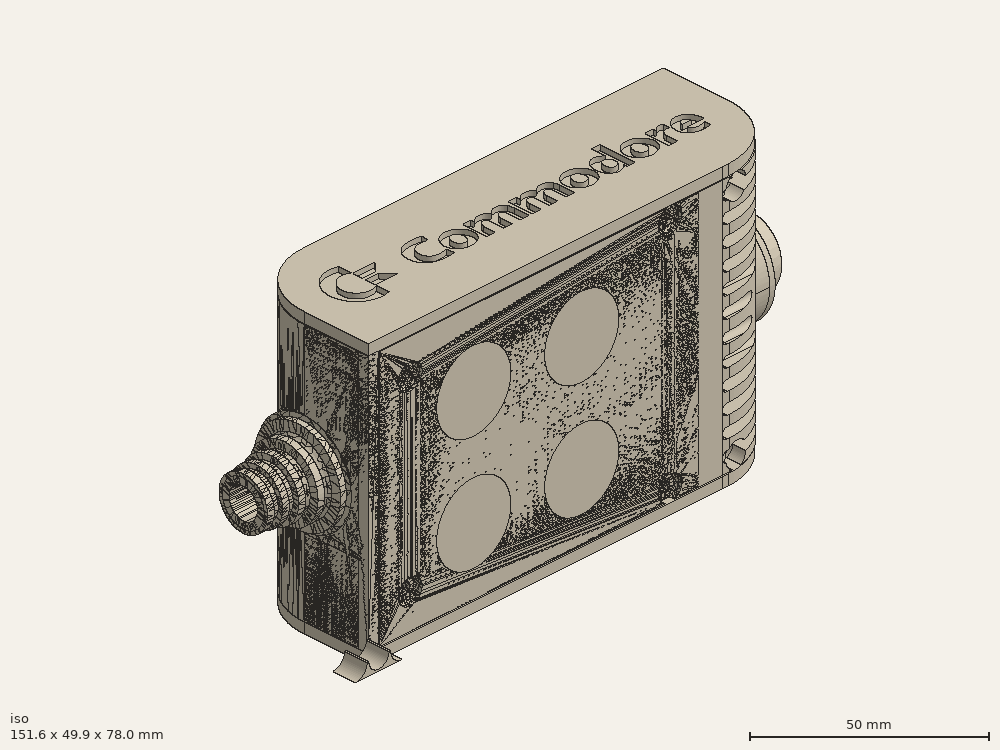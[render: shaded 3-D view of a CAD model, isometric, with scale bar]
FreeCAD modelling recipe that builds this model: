
FCSTD DOCUMENT  (FreeCAD 0.19R0.19.2)
Label: enclosure_213FCStd
License: All rights reserved
LicenseURL: http://en.wikipedia.org/wiki/All_rights_reserved
objects: Part::Revolution×152, Part::MultiFuse×146, Part::Feature×146, Sketcher::SketchObject×87, Part::Extrusion×72, Part::Cut×72, Part::Cylinder×70, Part::Fillet×58, Part::Box×36, App::MeasureDistance×4, Part::FeaturePython×2, Image::ImagePlane×1, PartDesign::Body×1, Part::Mirroring×1
note: 843 computed .brp shape members not serialized (recipe doc carries the construction recipe); baked Part::Feature solids carry a one-line shape summary decoded from their .brp

FEATURE [Sketcher::SketchObject] Sketch  label="topSketch"
  FullyConstrained = true
  sketch-geometry (20):
    g0: LineSegment StartX=5.21097e-06 StartY=3 StartZ=0 EndX=5.21097e-06 EndY=19 EndZ=0
    g1: ArcOfCircle CenterX=19 CenterY=19 CenterZ=0 NormalX=0 NormalY=0 NormalZ=1 AngleXU=0 Radius=19 StartAngle=1.5708 EndAngle=3.14159
    g2: ArcOfCircle CenterX=19 CenterY=19 CenterZ=0 NormalX=0 NormalY=0 NormalZ=1 AngleXU=0 Radius=16 StartAngle=1.5708 EndAngle=3.14159
    g3: LineSegment StartX=114 StartY=35 StartZ=0 EndX=19 EndY=35 EndZ=0
    g4: LineSegment StartX=5.21097e-06 StartY=3 StartZ=0 EndX=5.21097e-06 EndY=0 EndZ=0
    g5: LineSegment StartX=3 StartY=0 StartZ=0 EndX=5.21097e-06 EndY=0 EndZ=0
    g6: LineSegment StartX=3 StartY=19 StartZ=0 EndX=3 EndY=0 EndZ=0
    g7: LineSegment StartX=19 StartY=38 StartZ=0 EndX=124 EndY=38 EndZ=0
    g8: Circle CenterX=119 CenterY=35 CenterZ=0 NormalX=0 NormalY=0 NormalZ=1 AngleXU=0 Radius=1
    g9: Circle CenterX=121 CenterY=35 CenterZ=0 NormalX=0 NormalY=0 NormalZ=1 AngleXU=0 Radius=1
    g10: Circle CenterX=121 CenterY=33 CenterZ=0 NormalX=0 NormalY=0 NormalZ=1 AngleXU=0 Radius=1
    g11: BSplineCurve PolesCount=3 KnotsCount=2 Degree=2 IsPeriodic=0
    g12: GeomPoint X=119 Y=35 Z=0
    g13: GeomPoint X=121 Y=33 Z=0
    g14: LineSegment StartX=119 StartY=35 StartZ=0 EndX=114 EndY=35 EndZ=0
    g15: ArcOfCircle CenterX=105 CenterY=19 CenterZ=0 NormalX=0 NormalY=0 NormalZ=1 AngleXU=0 Radius=19 StartAngle=5.7297 EndAngle=6.28319
    g16: ArcOfCircle CenterX=105 CenterY=19 CenterZ=0 NormalX=0 NormalY=0 NormalZ=1 AngleXU=0 Radius=16 StartAngle=5.60905 EndAngle=6.28319
    g17: LineSegment StartX=121 StartY=33 StartZ=0 EndX=121 EndY=19 EndZ=0
    g18: LineSegment StartX=124 StartY=38 StartZ=0 EndX=124 EndY=19 EndZ=0
    g19: LineSegment StartX=117.5 StartY=9.01251 StartZ=0 EndX=121.163 EndY=9.0125 EndZ=0
  constraints (46):
    c: Vertical(g0)
    c: Block(g0)
    c: Coincident(g1,g0)
    c: Block(g1)
    c: Coincident(g2,g1)
    c: Block(g2)
    c: Coincident(g3,g2)
    c: Horizontal(g3)
    c: Tangent(g3,g2)
    c: Coincident(g4,g0)
    c: Distance(g4) = 3
    c: Vertical(g4)
    c: Coincident(g5,g4)
    c: Horizontal(g5)
    c: Coincident(g6,g2)
    c: Coincident(g6,g5)
    c: Vertical(g6)
    c: Horizontal(g7)
    c: Distance(g7) = 105
    c: Coincident(g7,g1)
    c: Block(g3)
    c: Weight(g8) = 1
    c: Equal(g8,g9)
    c: Equal(g8,g10)
    c: InternalAlignment(g8,g11)
    c: InternalAlignment(g9,g11)
    c: InternalAlignment(g10,g11)
    c: InternalAlignment(g12,g11)
    c: InternalAlignment(g13,g11)
    c: Block(g11)
    c: Coincident(g14,g11)
    c: Coincident(g14,g3)
    c: Horizontal(g14)
    c: Block(g15)
    c: Coincident(g16,g15)
    c: Block(g16)
    c: Coincident(g17,g11)
    c: Coincident(g17,g16)
    c: Vertical(g17)
    c: Distance(g17) = 14
    c: Coincident(g18,g7)
    c: Coincident(g18,g15)
    c: Vertical(g18)
    c: Distance(g18) = 19
    c: Coincident(g19,g16)
    c: Coincident(g19,g15)
FEATURE [Sketcher::SketchObject] Sketch001  label="bottomSketch"
  FullyConstrained = true
  sketch-geometry (32):
    g0: LineSegment StartX=3.3 StartY=-6.03275e-07 StartZ=0 EndX=98 EndY=-6.03275e-07 EndZ=0
    g1: ArcOfCircle CenterX=98 CenterY=19 CenterZ=0 NormalX=0 NormalY=0 NormalZ=1 AngleXU=0 Radius=19 StartAngle=4.71239 EndAngle=5.71103
    g2: LineSegment StartX=6.3 StartY=8 StartZ=0 EndX=3.3 EndY=8 EndZ=0
    g3: LineSegment StartX=3.3 StartY=8 StartZ=0 EndX=3.3 EndY=-6.03275e-07 EndZ=0
    g4: ArcOfCircle CenterX=8.3 CenterY=5 CenterZ=0 NormalX=0 NormalY=0 NormalZ=1 AngleXU=0 Radius=2 StartAngle=3.14159 EndAngle=4.71239
    g5: LineSegment StartX=6.3 StartY=8 StartZ=0 EndX=6.3 EndY=5 EndZ=0
    g6: ArcOfCircle CenterX=98 CenterY=19 CenterZ=0 NormalX=0 NormalY=0 NormalZ=1 AngleXU=0 Radius=12.7 StartAngle=4.71239 EndAngle=6.28319
    g7: LineSegment StartX=94.7 StartY=3 StartZ=0 EndX=8.3 EndY=3 EndZ=0
    g8-g12: Circle x5 (B-spline internal-alignment scaffolding for g13; pole/knot coordinates omitted)
    g13: BSplineCurve PolesCount=5 KnotsCount=3 Degree=3 IsPeriodic=0
    g14: GeomPoint X=98 Y=6.3 Z=0
    g15: GeomPoint X=96.3938 Y=4.71946 Z=0
    g16: GeomPoint X=94.7 Y=3 Z=0
    g17-g23: Circle x7 (B-spline internal-alignment scaffolding for g24; pole/knot coordinates omitted)
    g24: BSplineCurve PolesCount=7 KnotsCount=5 Degree=3 IsPeriodic=0
    g25-g29: GeomPoint x5 (B-spline internal-alignment scaffolding for g24; pole/knot coordinates omitted)
    g30: ArcOfCircle CenterX=98 CenterY=19 CenterZ=0 NormalX=0 NormalY=0 NormalZ=1 AngleXU=0 Radius=15.7 StartAngle=5.81226 EndAngle=6.28319
    g31: LineSegment StartX=110.7 StartY=19 StartZ=0 EndX=113.7 EndY=19 EndZ=0
  constraints (41):
    c: Horizontal(g0)
    c: Coincident(g1,g0)
    c: Block(g1)
    c: Horizontal(g2)
    c: Distance(g2) = 3
    c: Coincident(g3,g2)
    c: Vertical(g3)
    c: Coincident(g3,g0)
    c: Block(g4)
    c: Block(g2)
    c: Coincident(g5,g2)
    c: Coincident(g5,g4)
    c: Vertical(g5)
    c: Coincident(g6,g1)
    c: Block(g6)
    c: Coincident(g7,g4)
    c: Horizontal(g7)
    c: Block(g0)
    c: Block(g7)
    c: Block(g3)
    c: Coincident(g13,g6)
    c: Weight(g8) = 1
    c: Equal(g8, g9-g12) x4
    c: Coincident(g13,g7)
    c: InternalAlignment(g8-g12 -> g13) x5
    c: InternalAlignment(g14,g13)
    c: InternalAlignment(g15,g13)
    c: InternalAlignment(g16,g13)
    c: Block(g13)
    c: Weight(g17) = 1
    c: Equal(g17, g18-g23) x6
    c: Coincident(g24,g1)
    c: InternalAlignment(g17-g23 -> g24) x7
    c: InternalAlignment(g25-g29 -> g24) x5
    c: Block(g24)
    c: Coincident(g30,g24)
    c: Coincident(g31,g6)
    c: Coincident(g31,g30)
    c: Horizontal(g31)
    c: Block(g31)
    c: Block(g30)
FEATURE [Part::Extrusion] Extrude  label="top"
  Base = -> Sketch
  Dir = (0,0,1)
  DirMode = 2
  FaceMakerClass = Part::FaceMakerBullseye
  LengthFwd = 72
  LengthRev = 0
  Solid = true
  Symmetric = false
FEATURE [Part::Extrusion] Extrude001  label="bottom"
  Base = -> Sketch001
  Dir = (0,0,1)
  DirMode = 2
  FaceMakerClass = Part::FaceMakerBullseye
  LengthFwd = 71.4
  LengthRev = 0
  Placement = pos=(0,0,0.3) rot=(0,0,1;0rad)
  Solid = true
  Symmetric = false
FEATURE [Sketcher::SketchObject] Sketch002  label="topSketch001"
  FullyConstrained = true
  sketch-geometry (8):
    g0: ArcOfCircle CenterX=19 CenterY=19.0975 CenterZ=0 NormalX=0 NormalY=0 NormalZ=1 AngleXU=0 Radius=18.9025 StartAngle=1.5708 EndAngle=3.14674
    g1: LineSegment StartX=0.0977805 StartY=19.0003 StartZ=0 EndX=0.0977805 EndY=0.000251602 EndZ=0
    g2: LineSegment StartX=19 StartY=38 StartZ=0 EndX=124 EndY=38 EndZ=0
    g3: LineSegment StartX=0.0977805 StartY=0.000251602 StartZ=0 EndX=105.098 EndY=0.000251602 EndZ=0
    g4: LineSegment StartX=124 StartY=38 StartZ=0 EndX=125.616 EndY=38 EndZ=0
    g5: LineSegment StartX=105.098 StartY=0.000251602 StartZ=0 EndX=106.713 EndY=0.000251602 EndZ=0
    g6: ArcOfCircle CenterX=106.616 CenterY=19 CenterZ=0 NormalX=0 NormalY=0 NormalZ=1 AngleXU=0 Radius=19 StartAngle=4.71754 EndAngle=6.28319
    g7: LineSegment StartX=125.616 StartY=38 StartZ=0 EndX=125.616 EndY=19 EndZ=0
  constraints (21):
    c: Block(g0)
    c: Coincident(g1,g0)
    c: Vertical(g1)
    c: Horizontal(g2)
    c: Distance(g2) = 105
    c: Coincident(g2,g0)
    c: Distance(g1) = 19
    c: Coincident(g3,g1)
    c: Horizontal(g3)
    c: Distance(g3) = 105
    c: Coincident(g4,g2)
    c: Horizontal(g4)
    c: Distance(g4) = 1.61553
    c: Horizontal(g5)
    c: Equal(g4,g5) = 1.61553
    c: Coincident(g5,g3)
    c: Block(g6)
    c: Coincident(g6,g5)
    c: Coincident(g7,g4)
    c: Coincident(g7,g6)
    c: Vertical(g7)
FEATURE [Part::Extrusion] Extrude002  label="sideA"
  Base = -> Sketch002
  Dir = (0,0,1)
  DirMode = 2
  FaceMakerClass = Part::FaceMakerBullseye
  LengthFwd = 3
  LengthRev = 0
  Placement = pos=(0,0,-3) rot=(0,0,1;0rad)
  Solid = true
  Symmetric = false
FEATURE [Sketcher::SketchObject] Sketch003  label="topSketch002"
  FullyConstrained = true
  sketch-geometry (6):
    g0: LineSegment StartX=19 StartY=38 StartZ=0 EndX=117 EndY=38 EndZ=0
    g1: ArcOfCircle CenterX=19 CenterY=19 CenterZ=0 NormalX=0 NormalY=0 NormalZ=1 AngleXU=0 Radius=19 StartAngle=1.5708 EndAngle=3.14159
    g2: LineSegment StartX=117 StartY=38 StartZ=0 EndX=117 EndY=19 EndZ=0
    g3: LineSegment StartX=98 StartY=1.0161e-12 StartZ=0 EndX=5.22862e-06 EndY=1.0161e-12 EndZ=0
    g4: LineSegment StartX=5.22862e-06 StartY=19 StartZ=0 EndX=5.22862e-06 EndY=1.0161e-12 EndZ=0
    g5: ArcOfCircle CenterX=98 CenterY=19 CenterZ=0 NormalX=0 NormalY=0 NormalZ=1 AngleXU=0 Radius=19 StartAngle=4.71239 EndAngle=6.28319
  constraints (16):
    c: Horizontal(g0)
    c: Distance(g0) = 98
    c: Coincident(g1,g0)
    c: Block(g1)
    c: Coincident(g2,g0)
    c: Vertical(g2)
    c: Distance(g2) = 19
    c: Horizontal(g3)
    c: Coincident(g4,g1)
    c: Vertical(g4)
    c: Coincident(g3,g4)
    c: Block(g3)
    c: Coincident(g5,g2)
    c: Coincident(g5,g3)
    c: Block(g0)
    c: Block(g5)
FEATURE [Sketcher::SketchObject] Sketch004
  FullyConstrained = true
  MapMode = 3
  Placement = pos=(0,0,0) rot=(1,0,0;1.5708rad)
  Support = -> [Extrude]
  sketch-geometry (8):
    g0: Circle CenterX=80.351 CenterY=-67.6202 CenterZ=0 NormalX=0 NormalY=0 NormalZ=1 AngleXU=0 Radius=2
    g1: Circle CenterX=80.351 CenterY=-67.6202 CenterZ=0 NormalX=0 NormalY=0 NormalZ=1 AngleXU=0 Radius=3
    g2: Circle CenterX=80.351 CenterY=-4.92017 CenterZ=0 NormalX=0 NormalY=0 NormalZ=1 AngleXU=0 Radius=2
    g3: Circle CenterX=80.351 CenterY=-4.92017 CenterZ=0 NormalX=0 NormalY=0 NormalZ=1 AngleXU=0 Radius=3
    g4: Circle CenterX=23.851 CenterY=-4.92017 CenterZ=0 NormalX=0 NormalY=0 NormalZ=1 AngleXU=0 Radius=2
    g5: Circle CenterX=23.851 CenterY=-4.92017 CenterZ=0 NormalX=0 NormalY=0 NormalZ=1 AngleXU=0 Radius=3
    g6: Circle CenterX=23.851 CenterY=-67.6202 CenterZ=0 NormalX=0 NormalY=0 NormalZ=1 AngleXU=0 Radius=2
    g7: Circle CenterX=23.851 CenterY=-67.6202 CenterZ=0 NormalX=0 NormalY=0 NormalZ=1 AngleXU=0 Radius=3
  constraints (8):
    c: Block(g3)
    c: Block(g2)
    c: Block(g1)
    c: Block(g0)
    c: Block(g6)
    c: Block(g7)
    c: Block(g4)
    c: Block(g5)
FEATURE [Part::Extrusion] Extrude004
  Base = -> Sketch004
  Dir = (0,-1,2e-16)
  DirMode = 2
  FaceMakerClass = Part::FaceMakerBullseye
  LengthFwd = 6
  LengthRev = 0
  Placement = pos=(0,9,0) rot=(0,0,1;0rad)
  Solid = true
  Symmetric = false
FEATURE [Sketcher::SketchObject] Sketch005
  FullyConstrained = true
  MapMode = 3
  Placement = pos=(0,0,0) rot=(1,0,0;1.5708rad)
  Support = -> [Extrude]
  sketch-geometry (8):
    g0: Circle CenterX=80.351 CenterY=-67.6202 CenterZ=0 NormalX=0 NormalY=0 NormalZ=1 AngleXU=0 Radius=3
    g1: Circle CenterX=80.351 CenterY=-4.92017 CenterZ=0 NormalX=0 NormalY=0 NormalZ=1 AngleXU=0 Radius=3
    g2: Circle CenterX=23.851 CenterY=-4.92017 CenterZ=0 NormalX=0 NormalY=0 NormalZ=1 AngleXU=0 Radius=3
    g3: Circle CenterX=23.851 CenterY=-67.6202 CenterZ=0 NormalX=0 NormalY=0 NormalZ=1 AngleXU=0 Radius=3
    g4: Circle CenterX=23.851 CenterY=-67.6202 CenterZ=0 NormalX=0 NormalY=0 NormalZ=1 AngleXU=0 Radius=5
    g5: Circle CenterX=80.351 CenterY=-67.6202 CenterZ=0 NormalX=0 NormalY=0 NormalZ=1 AngleXU=0 Radius=5
    g6: Circle CenterX=23.851 CenterY=-4.92017 CenterZ=0 NormalX=0 NormalY=0 NormalZ=1 AngleXU=0 Radius=5
    g7: Circle CenterX=80.351 CenterY=-4.92017 CenterZ=0 NormalX=0 NormalY=0 NormalZ=1 AngleXU=0 Radius=5
  constraints (8):
    c: Block(g1)
    c: Block(g0)
    c: Block(g3)
    c: Block(g2)
    c: Block(g5)
    c: Block(g4)
    c: Block(g6)
    c: Block(g7)
FEATURE [Part::Extrusion] Extrude005
  Base = -> Sketch005
  Dir = (0,-1,2e-16)
  DirMode = 2
  FaceMakerClass = Part::FaceMakerBullseye
  LengthFwd = 2
  LengthRev = 0
  Solid = true
  Symmetric = false
FEATURE [Sketcher::SketchObject] Sketch006
  FullyConstrained = true
  MapMode = 3
  Placement = pos=(0,0,0) rot=(1,0,0;1.5708rad)
  sketch-geometry (8):
    g0: Circle CenterX=80.351 CenterY=-67.6202 CenterZ=0 NormalX=0 NormalY=0 NormalZ=1 AngleXU=0 Radius=3
    g1: Circle CenterX=80.351 CenterY=-4.92017 CenterZ=0 NormalX=0 NormalY=0 NormalZ=1 AngleXU=0 Radius=3
    g2: Circle CenterX=23.851 CenterY=-4.92017 CenterZ=0 NormalX=0 NormalY=0 NormalZ=1 AngleXU=0 Radius=3
    g3: Circle CenterX=23.851 CenterY=-67.6202 CenterZ=0 NormalX=0 NormalY=0 NormalZ=1 AngleXU=0 Radius=3
    g4: Circle CenterX=23.851 CenterY=-67.6202 CenterZ=0 NormalX=0 NormalY=0 NormalZ=1 AngleXU=0 Radius=5
    g5: Circle CenterX=80.351 CenterY=-67.6202 CenterZ=0 NormalX=0 NormalY=0 NormalZ=1 AngleXU=0 Radius=5
    g6: Circle CenterX=23.851 CenterY=-4.92017 CenterZ=0 NormalX=0 NormalY=0 NormalZ=1 AngleXU=0 Radius=5
    g7: Circle CenterX=80.351 CenterY=-4.92017 CenterZ=0 NormalX=0 NormalY=0 NormalZ=1 AngleXU=0 Radius=5
  constraints (8):
    c: Block(g1)
    c: Block(g0)
    c: Block(g3)
    c: Block(g2)
    c: Block(g5)
    c: Block(g4)
    c: Block(g6)
    c: Block(g7)
FEATURE [Part::Extrusion] Extrude007
  Base = -> Sketch006
  Dir = (0,-1,2e-16)
  DirMode = 2
  FaceMakerClass = Part::FaceMakerBullseye
  LengthFwd = 2
  LengthRev = 0
  Solid = true
  Symmetric = false
FEATURE [Part::Fillet] Fillet
  Base = -> Extrude007
  Edges = 4 edges r=1.99: [Edge6,Edge12,Edge18,Edge24]
FEATURE [Part::Cut] Cut
  Base = -> Extrude005
  Placement = pos=(0,5,0) rot=(0,0,1;0rad)
  Tool = -> Fillet
FEATURE [Part::MultiFuse] Fusion  label="pCBScrews"
  Placement = pos=(-2.5,0,72.3) rot=(0,0,1;0rad)
  Shapes = -> [Extrude004,Cut]
FEATURE [App::MeasureDistance] Distance  label="Distance: 0.69 mm"
  Distance = 0.685967
  P1 = (24.0138,2.9647,0.3)
  P2 = (23.8901,3,-0.373787)
FEATURE [App::MeasureDistance] Distance001  label="Distance: 0.53 mm"
  Distance = 0.533607
  P1 = (80.2939,3,72.2334)
  P2 = (80.281,2.99661,71.7)
FEATURE [Part::Fillet] Fillet001
  Base = -> Extrude001
  Edges = 1 edges r=2.4: [Edge17]
FEATURE [Part::Fillet] Fillet002  label="bottom001"
  Base = -> Fillet001
  Edges = 1 edges r=2.4: [Edge36]
FEATURE [Part::Fillet] Fillet003  label="top001"
  Base = -> Extrude
  Edges = 1 edges r=2: [Edge1]
FEATURE [Sketcher::SketchObject] Sketch007
  FullyConstrained = true
  sketch-geometry (16):
    g0: LineSegment StartX=4 StartY=0 StartZ=0 EndX=4 EndY=2.4 EndZ=0
    g1: LineSegment StartX=4 StartY=2.4 StartZ=0 EndX=7 EndY=2.4 EndZ=0
    g2: LineSegment StartX=4 StartY=0 StartZ=0 EndX=5.7 EndY=0 EndZ=0
    g3: LineSegment StartX=5.7 StartY=0 StartZ=0 EndX=5.7 EndY=-5.6 EndZ=0
    g4-g8: Circle x5 (B-spline internal-alignment scaffolding for g9; pole/knot coordinates omitted)
    g9: BSplineCurve PolesCount=5 KnotsCount=3 Degree=3 IsPeriodic=0
    g10: GeomPoint X=7 Y=2.4 Z=0
    g11: GeomPoint X=10.4582 Y=-1.55472 Z=0
    g12: GeomPoint X=14 Y=-5.6 Z=0
    g13: LineSegment StartX=14 StartY=-5.6 StartZ=0 EndX=14 EndY=-14.1 EndZ=0
    g14: LineSegment StartX=14 StartY=-14.1 StartZ=0 EndX=6.5 EndY=-14.1 EndZ=0
    g15: LineSegment StartX=5.7 StartY=-5.6 StartZ=0 EndX=6.5 EndY=-14.1 EndZ=0
  constraints (28):
    c: Distance(g0) = 2.4
    c: Vertical(g0)
    c: Block(g0)
    c: Coincident(g1,g0)
    c: Horizontal(g1)
    c: Distance(g1) = 3
    c: Coincident(g2,g0)
    c: Horizontal(g2)
    c: Distance(g2) = 1.7
    c: Coincident(g3,g2)
    c: Vertical(g3)
    c: Distance(g3) = 5.6
    c: Coincident(g9,g1)
    c: Weight(g4) = 1
    c: Equal(g4, g5-g8) x4
    c: InternalAlignment(g4-g8 -> g9) x5
    c: InternalAlignment(g10,g9)
    c: InternalAlignment(g11,g9)
    c: InternalAlignment(g12,g9)
    c: Block(g9)
    c: Coincident(g13,g9)
    c: Vertical(g13)
    c: Distance(g13) = 8.5
    c: Coincident(g14,g13)
    c: Horizontal(g14)
    c: Distance(g14) = 7.5
    c: Coincident(g15,g3)
    c: Coincident(g15,g14)
FEATURE [Part::Feature] Face
  shape: bbox 10 x 16.5 x 2e-07 mm, 1 faces, 0 solids (baked)
FEATURE [Part::Revolution] Revolve  label="plugHousing"
  Angle = 360
  Axis = (0,1,0)
  Base = (0,0,0)
  FaceMakerClass = Part::FaceMakerBullseye
  Placement = pos=(0,0,36.15) rot=(0,0,1;0rad)
  Solid = false
  Source = -> Face
  Symmetric = false
FEATURE [Part::Feature] Face001
  shape: bbox 10 x 16.5 x 2e-07 mm, 1 faces, 0 solids (baked)
FEATURE [Part::Revolution] Revolve001  label="plugHousing001"
  Angle = 360
  Axis = (0,1,0)
  Base = (0,0,0)
  FaceMakerClass = Part::FaceMakerBullseye
  Placement = pos=(0,0,36.15) rot=(0,0,1;0rad)
  Solid = false
  Source = -> Face001
  Symmetric = false
FEATURE [Part::MultiFuse] Fusion001  label="plugHousing002"
  Placement = pos=(0,0,0) rot=(0,0,1;1.5708rad)
  Shapes = -> [Revolve001,Revolve]
FEATURE [Part::Feature] Face002
  shape: bbox 10 x 16.5 x 2e-07 mm, 1 faces, 0 solids (baked)
FEATURE [Part::Revolution] Revolve003  label="plugHousing005"
  Angle = 360
  Axis = (0,1,0)
  Base = (0,0,0)
  FaceMakerClass = Part::FaceMakerBullseye
  Placement = pos=(0,0,36.15) rot=(0,0,1;0rad)
  Solid = false
  Source = -> Face002
  Symmetric = false
FEATURE [Part::Feature] Face003
  shape: bbox 10 x 16.5 x 2e-07 mm, 1 faces, 0 solids (baked)
FEATURE [Part::Revolution] Revolve002  label="plugHousing003"
  Angle = 360
  Axis = (0,1,0)
  Base = (0,0,0)
  FaceMakerClass = Part::FaceMakerBullseye
  Placement = pos=(0,0,36.15) rot=(0,0,1;0rad)
  Solid = false
  Source = -> Face003
  Symmetric = false
FEATURE [Part::MultiFuse] Fusion002  label="plugHousing004"
  Placement = pos=(0,0,0) rot=(0,0,1;1.5708rad)
  Shapes = -> [Revolve002,Revolve003]
FEATURE [Part::MultiFuse] Fusion003  label="plugHousing006"
  Placement = pos=(0,19,0) rot=(0,0,1;3.14159rad)
  Shapes = -> [Fusion002,Fusion001]
FEATURE [Part::Feature] Face004
  shape: bbox 10 x 16.5 x 2e-07 mm, 1 faces, 0 solids (baked)
FEATURE [Part::Revolution] Revolve006  label="plugHousing010"
  Angle = 360
  Axis = (0,1,0)
  Base = (0,0,0)
  FaceMakerClass = Part::FaceMakerBullseye
  Placement = pos=(0,0,36.15) rot=(0,0,1;0rad)
  Solid = false
  Source = -> Face004
  Symmetric = false
FEATURE [Part::Feature] Face005
  shape: bbox 10 x 16.5 x 2e-07 mm, 1 faces, 0 solids (baked)
FEATURE [Part::Revolution] Revolve007  label="plugHousing011"
  Angle = 360
  Axis = (0,1,0)
  Base = (0,0,0)
  FaceMakerClass = Part::FaceMakerBullseye
  Placement = pos=(0,0,36.15) rot=(0,0,1;0rad)
  Solid = false
  Source = -> Face005
  Symmetric = false
FEATURE [Part::Feature] Face006
  shape: bbox 10 x 16.5 x 2e-07 mm, 1 faces, 0 solids (baked)
FEATURE [Part::Revolution] Revolve004  label="plugHousing007"
  Angle = 360
  Axis = (0,1,0)
  Base = (0,0,0)
  FaceMakerClass = Part::FaceMakerBullseye
  Placement = pos=(0,0,36.15) rot=(0,0,1;0rad)
  Solid = false
  Source = -> Face006
  Symmetric = false
FEATURE [Part::MultiFuse] Fusion004  label="plugHousing009"
  Placement = pos=(0,0,0) rot=(0,0,1;1.5708rad)
  Shapes = -> [Revolve004,Revolve007]
FEATURE [Part::Feature] Face007
  shape: bbox 10 x 16.5 x 2e-07 mm, 1 faces, 0 solids (baked)
FEATURE [Part::Revolution] Revolve005  label="plugHousing008"
  Angle = 360
  Axis = (0,1,0)
  Base = (0,0,0)
  FaceMakerClass = Part::FaceMakerBullseye
  Placement = pos=(0,0,36.15) rot=(0,0,1;0rad)
  Solid = false
  Source = -> Face007
  Symmetric = false
FEATURE [Part::MultiFuse] Fusion005  label="plugHousing012"
  Placement = pos=(0,0,0) rot=(0,0,1;1.5708rad)
  Shapes = -> [Revolve006,Revolve005]
FEATURE [Part::MultiFuse] Fusion006  label="plugHousing013"
  Placement = pos=(0,19,0) rot=(0,0,1;3.14159rad)
  Shapes = -> [Fusion005,Fusion004]
FEATURE [Part::MultiFuse] Fusion007  label="plugHousing014"
  Placement = pos=(122.621,0,-0.15) rot=(0,0,1;0rad)
  Shapes = -> [Fusion003,Fusion006]
FEATURE [Part::Cylinder] Cylinder002
  Angle = 360
  AttacherType = Attacher::AttachEngine3D
  Height = 20
  Placement = pos=(0,0,36.15) rot=(0,0,1;0rad)
  Radius = 4
FEATURE [Part::Cylinder] Cylinder003
  Angle = 360
  AttacherType = Attacher::AttachEngine3D
  Height = 10
  Placement = pos=(0,0,36.15) rot=(0,0,1;0rad)
  Radius = 4
FEATURE [Part::MultiFuse] Fusion009  label="removeToCreateHoleForPlugHousing"
  Placement = pos=(70,19,36.15) rot=(0,1,0;1.5708rad)
  Shapes = -> [Cylinder002,Cylinder003]
FEATURE [Part::Cylinder] Cylinder004
  Angle = 360
  AttacherType = Attacher::AttachEngine3D
  Height = 20
  Placement = pos=(0,0,36.15) rot=(0,0,1;0rad)
  Radius = 4
FEATURE [Part::Cylinder] Cylinder005
  Angle = 360
  AttacherType = Attacher::AttachEngine3D
  Height = 10
  Placement = pos=(0,0,36.15) rot=(0,0,1;0rad)
  Radius = 4
FEATURE [Part::MultiFuse] Fusion010  label="removeToCreateHoleForPlugHousing001"
  Placement = pos=(70,19,36.15) rot=(0,1,0;1.5708rad)
  Shapes = -> [Cylinder004,Cylinder005]
FEATURE [Part::Cut] Cut001
  Base = -> Fillet003
  Tool = -> Fusion010
FEATURE [Part::Cut] Cut002  label="Bottom"
  Base = -> Fillet002
  Tool = -> Fusion009
FEATURE [Part::Feature] Face008
  shape: bbox 10 x 16.5 x 2e-07 mm, 1 faces, 0 solids (baked)
FEATURE [Part::Revolution] Revolve011  label="plugHousing021"
  Angle = 360
  Axis = (0,1,0)
  Base = (0,0,0)
  FaceMakerClass = Part::FaceMakerBullseye
  Placement = pos=(0,0,36.15) rot=(0,0,1;0rad)
  Solid = false
  Source = -> Face008
  Symmetric = false
FEATURE [Part::Feature] Face009
  shape: bbox 10 x 16.5 x 2e-07 mm, 1 faces, 0 solids (baked)
FEATURE [Part::Revolution] Revolve012  label="plugHousing022"
  Angle = 360
  Axis = (0,1,0)
  Base = (0,0,0)
  FaceMakerClass = Part::FaceMakerBullseye
  Placement = pos=(0,0,36.15) rot=(0,0,1;0rad)
  Solid = false
  Source = -> Face009
  Symmetric = false
FEATURE [Part::Feature] Face010 .. Face013  x4 (patterned run collapsed; names and placements below)
  shape: bbox 10 x 16.5 x 2e-07 mm, 1 faces, 0 solids (baked)
FEATURE [Part::Revolution] Revolve015  label="plugHousing027"
  Angle = 360
  Axis = (0,1,0)
  Base = (0,0,0)
  FaceMakerClass = Part::FaceMakerBullseye
  Placement = pos=(0,0,36.15) rot=(0,0,1;0rad)
  Solid = false
  Source = -> Face013
  Symmetric = false
FEATURE [Part::Feature] Face014
  shape: bbox 10 x 16.5 x 2e-07 mm, 1 faces, 0 solids (baked)
FEATURE [Part::Feature] Face015
  shape: bbox 10 x 16.5 x 2e-07 mm, 1 faces, 0 solids (baked)
FEATURE [Part::Feature] Face016
  shape: bbox 10 x 16.5 x 2e-07 mm, 1 faces, 0 solids (baked)
FEATURE [Part::Revolution] Revolve019  label="plugHousing033"
  Angle = 360
  Axis = (0,1,0)
  Base = (0,0,0)
  FaceMakerClass = Part::FaceMakerBullseye
  Placement = pos=(0,0,36.15) rot=(0,0,1;0rad)
  Solid = false
  Source = -> Face016
  Symmetric = false
FEATURE [Part::Feature] Face017
  shape: bbox 10 x 16.5 x 2e-07 mm, 1 faces, 0 solids (baked)
FEATURE [Part::Revolution] Revolve020  label="plugHousing034"
  Angle = 360
  Axis = (0,1,0)
  Base = (0,0,0)
  FaceMakerClass = Part::FaceMakerBullseye
  Placement = pos=(0,0,36.15) rot=(0,0,1;0rad)
  Solid = false
  Source = -> Face017
  Symmetric = false
FEATURE [Part::Feature] Face018
  shape: bbox 10 x 16.5 x 2e-07 mm, 1 faces, 0 solids (baked)
FEATURE [Part::Revolution] Revolve016  label="plugHousing030"
  Angle = 360
  Axis = (0,1,0)
  Base = (0,0,0)
  FaceMakerClass = Part::FaceMakerBullseye
  Placement = pos=(0,0,36.15) rot=(0,0,1;0rad)
  Solid = false
  Source = -> Face018
  Symmetric = false
FEATURE [Part::MultiFuse] Fusion020  label="plugHousing038"
  Placement = pos=(0,0,0) rot=(0,0,1;1.5708rad)
  Shapes = -> [Revolve016,Revolve020]
FEATURE [Part::Feature] Face019
  shape: bbox 10 x 16.5 x 2e-07 mm, 1 faces, 0 solids (baked)
FEATURE [Part::Feature] Face020
  shape: bbox 10 x 16.5 x 2e-07 mm, 1 faces, 0 solids (baked)
FEATURE [Part::Revolution] Revolve017  label="plugHousing031"
  Angle = 360
  Axis = (0,1,0)
  Base = (0,0,0)
  FaceMakerClass = Part::FaceMakerBullseye
  Placement = pos=(0,0,36.15) rot=(0,0,1;0rad)
  Solid = false
  Source = -> Face020
  Symmetric = false
FEATURE [Part::MultiFuse] Fusion021  label="plugHousing039"
  Placement = pos=(0,0,0) rot=(0,0,1;1.5708rad)
  Shapes = -> [Revolve019,Revolve017]
FEATURE [Part::MultiFuse] Fusion023  label="plugHousing041"
  Placement = pos=(0,19,0) rot=(0,0,1;3.14159rad)
  Shapes = -> [Fusion021,Fusion020]
FEATURE [Part::Revolution] Revolve022  label="plugHousing043"
  Angle = 360
  Axis = (0,1,0)
  Base = (0,0,0)
  FaceMakerClass = Part::FaceMakerBullseye
  Placement = pos=(0,0,36.15) rot=(0,0,1;0rad)
  Solid = false
  Source = -> Face019
  Symmetric = false
FEATURE [Part::Feature] Face021
  shape: bbox 10 x 16.5 x 2e-07 mm, 1 faces, 0 solids (baked)
FEATURE [Part::Revolution] Revolve023  label="plugHousing044"
  Angle = 360
  Axis = (0,1,0)
  Base = (0,0,0)
  FaceMakerClass = Part::FaceMakerBullseye
  Placement = pos=(0,0,36.15) rot=(0,0,1;0rad)
  Solid = false
  Source = -> Face021
  Symmetric = false
FEATURE [Part::Feature] Face022
  shape: bbox 10 x 16.5 x 2e-07 mm, 1 faces, 0 solids (baked)
FEATURE [Part::Revolution] Revolve018  label="plugHousing032"
  Angle = 360
  Axis = (0,1,0)
  Base = (0,0,0)
  FaceMakerClass = Part::FaceMakerBullseye
  Placement = pos=(0,0,36.15) rot=(0,0,1;0rad)
  Solid = false
  Source = -> Face022
  Symmetric = false
FEATURE [Part::MultiFuse] Fusion022  label="plugHousing040"
  Placement = pos=(0,0,0) rot=(0,0,1;1.5708rad)
  Shapes = -> [Revolve018,Revolve023]
FEATURE [Part::Feature] Face023
  shape: bbox 10 x 16.5 x 2e-07 mm, 1 faces, 0 solids (baked)
FEATURE [Part::Revolution] Revolve021  label="plugHousing035"
  Angle = 360
  Axis = (0,1,0)
  Base = (0,0,0)
  FaceMakerClass = Part::FaceMakerBullseye
  Placement = pos=(0,0,36.15) rot=(0,0,1;0rad)
  Solid = false
  Source = -> Face023
  Symmetric = false
FEATURE [Part::MultiFuse] Fusion018  label="plugHousing036"
  Placement = pos=(0,0,0) rot=(0,0,1;1.5708rad)
  Shapes = -> [Revolve022,Revolve021]
FEATURE [Part::MultiFuse] Fusion019  label="plugHousing037"
  Placement = pos=(0,19,0) rot=(0,0,1;3.14159rad)
  Shapes = -> [Fusion018,Fusion022]
FEATURE [Part::MultiFuse] Fusion024  label="plugHousing042"
  Placement = pos=(122.621,0,-0.15) rot=(0,0,1;0rad)
  Shapes = -> [Fusion023,Fusion019]
FEATURE [Part::Cylinder] Cylinder006
  Angle = 360
  AttacherType = Attacher::AttachEngine3D
  Height = 20
  Placement = pos=(0,0,36.15) rot=(0,0,1;0rad)
  Radius = 14.3
FEATURE [Part::Cylinder] Cylinder007
  Angle = 360
  AttacherType = Attacher::AttachEngine3D
  Height = 10
  Placement = pos=(0,0,36.15) rot=(0,0,1;0rad)
  Radius = 4
FEATURE [Part::MultiFuse] Fusion026  label="removeToCreteHoleForPlugHousing"
  Placement = pos=(70,19,36) rot=(0,1,0;1.5708rad)
  Shapes = -> [Cylinder006,Cylinder007]
FEATURE [Part::Box] Box001  label="Cube001"
  AttacherType = Attacher::AttachEngine3D
  Height = 28
  Length = 3
  Placement = pos=(110.7,19,22) rot=(0,0,1;0rad)
  Width = 15.7
FEATURE [Part::Cut] Cut003  label="top002"
  Base = -> Cut001
  Tool = -> Fusion007
FEATURE [Part::Revolution] Revolve008  label="plugHousing015"
  Angle = 360
  Axis = (0,1,0)
  Base = (0,0,0)
  FaceMakerClass = Part::FaceMakerBullseye
  Placement = pos=(0,0,36.15) rot=(0,0,1;0rad)
  Solid = false
  Source = -> Face010
  Symmetric = false
FEATURE [Part::MultiFuse] Fusion013  label="plugHousing020"
  Placement = pos=(0,0,0) rot=(0,0,1;1.5708rad)
  Shapes = -> [Revolve008,Revolve012]
FEATURE [Part::Cut] Cut004  label="top003"
  Base = -> Cut003
  Placement = pos=(1,0,0) rot=(0,0,1;0rad)
  Tool = -> Fusion026
FEATURE [Part::Cylinder] Cylinder008
  Angle = 360
  AttacherType = Attacher::AttachEngine3D
  Height = 20
  Placement = pos=(0,0,36.15) rot=(0,0,1;0rad)
  Radius = 10.3
FEATURE [Part::Cylinder] Cylinder009
  Angle = 360
  AttacherType = Attacher::AttachEngine3D
  Height = 10
  Placement = pos=(0,0,36.15) rot=(0,0,1;0rad)
  Radius = 4
FEATURE [Part::MultiFuse] Fusion027  label="removeToCreteHoleForPlugHousing001"
  Placement = pos=(70,19,36) rot=(0,1,0;1.5708rad)
  Shapes = -> [Cylinder008,Cylinder009]
FEATURE [Part::Cut] Cut005  label="plugHousingTab"
  Base = -> Box001
  Tool = -> Fusion027
FEATURE [Part::MultiFuse] Fusion028  label="plugHousing045"
  Shapes = -> [Fusion024,Cut005]
FEATURE [Part::Box] Box002  label="Cube002"
  AttacherType = Attacher::AttachEngine3D
  Height = 28.8
  Length = 3
  Placement = pos=(107.3,28,21.6) rot=(0,0,1;0rad)
  Width = 7
FEATURE [Part::Box] Box003  label="Cube003"
  AttacherType = Attacher::AttachEngine3D
  Height = 3
  Length = 6.4
  Placement = pos=(107.3,28,18.6) rot=(0,0,1;0rad)
  Width = 7
FEATURE [Part::Box] Box004  label="Cube004"
  AttacherType = Attacher::AttachEngine3D
  Height = 3
  Length = 6.4
  Placement = pos=(107.3,28,50.4) rot=(0,0,1;0rad)
  Width = 7
FEATURE [Part::MultiFuse] Fusion029  label="plugHousingBracketHolder"
  Shapes = -> [Box004,Box002,Box003]
FEATURE [Part::Cylinder] Cylinder010
  Angle = 360
  AttacherType = Attacher::AttachEngine3D
  Height = 20
  Placement = pos=(0,0,36.15) rot=(0,0,1;0rad)
  Radius = 14.3
FEATURE [Part::Cylinder] Cylinder011
  Angle = 360
  AttacherType = Attacher::AttachEngine3D
  Height = 10
  Placement = pos=(0,0,36.15) rot=(0,0,1;0rad)
  Radius = 4
FEATURE [Part::MultiFuse] Fusion030  label="removeToCreteHoleForPlugHousing002"
  Placement = pos=(70,19,36) rot=(0,1,0;1.5708rad)
  Shapes = -> [Cylinder010,Cylinder011]
FEATURE [Part::Cut] Cut006  label="plugHousingBracketHolder001"
  Base = -> Fusion029
  Tool = -> Fusion030
FEATURE [Part::Cylinder] Cylinder012
  Angle = 360
  AttacherType = Attacher::AttachEngine3D
  Height = 20
  Placement = pos=(0,0,36.15) rot=(0,0,1;0rad)
  Radius = 7
FEATURE [Part::Cylinder] Cylinder013
  Angle = 360
  AttacherType = Attacher::AttachEngine3D
  Height = 10
  Placement = pos=(0,0,36.15) rot=(0,0,1;0rad)
  Radius = 4
FEATURE [Part::MultiFuse] Fusion032  label="removeToCreteHoleForPlugHousing003"
  Placement = pos=(70,19,36) rot=(0,1,0;1.5708rad)
  Shapes = -> [Cylinder012,Cylinder013]
FEATURE [Part::Cut] Cut007  label="bottom002"
  Base = -> Cut002
  Tool = -> Fusion032
FEATURE [Sketcher::SketchObject] Sketch008
  FullyConstrained = true
  sketch-geometry (54):
    g0: LineSegment StartX=-4.2 StartY=0 StartZ=0 EndX=-6.2 EndY=0 EndZ=0
    g1: LineSegment StartX=-14 StartY=-18 StartZ=0 EndX=-14 EndY=-26.5 EndZ=0
    g2: LineSegment StartX=-4.2 StartY=0 StartZ=0 EndX=-4.2 EndY=-13.4877 EndZ=0
    g3: Circle CenterX=-4.2 CenterY=-13.4877 CenterZ=0 NormalX=0 NormalY=0 NormalZ=1 AngleXU=0 Radius=1
    g4: Circle CenterX=-4.2 CenterY=-26.5 CenterZ=0 NormalX=0 NormalY=0 NormalZ=1 AngleXU=0 Radius=1
    g5: Circle CenterX=-8.2 CenterY=-26.5 CenterZ=0 NormalX=0 NormalY=0 NormalZ=1 AngleXU=0 Radius=1
    g6: BSplineCurve PolesCount=3 KnotsCount=2 Degree=2 IsPeriodic=0
    g7: GeomPoint X=-4.2 Y=-13.4877 Z=0
    g8: GeomPoint X=-8.2 Y=-26.5 Z=0
    g9: LineSegment StartX=-14 StartY=-26.5 StartZ=0 EndX=-8.2 EndY=-26.5 EndZ=0
    g10: LineSegment StartX=-10.15 StartY=-12 StartZ=0 EndX=-10.15 EndY=-14 EndZ=0
    g11: LineSegment StartX=-12.8401 StartY=-16 StartZ=0 EndX=-10.1571 EndY=-16 EndZ=0
    g12: LineSegment StartX=-10.15 StartY=-14 StartZ=0 EndX=-8.70761 EndY=-14 EndZ=0
    g13: LineSegment StartX=-12.8401 StartY=-16 StartZ=0 EndX=-12.8401 EndY=-17.6958 EndZ=0
    g14: LineSegment StartX=-10.15 StartY=-12 StartZ=0 EndX=-7.79258 EndY=-12 EndZ=0
    g15: Circle CenterX=-6.2215 CenterY=-2 CenterZ=0 NormalX=0 NormalY=0 NormalZ=1 AngleXU=0 Radius=1
    g16: Circle CenterX=-6.22762 CenterY=-2.58724 CenterZ=0 NormalX=0 NormalY=0 NormalZ=1 AngleXU=0 Radius=1
    g17: Circle CenterX=-6.32538 CenterY=-4 CenterZ=0 NormalX=0 NormalY=0 NormalZ=1 AngleXU=0 Radius=1
    g18: BSplineCurve PolesCount=3 KnotsCount=2 Degree=2 IsPeriodic=0
    g19: GeomPoint X=-6.2215 Y=-2 Z=0
    g20: GeomPoint X=-6.32538 Y=-4 Z=0
    g21: Circle CenterX=-6.48644 CenterY=-5.99526 CenterZ=0 NormalX=0 NormalY=0 NormalZ=1 AngleXU=0 Radius=1
    g22: Circle CenterX=-6.58486 CenterY=-6.99526 CenterZ=0 NormalX=0 NormalY=0 NormalZ=1 AngleXU=0 Radius=1
    g23: Circle CenterX=-6.77343 CenterY=-8 CenterZ=0 NormalX=0 NormalY=0 NormalZ=1 AngleXU=0 Radius=1
    g24: BSplineCurve PolesCount=3 KnotsCount=2 Degree=2 IsPeriodic=0
    g25: GeomPoint X=-6.48644 Y=-5.99526 Z=0
    g26: GeomPoint X=-6.77343 Y=-8 Z=0
    g27: Circle CenterX=-7.19003 CenterY=-10 CenterZ=0 NormalX=0 NormalY=0 NormalZ=1 AngleXU=0 Radius=1
    g28: Circle CenterX=-7.44407 CenterY=-11.0915 CenterZ=0 NormalX=0 NormalY=0 NormalZ=1 AngleXU=0 Radius=1
    g29: Circle CenterX=-7.79258 CenterY=-12 CenterZ=0 NormalX=0 NormalY=0 NormalZ=1 AngleXU=0 Radius=1
    g30: BSplineCurve PolesCount=3 KnotsCount=2 Degree=2 IsPeriodic=0
    g31: GeomPoint X=-7.19003 Y=-10 Z=0
    g32: GeomPoint X=-7.79258 Y=-12 Z=0
    g33: Circle CenterX=-8.70761 CenterY=-14 CenterZ=0 NormalX=0 NormalY=0 NormalZ=1 AngleXU=0 Radius=1
    g34: Circle CenterX=-9.33087 CenterY=-15.1837 CenterZ=0 NormalX=0 NormalY=0 NormalZ=1 AngleXU=0 Radius=1
    g35: Circle CenterX=-10.1571 CenterY=-16 CenterZ=0 NormalX=0 NormalY=0 NormalZ=1 AngleXU=0 Radius=1
    g36: BSplineCurve PolesCount=3 KnotsCount=2 Degree=2 IsPeriodic=0
    g37: GeomPoint X=-8.70761 Y=-14 Z=0
    g38: GeomPoint X=-10.1571 Y=-16 Z=0
    g39: Circle CenterX=-12.8401 CenterY=-17.6958 CenterZ=0 NormalX=0 NormalY=0 NormalZ=1 AngleXU=0 Radius=1
    g40: Circle CenterX=-13.3521 CenterY=-17.9027 CenterZ=0 NormalX=0 NormalY=0 NormalZ=1 AngleXU=0 Radius=1
    g41: Circle CenterX=-14 CenterY=-18 CenterZ=0 NormalX=0 NormalY=0 NormalZ=1 AngleXU=0 Radius=1
    g42: BSplineCurve PolesCount=3 KnotsCount=2 Degree=2 IsPeriodic=0
    g43: GeomPoint X=-12.8401 Y=-17.6958 Z=0
    g44: GeomPoint X=-14 Y=-18 Z=0
    g45: LineSegment StartX=-6.2 StartY=0 StartZ=0 EndX=-7.2 EndY=0 EndZ=0
    g46: LineSegment StartX=-7.2 StartY=0 StartZ=0 EndX=-7.2 EndY=-2 EndZ=0
    g47: LineSegment StartX=-7.2 StartY=-2 StartZ=0 EndX=-6.2215 EndY=-2 EndZ=0
    g48: LineSegment StartX=-6.32538 StartY=-4 StartZ=0 EndX=-7.65538 EndY=-4 EndZ=0
    g49: LineSegment StartX=-7.65538 StartY=-4 StartZ=0 EndX=-7.65538 EndY=-5.99526 EndZ=0
    g50: LineSegment StartX=-7.65538 StartY=-5.99526 StartZ=0 EndX=-6.48644 EndY=-5.99526 EndZ=0
    g51: LineSegment StartX=-6.77343 StartY=-8 StartZ=0 EndX=-8.43343 EndY=-8 EndZ=0
    g52: LineSegment StartX=-8.43343 StartY=-8 StartZ=0 EndX=-8.43343 EndY=-10 EndZ=0
    g53: LineSegment StartX=-8.43343 StartY=-10 StartZ=0 EndX=-7.19003 EndY=-10 EndZ=0
  constraints (112):
    c: Horizontal(g0)
    c: Distance(g0) = 2
    c: Block(g0)
    c: Vertical(g1)
    c: Coincident(g2,g0)
    c: Vertical(g2)
    c: Block(g2)
    c: Coincident(g6,g2)
    c: Weight(g3) = 1
    c: Equal(g3,g4)
    c: Equal(g3,g5)
    c: InternalAlignment(g3,g6)
    c: InternalAlignment(g4,g6)
    c: InternalAlignment(g5,g6)
    c: InternalAlignment(g7,g6)
    c: InternalAlignment(g8,g6)
    c: Block(g6)
    c: Coincident(g9,g1)
    c: Coincident(g9,g6)
    c: Horizontal(g9)
    c: Vertical(g10)
    c: Block(g10)
    c: Horizontal(g11)
    c: Block(g11)
    c: Coincident(g12,g10)
    c: Horizontal(g12)
    c: Block(g12)
    c: Coincident(g13,g11)
    c: Vertical(g13)
    c: Block(g13)
    c: Coincident(g14,g10)
    c: Horizontal(g14)
    c: Block(g14)
    c: Block(g9)
    c: Block(g1)
    c: Weight(g15) = 1
    c: Equal(g15,g16)
    c: Equal(g15,g17)
    c: InternalAlignment(g15,g18)
    c: InternalAlignment(g16,g18)
    c: InternalAlignment(g17,g18)
    c: InternalAlignment(g19,g18)
    c: InternalAlignment(g20,g18)
    c: Weight(g21) = 1
    c: Equal(g21,g22)
    c: Equal(g21,g23)
    c: InternalAlignment(g21,g24)
    c: InternalAlignment(g22,g24)
    c: InternalAlignment(g23,g24)
    c: InternalAlignment(g25,g24)
    c: InternalAlignment(g26,g24)
    c: Weight(g27) = 1
    c: Equal(g27,g28)
    c: Equal(g27,g29)
    c: Coincident(g30,g14)
    c: InternalAlignment(g27,g30)
    c: InternalAlignment(g28,g30)
    c: InternalAlignment(g29,g30)
    c: InternalAlignment(g31,g30)
    c: InternalAlignment(g32,g30)
    c: Coincident(g36,g12)
    c: Weight(g33) = 1
    c: Equal(g33,g34)
    c: Equal(g33,g35)
    c: Coincident(g36,g11)
    c: InternalAlignment(g33,g36)
    c: InternalAlignment(g34,g36)
    c: InternalAlignment(g35,g36)
    c: InternalAlignment(g37,g36)
    c: InternalAlignment(g38,g36)
    c: Coincident(g42,g13)
    c: Weight(g39) = 1
    c: Equal(g39,g40)
    c: Equal(g39,g41)
    c: Coincident(g42,g1)
    c: InternalAlignment(g39,g42)
    c: InternalAlignment(g40,g42)
    c: InternalAlignment(g41,g42)
    c: InternalAlignment(g43,g42)
    c: InternalAlignment(g44,g42)
    c: Block(g18)
    c: Block(g24)
    c: Block(g30)
    c: Block(g36)
    c: Block(g42)
    c: Horizontal(g45)
    c: Coincident(g45,g0)
    c: Vertical(g46)
    c: Coincident(g46,g45)
    c: Coincident(g47,g46)
    c: Coincident(g47,g18)
    c: Horizontal(g47)
    c: Block(g46)
    c: Coincident(g48,g18)
    c: Horizontal(g48)
    c: Distance(g48) = 1.33
    c: Vertical(g49)
    c: Coincident(g49,g48)
    c: Coincident(g50,g49)
    c: Coincident(g50,g24)
    c: Horizontal(g50)
    c: Tangent(g50,g22)
    c: Horizontal(g51)
    c: Coincident(g51,g24)
    c: Block(g51)
    c: Vertical(g52)
    c: Block(g52)
    c: Coincident(g52,g51)
    c: Coincident(g53,g52)
    c: Coincident(g53,g30)
    c: Horizontal(g53)
    c: Distance(g1) = 8.5
FEATURE [Part::Feature] Face024
  shape: bbox 9.8 x 26.5 x 2e-07 mm, 1 faces, 0 solids (baked)
FEATURE [Part::Revolution] Revolve024
  Angle = 360
  Axis = (0,1,0)
  Base = (0,0,0)
  FaceMakerClass = Part::FaceMakerBullseye
  Placement = pos=(0,0,0) rot=(0,0,1;1.5708rad)
  Solid = false
  Source = -> Face024
  Symmetric = false
FEATURE [Part::Feature] Face025
  shape: bbox 9.8 x 26.5 x 2e-07 mm, 1 faces, 0 solids (baked)
FEATURE [Part::Revolution] Revolve025
  Angle = 360
  Axis = (0,1,0)
  Base = (0,0,0)
  FaceMakerClass = Part::FaceMakerBullseye
  Placement = pos=(0,0,0) rot=(0,0,1;1.5708rad)
  Solid = false
  Source = -> Face025
  Symmetric = false
FEATURE [Part::MultiFuse] Fusion033
  Placement = pos=(-18,19,36) rot=(0,0,1;0rad)
  Shapes = -> [Revolve025,Revolve024]
FEATURE [Part::Cylinder] Cylinder014
  Angle = 360
  AttacherType = Attacher::AttachEngine3D
  Height = 20
  Placement = pos=(0,0,36.15) rot=(0,0,1;0rad)
  Radius = 14.3
FEATURE [Part::Cylinder] Cylinder015
  Angle = 360
  AttacherType = Attacher::AttachEngine3D
  Height = 10
  Placement = pos=(0,0,36.15) rot=(0,0,1;0rad)
  Radius = 4
FEATURE [Part::MultiFuse] Fusion034  label="removeToCreteHoleForPlugHousing004"
  Placement = pos=(-42,19,36) rot=(0,1,0;1.5708rad)
  Shapes = -> [Cylinder014,Cylinder015]
FEATURE [Part::Cut] Cut008  label="top004"
  Base = -> Cut004
  Placement = pos=(-1,0,0) rot=(0,0,1;0rad)
  Tool = -> Fusion034
FEATURE [Part::Box] Box005  label="Cube005"
  AttacherType = Attacher::AttachEngine3D
  Height = 28
  Length = 3
  Placement = pos=(110.7,19,22) rot=(0,0,1;0rad)
  Width = 15.7
FEATURE [Part::Cylinder] Cylinder016
  Angle = 360
  AttacherType = Attacher::AttachEngine3D
  Height = 10
  Placement = pos=(0,0,36.15) rot=(0,0,1;0rad)
  Radius = 4
FEATURE [Part::Cylinder] Cylinder017
  Angle = 360
  AttacherType = Attacher::AttachEngine3D
  Height = 20
  Placement = pos=(0,0,36.15) rot=(0,0,1;0rad)
  Radius = 10.3
FEATURE [Part::MultiFuse] Fusion035  label="removeToCreteHoleForPlugHousing005"
  Placement = pos=(70,19,36) rot=(0,1,0;1.5708rad)
  Shapes = -> [Cylinder017,Cylinder016]
FEATURE [Part::Cut] Cut009  label="plugHousingTab001"
  Base = -> Box005
  Placement = pos=(-107.4,-14,0) rot=(0,0,1;0rad)
  Tool = -> Fusion035
FEATURE [Part::Box] Box006  label="Cube006"
  AttacherType = Attacher::AttachEngine3D
  Height = 28
  Length = 3
  Placement = pos=(110.7,19,22) rot=(0,0,1;0rad)
  Width = 15.7
FEATURE [Part::Cylinder] Cylinder018
  Angle = 360
  AttacherType = Attacher::AttachEngine3D
  Height = 10
  Placement = pos=(0,0,36.15) rot=(0,0,1;0rad)
  Radius = 4
FEATURE [Part::Cylinder] Cylinder019
  Angle = 360
  AttacherType = Attacher::AttachEngine3D
  Height = 20
  Placement = pos=(0,0,36.15) rot=(0,0,1;0rad)
  Radius = 10.3
FEATURE [Part::MultiFuse] Fusion036  label="removeToCreteHoleForPlugHousing006"
  Placement = pos=(70,19,36) rot=(0,1,0;1.5708rad)
  Shapes = -> [Cylinder019,Cylinder018]
FEATURE [Part::Cut] Cut010  label="plugHousingTab002"
  Base = -> Box006
  Placement = pos=(-107.4,-14,0) rot=(0,0,1;0rad)
  Tool = -> Fusion036
FEATURE [Part::MultiFuse] Fusion037
  Placement = pos=(9.6,23,0) rot=(0,0,1;3.14159rad)
  Shapes = -> [Cut009,Cut010]
FEATURE [Part::Box] Box  label="Cube"
  AttacherType = Attacher::AttachEngine3D
  Height = 10
  Length = 3
  Placement = pos=(3.3,4,12) rot=(0,0,1;0rad)
  Width = 10
FEATURE [Part::Fillet] Fillet004
  Base = -> Fusion028
  Edges = 1 edges r=2: [Edge25]
FEATURE [Part::Fillet] Fillet005  label="plugHousing046"
  Base = -> Fillet004
  Edges = 1 edges r=2: [Edge8]
FEATURE [Part::Fillet] Fillet006
  Base = -> Box
  Edges = 1 edges r=2: [Edge11]
FEATURE [Part::Box] Box007  label="Cube007"
  AttacherType = Attacher::AttachEngine3D
  Height = 10
  Length = 3
  Placement = pos=(3.3,4,50) rot=(0,0,1;0rad)
  Width = 10
FEATURE [Part::Fillet] Fillet007
  Base = -> Box007
  Edges = 1 edges r=2: [Edge12]
FEATURE [Part::Box] Box008  label="Cube008"
  AttacherType = Attacher::AttachEngine3D
  Height = 28
  Length = 4
  Placement = pos=(5,0,22) rot=(0,0,1;0rad)
  Width = 10
FEATURE [Part::Fillet] Fillet008
  Base = -> Box008
  Edges = 1 edges r=1: [Edge7]
FEATURE [Part::Fillet] Fillet009
  Base = -> Fillet008
  Edges = 1 edges r=2: [Edge5]
FEATURE [Part::Fillet] Fillet010
  Base = -> Fillet009
  Edges = 1 edges r=2: [Edge2]
FEATURE [Sketcher::SketchObject] Sketch009  label="topSketch003"
  FullyConstrained = true
  sketch-geometry (4):
    g0: LineSegment StartX=16.8446 StartY=31.512 StartZ=0 EndX=16.3251 EndY=34.4666 EndZ=0
    g1: ArcOfCircle CenterX=19 CenterY=19.2524 CenterZ=0 NormalX=0 NormalY=0 NormalZ=1 AngleXU=0 Radius=15.4476 StartAngle=1.74483 EndAngle=2.72717
    g2: ArcOfCircle CenterX=19 CenterY=19.2524 CenterZ=0 NormalX=0 NormalY=0 NormalZ=1 AngleXU=0 Radius=12.4476 StartAngle=1.74483 EndAngle=2.73189
    g3: LineSegment StartX=4.86004 StartY=25.4725 StartZ=0 EndX=7.58253 EndY=24.2107 EndZ=0
  constraints (7):
    c: Block(g0)
    c: Coincident(g1,g0)
    c: Coincident(g2,g0)
    c: Coincident(g3,g1)
    c: Coincident(g3,g2)
    c: Block(g1)
    c: Block(g2)
FEATURE [Part::Extrusion] Extrude008
  Base = -> Sketch009
  Dir = (0,0,1)
  DirMode = 2
  FaceMakerClass = Part::FaceMakerBullseye
  LengthFwd = 10
  LengthRev = 0
  Placement = pos=(0,0,31) rot=(0,0,1;0rad)
  Solid = true
  Symmetric = false
FEATURE [Part::Cylinder] Cylinder020
  Angle = 360
  AttacherType = Attacher::AttachEngine3D
  Height = 20
  Placement = pos=(0,0,36.15) rot=(0,0,1;0rad)
  Radius = 8.2
FEATURE [Part::Cylinder] Cylinder021
  Angle = 360
  AttacherType = Attacher::AttachEngine3D
  Height = 10
  Placement = pos=(0,0,36.15) rot=(0,0,1;0rad)
  Radius = 4
FEATURE [Part::MultiFuse] Fusion038  label="removeToCreteHoleForPlugHousing007"
  Placement = pos=(-42,19,36) rot=(0,1,0;1.5708rad)
  Shapes = -> [Cylinder020,Cylinder021]
FEATURE [Part::Cut] Cut011
  Base = -> Extrude008
  Tool = -> Fusion038
FEATURE [Part::Fillet] Fillet011
  Base = -> Cut011
  Edges = 1 edges r=2: [Edge1]
FEATURE [Part::Fillet] Fillet012
  Base = -> Fillet011
  Edges = 1 edges r=2.5: [Edge1]
FEATURE [Part::Fillet] Fillet013
  Base = -> Fillet012
  Edges = 1 edges r=2.5: [Edge2]
FEATURE [Part::Box] Box010  label="Cube010"
  AttacherType = Attacher::AttachEngine3D
  Height = 16
  Length = 8
  Placement = pos=(12.7,31.52,28) rot=(0,0,1;0rad)
  Width = 4
FEATURE [Sketcher::SketchObject] Sketch010  label="topSketch004"
  FullyConstrained = true
  sketch-geometry (4):
    g0: LineSegment StartX=16.8446 StartY=31.512 StartZ=0 EndX=16.3251 EndY=34.4666 EndZ=0
    g1: ArcOfCircle CenterX=19 CenterY=19.2524 CenterZ=0 NormalX=0 NormalY=0 NormalZ=1 AngleXU=0 Radius=15.4476 StartAngle=1.74483 EndAngle=2.72717
    g2: ArcOfCircle CenterX=19 CenterY=19.2524 CenterZ=0 NormalX=0 NormalY=0 NormalZ=1 AngleXU=0 Radius=12.4476 StartAngle=1.74483 EndAngle=2.73189
    g3: LineSegment StartX=4.86004 StartY=25.4725 StartZ=0 EndX=7.58253 EndY=24.2107 EndZ=0
  constraints (7):
    c: Block(g0)
    c: Coincident(g1,g0)
    c: Coincident(g2,g0)
    c: Coincident(g3,g1)
    c: Coincident(g3,g2)
    c: Block(g1)
    c: Block(g2)
FEATURE [Part::Cylinder] Cylinder022
  Angle = 360
  AttacherType = Attacher::AttachEngine3D
  Height = 10
  Placement = pos=(0,0,36.15) rot=(0,0,1;0rad)
  Radius = 4
FEATURE [Sketcher::SketchObject] Sketch011  label="topSketch005"
  FullyConstrained = true
  sketch-geometry (4):
    g0: LineSegment StartX=16.8446 StartY=31.512 StartZ=0 EndX=16.3251 EndY=34.4666 EndZ=0
    g1: ArcOfCircle CenterX=19 CenterY=19.2524 CenterZ=0 NormalX=0 NormalY=0 NormalZ=1 AngleXU=0 Radius=15.4476 StartAngle=1.74483 EndAngle=2.72717
    g2: ArcOfCircle CenterX=19 CenterY=19.2524 CenterZ=0 NormalX=0 NormalY=0 NormalZ=1 AngleXU=0 Radius=12.4476 StartAngle=1.74483 EndAngle=2.73189
    g3: LineSegment StartX=4.86004 StartY=25.4725 StartZ=0 EndX=7.58253 EndY=24.2107 EndZ=0
  constraints (7):
    c: Block(g0)
    c: Coincident(g1,g0)
    c: Coincident(g2,g0)
    c: Coincident(g3,g1)
    c: Coincident(g3,g2)
    c: Block(g1)
    c: Block(g2)
FEATURE [Part::Extrusion] Extrude010
  Base = -> Sketch011
  Dir = (0,0,1)
  DirMode = 2
  FaceMakerClass = Part::FaceMakerBullseye
  LengthFwd = 10.6
  LengthRev = 0
  Placement = pos=(0,0,31) rot=(0,0,1;0rad)
  Solid = true
  Symmetric = false
FEATURE [Part::Cylinder] Cylinder023
  Angle = 360
  AttacherType = Attacher::AttachEngine3D
  Height = 20
  Placement = pos=(0,0,36.15) rot=(0,0,1;0rad)
  Radius = 8.2
FEATURE [Part::MultiFuse] Fusion039  label="removeToCreteHoleForPlugHousing008"
  Placement = pos=(-42,19,36) rot=(0,1,0;1.5708rad)
  Shapes = -> [Cylinder023,Cylinder022]
FEATURE [Part::Cut] Cut012
  Base = -> Extrude010
  Placement = pos=(0,0,-0.3) rot=(0,0,1;0rad)
  Tool = -> Fusion039
FEATURE [Part::Cut] Cut013
  Base = -> Box010
  Tool = -> Cut012
FEATURE [Part::Fillet] Fillet014
  Base = -> Cut013
  Edges = 1 edges r=0.7: [Edge13]
FEATURE [Part::Fillet] Fillet015
  Base = -> Fillet014
  Edges = 1 edges r=0.7: [Edge13]
FEATURE [Part::Fillet] Fillet016
  Base = -> Fillet015
  Edges = 1 edges r=0.7: [Edge16]
FEATURE [Part::Fillet] Fillet017
  Base = -> Fillet016
  Edges = 1 edges r=0.7: [Edge11]
FEATURE [Part::Fillet] Fillet018
  Base = -> Fillet017
  Edges = 1 edges r=0.7: [Edge10]
FEATURE [Part::Fillet] Fillet019
  Base = -> Fillet018
  Edges = 1 edges r=1.2: [Edge5]
FEATURE [Part::Fillet] Fillet020
  Base = -> Fillet019
  Edges = 1 edges r=1.2: [Edge12]
FEATURE [Part::Fillet] Fillet021
  Base = -> Fillet020
  Edges = 1 edges r=2: [Edge1]
  Placement = pos=(0.3,0,0) rot=(0,0,1;0rad)
FEATURE [Part::MultiFuse] Fusion040  label="top005"
  Shapes = -> [Cut008,Fillet021]
FEATURE [Part::MultiFuse] Fusion041  label="wireHolder"
  Shapes = -> [Fusion033,Fillet013]
FEATURE [Part::MultiFuse] Fusion042
  Shapes = -> [Fillet007,Fusion041]
FEATURE [Part::MultiFuse] Fusion043  label="wireHolder001"
  Shapes = -> [Fusion042,Fillet010]
FEATURE [Part::MultiFuse] Fusion044  label="wireHolder002"
  Shapes = -> [Fillet006,Fusion037,Fusion043]
FEATURE [Part::Feature] Face026
  shape: bbox 11 x 6 x 2e-07 mm, 1 faces, 0 solids (baked)
FEATURE [Part::Revolution] Revolve026
  Angle = 360
  Axis = (0,1,0)
  Base = (0,0,0)
  FaceMakerClass = Part::FaceMakerBullseye
  Placement = pos=(30.3,-1,19.7) rot=(0,0,1;0rad)
  Solid = false
  Source = -> Face026
  Symmetric = false
FEATURE [Sketcher::SketchObject] Sketch013  label="topSketch006"
  FullyConstrained = true
  sketch-geometry (13):
    g0: LineSegment StartX=117 StartY=19 StartZ=0 EndX=117 EndY=38 EndZ=0
    g1: ArcOfCircle CenterX=98 CenterY=19 CenterZ=0 NormalX=0 NormalY=0 NormalZ=1 AngleXU=0 Radius=19 StartAngle=5.7297 EndAngle=6.28319
    g2: LineSegment StartX=0 StartY=3 StartZ=0 EndX=0 EndY=19 EndZ=0
    g3: LineSegment StartX=19 StartY=38 StartZ=0 EndX=117 EndY=38 EndZ=0
    g4: ArcOfCircle CenterX=19 CenterY=19 CenterZ=0 NormalX=0 NormalY=0 NormalZ=1 AngleXU=0 Radius=19 StartAngle=1.5708 EndAngle=3.14159
    g5: ArcOfCircle CenterX=19 CenterY=19 CenterZ=0 NormalX=0 NormalY=0 NormalZ=1 AngleXU=0 Radius=16 StartAngle=1.5708 EndAngle=3.14159
    g6: ArcOfCircle CenterX=98 CenterY=19 CenterZ=0 NormalX=0 NormalY=0 NormalZ=1 AngleXU=0 Radius=16 StartAngle=5.60905 EndAngle=6.28319
    g7: LineSegment StartX=114 StartY=19 StartZ=0 EndX=114 EndY=35 EndZ=0
    g8: LineSegment StartX=110.5 StartY=9.01251 StartZ=0 EndX=114.163 EndY=9.01251 EndZ=0
    g9: LineSegment StartX=114 StartY=35 StartZ=0 EndX=19 EndY=35 EndZ=0
    g10: LineSegment StartX=0 StartY=3 StartZ=0 EndX=0 EndY=0 EndZ=0
    g11: LineSegment StartX=3 StartY=0 StartZ=0 EndX=0 EndY=0 EndZ=0
    g12: LineSegment StartX=3 StartY=19 StartZ=0 EndX=3 EndY=0 EndZ=0
  constraints (33):
    c: Vertical(g0)
    c: Distance(g0) = 19
    c: Block(g0)
    c: Coincident(g1,g0)
    c: Block(g1)
    c: Vertical(g2)
    c: Block(g2)
    c: Coincident(g3,g0)
    c: Horizontal(g3)
    c: Distance(g3) = 98
    c: Coincident(g4,g3)
    c: Coincident(g4,g2)
    c: Block(g4)
    c: Coincident(g5,g4)
    c: Coincident(g6,g1)
    c: Block(g6)
    c: Block(g5)
    c: Coincident(g7,g6)
    c: Vertical(g7)
    c: Coincident(g8,g6)
    c: Coincident(g8,g1)
    c: Coincident(g9,g7)
    c: Coincident(g9,g5)
    c: Horizontal(g9)
    c: Tangent(g9,g5)
    c: Coincident(g10,g2)
    c: Distance(g10) = 3
    c: Vertical(g10)
    c: Coincident(g11,g10)
    c: Horizontal(g11)
    c: Coincident(g12,g5)
    c: Coincident(g12,g11)
    c: Vertical(g12)
FEATURE [Part::Extrusion] Extrude011  label="top006"
  Base = -> Sketch013
  Dir = (0,0,1)
  DirMode = 2
  FaceMakerClass = Part::FaceMakerBullseye
  LengthFwd = 72
  LengthRev = 0
  Solid = true
  Symmetric = false
FEATURE [Sketcher::SketchObject] Sketch014
  FullyConstrained = true
  MapMode = 3
  Placement = pos=(0,0,0) rot=(1,0,0;1.5708rad)
  Support = -> [Extrude011]
  sketch-geometry (8):
    g0: Circle CenterX=80.351 CenterY=-67.6202 CenterZ=0 NormalX=0 NormalY=0 NormalZ=1 AngleXU=0 Radius=2
    g1: Circle CenterX=80.351 CenterY=-67.6202 CenterZ=0 NormalX=0 NormalY=0 NormalZ=1 AngleXU=0 Radius=3
    g2: Circle CenterX=80.351 CenterY=-4.92017 CenterZ=0 NormalX=0 NormalY=0 NormalZ=1 AngleXU=0 Radius=2
    g3: Circle CenterX=80.351 CenterY=-4.92017 CenterZ=0 NormalX=0 NormalY=0 NormalZ=1 AngleXU=0 Radius=3
    g4: Circle CenterX=23.851 CenterY=-4.92017 CenterZ=0 NormalX=0 NormalY=0 NormalZ=1 AngleXU=0 Radius=2
    g5: Circle CenterX=23.851 CenterY=-4.92017 CenterZ=0 NormalX=0 NormalY=0 NormalZ=1 AngleXU=0 Radius=3
    g6: Circle CenterX=23.851 CenterY=-67.6202 CenterZ=0 NormalX=0 NormalY=0 NormalZ=1 AngleXU=0 Radius=2
    g7: Circle CenterX=23.851 CenterY=-67.6202 CenterZ=0 NormalX=0 NormalY=0 NormalZ=1 AngleXU=0 Radius=3
  constraints (8):
    c: Block(g3)
    c: Block(g2)
    c: Block(g1)
    c: Block(g0)
    c: Block(g6)
    c: Block(g7)
    c: Block(g4)
    c: Block(g5)
FEATURE [Part::Feature] Face027
  shape: bbox 11 x 6 x 2e-07 mm, 1 faces, 0 solids (baked)
FEATURE [Part::Revolution] Revolve027
  Angle = 360
  Axis = (0,1,0)
  Base = (0,0,0)
  FaceMakerClass = Part::FaceMakerBullseye
  Placement = pos=(30.3,-1,51.7) rot=(0,0,1;0rad)
  Solid = false
  Source = -> Face027
  Symmetric = false
FEATURE [Part::Feature] Face028
  shape: bbox 11 x 6 x 2e-07 mm, 1 faces, 0 solids (baked)
FEATURE [Part::Revolution] Revolve028
  Angle = 360
  Axis = (0,1,0)
  Base = (0,0,0)
  FaceMakerClass = Part::FaceMakerBullseye
  Placement = pos=(62.3,-1,19.7) rot=(0,0,1;0rad)
  Solid = false
  Source = -> Face028
  Symmetric = false
FEATURE [Part::Feature] Face029
  shape: bbox 11 x 6 x 2e-07 mm, 1 faces, 0 solids (baked)
FEATURE [Part::Revolution] Revolve029
  Angle = 360
  Axis = (0,1,0)
  Base = (0,0,0)
  FaceMakerClass = Part::FaceMakerBullseye
  Placement = pos=(62.3,-1,51.7) rot=(0,0,1;0rad)
  Solid = false
  Source = -> Face029
  Symmetric = false
FEATURE [Part::Feature] Wire
  shape: bbox 11 x 5.2 x 2e-07 mm, 0 faces, 0 solids (baked)
FEATURE [Part::Revolution] Revolve030
  Angle = 360
  Axis = (0,1,0)
  Base = (0,0,0)
  FaceMakerClass = Part::FaceMakerBullseye
  Placement = pos=(30.3,38,19.7) rot=(0,0,1;0rad)
  Solid = true
  Source = -> Wire
  Symmetric = false
FEATURE [Part::Feature] Wire001
  shape: bbox 11 x 5.2 x 2e-07 mm, 0 faces, 0 solids (baked)
FEATURE [Part::Revolution] Revolve031
  Angle = 360
  Axis = (0,1,0)
  Base = (0,0,0)
  FaceMakerClass = Part::FaceMakerBullseye
  Placement = pos=(30.3,38,51.7) rot=(0,0,1;0rad)
  Solid = true
  Source = -> Wire001
  Symmetric = false
FEATURE [Part::Feature] Wire002
  shape: bbox 11 x 5.2 x 2e-07 mm, 0 faces, 0 solids (baked)
FEATURE [Part::Revolution] Revolve032
  Angle = 360
  Axis = (0,1,0)
  Base = (0,0,0)
  FaceMakerClass = Part::FaceMakerBullseye
  Placement = pos=(62.3,38,51.7) rot=(0,0,1;0rad)
  Solid = true
  Source = -> Wire002
  Symmetric = false
FEATURE [Part::Feature] Wire003
  shape: bbox 11 x 5.2 x 2e-07 mm, 0 faces, 0 solids (baked)
FEATURE [Part::Revolution] Revolve033
  Angle = 360
  Axis = (0,1,0)
  Base = (0,0,0)
  FaceMakerClass = Part::FaceMakerBullseye
  Placement = pos=(62.3,38,19.7) rot=(0,0,1;0rad)
  Solid = true
  Source = -> Wire003
  Symmetric = false
FEATURE [Part::MultiFuse] Fusion045  label="altRandScrewHousing"
  Shapes = -> [Revolve029,Revolve027,Revolve028,Revolve026]
FEATURE [Part::MultiFuse] Fusion046  label="fanScrewHousing"
  Shapes = -> [Revolve033,Revolve032,Revolve031,Revolve030]
FEATURE [Sketcher::SketchObject] Sketch015
  FullyConstrained = true
  sketch-geometry (17):
    g0: Circle CenterX=-3.5 CenterY=23.5 CenterZ=0 NormalX=0 NormalY=0 NormalZ=1 AngleXU=0 Radius=1
    g1: Circle CenterX=-1 CenterY=15.25 CenterZ=0 NormalX=0 NormalY=0 NormalZ=1 AngleXU=0 Radius=1
    g2: Circle CenterX=-3.5 CenterY=7 CenterZ=0 NormalX=0 NormalY=0 NormalZ=1 AngleXU=0 Radius=1
    g3: BSplineCurve PolesCount=3 KnotsCount=2 Degree=2 IsPeriodic=0
    g4: GeomPoint X=-3.5 Y=23.5 Z=0
    g5: GeomPoint X=-3.5 Y=7 Z=0
    g6: Circle CenterX=-4.8 CenterY=30.5 CenterZ=0 NormalX=0 NormalY=0 NormalZ=1 AngleXU=0 Radius=1
    g7: Circle CenterX=-3.5 CenterY=30.5 CenterZ=0 NormalX=0 NormalY=0 NormalZ=1 AngleXU=0 Radius=1
    g8: Circle CenterX=-3.5 CenterY=29.2 CenterZ=0 NormalX=0 NormalY=0 NormalZ=1 AngleXU=0 Radius=1
    g9: BSplineCurve PolesCount=3 KnotsCount=2 Degree=2 IsPeriodic=0
    g10: GeomPoint X=-4.8 Y=30.5 Z=0
    g11: GeomPoint X=-3.5 Y=29.2 Z=0
    g12: LineSegment StartX=-3.5 StartY=29.2 StartZ=0 EndX=-3.5 EndY=23.5 EndZ=0
    g13: LineSegment StartX=-4.8 StartY=30.5 StartZ=0 EndX=0 EndY=30.5 EndZ=0
    g14: LineSegment StartX=-3.5 StartY=0.3 StartZ=0 EndX=0 EndY=0.3 EndZ=0
    g15: LineSegment StartX=-3.5 StartY=0.3 StartZ=0 EndX=-3.5 EndY=7 EndZ=0
    g16: LineSegment StartX=0 StartY=0.3 StartZ=0 EndX=0 EndY=30.5 EndZ=0
  constraints (34):
    c: Weight(g0) = 1
    c: Equal(g0,g1)
    c: Equal(g0,g2)
    c: InternalAlignment(g0,g3)
    c: InternalAlignment(g1,g3)
    c: InternalAlignment(g2,g3)
    c: InternalAlignment(g4,g3)
    c: InternalAlignment(g5,g3)
    c: Block(g3)
    c: Weight(g6) = 1
    c: Equal(g6,g7)
    c: Equal(g6,g8)
    c: InternalAlignment(g6,g9)
    c: InternalAlignment(g7,g9)
    c: InternalAlignment(g8,g9)
    c: InternalAlignment(g10,g9)
    c: InternalAlignment(g11,g9)
    c: Block(g9)
    c: Coincident(g12,g9)
    c: Coincident(g12,g3)
    c: Vertical(g12)
    c: Coincident(g13,g9)
    c: Horizontal(g13)
    c: Distance(g13) = 4.8
    c: Horizontal(g14)
    c: Block(g14)
    c: Coincident(g15,g14)
    c: Coincident(g15,g3)
    c: Vertical(g15)
    c: Coincident(g16,g14)
    c: Coincident(g16,g13)
    c: Vertical(g16)
    c: Tangent(g16,g1)
    c: Distance(g14) = 3.5
FEATURE [Sketcher::SketchObject] Sketch016
  FullyConstrained = true
  sketch-geometry (16):
    g0: Circle CenterX=-3.5 CenterY=23.5 CenterZ=0 NormalX=0 NormalY=0 NormalZ=1 AngleXU=0 Radius=1
    g1: Circle CenterX=-1 CenterY=15.25 CenterZ=0 NormalX=0 NormalY=0 NormalZ=1 AngleXU=0 Radius=1
    g2: Circle CenterX=-3.5 CenterY=7 CenterZ=0 NormalX=0 NormalY=0 NormalZ=1 AngleXU=0 Radius=1
    g3: BSplineCurve PolesCount=3 KnotsCount=2 Degree=2 IsPeriodic=0
    g4: GeomPoint X=-3.5 Y=23.5 Z=0
    g5: GeomPoint X=-3.5 Y=7 Z=0
    g6: LineSegment StartX=-3.5 StartY=28.2 StartZ=0 EndX=-3.5 EndY=23.5 EndZ=0
    g7: LineSegment StartX=0 StartY=29.5 StartZ=0 EndX=0 EndY=30 EndZ=0
    g8: LineSegment StartX=-3.5 StartY=28.2 StartZ=0 EndX=-3.5 EndY=30 EndZ=0
    g9: LineSegment StartX=0 StartY=30 StartZ=0 EndX=0 EndY=30.5 EndZ=0
    g10: LineSegment StartX=0 StartY=30.5 StartZ=0 EndX=-3.5 EndY=30.5 EndZ=0
    g11: LineSegment StartX=-3.5 StartY=30.5 StartZ=0 EndX=-3.5 EndY=30 EndZ=0
    g12: LineSegment StartX=0 StartY=29.5 StartZ=0 EndX=0 EndY=5 EndZ=0
    g13: LineSegment StartX=-3.5 StartY=0.3 StartZ=0 EndX=-3.5 EndY=7 EndZ=0
    g14: LineSegment StartX=-3.5 StartY=0.3 StartZ=0 EndX=0 EndY=0.3 EndZ=0
    g15: LineSegment StartX=0 StartY=5 StartZ=0 EndX=0 EndY=0.3 EndZ=0
  constraints (39):
    c: Weight(g0) = 1
    c: Equal(g0,g1)
    c: Equal(g0,g2)
    c: InternalAlignment(g0,g3)
    c: InternalAlignment(g1,g3)
    c: InternalAlignment(g2,g3)
    c: InternalAlignment(g4,g3)
    c: InternalAlignment(g5,g3)
    c: Block(g3)
    c: Coincident(g6,g3)
    c: Vertical(g6)
    c: Vertical(g7)
    c: Distance(g7) = 0.5
    c: Coincident(g8,g6)
    c: Vertical(g8)
    c: Block(g6)
    c: Block(g7)
    c: Vertical(g9)
    c: Equal(g7,g9) = 0.5
    c: Block(g9)
    c: Coincident(g9,g7)
    c: Horizontal(g10)
    c: Coincident(g10,g9)
    c: Coincident(g11,g10)
    c: Coincident(g11,g8)
    c: Vertical(g11)
    c: Block(g11)
    c: Coincident(g12,g7)
    c: Vertical(g12)
    c: Coincident(g13,g3)
    c: Vertical(g13)
    c: Distance(g13) = 6.7
    c: Coincident(g14,g13)
    c: Horizontal(g14)
    c: Block(g14)
    c: Coincident(g15,g12)
    c: Coincident(g15,g14)
    c: Vertical(g15)
    c: Block(g15)
FEATURE [Sketcher::SketchObject] Sketch017
  FullyConstrained = true
  sketch-geometry (11):
    g0: LineSegment StartX=-3.5 StartY=1e-16 StartZ=0 EndX=-1.6 EndY=1e-16 EndZ=0
    g1: LineSegment StartX=-1.6 StartY=1e-16 StartZ=0 EndX=-1.6 EndY=1.5 EndZ=0
    g2: LineSegment StartX=-3.5 StartY=1.5 StartZ=0 EndX=-1.6 EndY=1.5 EndZ=0
    g3: LineSegment StartX=-3.5 StartY=1e-16 StartZ=0 EndX=-4.8 EndY=1e-16 EndZ=0
    g4: Circle CenterX=-3.5 CenterY=1.3 CenterZ=0 NormalX=0 NormalY=0 NormalZ=1 AngleXU=0 Radius=1
    g5: Circle CenterX=-3.5 CenterY=1e-16 CenterZ=0 NormalX=0 NormalY=0 NormalZ=1 AngleXU=0 Radius=1
    g6: Circle CenterX=-4.8 CenterY=1e-16 CenterZ=0 NormalX=0 NormalY=0 NormalZ=1 AngleXU=0 Radius=1
    g7: BSplineCurve PolesCount=3 KnotsCount=2 Degree=2 IsPeriodic=0
    g8: GeomPoint X=-3.5 Y=1.3 Z=0
    g9: GeomPoint X=-4.8 Y=1e-16 Z=0
    g10: LineSegment StartX=-3.5 StartY=1.3 StartZ=0 EndX=-3.5 EndY=1.5 EndZ=0
  constraints (24):
    c: Horizontal(g0)
    c: Distance(g0) = 1.9
    c: Block(g0)
    c: Coincident(g1,g0)
    c: Vertical(g1)
    c: Coincident(g2,g1)
    c: Horizontal(g2)
    c: Coincident(g3,g0)
    c: Horizontal(g3)
    c: Distance(g3) = 1.3
    c: Weight(g4) = 1
    c: Equal(g4,g5)
    c: Coincident(g5,g0)
    c: Equal(g4,g6)
    c: Coincident(g7,g3)
    c: InternalAlignment(g4,g7)
    c: InternalAlignment(g5,g7)
    c: InternalAlignment(g6,g7)
    c: InternalAlignment(g8,g7)
    c: InternalAlignment(g9,g7)
    c: Coincident(g10,g7)
    c: Coincident(g10,g2)
    c: Vertical(g10)
    c: Block(g10)
FEATURE [Part::Feature] Face035
  shape: bbox 3.2 x 1.5 x 2e-07 mm, 1 faces, 0 solids (baked)
FEATURE [Part::Revolution] Revolve039  label="backCaseScrewRetainer"
  Angle = 360
  Axis = (0,1,0)
  Base = (0,0,0)
  FaceMakerClass = Part::FaceMakerBullseye
  Placement = pos=(12.5,3,62) rot=(0,0,1;0rad)
  Solid = false
  Source = -> Face035
  Symmetric = false
FEATURE [Part::Feature] Face036
  shape: bbox 3.2 x 1.5 x 2e-07 mm, 1 faces, 0 solids (baked)
FEATURE [Part::Feature] Face039
  shape: bbox 4.8 x 30.2 x 2e-07 mm, 1 faces, 0 solids (baked)
FEATURE [Part::Revolution] Revolve043  label="frontCaseScrewPost002"
  Angle = 360
  Axis = (0,1,0)
  Base = (0,0,0)
  FaceMakerClass = Part::FaceMakerBullseye
  Placement = pos=(89.5,4.5,3.5) rot=(0,0,1;0rad)
  Solid = false
  Source = -> Face039
  Symmetric = false
FEATURE [Part::Feature] Face042
  shape: bbox 4.8 x 30.2 x 2e-07 mm, 1 faces, 0 solids (baked)
FEATURE [Part::Revolution] Revolve046  label="frontCaseScrewPost003"
  Angle = 360
  Axis = (0,1,0)
  Base = (0,0,0)
  FaceMakerClass = Part::FaceMakerBullseye
  Placement = pos=(89.5,4.5,68.5) rot=(0,0,1;0rad)
  Solid = false
  Source = -> Face042
  Symmetric = false
FEATURE [Part::Feature] Face043
  shape: bbox 3.2 x 1.5 x 2e-07 mm, 1 faces, 0 solids (baked)
FEATURE [Part::Revolution] Revolve047  label="frontCaseScrewRetainer002"
  Angle = 360
  Axis = (0,1,0)
  Base = (0,0,0)
  FaceMakerClass = Part::FaceMakerBullseye
  Placement = pos=(89.5,3,68.5) rot=(0,0,1;0rad)
  Solid = false
  Source = -> Face043
  Symmetric = false
FEATURE [Part::Feature] Face044
  shape: bbox 3.2 x 1.5 x 2e-07 mm, 1 faces, 0 solids (baked)
FEATURE [Part::Revolution] Revolve048  label="frontCaseScrewRetainer003"
  Angle = 360
  Axis = (0,1,0)
  Base = (0,0,0)
  FaceMakerClass = Part::FaceMakerBullseye
  Placement = pos=(89.5,3,3.5) rot=(0,0,1;0rad)
  Solid = false
  Source = -> Face044
  Symmetric = false
FEATURE [App::MeasureDistance] Distance002  label="Distance: 1.67 mm"
  Distance = 1.66921
  P1 = (99.2361,4.7524,71.7)
  P2 = (99.2347,6.42161,71.7)
FEATURE [Sketcher::SketchObject] Sketch018
  FullyConstrained = true
  sketch-geometry (7):
    g0: LineSegment StartX=0 StartY=0 StartZ=0 EndX=0 EndY=6 EndZ=0
    g1: Circle CenterX=0 CenterY=0 CenterZ=0 NormalX=0 NormalY=0 NormalZ=1 AngleXU=0 Radius=1
    g2: Circle CenterX=8 CenterY=6 CenterZ=0 NormalX=0 NormalY=0 NormalZ=1 AngleXU=0 Radius=1
    g3: BSplineCurve PolesCount=3 KnotsCount=2 Degree=2 IsPeriodic=0
    g4: GeomPoint X=0 Y=0 Z=0
    g5: GeomPoint X=8 Y=6 Z=0
    g6: LineSegment StartX=0 StartY=6 StartZ=0 EndX=8 EndY=6 EndZ=0
  constraints (14):
    c: Coincident(g0,g-1)
    c: Distance(g0) = 6
    c: Vertical(g0)
    c: Coincident(g3,g0)
    c: Weight(g1) = 1
    c: Equal(g1,g2)
    c: InternalAlignment(g1,g3)
    c: InternalAlignment(g2,g3)
    c: InternalAlignment(g4,g3)
    c: InternalAlignment(g5,g3)
    c: Block(g3)
    c: Coincident(g6,g0)
    c: Coincident(g6,g3)
    c: Horizontal(g6)
FEATURE [Part::Extrusion] Extrude012  label="caseScrewPillarBracket"
  Base = -> Sketch018
  Dir = (0,0,1)
  DirMode = 2
  FaceMakerClass = Part::FaceMakerBullseye
  LengthFwd = 2.4
  LengthRev = 0
  Placement = pos=(15.76,29,8.8) rot=(0,1,0;0rad)
  Solid = true
  Symmetric = false
FEATURE [Sketcher::SketchObject] Sketch019
  FullyConstrained = true
  sketch-geometry (7):
    g0: LineSegment StartX=0 StartY=0 StartZ=0 EndX=0 EndY=6 EndZ=0
    g1: Circle CenterX=0 CenterY=0 CenterZ=0 NormalX=0 NormalY=0 NormalZ=1 AngleXU=0 Radius=1
    g2: Circle CenterX=8 CenterY=6 CenterZ=0 NormalX=0 NormalY=0 NormalZ=1 AngleXU=0 Radius=1
    g3: BSplineCurve PolesCount=3 KnotsCount=2 Degree=2 IsPeriodic=0
    g4: GeomPoint X=0 Y=0 Z=0
    g5: GeomPoint X=8 Y=6 Z=0
    g6: LineSegment StartX=0 StartY=6 StartZ=0 EndX=8 EndY=6 EndZ=0
  constraints (14):
    c: Coincident(g0,g-1)
    c: Distance(g0) = 6
    c: Vertical(g0)
    c: Coincident(g3,g0)
    c: Weight(g1) = 1
    c: Equal(g1,g2)
    c: InternalAlignment(g1,g3)
    c: InternalAlignment(g2,g3)
    c: InternalAlignment(g4,g3)
    c: InternalAlignment(g5,g3)
    c: Block(g3)
    c: Coincident(g6,g0)
    c: Coincident(g6,g3)
    c: Horizontal(g6)
FEATURE [Part::Extrusion] Extrude013  label="caseScrewPillarBracket001"
  Base = -> Sketch019
  Dir = (0,0,1)
  DirMode = 2
  FaceMakerClass = Part::FaceMakerBullseye
  LengthFwd = 2.4
  LengthRev = 0
  Placement = pos=(15.76,29,60.8) rot=(0,0,1;0rad)
  Solid = true
  Symmetric = false
FEATURE [Sketcher::SketchObject] Sketch020
  FullyConstrained = true
  sketch-geometry (7):
    g0: LineSegment StartX=0 StartY=0 StartZ=0 EndX=0 EndY=6 EndZ=0
    g1: Circle CenterX=0 CenterY=0 CenterZ=0 NormalX=0 NormalY=0 NormalZ=1 AngleXU=0 Radius=1
    g2: Circle CenterX=8 CenterY=6 CenterZ=0 NormalX=0 NormalY=0 NormalZ=1 AngleXU=0 Radius=1
    g3: BSplineCurve PolesCount=3 KnotsCount=2 Degree=2 IsPeriodic=0
    g4: GeomPoint X=0 Y=0 Z=0
    g5: GeomPoint X=8 Y=6 Z=0
    g6: LineSegment StartX=0 StartY=6 StartZ=0 EndX=8 EndY=6 EndZ=0
  constraints (14):
    c: Coincident(g0,g-1)
    c: Distance(g0) = 6
    c: Vertical(g0)
    c: Coincident(g3,g0)
    c: Weight(g1) = 1
    c: Equal(g1,g2)
    c: InternalAlignment(g1,g3)
    c: InternalAlignment(g2,g3)
    c: InternalAlignment(g4,g3)
    c: InternalAlignment(g5,g3)
    c: Block(g3)
    c: Coincident(g6,g0)
    c: Coincident(g6,g3)
    c: Horizontal(g6)
FEATURE [Part::Extrusion] Extrude014  label="caseScrewPillarBracket002"
  Base = -> Sketch020
  Dir = (0,0,1)
  DirMode = 2
  FaceMakerClass = Part::FaceMakerBullseye
  LengthFwd = 2.4
  LengthRev = 0
  Placement = pos=(13.7,29,13.26) rot=(0,-1,0;1.5708rad)
  Solid = true
  Symmetric = false
FEATURE [Sketcher::SketchObject] Sketch021
  FullyConstrained = true
  sketch-geometry (7):
    g0: LineSegment StartX=0 StartY=0 StartZ=0 EndX=0 EndY=6 EndZ=0
    g1: Circle CenterX=0 CenterY=0 CenterZ=0 NormalX=0 NormalY=0 NormalZ=1 AngleXU=0 Radius=1
    g2: Circle CenterX=8 CenterY=6 CenterZ=0 NormalX=0 NormalY=0 NormalZ=1 AngleXU=0 Radius=1
    g3: BSplineCurve PolesCount=3 KnotsCount=2 Degree=2 IsPeriodic=0
    g4: GeomPoint X=0 Y=0 Z=0
    g5: GeomPoint X=8 Y=6 Z=0
    g6: LineSegment StartX=0 StartY=6 StartZ=0 EndX=8 EndY=6 EndZ=0
  constraints (14):
    c: Coincident(g0,g-1)
    c: Distance(g0) = 6
    c: Vertical(g0)
    c: Coincident(g3,g0)
    c: Weight(g1) = 1
    c: Equal(g1,g2)
    c: InternalAlignment(g1,g3)
    c: InternalAlignment(g2,g3)
    c: InternalAlignment(g4,g3)
    c: InternalAlignment(g5,g3)
    c: Block(g3)
    c: Coincident(g6,g0)
    c: Coincident(g6,g3)
    c: Horizontal(g6)
FEATURE [Part::Extrusion] Extrude015  label="caseScrewPillarBracket003"
  Base = -> Sketch021
  Dir = (0,0,1)
  DirMode = 2
  FaceMakerClass = Part::FaceMakerBullseye
  LengthFwd = 2.4
  LengthRev = 0
  Placement = pos=(11.3,29,58.74) rot=(0,1,0;1.5708rad)
  Solid = true
  Symmetric = false
FEATURE [Sketcher::SketchObject] Sketch022
  FullyConstrained = true
  sketch-geometry (7):
    g0: LineSegment StartX=0 StartY=0 StartZ=0 EndX=0 EndY=6 EndZ=0
    g1: Circle CenterX=0 CenterY=0 CenterZ=0 NormalX=0 NormalY=0 NormalZ=1 AngleXU=0 Radius=1
    g2: Circle CenterX=8 CenterY=6 CenterZ=0 NormalX=0 NormalY=0 NormalZ=1 AngleXU=0 Radius=1
    g3: BSplineCurve PolesCount=3 KnotsCount=2 Degree=2 IsPeriodic=0
    g4: GeomPoint X=0 Y=0 Z=0
    g5: GeomPoint X=8 Y=6 Z=0
    g6: LineSegment StartX=0 StartY=6 StartZ=0 EndX=8 EndY=6 EndZ=0
  constraints (14):
    c: Coincident(g0,g-1)
    c: Distance(g0) = 6
    c: Vertical(g0)
    c: Coincident(g3,g0)
    c: Weight(g1) = 1
    c: Equal(g1,g2)
    c: InternalAlignment(g1,g3)
    c: InternalAlignment(g2,g3)
    c: InternalAlignment(g4,g3)
    c: InternalAlignment(g5,g3)
    c: Block(g3)
    c: Coincident(g6,g0)
    c: Coincident(g6,g3)
    c: Horizontal(g6)
FEATURE [Part::Extrusion] Extrude016  label="caseScrewPillarBracket004"
  Base = -> Sketch022
  Dir = (0,0,1)
  DirMode = 2
  FaceMakerClass = Part::FaceMakerBullseye
  LengthFwd = 2.4
  LengthRev = 0
  Placement = pos=(88.3,29,65.23) rot=(0,1,0;1.5708rad)
  Solid = true
  Symmetric = false
FEATURE [Sketcher::SketchObject] Sketch023
  FullyConstrained = true
  sketch-geometry (7):
    g0: LineSegment StartX=0 StartY=0 StartZ=0 EndX=0 EndY=6 EndZ=0
    g1: Circle CenterX=0 CenterY=0 CenterZ=0 NormalX=0 NormalY=0 NormalZ=1 AngleXU=0 Radius=1
    g2: Circle CenterX=8 CenterY=6 CenterZ=0 NormalX=0 NormalY=0 NormalZ=1 AngleXU=0 Radius=1
    g3: BSplineCurve PolesCount=3 KnotsCount=2 Degree=2 IsPeriodic=0
    g4: GeomPoint X=0 Y=0 Z=0
    g5: GeomPoint X=8 Y=6 Z=0
    g6: LineSegment StartX=0 StartY=6 StartZ=0 EndX=8 EndY=6 EndZ=0
  constraints (14):
    c: Coincident(g0,g-1)
    c: Distance(g0) = 6
    c: Vertical(g0)
    c: Coincident(g3,g0)
    c: Weight(g1) = 1
    c: Equal(g1,g2)
    c: InternalAlignment(g1,g3)
    c: InternalAlignment(g2,g3)
    c: InternalAlignment(g4,g3)
    c: InternalAlignment(g5,g3)
    c: Block(g3)
    c: Coincident(g6,g0)
    c: Coincident(g6,g3)
    c: Horizontal(g6)
FEATURE [Part::Extrusion] Extrude017  label="caseScrewPillarBracket005"
  Base = -> Sketch023
  Dir = (0,0,1)
  DirMode = 2
  FaceMakerClass = Part::FaceMakerBullseye
  LengthFwd = 2.4
  LengthRev = 0
  Placement = pos=(90.7,29,6.77) rot=(0,-1,0;1.5708rad)
  Solid = true
  Symmetric = false
FEATURE [Sketcher::SketchObject] Sketch024
  FullyConstrained = true
  sketch-geometry (7):
    g0: LineSegment StartX=0 StartY=0 StartZ=0 EndX=0 EndY=6 EndZ=0
    g1: Circle CenterX=0 CenterY=0 CenterZ=0 NormalX=0 NormalY=0 NormalZ=1 AngleXU=0 Radius=1
    g2: Circle CenterX=8 CenterY=6 CenterZ=0 NormalX=0 NormalY=0 NormalZ=1 AngleXU=0 Radius=1
    g3: BSplineCurve PolesCount=3 KnotsCount=2 Degree=2 IsPeriodic=0
    g4: GeomPoint X=0 Y=0 Z=0
    g5: GeomPoint X=8 Y=6 Z=0
    g6: LineSegment StartX=0 StartY=6 StartZ=0 EndX=8 EndY=6 EndZ=0
  constraints (14):
    c: Coincident(g0,g-1)
    c: Distance(g0) = 6
    c: Vertical(g0)
    c: Coincident(g3,g0)
    c: Weight(g1) = 1
    c: Equal(g1,g2)
    c: InternalAlignment(g1,g3)
    c: InternalAlignment(g2,g3)
    c: InternalAlignment(g4,g3)
    c: InternalAlignment(g5,g3)
    c: Block(g3)
    c: Coincident(g6,g0)
    c: Coincident(g6,g3)
    c: Horizontal(g6)
FEATURE [Part::Extrusion] Extrude018  label="caseScrewPillarBracket006"
  Base = -> Sketch024
  Dir = (0,0,1)
  DirMode = 2
  FaceMakerClass = Part::FaceMakerBullseye
  LengthFwd = 2.4
  LengthRev = 0
  Placement = pos=(103.7,29,6.77) rot=(0,-1,0;1.5708rad)
  Solid = true
  Symmetric = false
FEATURE [Sketcher::SketchObject] Sketch025
  FullyConstrained = true
  sketch-geometry (7):
    g0: LineSegment StartX=0 StartY=0 StartZ=0 EndX=0 EndY=6 EndZ=0
    g1: Circle CenterX=0 CenterY=0 CenterZ=0 NormalX=0 NormalY=0 NormalZ=1 AngleXU=0 Radius=1
    g2: Circle CenterX=8 CenterY=6 CenterZ=0 NormalX=0 NormalY=0 NormalZ=1 AngleXU=0 Radius=1
    g3: BSplineCurve PolesCount=3 KnotsCount=2 Degree=2 IsPeriodic=0
    g4: GeomPoint X=0 Y=0 Z=0
    g5: GeomPoint X=8 Y=6 Z=0
    g6: LineSegment StartX=0 StartY=6 StartZ=0 EndX=8 EndY=6 EndZ=0
  constraints (14):
    c: Coincident(g0,g-1)
    c: Distance(g0) = 6
    c: Vertical(g0)
    c: Coincident(g3,g0)
    c: Weight(g1) = 1
    c: Equal(g1,g2)
    c: InternalAlignment(g1,g3)
    c: InternalAlignment(g2,g3)
    c: InternalAlignment(g4,g3)
    c: InternalAlignment(g5,g3)
    c: Block(g3)
    c: Coincident(g6,g0)
    c: Coincident(g6,g3)
    c: Horizontal(g6)
FEATURE [Part::Extrusion] Extrude019  label="caseScrewPillarBracket007"
  Base = -> Sketch025
  Dir = (0,0,1)
  DirMode = 2
  FaceMakerClass = Part::FaceMakerBullseye
  LengthFwd = 2.4
  LengthRev = 0
  Placement = pos=(101.3,29,65.23) rot=(0,1,0;1.5708rad)
  Solid = true
  Symmetric = false
FEATURE [Part::Box] Box011  label="frontCaseScrewPillarBracket"
  AttacherType = Attacher::AttachEngine3D
  Height = 2.4
  Length = 16
  Placement = pos=(87,28,2.3) rot=(0,0,1;0rad)
  Width = 7
FEATURE [Part::Box] Box012  label="frontCaseScrewPillarBracket001"
  AttacherType = Attacher::AttachEngine3D
  Height = 2.4
  Length = 16
  Placement = pos=(87,28,67.3) rot=(0,0,1;0rad)
  Width = 7
FEATURE [Sketcher::SketchObject] Sketch026
  FullyConstrained = true
  sketch-geometry (17):
    g0: Circle CenterX=-3.5 CenterY=23.5 CenterZ=0 NormalX=0 NormalY=0 NormalZ=1 AngleXU=0 Radius=1
    g1: Circle CenterX=-1 CenterY=15.25 CenterZ=0 NormalX=0 NormalY=0 NormalZ=1 AngleXU=0 Radius=1
    g2: Circle CenterX=-3.5 CenterY=7 CenterZ=0 NormalX=0 NormalY=0 NormalZ=1 AngleXU=0 Radius=1
    g3: BSplineCurve PolesCount=3 KnotsCount=2 Degree=2 IsPeriodic=0
    g4: GeomPoint X=-3.5 Y=23.5 Z=0
    g5: GeomPoint X=-3.5 Y=7 Z=0
    g6: Circle CenterX=-4.8 CenterY=30.5 CenterZ=0 NormalX=0 NormalY=0 NormalZ=1 AngleXU=0 Radius=1
    g7: Circle CenterX=-3.5 CenterY=30.5 CenterZ=0 NormalX=0 NormalY=0 NormalZ=1 AngleXU=0 Radius=1
    g8: Circle CenterX=-3.5 CenterY=29.2 CenterZ=0 NormalX=0 NormalY=0 NormalZ=1 AngleXU=0 Radius=1
    g9: BSplineCurve PolesCount=3 KnotsCount=2 Degree=2 IsPeriodic=0
    g10: GeomPoint X=-4.8 Y=30.5 Z=0
    g11: GeomPoint X=-3.5 Y=29.2 Z=0
    g12: LineSegment StartX=-3.5 StartY=29.2 StartZ=0 EndX=-3.5 EndY=23.5 EndZ=0
    g13: LineSegment StartX=-4.8 StartY=30.5 StartZ=0 EndX=0 EndY=30.5 EndZ=0
    g14: LineSegment StartX=-3.5 StartY=5 StartZ=0 EndX=-3.5 EndY=7 EndZ=0
    g15: LineSegment StartX=0 StartY=5 StartZ=0 EndX=0 EndY=30.5 EndZ=0
    g16: LineSegment StartX=-3.5 StartY=5 StartZ=0 EndX=0 EndY=5 EndZ=0
  constraints (33):
    c: Weight(g0) = 1
    c: Equal(g0,g1)
    c: Equal(g0,g2)
    c: InternalAlignment(g0,g3)
    c: InternalAlignment(g1,g3)
    c: InternalAlignment(g2,g3)
    c: InternalAlignment(g4,g3)
    c: InternalAlignment(g5,g3)
    c: Block(g3)
    c: Weight(g6) = 1
    c: Equal(g6,g7)
    c: Equal(g6,g8)
    c: InternalAlignment(g6,g9)
    c: InternalAlignment(g7,g9)
    c: InternalAlignment(g8,g9)
    c: InternalAlignment(g10,g9)
    c: InternalAlignment(g11,g9)
    c: Block(g9)
    c: Coincident(g12,g9)
    c: Coincident(g12,g3)
    c: Vertical(g12)
    c: Coincident(g13,g9)
    c: Horizontal(g13)
    c: Distance(g13) = 4.8
    c: Coincident(g14,g3)
    c: Vertical(g14)
    c: Coincident(g15,g13)
    c: Vertical(g15)
    c: Tangent(g15,g1)
    c: Distance(g14) = 2
    c: Coincident(g16,g14)
    c: Horizontal(g16)
    c: Coincident(g15,g16)
FEATURE [Part::Feature] Face050
  shape: bbox 4.8 x 25.5 x 2e-07 mm, 1 faces, 0 solids (baked)
FEATURE [Part::Revolution] Revolve054  label="moreFrontCaseScrewPost001"
  Angle = 360
  Axis = (0,1,0)
  Base = (0,0,0)
  FaceMakerClass = Part::FaceMakerBullseye
  Placement = pos=(102.5,4.5,3.5) rot=(0,0,1;0rad)
  Solid = false
  Source = -> Face050
  Symmetric = false
FEATURE [Part::Feature] Face051
  shape: bbox 4.8 x 25.5 x 2e-07 mm, 1 faces, 0 solids (baked)
FEATURE [Part::Revolution] Revolve055  label="moreFrontCaseScrewPost002"
  Angle = 360
  Axis = (0,1,0)
  Base = (0,0,0)
  FaceMakerClass = Part::FaceMakerBullseye
  Placement = pos=(102.5,4.5,68.5) rot=(0,0,1;0rad)
  Solid = false
  Source = -> Face051
  Symmetric = false
FEATURE [Sketcher::SketchObject] Sketch027
  FullyConstrained = true
  sketch-geometry (10):
    g0: LineSegment StartX=-1.6 StartY=4.7 StartZ=0 EndX=-1.6 EndY=1.7 EndZ=0
    g1: LineSegment StartX=-3.5 StartY=4.7 StartZ=0 EndX=-1.6 EndY=4.7 EndZ=0
    g2: LineSegment StartX=-1.6 StartY=1.7 StartZ=0 EndX=-1.6 EndY=1.5 EndZ=0
    g3: LineSegment StartX=-1.6 StartY=1.5 StartZ=0 EndX=-5.2 EndY=1.5 EndZ=0
    g4: Circle CenterX=-3.5 CenterY=4.7 CenterZ=0 NormalX=0 NormalY=0 NormalZ=1 AngleXU=0 Radius=1
    g5: Circle CenterX=-3.59627 CenterY=2.99743 CenterZ=0 NormalX=0 NormalY=0 NormalZ=1 AngleXU=0 Radius=1
    g6: Circle CenterX=-5.2 CenterY=1.5 CenterZ=0 NormalX=0 NormalY=0 NormalZ=1 AngleXU=0 Radius=1
    g7: BSplineCurve PolesCount=3 KnotsCount=2 Degree=2 IsPeriodic=0
    g8: GeomPoint X=-3.5 Y=4.7 Z=0
    g9: GeomPoint X=-5.2 Y=1.5 Z=0
  constraints (23):
    c: Vertical(g0)
    c: Distance(g0) = 3
    c: Coincident(g1,g0)
    c: Horizontal(g1)
    c: Block(g0)
    c: Block(g1)
    c: Coincident(g2,g0)
    c: Vertical(g2)
    c: Distance(g2) = 0.2
    c: Coincident(g3,g2)
    c: Horizontal(g3)
    c: Block(g3)
    c: Coincident(g7,g1)
    c: Weight(g4) = 1
    c: Equal(g4,g5)
    c: Equal(g4,g6)
    c: Coincident(g7,g3)
    c: InternalAlignment(g4,g7)
    c: InternalAlignment(g5,g7)
    c: InternalAlignment(g6,g7)
    c: InternalAlignment(g8,g7)
    c: InternalAlignment(g9,g7)
    c: Block(g7)
FEATURE [Sketcher::SketchObject] Sketch028
  FullyConstrained = true
  sketch-geometry (18):
    g0: LineSegment StartX=0 StartY=3e-16 StartZ=0 EndX=0 EndY=1.7 EndZ=0
    g1: LineSegment StartX=-3.5 StartY=0 StartZ=0 EndX=-3.5 EndY=0.9 EndZ=0
    g2: Circle CenterX=-2.7 CenterY=1.7 CenterZ=0 NormalX=0 NormalY=0 NormalZ=1 AngleXU=0 Radius=1
    g3: Circle CenterX=-3.5 CenterY=1.7 CenterZ=0 NormalX=0 NormalY=0 NormalZ=1 AngleXU=0 Radius=1
    g4: Circle CenterX=-3.5 CenterY=0.9 CenterZ=0 NormalX=0 NormalY=0 NormalZ=1 AngleXU=0 Radius=1
    g5: BSplineCurve PolesCount=3 KnotsCount=2 Degree=2 IsPeriodic=0
    g6: GeomPoint X=-2.7 Y=1.7 Z=0
    g7: GeomPoint X=-3.5 Y=0.9 Z=0
    g8: LineSegment StartX=-3.5 StartY=0 StartZ=0 EndX=-3.5 EndY=-7 EndZ=0
    g9: LineSegment StartX=0 StartY=3e-16 StartZ=0 EndX=0 EndY=-7 EndZ=0
    g10: LineSegment StartX=-3.5 StartY=-7 StartZ=0 EndX=0 EndY=-7 EndZ=0
    g11: LineSegment StartX=-2.7 StartY=1.7 StartZ=0 EndX=-1.6 EndY=1.7 EndZ=0
    g12: LineSegment StartX=0 StartY=1.7 StartZ=0 EndX=0 EndY=4.5 EndZ=0
    g13: LineSegment StartX=0 StartY=4.5 StartZ=0 EndX=0 EndY=10.8 EndZ=0
    g14: LineSegment StartX=0 StartY=10.8 StartZ=0 EndX=-2 EndY=10.8 EndZ=0
    g15: LineSegment StartX=-1.6 StartY=4.7 StartZ=0 EndX=-1.6 EndY=1.7 EndZ=0
    g16: LineSegment StartX=-1.6 StartY=4.7 StartZ=0 EndX=-2 EndY=4.7 EndZ=0
    g17: LineSegment StartX=-2 StartY=4.7 StartZ=0 EndX=-2 EndY=10.8 EndZ=0
  constraints (44):
    c: Vertical(g0)
    c: Vertical(g1)
    c: Distance(g1) = 0.9
    c: Block(g0)
    c: Distance(g0) = 1.7
    c: Weight(g2) = 1
    c: Equal(g2,g3)
    c: Equal(g2,g4)
    c: Coincident(g5,g1)
    c: InternalAlignment(g2,g5)
    c: InternalAlignment(g3,g5)
    c: InternalAlignment(g4,g5)
    c: InternalAlignment(g6,g5)
    c: InternalAlignment(g7,g5)
    c: Block(g5)
    c: Coincident(g8,g1)
    c: Vertical(g8)
    c: Distance(g8) = 7
    c: Vertical(g9)
    c: Equal(g8,g9) = 7
    c: Coincident(g9,g0)
    c: Coincident(g10,g8)
    c: Coincident(g10,g9)
    c: Horizontal(g10)
    c: Coincident(g11,g5)
    c: Horizontal(g11)
    c: Coincident(g12,g0)
    c: Vertical(g12)
    c: Distance(g12) = 2.8
    c: Coincident(g13,g12)
    c: Vertical(g13)
    c: Distance(g13) = 6.3
    c: Coincident(g14,g13)
    c: Horizontal(g14)
    c: Distance(g14) = 2
    c: Vertical(g15)
    c: Distance(g15) = 3
    c: Block(g11)
    c: Coincident(g15,g11)
    c: Coincident(g16,g15)
    c: Horizontal(g16)
    c: Coincident(g17,g16)
    c: Coincident(g17,g14)
    c: Vertical(g17)
FEATURE [Part::Revolution] Revolve040  label="backCaseScrewRetainer001"
  Angle = 360
  Axis = (0,1,0)
  Base = (0,0,0)
  FaceMakerClass = Part::FaceMakerBullseye
  Placement = pos=(12.5,3,10) rot=(0,0,1;0rad)
  Solid = false
  Source = -> Face036
  Symmetric = false
FEATURE [Part::Feature] Face055
  shape: bbox 3.5 x 30.2 x 2e-07 mm, 1 faces, 0 solids (baked)
FEATURE [Part::Revolution] Revolve059  label="backCaseScrewPost"
  Angle = 360
  Axis = (0,1,0)
  Base = (0,0,0)
  FaceMakerClass = Part::FaceMakerBullseye
  Placement = pos=(12.5,4.5,10) rot=(0,0,1;0rad)
  Solid = false
  Source = -> Face055
  Symmetric = false
FEATURE [Part::Feature] Face056
  shape: bbox 3.5 x 30.2 x 2e-07 mm, 1 faces, 0 solids (baked)
FEATURE [Part::Revolution] Revolve060  label="backCaseScrewPost001"
  Angle = 360
  Axis = (0,1,0)
  Base = (0,0,0)
  FaceMakerClass = Part::FaceMakerBullseye
  Placement = pos=(12.5,4.5,62) rot=(0,0,1;0rad)
  Solid = false
  Source = -> Face056
  Symmetric = false
FEATURE [Part::Feature] Face057
  shape: bbox 3.5 x 17.8 x 2e-07 mm, 1 faces, 0 solids (baked)
FEATURE [Part::Revolution] Revolve061  label="removeToCreateScrewAndThreadedInsertHole"
  Angle = 360
  Axis = (0,1,0)
  Base = (0,0,0)
  FaceMakerClass = Part::FaceMakerBullseye
  Placement = pos=(12.5,0,10) rot=(0,0,1;0rad)
  Solid = false
  Source = -> Face057
  Symmetric = false
FEATURE [Part::Feature] Face058
  shape: bbox 3.5 x 17.8 x 2e-07 mm, 1 faces, 0 solids (baked)
FEATURE [Part::Revolution] Revolve062  label="removeToCreateScrewAndThreadedInsertHole001"
  Angle = 360
  Axis = (0,1,0)
  Base = (0,0,0)
  FaceMakerClass = Part::FaceMakerBullseye
  Placement = pos=(12.5,0,62) rot=(0,0,1;0rad)
  Solid = false
  Source = -> Face058
  Symmetric = false
FEATURE [Part::Feature] Face059
  shape: bbox 3.5 x 17.8 x 2e-07 mm, 1 faces, 0 solids (baked)
FEATURE [Part::Revolution] Revolve063  label="removeToCreateScrewAndThreadedInsertHole002"
  Angle = 360
  Axis = (0,1,0)
  Base = (0,0,0)
  FaceMakerClass = Part::FaceMakerBullseye
  Placement = pos=(89.5,0,68.5) rot=(0,0,1;0rad)
  Solid = false
  Source = -> Face059
  Symmetric = false
FEATURE [Part::Feature] Face060
  shape: bbox 3.5 x 17.8 x 2e-07 mm, 1 faces, 0 solids (baked)
FEATURE [Part::Revolution] Revolve064  label="removeToCreateScrewAndThreadedInsertHole003"
  Angle = 360
  Axis = (0,1,0)
  Base = (0,0,0)
  FaceMakerClass = Part::FaceMakerBullseye
  Placement = pos=(89.5,0,3.5) rot=(0,0,1;0rad)
  Solid = false
  Source = -> Face060
  Symmetric = false
FEATURE [Part::Feature] Face061
  shape: bbox 3.5 x 17.8 x 2e-07 mm, 1 faces, 0 solids (baked)
FEATURE [Part::Revolution] Revolve065  label="removeToCreateScrewAndThreadedInsertHole004"
  Angle = 360
  Axis = (0,1,0)
  Base = (0,0,0)
  FaceMakerClass = Part::FaceMakerBullseye
  Placement = pos=(102.5,4.7,3.5) rot=(0,0,1;0rad)
  Solid = false
  Source = -> Face061
  Symmetric = false
FEATURE [Part::Feature] Face062
  shape: bbox 3.5 x 17.8 x 2e-07 mm, 1 faces, 0 solids (baked)
FEATURE [Part::Revolution] Revolve066  label="removeToCreateScrewAndThreadedInsertHole005"
  Angle = 360
  Axis = (0,1,0)
  Base = (0,0,0)
  FaceMakerClass = Part::FaceMakerBullseye
  Placement = pos=(102.5,4.7,68.5) rot=(0,0,1;0rad)
  Solid = false
  Source = -> Face062
  Symmetric = false
FEATURE [Part::MultiFuse] Fusion047  label="makeHoles"
  Shapes = -> [Revolve066,Revolve065,Revolve064,Revolve063,Revolve062,Revolve061]
FEATURE [Part::Feature] Face063
  shape: bbox 3.6 x 3.2 x 2e-07 mm, 1 faces, 0 solids (baked)
FEATURE [Part::Revolution] Revolve067  label="moreFrontCaseScrewRetainer002"
  Angle = 360
  Axis = (0,1,0)
  Base = (0,0,0)
  FaceMakerClass = Part::FaceMakerBullseye
  Placement = pos=(102.5,4.5,68.5) rot=(0,0,1;0rad)
  Solid = false
  Source = -> Face063
  Symmetric = false
FEATURE [Part::Feature] Face064
  shape: bbox 3.6 x 3.2 x 2e-07 mm, 1 faces, 0 solids (baked)
FEATURE [Part::Revolution] Revolve068  label="moreFrontCaseScrewRetainer003"
  Angle = 360
  Axis = (0,1,0)
  Base = (0,0,0)
  FaceMakerClass = Part::FaceMakerBullseye
  Placement = pos=(102.5,4.5,3.5) rot=(0,0,1;0rad)
  Solid = false
  Source = -> Face064
  Symmetric = false
FEATURE [Part::Feature] Face065
  shape: bbox 3.5 x 17.8 x 2e-07 mm, 1 faces, 0 solids (baked)
FEATURE [Part::Revolution] Revolve069  label="removeToCreateScrewAndThreadedInsertHole006"
  Angle = 360
  Axis = (0,1,0)
  Base = (0,0,0)
  FaceMakerClass = Part::FaceMakerBullseye
  Placement = pos=(12.5,0,10) rot=(0,0,1;0rad)
  Solid = false
  Source = -> Face065
  Symmetric = false
FEATURE [Part::Feature] Face066
  shape: bbox 3.5 x 17.8 x 2e-07 mm, 1 faces, 0 solids (baked)
FEATURE [Part::Revolution] Revolve070  label="removeToCreateScrewAndThreadedInsertHole007"
  Angle = 360
  Axis = (0,1,0)
  Base = (0,0,0)
  FaceMakerClass = Part::FaceMakerBullseye
  Placement = pos=(12.5,0,62) rot=(0,0,1;0rad)
  Solid = false
  Source = -> Face066
  Symmetric = false
FEATURE [Part::Feature] Face067
  shape: bbox 3.5 x 17.8 x 2e-07 mm, 1 faces, 0 solids (baked)
FEATURE [Part::Revolution] Revolve071  label="removeToCreateScrewAndThreadedInsertHole008"
  Angle = 360
  Axis = (0,1,0)
  Base = (0,0,0)
  FaceMakerClass = Part::FaceMakerBullseye
  Placement = pos=(89.5,0,68.5) rot=(0,0,1;0rad)
  Solid = false
  Source = -> Face067
  Symmetric = false
FEATURE [Part::Feature] Face068
  shape: bbox 3.5 x 17.8 x 2e-07 mm, 1 faces, 0 solids (baked)
FEATURE [Part::Revolution] Revolve072  label="removeToCreateScrewAndThreadedInsertHole009"
  Angle = 360
  Axis = (0,1,0)
  Base = (0,0,0)
  FaceMakerClass = Part::FaceMakerBullseye
  Placement = pos=(89.5,0,3.5) rot=(0,0,1;0rad)
  Solid = false
  Source = -> Face068
  Symmetric = false
FEATURE [Part::Feature] Face069
  shape: bbox 3.5 x 17.8 x 2e-07 mm, 1 faces, 0 solids (baked)
FEATURE [Part::Feature] Face070
  shape: bbox 3.5 x 17.8 x 2e-07 mm, 1 faces, 0 solids (baked)
FEATURE [Part::Revolution] Revolve073  label="removeToCreateScrewAndThreadedInsertHole010"
  Angle = 360
  Axis = (0,1,0)
  Base = (0,0,0)
  FaceMakerClass = Part::FaceMakerBullseye
  Placement = pos=(102.5,4.7,3.5) rot=(0,0,1;0rad)
  Solid = false
  Source = -> Face069
  Symmetric = false
FEATURE [Part::Revolution] Revolve074  label="removeToCreateScrewAndThreadedInsertHole011"
  Angle = 360
  Axis = (0,1,0)
  Base = (0,0,0)
  FaceMakerClass = Part::FaceMakerBullseye
  Placement = pos=(102.5,4.7,68.5) rot=(0,0,1;0rad)
  Solid = false
  Source = -> Face070
  Symmetric = false
FEATURE [Part::MultiFuse] Fusion048  label="makeHoles001"
  Shapes = -> [Revolve074,Revolve073,Revolve072,Revolve071,Revolve070,Revolve069]
FEATURE [Part::MultiFuse] Fusion049  label="caseScrewRetainers"
  Shapes = -> [Revolve067,Revolve068,Revolve048,Revolve047,Revolve039,Revolve040]
FEATURE [Part::Cut] Cut015  label="caseScrewRetainers001"
  Base = -> Fusion049
  Tool = -> Fusion048
FEATURE [Part::MultiFuse] Fusion050  label="casePillars"
  Shapes = -> [Revolve055,Revolve054,Revolve043,Revolve046,Revolve059,Revolve060]
FEATURE [Part::Feature] Face071 .. Face076  x6 (patterned run collapsed; names and placements below)
  shape: bbox 3.5 x 17.8 x 2e-07 mm, 1 faces, 0 solids (baked)
FEATURE [Part::Revolution] Revolve075  label="removeToCreateScrewAndThreadedInsertHole012"
  Angle = 360
  Axis = (0,1,0)
  Base = (0,0,0)
  FaceMakerClass = Part::FaceMakerBullseye
  Placement = pos=(12.5,0,10) rot=(0,0,1;0rad)
  Solid = false
  Source = -> Face071
  Symmetric = false
FEATURE [Part::Revolution] Revolve076  label="removeToCreateScrewAndThreadedInsertHole013"
  Angle = 360
  Axis = (0,1,0)
  Base = (0,0,0)
  FaceMakerClass = Part::FaceMakerBullseye
  Placement = pos=(12.5,0,62) rot=(0,0,1;0rad)
  Solid = false
  Source = -> Face072
  Symmetric = false
FEATURE [Part::Revolution] Revolve077  label="removeToCreateScrewAndThreadedInsertHole014"
  Angle = 360
  Axis = (0,1,0)
  Base = (0,0,0)
  FaceMakerClass = Part::FaceMakerBullseye
  Placement = pos=(89.5,0,68.5) rot=(0,0,1;0rad)
  Solid = false
  Source = -> Face073
  Symmetric = false
FEATURE [Part::Revolution] Revolve078  label="removeToCreateScrewAndThreadedInsertHole015"
  Angle = 360
  Axis = (0,1,0)
  Base = (0,0,0)
  FaceMakerClass = Part::FaceMakerBullseye
  Placement = pos=(89.5,0,3.5) rot=(0,0,1;0rad)
  Solid = false
  Source = -> Face074
  Symmetric = false
FEATURE [Part::Revolution] Revolve079  label="removeToCreateScrewAndThreadedInsertHole016"
  Angle = 360
  Axis = (0,1,0)
  Base = (0,0,0)
  FaceMakerClass = Part::FaceMakerBullseye
  Placement = pos=(102.5,4.7,3.5) rot=(0,0,1;0rad)
  Solid = false
  Source = -> Face075
  Symmetric = false
FEATURE [Part::Revolution] Revolve080  label="removeToCreateScrewAndThreadedInsertHole017"
  Angle = 360
  Axis = (0,1,0)
  Base = (0,0,0)
  FaceMakerClass = Part::FaceMakerBullseye
  Placement = pos=(102.5,4.7,68.5) rot=(0,0,1;0rad)
  Solid = false
  Source = -> Face076
  Symmetric = false
FEATURE [Part::MultiFuse] Fusion051  label="makeHoles002"
  Shapes = -> [Revolve080,Revolve079,Revolve078,Revolve077,Revolve076,Revolve075]
FEATURE [Part::Cut] Cut016  label="caesPillars"
  Base = -> Fusion050
  Tool = -> Fusion051
FEATURE [Part::Revolution] Revolve009  label="plugHousing016"
  Angle = 360
  Axis = (0,1,0)
  Base = (0,0,0)
  FaceMakerClass = Part::FaceMakerBullseye
  Placement = pos=(0,0,36.15) rot=(0,0,1;0rad)
  Solid = false
  Source = -> Face012
  Symmetric = false
FEATURE [Part::MultiFuse] Fusion014  label="plugHousing023"
  Placement = pos=(0,0,0) rot=(0,0,1;1.5708rad)
  Shapes = -> [Revolve011,Revolve009]
FEATURE [Part::Revolution] Revolve010  label="plugHousing017"
  Angle = 360
  Axis = (0,1,0)
  Base = (0,0,0)
  FaceMakerClass = Part::FaceMakerBullseye
  Placement = pos=(0,0,36.15) rot=(0,0,1;0rad)
  Solid = false
  Source = -> Face014
  Symmetric = false
FEATURE [Part::MultiFuse] Fusion015  label="plugHousing024"
  Placement = pos=(0,0,0) rot=(0,0,1;1.5708rad)
  Shapes = -> [Revolve010,Revolve015]
FEATURE [Part::Revolution] Revolve014  label="plugHousing026"
  Angle = 360
  Axis = (0,1,0)
  Base = (0,0,0)
  FaceMakerClass = Part::FaceMakerBullseye
  Placement = pos=(0,0,36.15) rot=(0,0,1;0rad)
  Solid = false
  Source = -> Face011
  Symmetric = false
FEATURE [Part::Revolution] Revolve013  label="plugHousing025"
  Angle = 360
  Axis = (0,1,0)
  Base = (0,0,0)
  FaceMakerClass = Part::FaceMakerBullseye
  Placement = pos=(0,0,36.15) rot=(0,0,1;0rad)
  Solid = false
  Source = -> Face015
  Symmetric = false
FEATURE [Part::MultiFuse] Fusion016  label="plugHousing028"
  Placement = pos=(0,19,0) rot=(0,0,1;3.14159rad)
  Shapes = -> [Fusion014,Fusion013]
FEATURE [Part::MultiFuse] Fusion011  label="plugHousing018"
  Placement = pos=(0,0,0) rot=(0,0,1;1.5708rad)
  Shapes = -> [Revolve014,Revolve013]
FEATURE [Part::MultiFuse] Fusion012  label="plugHousing019"
  Placement = pos=(0,19,0) rot=(0,0,1;3.14159rad)
  Shapes = -> [Fusion011,Fusion015]
FEATURE [Part::MultiFuse] Fusion017  label="plugHousing029"
  Placement = pos=(122.621,0,-0.15) rot=(0,0,1;0rad)
  Shapes = -> [Fusion016,Fusion012]
FEATURE [Part::MultiFuse] Fusion052  label="casePillarRetainers"
  Shapes = -> [Extrude012,Extrude013,Extrude014,Extrude015,Extrude016,Extrude017,Extrude018,Extrude019,Box011,Box012]
FEATURE [Part::Feature] Face077
  shape: bbox 3.5 x 17.8 x 2e-07 mm, 1 faces, 0 solids (baked)
FEATURE [Part::Revolution] Revolve081  label="removeToCreateScrewAndThreadedInsertHole018"
  Angle = 360
  Axis = (0,1,0)
  Base = (0,0,0)
  FaceMakerClass = Part::FaceMakerBullseye
  Placement = pos=(62.3,30.3,19.7) rot=(0,0,1;0rad)
  Solid = false
  Source = -> Face077
  Symmetric = false
FEATURE [Part::Feature] Face078
  shape: bbox 3.5 x 17.8 x 2e-07 mm, 1 faces, 0 solids (baked)
FEATURE [Part::Revolution] Revolve082  label="removeToCreateScrewAndThreadedInsertHole019"
  Angle = 360
  Axis = (0,1,0)
  Base = (0,0,0)
  FaceMakerClass = Part::FaceMakerBullseye
  Placement = pos=(62.3,30.3,51.7) rot=(0,0,1;0rad)
  Solid = false
  Source = -> Face078
  Symmetric = false
FEATURE [Part::Feature] Face079
  shape: bbox 3.5 x 17.8 x 2e-07 mm, 1 faces, 0 solids (baked)
FEATURE [Part::Revolution] Revolve083  label="removeToCreateScrewAndThreadedInsertHole020"
  Angle = 360
  Axis = (0,1,0)
  Base = (0,0,0)
  FaceMakerClass = Part::FaceMakerBullseye
  Placement = pos=(30.3,30.3,19.7) rot=(0,0,1;0rad)
  Solid = false
  Source = -> Face079
  Symmetric = false
FEATURE [Part::Feature] Face080
  shape: bbox 3.5 x 17.8 x 2e-07 mm, 1 faces, 0 solids (baked)
FEATURE [Part::Revolution] Revolve084  label="removeToCreateScrewAndThreadedInsertHole021"
  Angle = 360
  Axis = (0,1,0)
  Base = (0,0,0)
  FaceMakerClass = Part::FaceMakerBullseye
  Placement = pos=(30.3,30.3,51.7) rot=(0,0,1;0rad)
  Solid = false
  Source = -> Face080
  Symmetric = false
FEATURE [Part::MultiFuse] Fusion053  label="createThreadedInsertHolesForFan"
  Shapes = -> [Revolve081,Revolve082,Revolve083,Revolve084]
FEATURE [Part::Cut] Cut017  label="fanScrewHousing001"
  Base = -> Fusion046
  Tool = -> Fusion053
FEATURE [Part::Feature] Face081
  shape: bbox 3.5 x 17.8 x 2e-07 mm, 1 faces, 0 solids (baked)
FEATURE [Part::Revolution] Revolve085  label="removeToCreateScrewAndThreadedInsertHole022"
  Angle = 360
  Axis = (0,1,0)
  Base = (0,0,0)
  FaceMakerClass = Part::FaceMakerBullseye
  Placement = pos=(62.3,30.3,19.7) rot=(0,0,1;0rad)
  Solid = false
  Source = -> Face081
  Symmetric = false
FEATURE [Part::Feature] Face082
  shape: bbox 3.5 x 17.8 x 2e-07 mm, 1 faces, 0 solids (baked)
FEATURE [Part::Revolution] Revolve086  label="removeToCreateScrewAndThreadedInsertHole023"
  Angle = 360
  Axis = (0,1,0)
  Base = (0,0,0)
  FaceMakerClass = Part::FaceMakerBullseye
  Placement = pos=(62.3,30.3,51.7) rot=(0,0,1;0rad)
  Solid = false
  Source = -> Face082
  Symmetric = false
FEATURE [Part::Feature] Face083
  shape: bbox 3.5 x 17.8 x 2e-07 mm, 1 faces, 0 solids (baked)
FEATURE [Part::Revolution] Revolve087  label="removeToCreateScrewAndThreadedInsertHole024"
  Angle = 360
  Axis = (0,1,0)
  Base = (0,0,0)
  FaceMakerClass = Part::FaceMakerBullseye
  Placement = pos=(30.3,30.3,19.7) rot=(0,0,1;0rad)
  Solid = false
  Source = -> Face083
  Symmetric = false
FEATURE [Part::Feature] Face084
  shape: bbox 3.5 x 17.8 x 2e-07 mm, 1 faces, 0 solids (baked)
FEATURE [Part::Revolution] Revolve088  label="removeToCreateScrewAndThreadedInsertHole025"
  Angle = 360
  Axis = (0,1,0)
  Base = (0,0,0)
  FaceMakerClass = Part::FaceMakerBullseye
  Placement = pos=(30.3,30.3,51.7) rot=(0,0,1;0rad)
  Solid = false
  Source = -> Face084
  Symmetric = false
FEATURE [Part::MultiFuse] Fusion054  label="createThreadedInsertHolesForFan001"
  Shapes = -> [Revolve085,Revolve086,Revolve087,Revolve088]
FEATURE [Part::Cut] Cut018  label="top007"
  Base = -> Fusion040
  Tool = -> Fusion054
FEATURE [Sketcher::SketchObject] Sketch029
  FullyConstrained = false
  Placement = pos=(0,0,0) rot=(1,0,0;1.5708rad)
  sketch-geometry (24):
    g0: ArcOfCircle CenterX=-4 CenterY=-10.5 CenterZ=0 NormalX=0 NormalY=0 NormalZ=1 AngleXU=0 Radius=1.5 StartAngle=6e-16 EndAngle=3.14159
    g1: ArcOfCircle CenterX=-34.2 CenterY=-10.5 CenterZ=0 NormalX=0 NormalY=0 NormalZ=1 AngleXU=0 Radius=1.5 StartAngle=0 EndAngle=3.14159
    g2: ArcOfCircle CenterX=-34.2 CenterY=-27.7 CenterZ=0 NormalX=0 NormalY=0 NormalZ=1 AngleXU=0 Radius=1.5 StartAngle=3.14159 EndAngle=6.28319
    g3: ArcOfCircle CenterX=-4 CenterY=-27.7 CenterZ=0 NormalX=0 NormalY=0 NormalZ=1 AngleXU=0 Radius=1.5 StartAngle=3.1416 EndAngle=6.28319
    g4: ArcOfCircle CenterX=-10 CenterY=-4.3 CenterZ=0 NormalX=0 NormalY=0 NormalZ=1 AngleXU=0 Radius=1.5 StartAngle=2e-16 EndAngle=3.14159
    g5: ArcOfCircle CenterX=-16.1 CenterY=-1.8 CenterZ=0 NormalX=0 NormalY=0 NormalZ=1 AngleXU=0 Radius=1.5 StartAngle=5e-16 EndAngle=3.14159
    g6: ArcOfCircle CenterX=-22.1 CenterY=-1.8 CenterZ=0 NormalX=0 NormalY=0 NormalZ=1 AngleXU=0 Radius=1.5 StartAngle=5e-16 EndAngle=3.14159
    g7: ArcOfCircle CenterX=-28.2 CenterY=-4.3 CenterZ=0 NormalX=0 NormalY=0 NormalZ=1 AngleXU=0 Radius=1.5 StartAngle=2e-16 EndAngle=3.14159
    g8: ArcOfCircle CenterX=-10 CenterY=-33.9 CenterZ=0 NormalX=0 NormalY=0 NormalZ=1 AngleXU=0 Radius=1.5 StartAngle=3.14159 EndAngle=6.28319
    g9: ArcOfCircle CenterX=-16.1 CenterY=-36.4 CenterZ=0 NormalX=0 NormalY=0 NormalZ=1 AngleXU=0 Radius=1.5 StartAngle=3.14159 EndAngle=6.28319
    g10: ArcOfCircle CenterX=-22.1 CenterY=-36.4 CenterZ=0 NormalX=0 NormalY=0 NormalZ=1 AngleXU=0 Radius=1.5 StartAngle=3.14159 EndAngle=6.28319
    g11: ArcOfCircle CenterX=-28.2 CenterY=-33.9 CenterZ=0 NormalX=0 NormalY=0 NormalZ=1 AngleXU=0 Radius=1.5 StartAngle=3.14159 EndAngle=6.28319
    g12: LineSegment StartX=-35.7 StartY=-10.5 StartZ=0 EndX=-35.7 EndY=-27.7 EndZ=0
    g13: LineSegment StartX=-32.7 StartY=-10.5 StartZ=0 EndX=-32.7 EndY=-27.7 EndZ=0
    g14: LineSegment StartX=-29.7 StartY=-33.9 StartZ=0 EndX=-29.7 EndY=-4.3 EndZ=0
    g15: LineSegment StartX=-26.7 StartY=-33.9 StartZ=0 EndX=-26.7 EndY=-4.3 EndZ=0
    g16: LineSegment StartX=-2.5 StartY=-10.5 StartZ=0 EndX=-2.5 EndY=-27.7 EndZ=0
    g17: LineSegment StartX=-8.5 StartY=-4.3 StartZ=0 EndX=-8.5 EndY=-33.9 EndZ=0
    g18: LineSegment StartX=-5.5 StartY=-10.5 StartZ=0 EndX=-5.5 EndY=-27.7 EndZ=0
    g19: LineSegment StartX=-11.5 StartY=-4.3 StartZ=0 EndX=-11.5 EndY=-33.9 EndZ=0
    g20: LineSegment StartX=-14.6 StartY=-1.8 StartZ=0 EndX=-14.6 EndY=-36.4 EndZ=0
    g21: LineSegment StartX=-17.6 StartY=-1.8 StartZ=0 EndX=-17.6 EndY=-36.4 EndZ=0
    g22: LineSegment StartX=-20.6 StartY=-36.4 StartZ=0 EndX=-20.6 EndY=-1.8 EndZ=0
    g23: LineSegment StartX=-23.6 StartY=-1.8 StartZ=0 EndX=-23.6 EndY=-36.4 EndZ=0
  constraints (48):
    c: Block(g0)
    c: Block(g1)
    c: Block(g2)
    c: Block(g3)
    c: Block(g4)
    c: Block(g5)
    c: Block(g6)
    c: Block(g7)
    c: Block(g8)
    c: Block(g9)
    c: Block(g10)
    c: Block(g11)
    c: Coincident(g12,g1)
    c: Coincident(g12,g2)
    c: Vertical(g12)
    c: Coincident(g13,g1)
    c: Coincident(g13,g2)
    c: Vertical(g13)
    c: Coincident(g14,g11)
    c: Coincident(g14,g7)
    c: Vertical(g14)
    c: Coincident(g15,g11)
    c: Coincident(g15,g7)
    c: Vertical(g15)
    c: Coincident(g16,g0)
    c: Coincident(g16,g3)
    c: Vertical(g16)
    c: Coincident(g17,g4)
    c: Coincident(g17,g8)
    c: Vertical(g17)
    c: Coincident(g18,g0)
    c: Coincident(g18,g3)
    c: Vertical(g18)
    c: Coincident(g19,g4)
    c: Coincident(g19,g8)
    c: Vertical(g19)
    c: Coincident(g20,g5)
    c: Coincident(g20,g9)
    c: Vertical(g20)
    c: Coincident(g21,g5)
    c: Coincident(g21,g9)
    c: Vertical(g21)
    c: Coincident(g22,g10)
    c: Coincident(g22,g6)
    c: Vertical(g22)
    c: Coincident(g23,g6)
    c: Coincident(g23,g10)
    c: Vertical(g23)
FEATURE [Part::Extrusion] Extrude020  label="removeToCreateFanGrillHoles"
  Base = -> Sketch029
  Dir = (0,-1,6e-16)
  DirMode = 2
  FaceMakerClass = Part::FaceMakerBullseye
  LengthFwd = 10
  LengthRev = 0
  Placement = pos=(65.4,44,54.82) rot=(0,0,1;0rad)
  Solid = true
  Symmetric = false
FEATURE [Part::MultiFuse] Fusion055  label="top008"
  Shapes = -> [Cut017,Cut018]
FEATURE [Part::Cut] Cut019  label="top009"
  Base = -> Fusion055
  Tool = -> Extrude020
FEATURE [App::MeasureDistance] Distance003  label="Distance: 71.95 mm"
  Distance = 71.9513
  P1 = (117,38,72)
  P2 = (117,38,0.0487319)
FEATURE [Sketcher::SketchObject] Sketch030
  FullyConstrained = true
  Placement = pos=(117,19,0) rot=(0.57735,0.57735,0.57735;2.0944rad)
  sketch-geometry (48):
    g0: LineSegment StartX=-49.19 StartY=69.25 StartZ=0 EndX=-49.19 EndY=66.25 EndZ=0
    g1: LineSegment StartX=-49.19 StartY=63.5 StartZ=0 EndX=-49.19 EndY=60.5 EndZ=0
    g2: LineSegment StartX=-49.19 StartY=57.75 StartZ=0 EndX=-49.19 EndY=54.75 EndZ=0
    g3: LineSegment StartX=-49.19 StartY=52 StartZ=0 EndX=-49.19 EndY=49 EndZ=0
    g4: LineSegment StartX=-49.19 StartY=46.25 StartZ=0 EndX=-49.19 EndY=43.25 EndZ=0
    g5: LineSegment StartX=-49.19 StartY=40.5 StartZ=0 EndX=-49.19 EndY=37.5 EndZ=0
    g6: LineSegment StartX=-49.19 StartY=34.5 StartZ=0 EndX=-49.19 EndY=31.5 EndZ=0
    g7: LineSegment StartX=-49.19 StartY=28.75 StartZ=0 EndX=-49.19 EndY=25.75 EndZ=0
    g8: LineSegment StartX=-49.19 StartY=23 StartZ=0 EndX=-49.19 EndY=20 EndZ=0
    g9: LineSegment StartX=-49.19 StartY=17.25 StartZ=0 EndX=-49.19 EndY=14.25 EndZ=0
    g10: LineSegment StartX=-49.19 StartY=11.5 StartZ=0 EndX=-49.19 EndY=8.5 EndZ=0
    g11: LineSegment StartX=-49.19 StartY=5.75 StartZ=0 EndX=-49.19 EndY=2.75 EndZ=0
    g12: ArcOfCircle CenterX=-1.5 CenterY=67.75 CenterZ=0 NormalX=0 NormalY=0 NormalZ=1 AngleXU=0 Radius=1.5 StartAngle=4.71239 EndAngle=7.85398
    g13: ArcOfCircle CenterX=-1.5 CenterY=62 CenterZ=0 NormalX=0 NormalY=0 NormalZ=1 AngleXU=0 Radius=1.5 StartAngle=4.71239 EndAngle=7.85398
    g14: ArcOfCircle CenterX=-1.5 CenterY=56.25 CenterZ=0 NormalX=0 NormalY=0 NormalZ=1 AngleXU=0 Radius=1.5 StartAngle=4.71239 EndAngle=7.85398
    g15: ArcOfCircle CenterX=-11.49 CenterY=50.5 CenterZ=0 NormalX=0 NormalY=0 NormalZ=1 AngleXU=0 Radius=1.5 StartAngle=4.71239 EndAngle=7.85398
    g16: ArcOfCircle CenterX=-16.28 CenterY=44.75 CenterZ=0 NormalX=0 NormalY=0 NormalZ=1 AngleXU=0 Radius=1.5 StartAngle=4.71239 EndAngle=7.85398
    g17: ArcOfCircle CenterX=-18.2337 CenterY=39 CenterZ=0 NormalX=0 NormalY=0 NormalZ=1 AngleXU=0 Radius=1.5 StartAngle=4.71485 EndAngle=7.85398
    g18: ArcOfCircle CenterX=-16.2837 CenterY=27.25 CenterZ=0 NormalX=0 NormalY=0 NormalZ=1 AngleXU=0 Radius=1.5 StartAngle=4.71485 EndAngle=7.85398
    g19: ArcOfCircle CenterX=-18.2337 CenterY=33 CenterZ=0 NormalX=0 NormalY=0 NormalZ=1 AngleXU=0 Radius=1.5 StartAngle=4.71485 EndAngle=7.85398
    g20: ArcOfCircle CenterX=-11.49 CenterY=21.5 CenterZ=0 NormalX=0 NormalY=0 NormalZ=1 AngleXU=0 Radius=1.5 StartAngle=4.71239 EndAngle=7.85398
    g21: ArcOfCircle CenterX=-1.5 CenterY=4.25 CenterZ=0 NormalX=0 NormalY=0 NormalZ=1 AngleXU=0 Radius=1.5 StartAngle=4.71239 EndAngle=7.85398
    g22: ArcOfCircle CenterX=-1.5 CenterY=10 CenterZ=0 NormalX=0 NormalY=0 NormalZ=1 AngleXU=0 Radius=1.5 StartAngle=4.71239 EndAngle=7.85398
    g23: ArcOfCircle CenterX=-1.5 CenterY=15.75 CenterZ=0 NormalX=0 NormalY=0 NormalZ=1 AngleXU=0 Radius=1.5 StartAngle=4.71239 EndAngle=7.85398
    g24: LineSegment StartX=-49.19 StartY=69.25 StartZ=0 EndX=-1.5 EndY=69.25 EndZ=0
    g25: LineSegment StartX=-49.19 StartY=66.25 StartZ=0 EndX=-1.5 EndY=66.25 EndZ=0
    g26: LineSegment StartX=-49.19 StartY=63.5 StartZ=0 EndX=-1.5 EndY=63.5 EndZ=0
    g27: LineSegment StartX=-49.19 StartY=60.5 StartZ=0 EndX=-1.5 EndY=60.5 EndZ=0
    g28: LineSegment StartX=-49.19 StartY=57.75 StartZ=0 EndX=-1.5 EndY=57.75 EndZ=0
    g29: LineSegment StartX=-49.19 StartY=54.75 StartZ=0 EndX=-1.5 EndY=54.75 EndZ=0
    g30: LineSegment StartX=-49.19 StartY=52 StartZ=0 EndX=-11.49 EndY=52 EndZ=0
    g31: LineSegment StartX=-49.19 StartY=49 StartZ=0 EndX=-11.49 EndY=49 EndZ=0
    g32: LineSegment StartX=-49.19 StartY=46.25 StartZ=0 EndX=-16.28 EndY=46.25 EndZ=0
    g33: LineSegment StartX=-49.19 StartY=43.25 StartZ=0 EndX=-16.28 EndY=43.25 EndZ=0
    g34: LineSegment StartX=-49.19 StartY=40.5 StartZ=0 EndX=-18.2337 EndY=40.5 EndZ=0
    g35: LineSegment StartX=-49.19 StartY=37.5 StartZ=0 EndX=-18.23 EndY=37.5 EndZ=0
    g36: LineSegment StartX=-49.19 StartY=34.5 StartZ=0 EndX=-18.2337 EndY=34.5 EndZ=0
    g37: LineSegment StartX=-49.19 StartY=31.5 StartZ=0 EndX=-18.23 EndY=31.5 EndZ=0
    g38: LineSegment StartX=-49.19 StartY=28.75 StartZ=0 EndX=-16.2837 EndY=28.75 EndZ=0
    g39: LineSegment StartX=-49.19 StartY=25.75 StartZ=0 EndX=-16.28 EndY=25.75 EndZ=0
    g40: LineSegment StartX=-49.19 StartY=23 StartZ=0 EndX=-11.49 EndY=23 EndZ=0
    g41: LineSegment StartX=-49.19 StartY=20 StartZ=0 EndX=-11.49 EndY=20 EndZ=0
    g42: LineSegment StartX=-49.19 StartY=17.25 StartZ=0 EndX=-1.5 EndY=17.25 EndZ=0
    g43: LineSegment StartX=-49.19 StartY=14.25 StartZ=0 EndX=-1.5 EndY=14.25 EndZ=0
    g44: LineSegment StartX=-49.19 StartY=11.5 StartZ=0 EndX=-1.5 EndY=11.5 EndZ=0
    g45: LineSegment StartX=-49.19 StartY=8.5 StartZ=0 EndX=-1.5 EndY=8.5 EndZ=0
    g46: LineSegment StartX=-49.19 StartY=5.75 StartZ=0 EndX=-1.5 EndY=5.75 EndZ=0
    g47: LineSegment StartX=-49.19 StartY=2.75 StartZ=0 EndX=-1.5 EndY=2.75 EndZ=0
  constraints (120):
    c: Vertical(g0)
    c: Distance(g0) = 3
    c: Block(g0)
    c: Vertical(g1)
    c: Distance(g1) = 3
    c: Vertical(g2)
    c: Equal(g0,g2) = 3
    c: Block(g2)
    c: Vertical(g3)
    c: Equal(g1,g3) = 3
    c: Vertical(g4)
    c: Equal(g0,g4) = 3
    c: Block(g4)
    c: Vertical(g5)
    c: Equal(g1,g5) = 3
    c: Vertical(g6)
    c: Equal(g0,g6) = 3
    c: Block(g6)
    c: Vertical(g7)
    c: Equal(g1,g7) = 3
    c: Vertical(g8)
    c: Equal(g0,g8) = 3
    c: Block(g8)
    c: Vertical(g9)
    c: Equal(g1,g9) = 3
    c: Vertical(g10)
    c: Equal(g0,g10) = 3
    c: Block(g10)
    c: Vertical(g11)
    c: Equal(g1,g11) = 3
    c: Block(g12)
    c: Block(g13)
    c: Block(g14)
    c: Block(g15)
    c: Block(g16)
    c: Block(g17)
    c: Block(g18)
    c: Block(g19)
    c: Block(g20)
    c: Block(g21)
    c: Block(g22)
    c: Block(g23)
    c: Block(g11)
    c: Block(g9)
    c: Block(g7)
    c: Block(g5)
    c: Block(g3)
    c: Block(g1)
    c: Coincident(g24,g0)
    c: Coincident(g24,g12)
    c: Horizontal(g24)
    c: Coincident(g25,g0)
    c: Coincident(g25,g12)
    c: Horizontal(g25)
    c: Coincident(g26,g1)
    c: Coincident(g26,g13)
    c: Horizontal(g26)
    c: Coincident(g27,g1)
    c: Coincident(g27,g13)
    c: Horizontal(g27)
    c: Coincident(g28,g2)
    c: Coincident(g28,g14)
    c: Horizontal(g28)
    c: Coincident(g29,g2)
    c: Coincident(g29,g14)
    c: Horizontal(g29)
    c: Coincident(g30,g3)
    c: Coincident(g30,g15)
    c: Horizontal(g30)
    c: Coincident(g31,g3)
    c: Coincident(g31,g15)
    c: Horizontal(g31)
    c: Coincident(g32,g4)
    c: Coincident(g32,g16)
    c: Horizontal(g32)
    c: Coincident(g33,g4)
    c: Coincident(g33,g16)
    c: Horizontal(g33)
    c: Coincident(g34,g5)
    c: Coincident(g34,g17)
    c: Horizontal(g34)
    c: Coincident(g35,g5)
    c: Coincident(g35,g17)
    c: Horizontal(g35)
    c: Coincident(g36,g6)
    c: Coincident(g36,g19)
    c: Horizontal(g36)
    c: Coincident(g37,g6)
    c: Coincident(g37,g19)
    c: Horizontal(g37)
    c: Coincident(g38,g7)
    c: Coincident(g38,g18)
    c: Horizontal(g38)
    c: Coincident(g39,g7)
    c: Coincident(g39,g18)
    c: Horizontal(g39)
    c: Coincident(g40,g8)
    c: Coincident(g40,g20)
    c: Horizontal(g40)
    c: Coincident(g41,g8)
    c: Coincident(g41,g20)
    c: Horizontal(g41)
    c: Coincident(g42,g9)
    c: Coincident(g42,g23)
    c: Horizontal(g42)
    c: Coincident(g43,g9)
    c: Coincident(g43,g23)
    c: Horizontal(g43)
    c: Coincident(g44,g10)
    c: Coincident(g44,g22)
    c: Horizontal(g44)
    c: Coincident(g45,g10)
    c: Coincident(g45,g22)
    c: Horizontal(g45)
    c: Coincident(g46,g11)
    c: Coincident(g46,g21)
    c: Horizontal(g46)
    c: Coincident(g47,g11)
    c: Coincident(g47,g21)
    c: Horizontal(g47)
FEATURE [Sketcher::SketchObject] Sketch031
  FullyConstrained = true
  Placement = pos=(117,19,0) rot=(0.57735,0.57735,0.57735;2.0944rad)
  sketch-geometry (24):
    g0: ArcOfCircle CenterX=-49.19 CenterY=67.75 CenterZ=0 NormalX=0 NormalY=0 NormalZ=1 AngleXU=0 Radius=1.5 StartAngle=1.5708 EndAngle=4.71239
    g1: ArcOfCircle CenterX=-49.19 CenterY=62 CenterZ=0 NormalX=0 NormalY=0 NormalZ=1 AngleXU=0 Radius=1.5 StartAngle=1.5708 EndAngle=4.71239
    g2: ArcOfCircle CenterX=-49.19 CenterY=56.25 CenterZ=0 NormalX=0 NormalY=0 NormalZ=1 AngleXU=0 Radius=1.5 StartAngle=1.5708 EndAngle=4.71239
    g3: ArcOfCircle CenterX=-49.19 CenterY=50.5 CenterZ=0 NormalX=0 NormalY=0 NormalZ=1 AngleXU=0 Radius=1.5 StartAngle=1.5708 EndAngle=4.71239
    g4: ArcOfCircle CenterX=-49.19 CenterY=44.75 CenterZ=0 NormalX=0 NormalY=0 NormalZ=1 AngleXU=0 Radius=1.5 StartAngle=1.5708 EndAngle=4.71239
    g5: ArcOfCircle CenterX=-49.19 CenterY=39 CenterZ=0 NormalX=0 NormalY=0 NormalZ=1 AngleXU=0 Radius=1.5 StartAngle=1.5708 EndAngle=4.71239
    g6: ArcOfCircle CenterX=-49.19 CenterY=33 CenterZ=0 NormalX=0 NormalY=0 NormalZ=1 AngleXU=0 Radius=1.5 StartAngle=1.5708 EndAngle=4.71239
    g7: ArcOfCircle CenterX=-49.19 CenterY=27.25 CenterZ=0 NormalX=0 NormalY=0 NormalZ=1 AngleXU=0 Radius=1.5 StartAngle=1.5708 EndAngle=4.71239
    g8: ArcOfCircle CenterX=-49.19 CenterY=21.5 CenterZ=0 NormalX=0 NormalY=0 NormalZ=1 AngleXU=0 Radius=1.5 StartAngle=1.5708 EndAngle=4.71239
    g9: ArcOfCircle CenterX=-49.19 CenterY=15.75 CenterZ=0 NormalX=0 NormalY=0 NormalZ=1 AngleXU=0 Radius=1.5 StartAngle=1.5708 EndAngle=4.71239
    g10: ArcOfCircle CenterX=-49.19 CenterY=10 CenterZ=0 NormalX=0 NormalY=0 NormalZ=1 AngleXU=0 Radius=1.5 StartAngle=1.5708 EndAngle=4.71239
    g11: ArcOfCircle CenterX=-49.19 CenterY=4.25 CenterZ=0 NormalX=0 NormalY=0 NormalZ=1 AngleXU=0 Radius=1.5 StartAngle=1.5708 EndAngle=4.71239
    g12: LineSegment StartX=-49.19 StartY=69.25 StartZ=0 EndX=-49.19 EndY=66.25 EndZ=0
    g13: LineSegment StartX=-49.19 StartY=63.5 StartZ=0 EndX=-49.19 EndY=60.5 EndZ=0
    g14: LineSegment StartX=-49.19 StartY=57.75 StartZ=0 EndX=-49.19 EndY=54.75 EndZ=0
    g15: LineSegment StartX=-49.19 StartY=52 StartZ=0 EndX=-49.19 EndY=49 EndZ=0
    g16: LineSegment StartX=-49.19 StartY=46.25 StartZ=0 EndX=-49.19 EndY=43.25 EndZ=0
    g17: LineSegment StartX=-49.19 StartY=40.5 StartZ=0 EndX=-49.19 EndY=37.5 EndZ=0
    g18: LineSegment StartX=-49.19 StartY=34.5 StartZ=0 EndX=-49.19 EndY=31.5 EndZ=0
    g19: LineSegment StartX=-49.19 StartY=28.75 StartZ=0 EndX=-49.19 EndY=25.75 EndZ=0
    g20: LineSegment StartX=-49.19 StartY=23 StartZ=0 EndX=-49.19 EndY=20 EndZ=0
    g21: LineSegment StartX=-49.19 StartY=17.25 StartZ=0 EndX=-49.19 EndY=14.25 EndZ=0
    g22: LineSegment StartX=-49.19 StartY=11.5 StartZ=0 EndX=-49.19 EndY=8.5 EndZ=0
    g23: LineSegment StartX=-49.19 StartY=5.75 StartZ=0 EndX=-49.19 EndY=2.75 EndZ=0
  constraints (48):
    c: Block(g0)
    c: Block(g1)
    c: Block(g2)
    c: Block(g3)
    c: Block(g4)
    c: Block(g5)
    c: Block(g6)
    c: Block(g7)
    c: Block(g8)
    c: Block(g9)
    c: Block(g10)
    c: Block(g11)
    c: Coincident(g12,g0)
    c: Coincident(g12,g0)
    c: Vertical(g12)
    c: Vertical(g13)
    c: Coincident(g13,g1)
    c: Vertical(g14)
    c: Coincident(g14,g2)
    c: Vertical(g15)
    c: Coincident(g15,g3)
    c: Vertical(g16)
    c: Coincident(g16,g4)
    c: Vertical(g17)
    c: Coincident(g17,g5)
    c: Vertical(g18)
    c: Coincident(g18,g6)
    c: Vertical(g19)
    c: Coincident(g19,g7)
    c: Vertical(g20)
    c: Coincident(g20,g8)
    c: Vertical(g21)
    c: Coincident(g21,g9)
    c: Vertical(g22)
    c: Coincident(g22,g10)
    c: Vertical(g23)
    c: Coincident(g23,g11)
    c: Block(g23)
    c: Block(g22)
    c: Block(g21)
    c: Block(g20)
    c: Block(g13)
    c: Block(g14)
    c: Block(g15)
    c: Block(g16)
    c: Block(g17)
    c: Block(g18)
    c: Block(g19)
FEATURE [Part::Extrusion] Extrude022
  Base = -> Sketch030
  Dir = (1,-2e-16,2e-16)
  DirMode = 2
  FaceMakerClass = Part::FaceMakerBullseye
  LengthFwd = 19
  LengthRev = 0
  Placement = pos=(-19,0,0) rot=(0,0,1;0rad)
  Solid = true
  Symmetric = false
FEATURE [Part::Fillet] Fillet022
  Base = -> Extrude022
  Edges = 24 edges r=1.49: [Edge6,Edge11,Edge18,Edge23,Edge30,Edge35,Edge42,Edge47,Edge54,Edge59,Edge66,Edge71,Edge78,Edge83,Edge90,Edge95,Edge102,Edge107,Edge114,Edge119,Edge126,Edge131,Edge138,Edge143]
FEATURE [Part::Cut] Cut020  label="top010"
  Base = -> Cut019
  Tool = -> Fillet022
FEATURE [Sketcher::SketchObject] Sketch032
  FullyConstrained = true
  Placement = pos=(117,19,0) rot=(0.57735,0.57735,0.57735;2.0944rad)
  sketch-geometry (48):
    g0: LineSegment StartX=-49.19 StartY=69.25 StartZ=0 EndX=-49.19 EndY=66.25 EndZ=0
    g1: LineSegment StartX=-49.19 StartY=63.5 StartZ=0 EndX=-49.19 EndY=60.5 EndZ=0
    g2: LineSegment StartX=-49.19 StartY=57.75 StartZ=0 EndX=-49.19 EndY=54.75 EndZ=0
    g3: LineSegment StartX=-49.19 StartY=52 StartZ=0 EndX=-49.19 EndY=49 EndZ=0
    g4: LineSegment StartX=-49.19 StartY=46.25 StartZ=0 EndX=-49.19 EndY=43.25 EndZ=0
    g5: LineSegment StartX=-49.19 StartY=40.5 StartZ=0 EndX=-49.19 EndY=37.5 EndZ=0
    g6: LineSegment StartX=-49.19 StartY=34.5 StartZ=0 EndX=-49.19 EndY=31.5 EndZ=0
    g7: LineSegment StartX=-49.19 StartY=28.75 StartZ=0 EndX=-49.19 EndY=25.75 EndZ=0
    g8: LineSegment StartX=-49.19 StartY=23 StartZ=0 EndX=-49.19 EndY=20 EndZ=0
    g9: LineSegment StartX=-49.19 StartY=17.25 StartZ=0 EndX=-49.19 EndY=14.25 EndZ=0
    g10: LineSegment StartX=-49.19 StartY=11.5 StartZ=0 EndX=-49.19 EndY=8.5 EndZ=0
    g11: LineSegment StartX=-49.19 StartY=5.75 StartZ=0 EndX=-49.19 EndY=2.75 EndZ=0
    g12: ArcOfCircle CenterX=-1.5 CenterY=67.75 CenterZ=0 NormalX=0 NormalY=0 NormalZ=1 AngleXU=0 Radius=1.5 StartAngle=4.71239 EndAngle=7.85398
    g13: ArcOfCircle CenterX=-1.5 CenterY=62 CenterZ=0 NormalX=0 NormalY=0 NormalZ=1 AngleXU=0 Radius=1.5 StartAngle=4.71239 EndAngle=7.85398
    g14: ArcOfCircle CenterX=-1.5 CenterY=56.25 CenterZ=0 NormalX=0 NormalY=0 NormalZ=1 AngleXU=0 Radius=1.5 StartAngle=4.71239 EndAngle=7.85398
    g15: ArcOfCircle CenterX=-11.49 CenterY=50.5 CenterZ=0 NormalX=0 NormalY=0 NormalZ=1 AngleXU=0 Radius=1.5 StartAngle=4.71239 EndAngle=7.85398
    g16: ArcOfCircle CenterX=-16.28 CenterY=44.75 CenterZ=0 NormalX=0 NormalY=0 NormalZ=1 AngleXU=0 Radius=1.5 StartAngle=4.71239 EndAngle=7.85398
    g17: ArcOfCircle CenterX=-18.2337 CenterY=39 CenterZ=0 NormalX=0 NormalY=0 NormalZ=1 AngleXU=0 Radius=1.5 StartAngle=4.71485 EndAngle=7.85398
    g18: ArcOfCircle CenterX=-16.2837 CenterY=27.25 CenterZ=0 NormalX=0 NormalY=0 NormalZ=1 AngleXU=0 Radius=1.5 StartAngle=4.71485 EndAngle=7.85398
    g19: ArcOfCircle CenterX=-18.2337 CenterY=33 CenterZ=0 NormalX=0 NormalY=0 NormalZ=1 AngleXU=0 Radius=1.5 StartAngle=4.71485 EndAngle=7.85398
    g20: ArcOfCircle CenterX=-11.49 CenterY=21.5 CenterZ=0 NormalX=0 NormalY=0 NormalZ=1 AngleXU=0 Radius=1.5 StartAngle=4.71239 EndAngle=7.85398
    g21: ArcOfCircle CenterX=-1.5 CenterY=4.25 CenterZ=0 NormalX=0 NormalY=0 NormalZ=1 AngleXU=0 Radius=1.5 StartAngle=4.71239 EndAngle=7.85398
    g22: ArcOfCircle CenterX=-1.5 CenterY=10 CenterZ=0 NormalX=0 NormalY=0 NormalZ=1 AngleXU=0 Radius=1.5 StartAngle=4.71239 EndAngle=7.85398
    g23: ArcOfCircle CenterX=-1.5 CenterY=15.75 CenterZ=0 NormalX=0 NormalY=0 NormalZ=1 AngleXU=0 Radius=1.5 StartAngle=4.71239 EndAngle=7.85398
    g24: LineSegment StartX=-49.19 StartY=69.25 StartZ=0 EndX=-1.5 EndY=69.25 EndZ=0
    g25: LineSegment StartX=-49.19 StartY=66.25 StartZ=0 EndX=-1.5 EndY=66.25 EndZ=0
    g26: LineSegment StartX=-49.19 StartY=63.5 StartZ=0 EndX=-1.5 EndY=63.5 EndZ=0
    g27: LineSegment StartX=-49.19 StartY=60.5 StartZ=0 EndX=-1.5 EndY=60.5 EndZ=0
    g28: LineSegment StartX=-49.19 StartY=57.75 StartZ=0 EndX=-1.5 EndY=57.75 EndZ=0
    g29: LineSegment StartX=-49.19 StartY=54.75 StartZ=0 EndX=-1.5 EndY=54.75 EndZ=0
    g30: LineSegment StartX=-49.19 StartY=52 StartZ=0 EndX=-11.49 EndY=52 EndZ=0
    g31: LineSegment StartX=-49.19 StartY=49 StartZ=0 EndX=-11.49 EndY=49 EndZ=0
    g32: LineSegment StartX=-49.19 StartY=46.25 StartZ=0 EndX=-16.28 EndY=46.25 EndZ=0
    g33: LineSegment StartX=-49.19 StartY=43.25 StartZ=0 EndX=-16.28 EndY=43.25 EndZ=0
    g34: LineSegment StartX=-49.19 StartY=40.5 StartZ=0 EndX=-18.2337 EndY=40.5 EndZ=0
    g35: LineSegment StartX=-49.19 StartY=37.5 StartZ=0 EndX=-18.23 EndY=37.5 EndZ=0
    g36: LineSegment StartX=-49.19 StartY=34.5 StartZ=0 EndX=-18.2337 EndY=34.5 EndZ=0
    g37: LineSegment StartX=-49.19 StartY=31.5 StartZ=0 EndX=-18.23 EndY=31.5 EndZ=0
    g38: LineSegment StartX=-49.19 StartY=28.75 StartZ=0 EndX=-16.2837 EndY=28.75 EndZ=0
    g39: LineSegment StartX=-49.19 StartY=25.75 StartZ=0 EndX=-16.28 EndY=25.75 EndZ=0
    g40: LineSegment StartX=-49.19 StartY=23 StartZ=0 EndX=-11.49 EndY=23 EndZ=0
    g41: LineSegment StartX=-49.19 StartY=20 StartZ=0 EndX=-11.49 EndY=20 EndZ=0
    g42: LineSegment StartX=-49.19 StartY=17.25 StartZ=0 EndX=-1.5 EndY=17.25 EndZ=0
    g43: LineSegment StartX=-49.19 StartY=14.25 StartZ=0 EndX=-1.5 EndY=14.25 EndZ=0
    g44: LineSegment StartX=-49.19 StartY=11.5 StartZ=0 EndX=-1.5 EndY=11.5 EndZ=0
    g45: LineSegment StartX=-49.19 StartY=8.5 StartZ=0 EndX=-1.5 EndY=8.5 EndZ=0
    g46: LineSegment StartX=-49.19 StartY=5.75 StartZ=0 EndX=-1.5 EndY=5.75 EndZ=0
    g47: LineSegment StartX=-49.19 StartY=2.75 StartZ=0 EndX=-1.5 EndY=2.75 EndZ=0
  constraints (120):
    c: Vertical(g0)
    c: Distance(g0) = 3
    c: Block(g0)
    c: Vertical(g1)
    c: Distance(g1) = 3
    c: Vertical(g2)
    c: Equal(g0,g2) = 3
    c: Block(g2)
    c: Vertical(g3)
    c: Equal(g1,g3) = 3
    c: Vertical(g4)
    c: Equal(g0,g4) = 3
    c: Block(g4)
    c: Vertical(g5)
    c: Equal(g1,g5) = 3
    c: Vertical(g6)
    c: Equal(g0,g6) = 3
    c: Block(g6)
    c: Vertical(g7)
    c: Equal(g1,g7) = 3
    c: Vertical(g8)
    c: Equal(g0,g8) = 3
    c: Block(g8)
    c: Vertical(g9)
    c: Equal(g1,g9) = 3
    c: Vertical(g10)
    c: Equal(g0,g10) = 3
    c: Block(g10)
    c: Vertical(g11)
    c: Equal(g1,g11) = 3
    c: Block(g12)
    c: Block(g13)
    c: Block(g14)
    c: Block(g15)
    c: Block(g16)
    c: Block(g17)
    c: Block(g18)
    c: Block(g19)
    c: Block(g20)
    c: Block(g21)
    c: Block(g22)
    c: Block(g23)
    c: Block(g11)
    c: Block(g9)
    c: Block(g7)
    c: Block(g5)
    c: Block(g3)
    c: Block(g1)
    c: Coincident(g24,g0)
    c: Coincident(g24,g12)
    c: Horizontal(g24)
    c: Coincident(g25,g0)
    c: Coincident(g25,g12)
    c: Horizontal(g25)
    c: Coincident(g26,g1)
    c: Coincident(g26,g13)
    c: Horizontal(g26)
    c: Coincident(g27,g1)
    c: Coincident(g27,g13)
    c: Horizontal(g27)
    c: Coincident(g28,g2)
    c: Coincident(g28,g14)
    c: Horizontal(g28)
    c: Coincident(g29,g2)
    c: Coincident(g29,g14)
    c: Horizontal(g29)
    c: Coincident(g30,g3)
    c: Coincident(g30,g15)
    c: Horizontal(g30)
    c: Coincident(g31,g3)
    c: Coincident(g31,g15)
    c: Horizontal(g31)
    c: Coincident(g32,g4)
    c: Coincident(g32,g16)
    c: Horizontal(g32)
    c: Coincident(g33,g4)
    c: Coincident(g33,g16)
    c: Horizontal(g33)
    c: Coincident(g34,g5)
    c: Coincident(g34,g17)
    c: Horizontal(g34)
    c: Coincident(g35,g5)
    c: Coincident(g35,g17)
    c: Horizontal(g35)
    c: Coincident(g36,g6)
    c: Coincident(g36,g19)
    c: Horizontal(g36)
    c: Coincident(g37,g6)
    c: Coincident(g37,g19)
    c: Horizontal(g37)
    c: Coincident(g38,g7)
    c: Coincident(g38,g18)
    c: Horizontal(g38)
    c: Coincident(g39,g7)
    c: Coincident(g39,g18)
    c: Horizontal(g39)
    c: Coincident(g40,g8)
    c: Coincident(g40,g20)
    c: Horizontal(g40)
    c: Coincident(g41,g8)
    c: Coincident(g41,g20)
    c: Horizontal(g41)
    c: Coincident(g42,g9)
    c: Coincident(g42,g23)
    c: Horizontal(g42)
    c: Coincident(g43,g9)
    c: Coincident(g43,g23)
    c: Horizontal(g43)
    c: Coincident(g44,g10)
    c: Coincident(g44,g22)
    c: Horizontal(g44)
    c: Coincident(g45,g10)
    c: Coincident(g45,g22)
    c: Horizontal(g45)
    c: Coincident(g46,g11)
    c: Coincident(g46,g21)
    c: Horizontal(g46)
    c: Coincident(g47,g11)
    c: Coincident(g47,g21)
    c: Horizontal(g47)
FEATURE [Part::Extrusion] Extrude023
  Base = -> Sketch032
  Dir = (1,-2e-16,2e-16)
  DirMode = 2
  FaceMakerClass = Part::FaceMakerBullseye
  LengthFwd = 19
  LengthRev = 0
  Placement = pos=(-19,0,0) rot=(0,0,1;0rad)
  Solid = true
  Symmetric = false
FEATURE [Part::Fillet] Fillet023
  Base = -> Extrude023
  Edges = <same value as first occurrence — deduplicated (x6 in doc)>
  Placement = pos=(0,0.05,0) rot=(0,0,1;0rad)
FEATURE [Part::Cut] Cut014  label="bottom003"
  Base = -> Cut007
  Tool = -> Fusion047
FEATURE [Part::Cut] Cut021  label="bottom004"
  Base = -> Cut014
  Tool = -> Fillet023
FEATURE [Sketcher::SketchObject] Sketch033
  FullyConstrained = true
  Placement = pos=(117,19,0) rot=(0.57735,0.57735,0.57735;2.0944rad)
  sketch-geometry (8):
    g0: LineSegment StartX=-49.19 StartY=69.25 StartZ=0 EndX=-49.19 EndY=66.25 EndZ=0
    g1: LineSegment StartX=-49.19 StartY=5.75 StartZ=0 EndX=-49.19 EndY=2.75 EndZ=0
    g2: ArcOfCircle CenterX=-1.5 CenterY=67.75 CenterZ=0 NormalX=0 NormalY=0 NormalZ=1 AngleXU=0 Radius=1.5 StartAngle=4.71239 EndAngle=7.85398
    g3: ArcOfCircle CenterX=-1.5 CenterY=4.25 CenterZ=0 NormalX=0 NormalY=0 NormalZ=1 AngleXU=0 Radius=1.5 StartAngle=4.71239 EndAngle=7.85398
    g4: LineSegment StartX=-49.19 StartY=69.25 StartZ=0 EndX=-1.5 EndY=69.25 EndZ=0
    g5: LineSegment StartX=-49.19 StartY=66.25 StartZ=0 EndX=-1.5 EndY=66.25 EndZ=0
    g6: LineSegment StartX=-49.19 StartY=5.75 StartZ=0 EndX=-1.5 EndY=5.75 EndZ=0
    g7: LineSegment StartX=-49.19 StartY=2.75 StartZ=0 EndX=-1.5 EndY=2.75 EndZ=0
  constraints (19):
    c: Vertical(g0)
    c: Distance(g0) = 3
    c: Block(g0)
    c: Vertical(g1)
    c: Block(g2)
    c: Block(g3)
    c: Block(g1)
    c: Coincident(g4,g0)
    c: Coincident(g4,g2)
    c: Horizontal(g4)
    c: Coincident(g5,g0)
    c: Coincident(g5,g2)
    c: Horizontal(g5)
    c: Coincident(g6,g1)
    c: Coincident(g6,g3)
    c: Horizontal(g6)
    c: Coincident(g7,g1)
    c: Coincident(g7,g3)
    c: Horizontal(g7)
FEATURE [Sketcher::SketchObject] Sketch034
  FullyConstrained = true
  Placement = pos=(117,19,0) rot=(0.57735,0.57735,0.57735;2.0944rad)
  sketch-geometry (8):
    g0: LineSegment StartX=-49.19 StartY=63.5 StartZ=0 EndX=-49.19 EndY=60.5 EndZ=0
    g1: LineSegment StartX=-49.19 StartY=11.5 StartZ=0 EndX=-49.19 EndY=8.5 EndZ=0
    g2: ArcOfCircle CenterX=-1.5 CenterY=62 CenterZ=0 NormalX=0 NormalY=0 NormalZ=1 AngleXU=0 Radius=1.5 StartAngle=4.71239 EndAngle=7.85398
    g3: ArcOfCircle CenterX=-1.5 CenterY=10 CenterZ=0 NormalX=0 NormalY=0 NormalZ=1 AngleXU=0 Radius=1.5 StartAngle=4.71239 EndAngle=7.85398
    g4: LineSegment StartX=-49.19 StartY=63.5 StartZ=0 EndX=-1.5 EndY=63.5 EndZ=0
    g5: LineSegment StartX=-49.19 StartY=60.5 StartZ=0 EndX=-1.5 EndY=60.5 EndZ=0
    g6: LineSegment StartX=-49.19 StartY=11.5 StartZ=0 EndX=-1.5 EndY=11.5 EndZ=0
    g7: LineSegment StartX=-49.19 StartY=8.5 StartZ=0 EndX=-1.5 EndY=8.5 EndZ=0
  constraints (19):
    c: Vertical(g0)
    c: Distance(g0) = 3
    c: Vertical(g1)
    c: Block(g1)
    c: Block(g2)
    c: Block(g3)
    c: Block(g0)
    c: Coincident(g4,g0)
    c: Coincident(g4,g2)
    c: Horizontal(g4)
    c: Coincident(g5,g0)
    c: Coincident(g5,g2)
    c: Horizontal(g5)
    c: Coincident(g6,g1)
    c: Coincident(g6,g3)
    c: Horizontal(g6)
    c: Coincident(g7,g1)
    c: Coincident(g7,g3)
    c: Horizontal(g7)
FEATURE [Part::Extrusion] Extrude024
  Base = -> Sketch033
  Dir = (1,0,0)
  DirMode = 2
  FaceMakerClass = Part::FaceMakerBullseye
  LengthFwd = 10
  LengthRev = 0
  Solid = true
  Symmetric = false
FEATURE [Part::Extrusion] Extrude025
  Base = -> Sketch034
  Dir = (1,0,0)
  DirMode = 2
  FaceMakerClass = Part::FaceMakerBullseye
  LengthFwd = 10
  LengthRev = 0
  Solid = true
  Symmetric = false
FEATURE [Part::Fillet] Fillet024  label="removeFromtMoreFrontCaseScrewRetainers"
  Base = -> Extrude024
  Edges = 4 edges r=1.49: [Edge6,Edge11,Edge18,Edge23]
  Placement = pos=(-11,0,0) rot=(0,0,1;0rad)
FEATURE [Part::Fillet] Fillet025  label="removeFromtMoreFrontCaseScrewRetainers001"
  Base = -> Extrude025
  Edges = 4 edges r=1.49: [Edge6,Edge11,Edge18,Edge23]
  Placement = pos=(-19,0,0) rot=(0,0,1;0rad)
FEATURE [Part::Cut] Cut022
  Base = -> Cut015
  Tool = -> Fillet025
FEATURE [Part::Cut] Cut023  label="screwRetainers"
  Base = -> Cut022
  Tool = -> Fillet024
FEATURE [Part::MultiFuse] Fusion056  label="bottom005"
  Shapes = -> [Fusion044,Cut021]
FEATURE [Part::MultiFuse] Fusion057  label="casePillars001"
  Shapes = -> [Cut016,Fusion052]
FEATURE [Part::MultiFuse] Fusion058  label="bottom006"
  Shapes = -> [Fusion056,Cut023]
FEATURE [Part::MultiFuse] Fusion059  label="bottom007"
  Shapes = -> [Fusion058,Fillet005]
FEATURE [Part::MultiFuse] Fusion060  label="bottom008"
  Shapes = -> [Fusion059,Fusion]
FEATURE [Part::MultiFuse] Fusion061  label="top011"
  Shapes = -> [Cut006,Cut020]
FEATURE [Part::MultiFuse] Fusion062  label="top012"
  Shapes = -> [Fusion057,Fusion061]
FEATURE [Sketcher::SketchObject] Sketch035  label="topSketch007"
  FullyConstrained = true
  sketch-geometry (6):
    g0: LineSegment StartX=19 StartY=38 StartZ=0 EndX=117 EndY=38 EndZ=0
    g1: ArcOfCircle CenterX=19 CenterY=19 CenterZ=0 NormalX=0 NormalY=0 NormalZ=1 AngleXU=0 Radius=19 StartAngle=1.5708 EndAngle=3.14159
    g2: LineSegment StartX=117 StartY=38 StartZ=0 EndX=117 EndY=19 EndZ=0
    g3: LineSegment StartX=98 StartY=1.0161e-12 StartZ=0 EndX=5.22862e-06 EndY=1.0161e-12 EndZ=0
    g4: LineSegment StartX=5.22862e-06 StartY=19 StartZ=0 EndX=5.22862e-06 EndY=1.0161e-12 EndZ=0
    g5: ArcOfCircle CenterX=98 CenterY=19 CenterZ=0 NormalX=0 NormalY=0 NormalZ=1 AngleXU=0 Radius=19 StartAngle=4.71239 EndAngle=6.28319
  constraints (16):
    c: Horizontal(g0)
    c: Distance(g0) = 98
    c: Coincident(g1,g0)
    c: Block(g1)
    c: Coincident(g2,g0)
    c: Vertical(g2)
    c: Distance(g2) = 19
    c: Horizontal(g3)
    c: Coincident(g4,g1)
    c: Vertical(g4)
    c: Coincident(g3,g4)
    c: Block(g3)
    c: Coincident(g5,g2)
    c: Coincident(g5,g3)
    c: Block(g0)
    c: Block(g5)
FEATURE [Part::Extrusion] Extrude026  label="sideA001"
  Base = -> Sketch035
  Dir = (0,0,1)
  DirMode = 2
  FaceMakerClass = Part::FaceMakerBullseye
  LengthFwd = 3
  LengthRev = 0
  Placement = pos=(0,0,-2.7) rot=(0,0,1;0rad)
  Solid = true
  Symmetric = false
FEATURE [Sketcher::SketchObject] Sketch036  label="topSketch008"
  FullyConstrained = true
  sketch-geometry (6):
    g0: LineSegment StartX=19 StartY=38 StartZ=0 EndX=117 EndY=38 EndZ=0
    g1: ArcOfCircle CenterX=19 CenterY=19 CenterZ=0 NormalX=0 NormalY=0 NormalZ=1 AngleXU=0 Radius=19 StartAngle=1.5708 EndAngle=3.14159
    g2: LineSegment StartX=117 StartY=38 StartZ=0 EndX=117 EndY=19 EndZ=0
    g3: LineSegment StartX=98 StartY=1.0161e-12 StartZ=0 EndX=5.22862e-06 EndY=1.0161e-12 EndZ=0
    g4: LineSegment StartX=5.22862e-06 StartY=19 StartZ=0 EndX=5.22862e-06 EndY=1.0161e-12 EndZ=0
    g5: ArcOfCircle CenterX=98 CenterY=19 CenterZ=0 NormalX=0 NormalY=0 NormalZ=1 AngleXU=0 Radius=19 StartAngle=4.71239 EndAngle=6.28319
  constraints (16):
    c: Horizontal(g0)
    c: Distance(g0) = 98
    c: Coincident(g1,g0)
    c: Block(g1)
    c: Coincident(g2,g0)
    c: Vertical(g2)
    c: Distance(g2) = 19
    c: Horizontal(g3)
    c: Coincident(g4,g1)
    c: Vertical(g4)
    c: Coincident(g3,g4)
    c: Block(g3)
    c: Coincident(g5,g2)
    c: Coincident(g5,g3)
    c: Block(g0)
    c: Block(g5)
FEATURE [Part::Extrusion] Extrude027  label="sideB001"
  Base = -> Sketch036
  Dir = (0,0,1)
  DirMode = 2
  FaceMakerClass = Part::FaceMakerBullseye
  LengthFwd = 3
  LengthRev = 0
  Placement = pos=(0,0,71.7) rot=(0,0,1;0rad)
  Solid = true
  Symmetric = false
FEATURE [Part::MultiFuse] Fusion064  label="removeFromBottom"
  Shapes = -> [Extrude026,Extrude027]
FEATURE [Part::Cut] Cut024  label="bottom009"
  Base = -> Fusion060
  Tool = -> Fusion064
FEATURE [Sketcher::SketchObject] Sketch037  label="topSketch009"
  FullyConstrained = true
  sketch-geometry (8):
    g0: ArcOfCircle CenterX=19 CenterY=19.1201 CenterZ=0 NormalX=0 NormalY=0 NormalZ=1 AngleXU=0 Radius=18.8799 StartAngle=1.5708 EndAngle=3.14793
    g1: LineSegment StartX=0.120501 StartY=19.0004 StartZ=0 EndX=0.120501 EndY=0.000382114 EndZ=0
    g2: LineSegment StartX=19 StartY=38 StartZ=0 EndX=124 EndY=38 EndZ=0
    g3: LineSegment StartX=0.120501 StartY=0.000382114 StartZ=0 EndX=105.121 EndY=0.000382114 EndZ=0
    g4: LineSegment StartX=124 StartY=38 StartZ=0 EndX=125.616 EndY=38 EndZ=0
    g5: LineSegment StartX=105.121 StartY=0.000382114 StartZ=0 EndX=106.736 EndY=0.000382114 EndZ=0
    g6: ArcOfCircle CenterX=106.616 CenterY=19 CenterZ=0 NormalX=0 NormalY=0 NormalZ=1 AngleXU=0 Radius=19 StartAngle=4.71873 EndAngle=6.28319
    g7: LineSegment StartX=125.616 StartY=38 StartZ=0 EndX=125.616 EndY=19 EndZ=0
  constraints (21):
    c: Block(g0)
    c: Coincident(g1,g0)
    c: Vertical(g1)
    c: Horizontal(g2)
    c: Distance(g2) = 105
    c: Coincident(g2,g0)
    c: Distance(g1) = 19
    c: Coincident(g3,g1)
    c: Horizontal(g3)
    c: Distance(g3) = 105
    c: Coincident(g4,g2)
    c: Horizontal(g4)
    c: Distance(g4) = 1.61553
    c: Horizontal(g5)
    c: Equal(g4,g5) = 1.61553
    c: Coincident(g5,g3)
    c: Block(g6)
    c: Coincident(g6,g5)
    c: Coincident(g7,g4)
    c: Coincident(g7,g6)
    c: Vertical(g7)
FEATURE [Part::Extrusion] Extrude028  label="sideB"
  Base = -> Sketch037
  Dir = (0,0,1)
  DirMode = 2
  FaceMakerClass = Part::FaceMakerBullseye
  LengthFwd = 3
  LengthRev = 0
  Placement = pos=(0,0,72) rot=(0,0,1;0rad)
  Solid = true
  Symmetric = false
FEATURE [Sketcher::SketchObject] Sketch038  label="topSketch010"
  FullyConstrained = true
  sketch-geometry (22):
    g0: LineSegment StartX=5.21097e-06 StartY=3 StartZ=0 EndX=5.21097e-06 EndY=19 EndZ=0
    g1: ArcOfCircle CenterX=19 CenterY=19 CenterZ=0 NormalX=0 NormalY=0 NormalZ=1 AngleXU=0 Radius=19 StartAngle=1.5708 EndAngle=3.14159
    g2: ArcOfCircle CenterX=19 CenterY=19 CenterZ=0 NormalX=0 NormalY=0 NormalZ=1 AngleXU=0 Radius=16 StartAngle=1.5708 EndAngle=3.14159
    g3: LineSegment StartX=114 StartY=35 StartZ=0 EndX=19 EndY=35 EndZ=0
    g4: LineSegment StartX=5.21097e-06 StartY=3 StartZ=0 EndX=5.21097e-06 EndY=0 EndZ=0
    g5: LineSegment StartX=3 StartY=0 StartZ=0 EndX=5.21097e-06 EndY=0 EndZ=0
    g6: LineSegment StartX=3 StartY=19 StartZ=0 EndX=3 EndY=0 EndZ=0
    g7: LineSegment StartX=19 StartY=38 StartZ=0 EndX=124 EndY=38 EndZ=0
    g8: Circle CenterX=119 CenterY=35 CenterZ=0 NormalX=0 NormalY=0 NormalZ=1 AngleXU=0 Radius=1
    g9: Circle CenterX=121 CenterY=35 CenterZ=0 NormalX=0 NormalY=0 NormalZ=1 AngleXU=0 Radius=1
    g10: Circle CenterX=121 CenterY=33 CenterZ=0 NormalX=0 NormalY=0 NormalZ=1 AngleXU=0 Radius=1
    g11: BSplineCurve PolesCount=3 KnotsCount=2 Degree=2 IsPeriodic=0
    g12: GeomPoint X=119 Y=35 Z=0
    g13: GeomPoint X=121 Y=33 Z=0
    g14: LineSegment StartX=119 StartY=35 StartZ=0 EndX=114 EndY=35 EndZ=0
    g15: ArcOfCircle CenterX=105 CenterY=19 CenterZ=0 NormalX=0 NormalY=0 NormalZ=1 AngleXU=0 Radius=16 StartAngle=5.60905 EndAngle=6.28319
    g16: LineSegment StartX=121 StartY=33 StartZ=0 EndX=121 EndY=19 EndZ=0
    g17: LineSegment StartX=117.5 StartY=9.01251 StartZ=0 EndX=121.163 EndY=9.0125 EndZ=0
    g18: ArcOfCircle CenterX=105 CenterY=19 CenterZ=0 NormalX=0 NormalY=0 NormalZ=1 AngleXU=0 Radius=20.6155 StartAngle=5.7297 EndAngle=6.28319
    g19: LineSegment StartX=121.163 StartY=9.0125 StartZ=0 EndX=122.538 EndY=8.16329 EndZ=0
    g20: LineSegment StartX=124 StartY=38 StartZ=0 EndX=125.616 EndY=38 EndZ=0
    g21: LineSegment StartX=125.616 StartY=19 StartZ=0 EndX=125.616 EndY=38 EndZ=0
  constraints (49):
    c: Vertical(g0)
    c: Block(g0)
    c: Coincident(g1,g0)
    c: Block(g1)
    c: Coincident(g2,g1)
    c: Block(g2)
    c: Coincident(g3,g2)
    c: Horizontal(g3)
    c: Tangent(g3,g2)
    c: Coincident(g4,g0)
    c: Distance(g4) = 3
    c: Vertical(g4)
    c: Coincident(g5,g4)
    c: Horizontal(g5)
    c: Coincident(g6,g2)
    c: Coincident(g6,g5)
    c: Vertical(g6)
    c: Horizontal(g7)
    c: Distance(g7) = 105
    c: Coincident(g7,g1)
    c: Block(g3)
    c: Weight(g8) = 1
    c: Equal(g8,g9)
    c: Equal(g8,g10)
    c: InternalAlignment(g8,g11)
    c: InternalAlignment(g9,g11)
    c: InternalAlignment(g10,g11)
    c: InternalAlignment(g12,g11)
    c: InternalAlignment(g13,g11)
    c: Block(g11)
    c: Coincident(g14,g11)
    c: Coincident(g14,g3)
    c: Horizontal(g14)
    c: Block(g15)
    c: Coincident(g16,g11)
    c: Coincident(g16,g15)
    c: Vertical(g16)
    c: Distance(g16) = 14
    c: Coincident(g17,g15)
    c: Block(g18)
    c: Coincident(g19,g18)
    c: Coincident(g20,g7)
    c: Horizontal(g20)
    c: Vertical(g21)
    c: Coincident(g20,g21)
    c: Block(g20)
    c: Block(g21)
    c: Block(g19)
    c: Block(g17)
FEATURE [Part::Extrusion] Extrude029
  Base = -> Sketch038
  Dir = (0,0,1)
  DirMode = 2
  FaceMakerClass = Part::FaceMakerBullseye
  LengthFwd = 72
  LengthRev = 0
  Solid = true
  Symmetric = false
FEATURE [Part::Feature] Face085
  shape: bbox 4.8 x 25.5 x 2e-07 mm, 1 faces, 0 solids (baked)
FEATURE [Part::Revolution] Revolve089  label="moreFrontCaseScrewPost003"
  Angle = 360
  Axis = (0,1,0)
  Base = (0,0,0)
  FaceMakerClass = Part::FaceMakerBullseye
  Placement = pos=(109.5,4.5,3.5) rot=(0,0,1;0rad)
  Solid = false
  Source = -> Face085
  Symmetric = false
FEATURE [Part::Feature] Face086
  shape: bbox 4.8 x 25.5 x 2e-07 mm, 1 faces, 0 solids (baked)
FEATURE [Part::Revolution] Revolve090  label="moreFrontCaseScrewPost004"
  Angle = 360
  Axis = (0,1,0)
  Base = (0,0,0)
  FaceMakerClass = Part::FaceMakerBullseye
  Placement = pos=(109.5,4.5,68.5) rot=(0,0,1;0rad)
  Solid = false
  Source = -> Face086
  Symmetric = false
FEATURE [Part::Fillet] Fillet026  label="top013"
  Base = -> Extrude029
  Edges = 1 edges r=2: [Edge35]
FEATURE [Sketcher::SketchObject] Sketch039
  FullyConstrained = true
  sketch-geometry (7):
    g0: LineSegment StartX=0 StartY=0 StartZ=0 EndX=0 EndY=6 EndZ=0
    g1: Circle CenterX=0 CenterY=0 CenterZ=0 NormalX=0 NormalY=0 NormalZ=1 AngleXU=0 Radius=1
    g2: Circle CenterX=8 CenterY=6 CenterZ=0 NormalX=0 NormalY=0 NormalZ=1 AngleXU=0 Radius=1
    g3: BSplineCurve PolesCount=3 KnotsCount=2 Degree=2 IsPeriodic=0
    g4: GeomPoint X=0 Y=0 Z=0
    g5: GeomPoint X=8 Y=6 Z=0
    g6: LineSegment StartX=0 StartY=6 StartZ=0 EndX=8 EndY=6 EndZ=0
  constraints (14):
    c: Coincident(g0,g-1)
    c: Distance(g0) = 6
    c: Vertical(g0)
    c: Coincident(g3,g0)
    c: Weight(g1) = 1
    c: Equal(g1,g2)
    c: InternalAlignment(g1,g3)
    c: InternalAlignment(g2,g3)
    c: InternalAlignment(g4,g3)
    c: InternalAlignment(g5,g3)
    c: Block(g3)
    c: Coincident(g6,g0)
    c: Coincident(g6,g3)
    c: Horizontal(g6)
FEATURE [Sketcher::SketchObject] Sketch040
  FullyConstrained = true
  sketch-geometry (7):
    g0: LineSegment StartX=0 StartY=0 StartZ=0 EndX=0 EndY=6 EndZ=0
    g1: Circle CenterX=0 CenterY=0 CenterZ=0 NormalX=0 NormalY=0 NormalZ=1 AngleXU=0 Radius=1
    g2: Circle CenterX=8 CenterY=6 CenterZ=0 NormalX=0 NormalY=0 NormalZ=1 AngleXU=0 Radius=1
    g3: BSplineCurve PolesCount=3 KnotsCount=2 Degree=2 IsPeriodic=0
    g4: GeomPoint X=0 Y=0 Z=0
    g5: GeomPoint X=8 Y=6 Z=0
    g6: LineSegment StartX=0 StartY=6 StartZ=0 EndX=8 EndY=6 EndZ=0
  constraints (14):
    c: Coincident(g0,g-1)
    c: Distance(g0) = 6
    c: Vertical(g0)
    c: Coincident(g3,g0)
    c: Weight(g1) = 1
    c: Equal(g1,g2)
    c: InternalAlignment(g1,g3)
    c: InternalAlignment(g2,g3)
    c: InternalAlignment(g4,g3)
    c: InternalAlignment(g5,g3)
    c: Block(g3)
    c: Coincident(g6,g0)
    c: Coincident(g6,g3)
    c: Horizontal(g6)
FEATURE [Sketcher::SketchObject] Sketch041
  FullyConstrained = true
  sketch-geometry (7):
    g0: LineSegment StartX=0 StartY=0 StartZ=0 EndX=0 EndY=6 EndZ=0
    g1: Circle CenterX=0 CenterY=0 CenterZ=0 NormalX=0 NormalY=0 NormalZ=1 AngleXU=0 Radius=1
    g2: Circle CenterX=8 CenterY=6 CenterZ=0 NormalX=0 NormalY=0 NormalZ=1 AngleXU=0 Radius=1
    g3: BSplineCurve PolesCount=3 KnotsCount=2 Degree=2 IsPeriodic=0
    g4: GeomPoint X=0 Y=0 Z=0
    g5: GeomPoint X=8 Y=6 Z=0
    g6: LineSegment StartX=0 StartY=6 StartZ=0 EndX=8 EndY=6 EndZ=0
  constraints (14):
    c: Coincident(g0,g-1)
    c: Distance(g0) = 6
    c: Vertical(g0)
    c: Coincident(g3,g0)
    c: Weight(g1) = 1
    c: Equal(g1,g2)
    c: InternalAlignment(g1,g3)
    c: InternalAlignment(g2,g3)
    c: InternalAlignment(g4,g3)
    c: InternalAlignment(g5,g3)
    c: Block(g3)
    c: Coincident(g6,g0)
    c: Coincident(g6,g3)
    c: Horizontal(g6)
FEATURE [Sketcher::SketchObject] Sketch042
  FullyConstrained = true
  sketch-geometry (7):
    g0: LineSegment StartX=0 StartY=0 StartZ=0 EndX=0 EndY=6 EndZ=0
    g1: Circle CenterX=0 CenterY=0 CenterZ=0 NormalX=0 NormalY=0 NormalZ=1 AngleXU=0 Radius=1
    g2: Circle CenterX=8 CenterY=6 CenterZ=0 NormalX=0 NormalY=0 NormalZ=1 AngleXU=0 Radius=1
    g3: BSplineCurve PolesCount=3 KnotsCount=2 Degree=2 IsPeriodic=0
    g4: GeomPoint X=0 Y=0 Z=0
    g5: GeomPoint X=8 Y=6 Z=0
    g6: LineSegment StartX=0 StartY=6 StartZ=0 EndX=8 EndY=6 EndZ=0
  constraints (14):
    c: Coincident(g0,g-1)
    c: Distance(g0) = 6
    c: Vertical(g0)
    c: Coincident(g3,g0)
    c: Weight(g1) = 1
    c: Equal(g1,g2)
    c: InternalAlignment(g1,g3)
    c: InternalAlignment(g2,g3)
    c: InternalAlignment(g4,g3)
    c: InternalAlignment(g5,g3)
    c: Block(g3)
    c: Coincident(g6,g0)
    c: Coincident(g6,g3)
    c: Horizontal(g6)
FEATURE [Part::Extrusion] Extrude030  label="caseScrewPillarBracket008"
  Base = -> Sketch039
  Dir = (0,0,1)
  DirMode = 2
  FaceMakerClass = Part::FaceMakerBullseye
  LengthFwd = 2.4
  LengthRev = 0
  Placement = pos=(15.76,29,8.8) rot=(0,1,0;0rad)
  Solid = true
  Symmetric = false
FEATURE [Part::Extrusion] Extrude031  label="caseScrewPillarBracket009"
  Base = -> Sketch040
  Dir = (0,0,1)
  DirMode = 2
  FaceMakerClass = Part::FaceMakerBullseye
  LengthFwd = 2.4
  LengthRev = 0
  Placement = pos=(15.76,29,60.8) rot=(0,0,1;0rad)
  Solid = true
  Symmetric = false
FEATURE [Part::Extrusion] Extrude032  label="caseScrewPillarBracket010"
  Base = -> Sketch041
  Dir = (0,0,1)
  DirMode = 2
  FaceMakerClass = Part::FaceMakerBullseye
  LengthFwd = 2.4
  LengthRev = 0
  Placement = pos=(13.7,29,13.26) rot=(0,-1,0;1.5708rad)
  Solid = true
  Symmetric = false
FEATURE [Part::Extrusion] Extrude033  label="caseScrewPillarBracket011"
  Base = -> Sketch042
  Dir = (0,0,1)
  DirMode = 2
  FaceMakerClass = Part::FaceMakerBullseye
  LengthFwd = 2.4
  LengthRev = 0
  Placement = pos=(11.3,29,58.74) rot=(0,1,0;1.5708rad)
  Solid = true
  Symmetric = false
FEATURE [Sketcher::SketchObject] Sketch043
  FullyConstrained = true
  sketch-geometry (7):
    g0: LineSegment StartX=0 StartY=0 StartZ=0 EndX=0 EndY=6 EndZ=0
    g1: Circle CenterX=0 CenterY=0 CenterZ=0 NormalX=0 NormalY=0 NormalZ=1 AngleXU=0 Radius=1
    g2: Circle CenterX=8 CenterY=6 CenterZ=0 NormalX=0 NormalY=0 NormalZ=1 AngleXU=0 Radius=1
    g3: BSplineCurve PolesCount=3 KnotsCount=2 Degree=2 IsPeriodic=0
    g4: GeomPoint X=0 Y=0 Z=0
    g5: GeomPoint X=8 Y=6 Z=0
    g6: LineSegment StartX=0 StartY=6 StartZ=0 EndX=8 EndY=6 EndZ=0
  constraints (14):
    c: Coincident(g0,g-1)
    c: Distance(g0) = 6
    c: Vertical(g0)
    c: Coincident(g3,g0)
    c: Weight(g1) = 1
    c: Equal(g1,g2)
    c: InternalAlignment(g1,g3)
    c: InternalAlignment(g2,g3)
    c: InternalAlignment(g4,g3)
    c: InternalAlignment(g5,g3)
    c: Block(g3)
    c: Coincident(g6,g0)
    c: Coincident(g6,g3)
    c: Horizontal(g6)
FEATURE [Part::Extrusion] Extrude034  label="caseScrewPillarBracket012"
  Base = -> Sketch043
  Dir = (0,0,1)
  DirMode = 2
  FaceMakerClass = Part::FaceMakerBullseye
  LengthFwd = 2.4
  LengthRev = 0
  Placement = pos=(88.3,29,65.23) rot=(0,1,0;1.5708rad)
  Solid = true
  Symmetric = false
FEATURE [Sketcher::SketchObject] Sketch044
  FullyConstrained = true
  sketch-geometry (7):
    g0: LineSegment StartX=0 StartY=0 StartZ=0 EndX=0 EndY=6 EndZ=0
    g1: Circle CenterX=0 CenterY=0 CenterZ=0 NormalX=0 NormalY=0 NormalZ=1 AngleXU=0 Radius=1
    g2: Circle CenterX=8 CenterY=6 CenterZ=0 NormalX=0 NormalY=0 NormalZ=1 AngleXU=0 Radius=1
    g3: BSplineCurve PolesCount=3 KnotsCount=2 Degree=2 IsPeriodic=0
    g4: GeomPoint X=0 Y=0 Z=0
    g5: GeomPoint X=8 Y=6 Z=0
    g6: LineSegment StartX=0 StartY=6 StartZ=0 EndX=8 EndY=6 EndZ=0
  constraints (14):
    c: Coincident(g0,g-1)
    c: Distance(g0) = 6
    c: Vertical(g0)
    c: Coincident(g3,g0)
    c: Weight(g1) = 1
    c: Equal(g1,g2)
    c: InternalAlignment(g1,g3)
    c: InternalAlignment(g2,g3)
    c: InternalAlignment(g4,g3)
    c: InternalAlignment(g5,g3)
    c: Block(g3)
    c: Coincident(g6,g0)
    c: Coincident(g6,g3)
    c: Horizontal(g6)
FEATURE [Part::Extrusion] Extrude035  label="caseScrewPillarBracket013"
  Base = -> Sketch044
  Dir = (0,0,1)
  DirMode = 2
  FaceMakerClass = Part::FaceMakerBullseye
  LengthFwd = 2.4
  LengthRev = 0
  Placement = pos=(90.7,29,6.77) rot=(0,-1,0;1.5708rad)
  Solid = true
  Symmetric = false
FEATURE [Sketcher::SketchObject] Sketch045
  FullyConstrained = true
  sketch-geometry (7):
    g0: LineSegment StartX=0 StartY=0 StartZ=0 EndX=0 EndY=6 EndZ=0
    g1: Circle CenterX=0 CenterY=0 CenterZ=0 NormalX=0 NormalY=0 NormalZ=1 AngleXU=0 Radius=1
    g2: Circle CenterX=8 CenterY=6 CenterZ=0 NormalX=0 NormalY=0 NormalZ=1 AngleXU=0 Radius=1
    g3: BSplineCurve PolesCount=3 KnotsCount=2 Degree=2 IsPeriodic=0
    g4: GeomPoint X=0 Y=0 Z=0
    g5: GeomPoint X=8 Y=6 Z=0
    g6: LineSegment StartX=0 StartY=6 StartZ=0 EndX=8 EndY=6 EndZ=0
  constraints (14):
    c: Coincident(g0,g-1)
    c: Distance(g0) = 6
    c: Vertical(g0)
    c: Coincident(g3,g0)
    c: Weight(g1) = 1
    c: Equal(g1,g2)
    c: InternalAlignment(g1,g3)
    c: InternalAlignment(g2,g3)
    c: InternalAlignment(g4,g3)
    c: InternalAlignment(g5,g3)
    c: Block(g3)
    c: Coincident(g6,g0)
    c: Coincident(g6,g3)
    c: Horizontal(g6)
FEATURE [Sketcher::SketchObject] Sketch046
  FullyConstrained = true
  sketch-geometry (7):
    g0: LineSegment StartX=0 StartY=0 StartZ=0 EndX=0 EndY=6 EndZ=0
    g1: Circle CenterX=0 CenterY=0 CenterZ=0 NormalX=0 NormalY=0 NormalZ=1 AngleXU=0 Radius=1
    g2: Circle CenterX=8 CenterY=6 CenterZ=0 NormalX=0 NormalY=0 NormalZ=1 AngleXU=0 Radius=1
    g3: BSplineCurve PolesCount=3 KnotsCount=2 Degree=2 IsPeriodic=0
    g4: GeomPoint X=0 Y=0 Z=0
    g5: GeomPoint X=8 Y=6 Z=0
    g6: LineSegment StartX=0 StartY=6 StartZ=0 EndX=8 EndY=6 EndZ=0
  constraints (14):
    c: Coincident(g0,g-1)
    c: Distance(g0) = 6
    c: Vertical(g0)
    c: Coincident(g3,g0)
    c: Weight(g1) = 1
    c: Equal(g1,g2)
    c: InternalAlignment(g1,g3)
    c: InternalAlignment(g2,g3)
    c: InternalAlignment(g4,g3)
    c: InternalAlignment(g5,g3)
    c: Block(g3)
    c: Coincident(g6,g0)
    c: Coincident(g6,g3)
    c: Horizontal(g6)
FEATURE [Part::Extrusion] Extrude036  label="caseScrewPillarBracket014"
  Base = -> Sketch045
  Dir = (0,0,1)
  DirMode = 2
  FaceMakerClass = Part::FaceMakerBullseye
  LengthFwd = 2.4
  LengthRev = 0
  Placement = pos=(110.7,29,6.77) rot=(0,-1,0;1.5708rad)
  Solid = true
  Symmetric = false
FEATURE [Part::Extrusion] Extrude037  label="caseScrewPillarBracket015"
  Base = -> Sketch046
  Dir = (0,0,1)
  DirMode = 2
  FaceMakerClass = Part::FaceMakerBullseye
  LengthFwd = 2.4
  LengthRev = 0
  Placement = pos=(108.3,29,65.23) rot=(0,1,0;1.5708rad)
  Solid = true
  Symmetric = false
FEATURE [Part::Box] Box013  label="frontCaseScrewPillarBracket002"
  AttacherType = Attacher::AttachEngine3D
  Height = 2.4
  Length = 22
  Placement = pos=(87,28,2.3) rot=(0,0,1;0rad)
  Width = 7
FEATURE [Part::Box] Box014  label="frontCaseScrewPillarBracket003"
  AttacherType = Attacher::AttachEngine3D
  Height = 2.4
  Length = 22
  Placement = pos=(87,28,67.3) rot=(0,0,1;0rad)
  Width = 7
FEATURE [Part::Feature] Face087
  shape: bbox 4.8 x 30.2 x 2e-07 mm, 1 faces, 0 solids (baked)
FEATURE [Part::Revolution] Revolve091  label="frontCaseScrewPost004"
  Angle = 360
  Axis = (0,1,0)
  Base = (0,0,0)
  FaceMakerClass = Part::FaceMakerBullseye
  Placement = pos=(89.5,4.5,3.5) rot=(0,0,1;0rad)
  Solid = false
  Source = -> Face087
  Symmetric = false
FEATURE [Part::Feature] Face088
  shape: bbox 4.8 x 30.2 x 2e-07 mm, 1 faces, 0 solids (baked)
FEATURE [Part::Revolution] Revolve092  label="frontCaseScrewPost005"
  Angle = 360
  Axis = (0,1,0)
  Base = (0,0,0)
  FaceMakerClass = Part::FaceMakerBullseye
  Placement = pos=(89.5,4.5,68.5) rot=(0,0,1;0rad)
  Solid = false
  Source = -> Face088
  Symmetric = false
FEATURE [Part::Feature] Face089
  shape: bbox 3.5 x 30.2 x 2e-07 mm, 1 faces, 0 solids (baked)
FEATURE [Part::Revolution] Revolve093  label="backCaseScrewPost002"
  Angle = 360
  Axis = (0,1,0)
  Base = (0,0,0)
  FaceMakerClass = Part::FaceMakerBullseye
  Placement = pos=(12.5,4.5,10) rot=(0,0,1;0rad)
  Solid = false
  Source = -> Face089
  Symmetric = false
FEATURE [Part::Feature] Face090
  shape: bbox 3.5 x 30.2 x 2e-07 mm, 1 faces, 0 solids (baked)
FEATURE [Part::Revolution] Revolve094  label="backCaseScrewPost003"
  Angle = 360
  Axis = (0,1,0)
  Base = (0,0,0)
  FaceMakerClass = Part::FaceMakerBullseye
  Placement = pos=(12.5,4.5,62) rot=(0,0,1;0rad)
  Solid = false
  Source = -> Face090
  Symmetric = false
FEATURE [Part::Box] Box015  label="Cube011"
  AttacherType = Attacher::AttachEngine3D
  Height = 28.8
  Length = 3
  Placement = pos=(107.3,28,21.6) rot=(0,0,1;0rad)
  Width = 7
FEATURE [Part::Box] Box016  label="Cube012"
  AttacherType = Attacher::AttachEngine3D
  Height = 3
  Length = 7.4
  Placement = pos=(107.3,28,18.6) rot=(0,0,1;0rad)
  Width = 7
FEATURE [Part::Box] Box017  label="Cube013"
  AttacherType = Attacher::AttachEngine3D
  Height = 3
  Length = 7.4
  Placement = pos=(107.3,28,50.4) rot=(0,0,1;0rad)
  Width = 7
FEATURE [Part::Cylinder] Cylinder024
  Angle = 360
  AttacherType = Attacher::AttachEngine3D
  Height = 20
  Placement = pos=(0,0,36.15) rot=(0,0,1;0rad)
  Radius = 14.3
FEATURE [Part::Cylinder] Cylinder025
  Angle = 360
  AttacherType = Attacher::AttachEngine3D
  Height = 10
  Placement = pos=(0,0,36.15) rot=(0,0,1;0rad)
  Radius = 4
FEATURE [Part::MultiFuse] Fusion066  label="removeToCreteHoleForPlugHousing009"
  Placement = pos=(70,19,36) rot=(0,1,0;1.5708rad)
  Shapes = -> [Cylinder024,Cylinder025]
FEATURE [Part::MultiFuse] Fusion065  label="plugHousingBracketHolder002"
  Shapes = -> [Box017,Box015,Box016]
FEATURE [Part::Cut] Cut025  label="plugHousingBracketHolder003"
  Base = -> Fusion065
  Placement = pos=(7,0,0) rot=(0,0,1;0rad)
  Tool = -> Fusion066
FEATURE [Sketcher::SketchObject] Sketch047
  FullyConstrained = false
  Placement = pos=(0,0,0) rot=(1,0,0;1.5708rad)
  sketch-geometry (24):
    g0: ArcOfCircle CenterX=-4 CenterY=-10.5 CenterZ=0 NormalX=0 NormalY=0 NormalZ=1 AngleXU=0 Radius=1.5 StartAngle=6e-16 EndAngle=3.14159
    g1: ArcOfCircle CenterX=-34.2 CenterY=-10.5 CenterZ=0 NormalX=0 NormalY=0 NormalZ=1 AngleXU=0 Radius=1.5 StartAngle=0 EndAngle=3.14159
    g2: ArcOfCircle CenterX=-34.2 CenterY=-27.7 CenterZ=0 NormalX=0 NormalY=0 NormalZ=1 AngleXU=0 Radius=1.5 StartAngle=3.14159 EndAngle=6.28319
    g3: ArcOfCircle CenterX=-4 CenterY=-27.7 CenterZ=0 NormalX=0 NormalY=0 NormalZ=1 AngleXU=0 Radius=1.5 StartAngle=3.1416 EndAngle=6.28319
    g4: ArcOfCircle CenterX=-10 CenterY=-4.3 CenterZ=0 NormalX=0 NormalY=0 NormalZ=1 AngleXU=0 Radius=1.5 StartAngle=2e-16 EndAngle=3.14159
    g5: ArcOfCircle CenterX=-16.1 CenterY=-1.8 CenterZ=0 NormalX=0 NormalY=0 NormalZ=1 AngleXU=0 Radius=1.5 StartAngle=5e-16 EndAngle=3.14159
    g6: ArcOfCircle CenterX=-22.1 CenterY=-1.8 CenterZ=0 NormalX=0 NormalY=0 NormalZ=1 AngleXU=0 Radius=1.5 StartAngle=5e-16 EndAngle=3.14159
    g7: ArcOfCircle CenterX=-28.2 CenterY=-4.3 CenterZ=0 NormalX=0 NormalY=0 NormalZ=1 AngleXU=0 Radius=1.5 StartAngle=2e-16 EndAngle=3.14159
    g8: ArcOfCircle CenterX=-10 CenterY=-33.9 CenterZ=0 NormalX=0 NormalY=0 NormalZ=1 AngleXU=0 Radius=1.5 StartAngle=3.14159 EndAngle=6.28319
    g9: ArcOfCircle CenterX=-16.1 CenterY=-36.4 CenterZ=0 NormalX=0 NormalY=0 NormalZ=1 AngleXU=0 Radius=1.5 StartAngle=3.14159 EndAngle=6.28319
    g10: ArcOfCircle CenterX=-22.1 CenterY=-36.4 CenterZ=0 NormalX=0 NormalY=0 NormalZ=1 AngleXU=0 Radius=1.5 StartAngle=3.14159 EndAngle=6.28319
    g11: ArcOfCircle CenterX=-28.2 CenterY=-33.9 CenterZ=0 NormalX=0 NormalY=0 NormalZ=1 AngleXU=0 Radius=1.5 StartAngle=3.14159 EndAngle=6.28319
    g12: LineSegment StartX=-35.7 StartY=-10.5 StartZ=0 EndX=-35.7 EndY=-27.7 EndZ=0
    g13: LineSegment StartX=-32.7 StartY=-10.5 StartZ=0 EndX=-32.7 EndY=-27.7 EndZ=0
    g14: LineSegment StartX=-29.7 StartY=-33.9 StartZ=0 EndX=-29.7 EndY=-4.3 EndZ=0
    g15: LineSegment StartX=-26.7 StartY=-33.9 StartZ=0 EndX=-26.7 EndY=-4.3 EndZ=0
    g16: LineSegment StartX=-2.5 StartY=-10.5 StartZ=0 EndX=-2.5 EndY=-27.7 EndZ=0
    g17: LineSegment StartX=-8.5 StartY=-4.3 StartZ=0 EndX=-8.5 EndY=-33.9 EndZ=0
    g18: LineSegment StartX=-5.5 StartY=-10.5 StartZ=0 EndX=-5.5 EndY=-27.7 EndZ=0
    g19: LineSegment StartX=-11.5 StartY=-4.3 StartZ=0 EndX=-11.5 EndY=-33.9 EndZ=0
    g20: LineSegment StartX=-14.6 StartY=-1.8 StartZ=0 EndX=-14.6 EndY=-36.4 EndZ=0
    g21: LineSegment StartX=-17.6 StartY=-1.8 StartZ=0 EndX=-17.6 EndY=-36.4 EndZ=0
    g22: LineSegment StartX=-20.6 StartY=-36.4 StartZ=0 EndX=-20.6 EndY=-1.8 EndZ=0
    g23: LineSegment StartX=-23.6 StartY=-1.8 StartZ=0 EndX=-23.6 EndY=-36.4 EndZ=0
  constraints (48):
    c: Block(g0)
    c: Block(g1)
    c: Block(g2)
    c: Block(g3)
    c: Block(g4)
    c: Block(g5)
    c: Block(g6)
    c: Block(g7)
    c: Block(g8)
    c: Block(g9)
    c: Block(g10)
    c: Block(g11)
    c: Coincident(g12,g1)
    c: Coincident(g12,g2)
    c: Vertical(g12)
    c: Coincident(g13,g1)
    c: Coincident(g13,g2)
    c: Vertical(g13)
    c: Coincident(g14,g11)
    c: Coincident(g14,g7)
    c: Vertical(g14)
    c: Coincident(g15,g11)
    c: Coincident(g15,g7)
    c: Vertical(g15)
    c: Coincident(g16,g0)
    c: Coincident(g16,g3)
    c: Vertical(g16)
    c: Coincident(g17,g4)
    c: Coincident(g17,g8)
    c: Vertical(g17)
    c: Coincident(g18,g0)
    c: Coincident(g18,g3)
    c: Vertical(g18)
    c: Coincident(g19,g4)
    c: Coincident(g19,g8)
    c: Vertical(g19)
    c: Coincident(g20,g5)
    c: Coincident(g20,g9)
    c: Vertical(g20)
    c: Coincident(g21,g5)
    c: Coincident(g21,g9)
    c: Vertical(g21)
    c: Coincident(g22,g10)
    c: Coincident(g22,g6)
    c: Vertical(g22)
    c: Coincident(g23,g6)
    c: Coincident(g23,g10)
    c: Vertical(g23)
FEATURE [Part::Extrusion] Extrude038  label="removeToCreateFanGrillHoles001"
  Base = -> Sketch047
  Dir = (0,-1,6e-16)
  DirMode = 2
  FaceMakerClass = Part::FaceMakerBullseye
  LengthFwd = 10
  LengthRev = 0
  Placement = pos=(65.4,44,54.82) rot=(0,0,1;0rad)
  Solid = true
  Symmetric = false
FEATURE [Part::Feature] Wire004
  shape: bbox 11 x 5.2 x 2e-07 mm, 0 faces, 0 solids (baked)
FEATURE [Part::Revolution] Revolve095
  Angle = 360
  Axis = (0,1,0)
  Base = (0,0,0)
  FaceMakerClass = Part::FaceMakerBullseye
  Placement = pos=(30.3,38,19.7) rot=(0,0,1;0rad)
  Solid = true
  Source = -> Wire004
  Symmetric = false
FEATURE [Part::Feature] Wire005
  shape: bbox 11 x 5.2 x 2e-07 mm, 0 faces, 0 solids (baked)
FEATURE [Part::Revolution] Revolve096
  Angle = 360
  Axis = (0,1,0)
  Base = (0,0,0)
  FaceMakerClass = Part::FaceMakerBullseye
  Placement = pos=(30.3,38,51.7) rot=(0,0,1;0rad)
  Solid = true
  Source = -> Wire005
  Symmetric = false
FEATURE [Part::Feature] Wire006
  shape: bbox 11 x 5.2 x 2e-07 mm, 0 faces, 0 solids (baked)
FEATURE [Part::Revolution] Revolve097
  Angle = 360
  Axis = (0,1,0)
  Base = (0,0,0)
  FaceMakerClass = Part::FaceMakerBullseye
  Placement = pos=(62.3,38,51.7) rot=(0,0,1;0rad)
  Solid = true
  Source = -> Wire006
  Symmetric = false
FEATURE [Part::Feature] Wire007
  shape: bbox 11 x 5.2 x 2e-07 mm, 0 faces, 0 solids (baked)
FEATURE [Part::Revolution] Revolve098
  Angle = 360
  Axis = (0,1,0)
  Base = (0,0,0)
  FaceMakerClass = Part::FaceMakerBullseye
  Placement = pos=(62.3,38,19.7) rot=(0,0,1;0rad)
  Solid = true
  Source = -> Wire007
  Symmetric = false
FEATURE [Part::MultiFuse] Fusion067  label="fanScrewHousing002"
  Shapes = -> [Revolve098,Revolve097,Revolve096,Revolve095]
FEATURE [Part::Feature] Face091 .. Face094  x4 (patterned run collapsed; names and placements below)
  shape: bbox 3.5 x 17.8 x 2e-07 mm, 1 faces, 0 solids (baked)
FEATURE [Part::Revolution] Revolve099  label="removeToCreateScrewAndThreadedInsertHole026"
  Angle = 360
  Axis = (0,1,0)
  Base = (0,0,0)
  FaceMakerClass = Part::FaceMakerBullseye
  Placement = pos=(62.3,30.3,19.7) rot=(0,0,1;0rad)
  Solid = false
  Source = -> Face091
  Symmetric = false
FEATURE [Part::Revolution] Revolve100  label="removeToCreateScrewAndThreadedInsertHole027"
  Angle = 360
  Axis = (0,1,0)
  Base = (0,0,0)
  FaceMakerClass = Part::FaceMakerBullseye
  Placement = pos=(62.3,30.3,51.7) rot=(0,0,1;0rad)
  Solid = false
  Source = -> Face092
  Symmetric = false
FEATURE [Part::Revolution] Revolve101  label="removeToCreateScrewAndThreadedInsertHole028"
  Angle = 360
  Axis = (0,1,0)
  Base = (0,0,0)
  FaceMakerClass = Part::FaceMakerBullseye
  Placement = pos=(30.3,30.3,19.7) rot=(0,0,1;0rad)
  Solid = false
  Source = -> Face093
  Symmetric = false
FEATURE [Part::Revolution] Revolve102  label="removeToCreateScrewAndThreadedInsertHole029"
  Angle = 360
  Axis = (0,1,0)
  Base = (0,0,0)
  FaceMakerClass = Part::FaceMakerBullseye
  Placement = pos=(30.3,30.3,51.7) rot=(0,0,1;0rad)
  Solid = false
  Source = -> Face094
  Symmetric = false
FEATURE [Part::MultiFuse] Fusion068  label="createThreadedInsertHolesForFan002"
  Shapes = -> [Revolve099,Revolve100,Revolve101,Revolve102]
FEATURE [Part::Cut] Cut026  label="fanScrewHousing003"
  Base = -> Fusion067
  Tool = -> Fusion068
FEATURE [Sketcher::SketchObject] Sketch048
  FullyConstrained = false
  Placement = pos=(0,0,0) rot=(1,0,0;1.5708rad)
  sketch-geometry (24):
    g0: ArcOfCircle CenterX=-4 CenterY=-10.5 CenterZ=0 NormalX=0 NormalY=0 NormalZ=1 AngleXU=0 Radius=1.5 StartAngle=6e-16 EndAngle=3.14159
    g1: ArcOfCircle CenterX=-34.2 CenterY=-10.5 CenterZ=0 NormalX=0 NormalY=0 NormalZ=1 AngleXU=0 Radius=1.5 StartAngle=0 EndAngle=3.14159
    g2: ArcOfCircle CenterX=-34.2 CenterY=-27.7 CenterZ=0 NormalX=0 NormalY=0 NormalZ=1 AngleXU=0 Radius=1.5 StartAngle=3.14159 EndAngle=6.28319
    g3: ArcOfCircle CenterX=-4 CenterY=-27.7 CenterZ=0 NormalX=0 NormalY=0 NormalZ=1 AngleXU=0 Radius=1.5 StartAngle=3.1416 EndAngle=6.28319
    g4: ArcOfCircle CenterX=-10 CenterY=-4.3 CenterZ=0 NormalX=0 NormalY=0 NormalZ=1 AngleXU=0 Radius=1.5 StartAngle=2e-16 EndAngle=3.14159
    g5: ArcOfCircle CenterX=-16.1 CenterY=-1.8 CenterZ=0 NormalX=0 NormalY=0 NormalZ=1 AngleXU=0 Radius=1.5 StartAngle=5e-16 EndAngle=3.14159
    g6: ArcOfCircle CenterX=-22.1 CenterY=-1.8 CenterZ=0 NormalX=0 NormalY=0 NormalZ=1 AngleXU=0 Radius=1.5 StartAngle=5e-16 EndAngle=3.14159
    g7: ArcOfCircle CenterX=-28.2 CenterY=-4.3 CenterZ=0 NormalX=0 NormalY=0 NormalZ=1 AngleXU=0 Radius=1.5 StartAngle=2e-16 EndAngle=3.14159
    g8: ArcOfCircle CenterX=-10 CenterY=-33.9 CenterZ=0 NormalX=0 NormalY=0 NormalZ=1 AngleXU=0 Radius=1.5 StartAngle=3.14159 EndAngle=6.28319
    g9: ArcOfCircle CenterX=-16.1 CenterY=-36.4 CenterZ=0 NormalX=0 NormalY=0 NormalZ=1 AngleXU=0 Radius=1.5 StartAngle=3.14159 EndAngle=6.28319
    g10: ArcOfCircle CenterX=-22.1 CenterY=-36.4 CenterZ=0 NormalX=0 NormalY=0 NormalZ=1 AngleXU=0 Radius=1.5 StartAngle=3.14159 EndAngle=6.28319
    g11: ArcOfCircle CenterX=-28.2 CenterY=-33.9 CenterZ=0 NormalX=0 NormalY=0 NormalZ=1 AngleXU=0 Radius=1.5 StartAngle=3.14159 EndAngle=6.28319
    g12: LineSegment StartX=-35.7 StartY=-10.5 StartZ=0 EndX=-35.7 EndY=-27.7 EndZ=0
    g13: LineSegment StartX=-32.7 StartY=-10.5 StartZ=0 EndX=-32.7 EndY=-27.7 EndZ=0
    g14: LineSegment StartX=-29.7 StartY=-33.9 StartZ=0 EndX=-29.7 EndY=-4.3 EndZ=0
    g15: LineSegment StartX=-26.7 StartY=-33.9 StartZ=0 EndX=-26.7 EndY=-4.3 EndZ=0
    g16: LineSegment StartX=-2.5 StartY=-10.5 StartZ=0 EndX=-2.5 EndY=-27.7 EndZ=0
    g17: LineSegment StartX=-8.5 StartY=-4.3 StartZ=0 EndX=-8.5 EndY=-33.9 EndZ=0
    g18: LineSegment StartX=-5.5 StartY=-10.5 StartZ=0 EndX=-5.5 EndY=-27.7 EndZ=0
    g19: LineSegment StartX=-11.5 StartY=-4.3 StartZ=0 EndX=-11.5 EndY=-33.9 EndZ=0
    g20: LineSegment StartX=-14.6 StartY=-1.8 StartZ=0 EndX=-14.6 EndY=-36.4 EndZ=0
    g21: LineSegment StartX=-17.6 StartY=-1.8 StartZ=0 EndX=-17.6 EndY=-36.4 EndZ=0
    g22: LineSegment StartX=-20.6 StartY=-36.4 StartZ=0 EndX=-20.6 EndY=-1.8 EndZ=0
    g23: LineSegment StartX=-23.6 StartY=-1.8 StartZ=0 EndX=-23.6 EndY=-36.4 EndZ=0
  constraints (48):
    c: Block(g0)
    c: Block(g1)
    c: Block(g2)
    c: Block(g3)
    c: Block(g4)
    c: Block(g5)
    c: Block(g6)
    c: Block(g7)
    c: Block(g8)
    c: Block(g9)
    c: Block(g10)
    c: Block(g11)
    c: Coincident(g12,g1)
    c: Coincident(g12,g2)
    c: Vertical(g12)
    c: Coincident(g13,g1)
    c: Coincident(g13,g2)
    c: Vertical(g13)
    c: Coincident(g14,g11)
    c: Coincident(g14,g7)
    c: Vertical(g14)
    c: Coincident(g15,g11)
    c: Coincident(g15,g7)
    c: Vertical(g15)
    c: Coincident(g16,g0)
    c: Coincident(g16,g3)
    c: Vertical(g16)
    c: Coincident(g17,g4)
    c: Coincident(g17,g8)
    c: Vertical(g17)
    c: Coincident(g18,g0)
    c: Coincident(g18,g3)
    c: Vertical(g18)
    c: Coincident(g19,g4)
    c: Coincident(g19,g8)
    c: Vertical(g19)
    c: Coincident(g20,g5)
    c: Coincident(g20,g9)
    c: Vertical(g20)
    c: Coincident(g21,g5)
    c: Coincident(g21,g9)
    c: Vertical(g21)
    c: Coincident(g22,g10)
    c: Coincident(g22,g6)
    c: Vertical(g22)
    c: Coincident(g23,g6)
    c: Coincident(g23,g10)
    c: Vertical(g23)
FEATURE [Part::Extrusion] Extrude039  label="removeToCreateFanGrillHoles002"
  Base = -> Sketch048
  Dir = (0,-1,6e-16)
  DirMode = 2
  FaceMakerClass = Part::FaceMakerBullseye
  LengthFwd = 10
  LengthRev = 0
  Placement = pos=(65.4,44,54.82) rot=(0,0,1;0rad)
  Solid = true
  Symmetric = false
FEATURE [Part::Cut] Cut027  label="fanScrewHousing004"
  Base = -> Cut026
  Tool = -> Extrude038
FEATURE [Part::Cut] Cut028  label="top014"
  Base = -> Fillet026
  Tool = -> Extrude039
FEATURE [Part::Feature] Face095 .. Face098  x4 (patterned run collapsed; names and placements below)
  shape: bbox 3.5 x 17.8 x 2e-07 mm, 1 faces, 0 solids (baked)
FEATURE [Part::Revolution] Revolve103  label="removeToCreateScrewAndThreadedInsertHole030"
  Angle = 360
  Axis = (0,1,0)
  Base = (0,0,0)
  FaceMakerClass = Part::FaceMakerBullseye
  Placement = pos=(62.3,30.3,19.7) rot=(0,0,1;0rad)
  Solid = false
  Source = -> Face095
  Symmetric = false
FEATURE [Part::Revolution] Revolve104  label="removeToCreateScrewAndThreadedInsertHole031"
  Angle = 360
  Axis = (0,1,0)
  Base = (0,0,0)
  FaceMakerClass = Part::FaceMakerBullseye
  Placement = pos=(62.3,30.3,51.7) rot=(0,0,1;0rad)
  Solid = false
  Source = -> Face096
  Symmetric = false
FEATURE [Part::Revolution] Revolve105  label="removeToCreateScrewAndThreadedInsertHole032"
  Angle = 360
  Axis = (0,1,0)
  Base = (0,0,0)
  FaceMakerClass = Part::FaceMakerBullseye
  Placement = pos=(30.3,30.3,19.7) rot=(0,0,1;0rad)
  Solid = false
  Source = -> Face097
  Symmetric = false
FEATURE [Part::Revolution] Revolve106  label="removeToCreateScrewAndThreadedInsertHole033"
  Angle = 360
  Axis = (0,1,0)
  Base = (0,0,0)
  FaceMakerClass = Part::FaceMakerBullseye
  Placement = pos=(30.3,30.3,51.7) rot=(0,0,1;0rad)
  Solid = false
  Source = -> Face098
  Symmetric = false
FEATURE [Part::MultiFuse] Fusion069  label="createThreadedInsertHolesForFan003"
  Shapes = -> [Revolve103,Revolve104,Revolve105,Revolve106]
FEATURE [Part::Cut] Cut029  label="top015"
  Base = -> Cut028
  Tool = -> Fusion054
FEATURE [Part::Cut] Cut030  label="fanScrewHousing005"
  Base = -> Cut027
  Tool = -> Fusion069
FEATURE [Part::Cylinder] Cylinder026  label="removeToCreteHoleForPlugHousing010"
  Angle = 360
  AttacherType = Attacher::AttachEngine3D
  Height = 20
  Placement = pos=(-2,19,36) rot=(0,1,0;1.5708rad)
  Radius = 14.3
FEATURE [Part::Box] Box018  label="removeToCreteHoleForPlugHousing011"
  AttacherType = Attacher::AttachEngine3D
  Height = 28.6
  Length = 10
  Placement = pos=(-2,0,21.7) rot=(0,0,1;0rad)
  Width = 19
FEATURE [Part::Box] Box019  label="wireHolderBottomCaseBit"
  AttacherType = Attacher::AttachEngine3D
  Height = 28
  Length = 3
  Placement = pos=(0,0,22) rot=(0,0,1;0rad)
  Width = 21
FEATURE [Part::Cylinder] Cylinder027  label="removeToCreteHoleForPlugHousing012"
  Angle = 360
  AttacherType = Attacher::AttachEngine3D
  Height = 20
  Placement = pos=(-2,19,36) rot=(0,1,0;1.5708rad)
  Radius = 14.3
FEATURE [Part::Cut] Cut031  label="wireHolderBottomCaseBit001"
  Base = -> Box019
  Tool = -> Cylinder027
FEATURE [Part::MultiFuse] Fusion070  label="removeToCreteHoleForPlugHousing013"
  Shapes = -> [Box018,Cylinder026]
FEATURE [Part::Cut] Cut032  label="top016"
  Base = -> Cut029
  Tool = -> Fusion070
FEATURE [Part::Cylinder] Cylinder028
  Angle = 360
  AttacherType = Attacher::AttachEngine3D
  Height = 20
  Placement = pos=(0,0,36.15) rot=(0,0,1;0rad)
  Radius = 14.3
FEATURE [Part::Cylinder] Cylinder029
  Angle = 360
  AttacherType = Attacher::AttachEngine3D
  Height = 10
  Placement = pos=(0,0,36.15) rot=(0,0,1;0rad)
  Radius = 4
FEATURE [Part::MultiFuse] Fusion071  label="removeToCreteHoleForPlugHousing014"
  Placement = pos=(70,19,36) rot=(0,1,0;1.5708rad)
  Shapes = -> [Cylinder028,Cylinder029]
FEATURE [Sketcher::SketchObject] Sketch049  label="topSketch011"
  FullyConstrained = true
  sketch-geometry (4):
    g0: ArcOfCircle CenterX=105 CenterY=19 CenterZ=0 NormalX=0 NormalY=0 NormalZ=1 AngleXU=0 Radius=20.6155 StartAngle=5.54125 EndAngle=6.28319
    g1: ArcOfCircle CenterX=105 CenterY=19 CenterZ=0 NormalX=0 NormalY=0 NormalZ=1 AngleXU=0 Radius=13 StartAngle=5.54125 EndAngle=6.28319
    g2: LineSegment StartX=118 StartY=19 StartZ=0 EndX=125.616 EndY=19 EndZ=0
    g3: LineSegment StartX=114.583 StartY=10.2157 StartZ=0 EndX=120.197 EndY=5.06982 EndZ=0
  constraints (7):
    c: Block(g0)
    c: Block(g1)
    c: Coincident(g2,g1)
    c: Coincident(g2,g0)
    c: Horizontal(g2)
    c: Coincident(g3,g1)
    c: Coincident(g3,g0)
FEATURE [Part::Box] Box020  label="removeToCreteHoleForPlugHousing015"
  AttacherType = Attacher::AttachEngine3D
  Height = 28.6
  Length = 20
  Placement = pos=(106.15,0,21.7) rot=(0,0,1;0rad)
  Width = 19
FEATURE [Part::MultiFuse] Fusion072  label="removeToCreteHoleForPlugHousing016"
  Shapes = -> [Box020,Fusion071]
FEATURE [Part::Cut] Cut033  label="removeToCreteHoleForPlugHousing017"
  Base = -> Cut032
  Tool = -> Fusion072
FEATURE [Part::Cylinder] Cylinder030
  Angle = 360
  AttacherType = Attacher::AttachEngine3D
  Height = 20
  Placement = pos=(0,0,36.15) rot=(0,0,1;0rad)
  Radius = 14.3
FEATURE [Part::Cylinder] Cylinder031
  Angle = 360
  AttacherType = Attacher::AttachEngine3D
  Height = 10
  Placement = pos=(0,0,36.15) rot=(0,0,1;0rad)
  Radius = 4
FEATURE [Part::Box] Box021  label="removeToCreteHoleForPlugHousing019"
  AttacherType = Attacher::AttachEngine3D
  Height = 28.6
  Length = 20
  Placement = pos=(106.15,0,21.7) rot=(0,0,1;0rad)
  Width = 19
FEATURE [Part::MultiFuse] Fusion074  label="removeToCreteHoleForPlugHousing020"
  Placement = pos=(70,19,36) rot=(0,1,0;1.5708rad)
  Shapes = -> [Cylinder030,Cylinder031]
FEATURE [Part::MultiFuse] Fusion073  label="removeToCreteHoleForPlugHousing018"
  Placement = pos=(0,0,28.3) rot=(0,0,1;0rad)
  Shapes = -> [Box021,Fusion074]
FEATURE [Part::Cylinder] Cylinder032
  Angle = 360
  AttacherType = Attacher::AttachEngine3D
  Height = 20
  Placement = pos=(0,0,36.15) rot=(0,0,1;0rad)
  Radius = 14.3
FEATURE [Part::Cylinder] Cylinder033
  Angle = 360
  AttacherType = Attacher::AttachEngine3D
  Height = 10
  Placement = pos=(0,0,36.15) rot=(0,0,1;0rad)
  Radius = 4
FEATURE [Part::Box] Box022  label="removeToCreteHoleForPlugHousing021"
  AttacherType = Attacher::AttachEngine3D
  Height = 28.6
  Length = 20
  Placement = pos=(106.15,0,21.7) rot=(0,0,1;0rad)
  Width = 19
FEATURE [Part::MultiFuse] Fusion076  label="removeToCreteHoleForPlugHousing023"
  Placement = pos=(70,19,36) rot=(0,1,0;1.5708rad)
  Shapes = -> [Cylinder032,Cylinder033]
FEATURE [Part::MultiFuse] Fusion075  label="removeToCreteHoleForPlugHousing022"
  Placement = pos=(0,0,-28.3) rot=(0,0,1;0rad)
  Shapes = -> [Box022,Fusion076]
FEATURE [Part::MultiFuse] Fusion077  label="removeToCreatePlugHousingBottomBit"
  Shapes = -> [Fusion075,Fusion073]
FEATURE [Part::Cylinder] Cylinder034
  Angle = 360
  AttacherType = Attacher::AttachEngine3D
  Height = 20
  Placement = pos=(0,0,36.15) rot=(0,0,1;0rad)
  Radius = 14
FEATURE [Part::Cylinder] Cylinder035
  Angle = 360
  AttacherType = Attacher::AttachEngine3D
  Height = 10
  Placement = pos=(0,0,36.15) rot=(0,0,1;0rad)
  Radius = 4
FEATURE [Part::MultiFuse] Fusion078  label="removeToCreteHoleForPlugHousing024"
  Placement = pos=(70,19,36) rot=(0,1,0;1.5708rad)
  Shapes = -> [Cylinder034,Cylinder035]
FEATURE [Part::MultiFuse] Fusion079  label="removeToCreatePlugHousingBottomBit001"
  Shapes = -> [Fusion078,Fusion077]
FEATURE [Part::Extrusion] Extrude040  label="bottomPlugHousingBit"
  Base = -> Sketch049
  Dir = (0,0,1)
  DirMode = 2
  FaceMakerClass = Part::FaceMakerBullseye
  LengthFwd = 72
  LengthRev = 0
  Solid = true
  Symmetric = false
FEATURE [Part::Cut] Cut034  label="bottomPlugHousingBit001"
  Base = -> Extrude040
  Placement = pos=(-0.09,0,0) rot=(0,0,1;0rad)
  Tool = -> Fusion079
FEATURE [Part::Box] Box023  label="Cube014"
  AttacherType = Attacher::AttachEngine3D
  Height = 16
  Length = 8
  Placement = pos=(12.7,31.52,28) rot=(0,0,1;0rad)
  Width = 4
FEATURE [Part::Cylinder] Cylinder036
  Angle = 360
  AttacherType = Attacher::AttachEngine3D
  Height = 10
  Placement = pos=(0,0,36.15) rot=(0,0,1;0rad)
  Radius = 4
FEATURE [Part::Cylinder] Cylinder037
  Angle = 360
  AttacherType = Attacher::AttachEngine3D
  Height = 20
  Placement = pos=(0,0,36.15) rot=(0,0,1;0rad)
  Radius = 8.2
FEATURE [Part::MultiFuse] Fusion080  label="removeToCreteHoleForPlugHousing025"
  Placement = pos=(-42,19,36) rot=(0,1,0;1.5708rad)
  Shapes = -> [Cylinder037,Cylinder036]
FEATURE [Sketcher::SketchObject] Sketch050  label="topSketch012"
  FullyConstrained = true
  sketch-geometry (4):
    g0: LineSegment StartX=16.8446 StartY=31.512 StartZ=0 EndX=16.3251 EndY=34.4666 EndZ=0
    g1: ArcOfCircle CenterX=19 CenterY=19.2524 CenterZ=0 NormalX=0 NormalY=0 NormalZ=1 AngleXU=0 Radius=15.4476 StartAngle=1.74483 EndAngle=2.72717
    g2: ArcOfCircle CenterX=19 CenterY=19.2524 CenterZ=0 NormalX=0 NormalY=0 NormalZ=1 AngleXU=0 Radius=12.4476 StartAngle=1.74483 EndAngle=2.73189
    g3: LineSegment StartX=4.86004 StartY=25.4725 StartZ=0 EndX=7.58253 EndY=24.2107 EndZ=0
  constraints (7):
    c: Block(g0)
    c: Coincident(g1,g0)
    c: Coincident(g2,g0)
    c: Coincident(g3,g1)
    c: Coincident(g3,g2)
    c: Block(g1)
    c: Block(g2)
FEATURE [Part::Extrusion] Extrude041
  Base = -> Sketch050
  Dir = (0,0,1)
  DirMode = 2
  FaceMakerClass = Part::FaceMakerBullseye
  LengthFwd = 10.6
  LengthRev = 0
  Placement = pos=(0,0,31) rot=(0,0,1;0rad)
  Solid = true
  Symmetric = false
FEATURE [Part::Cut] Cut035
  Base = -> Extrude041
  Placement = pos=(0,0,-0.3) rot=(0,0,1;0rad)
  Tool = -> Fusion080
FEATURE [Part::Cut] Cut036
  Base = -> Box023
  Tool = -> Cut035
FEATURE [Part::Fillet] Fillet027
  Base = -> Cut036
  Edges = 1 edges r=0.7: [Edge13]
FEATURE [Part::Fillet] Fillet028
  Base = -> Fillet027
  Edges = 1 edges r=0.7: [Edge13]
FEATURE [Part::Fillet] Fillet029
  Base = -> Fillet028
  Edges = 1 edges r=0.7: [Edge16]
FEATURE [Part::Fillet] Fillet030
  Base = -> Fillet029
  Edges = 1 edges r=0.7: [Edge11]
FEATURE [Part::Fillet] Fillet031
  Base = -> Fillet030
  Edges = 1 edges r=0.7: [Edge10]
FEATURE [Part::Fillet] Fillet032
  Base = -> Fillet031
  Edges = 1 edges r=1.2: [Edge5]
FEATURE [Part::Fillet] Fillet033
  Base = -> Fillet032
  Edges = 1 edges r=1.2: [Edge12]
FEATURE [Part::Fillet] Fillet034  label="wireHousingRetainer"
  Base = -> Fillet033
  Edges = 1 edges r=2: [Edge1]
  Placement = pos=(0.3,0,0) rot=(0,0,1;0rad)
FEATURE [Part::Feature] Face099
  shape: bbox 3.5 x 17.8 x 2e-07 mm, 1 faces, 0 solids (baked)
FEATURE [Part::Revolution] Revolve107  label="removeToCreateScrewAndThreadedInsertHole034"
  Angle = 360
  Axis = (0,1,0)
  Base = (0,0,0)
  FaceMakerClass = Part::FaceMakerBullseye
  Placement = pos=(12.5,0,10) rot=(0,0,1;0rad)
  Solid = false
  Source = -> Face099
  Symmetric = false
FEATURE [Part::Feature] Face100
  shape: bbox 3.5 x 17.8 x 2e-07 mm, 1 faces, 0 solids (baked)
FEATURE [Part::Revolution] Revolve108  label="removeToCreateScrewAndThreadedInsertHole035"
  Angle = 360
  Axis = (0,1,0)
  Base = (0,0,0)
  FaceMakerClass = Part::FaceMakerBullseye
  Placement = pos=(12.5,0,62) rot=(0,0,1;0rad)
  Solid = false
  Source = -> Face100
  Symmetric = false
FEATURE [Part::Feature] Face101
  shape: bbox 3.5 x 17.8 x 2e-07 mm, 1 faces, 0 solids (baked)
FEATURE [Part::Revolution] Revolve109  label="removeToCreateScrewAndThreadedInsertHole036"
  Angle = 360
  Axis = (0,1,0)
  Base = (0,0,0)
  FaceMakerClass = Part::FaceMakerBullseye
  Placement = pos=(89.5,0,68.5) rot=(0,0,1;0rad)
  Solid = false
  Source = -> Face101
  Symmetric = false
FEATURE [Part::Feature] Face102
  shape: bbox 3.5 x 17.8 x 2e-07 mm, 1 faces, 0 solids (baked)
FEATURE [Part::Revolution] Revolve110  label="removeToCreateScrewAndThreadedInsertHole037"
  Angle = 360
  Axis = (0,1,0)
  Base = (0,0,0)
  FaceMakerClass = Part::FaceMakerBullseye
  Placement = pos=(89.5,0,3.5) rot=(0,0,1;0rad)
  Solid = false
  Source = -> Face102
  Symmetric = false
FEATURE [Part::Feature] Face103
  shape: bbox 3.5 x 17.8 x 2e-07 mm, 1 faces, 0 solids (baked)
FEATURE [Part::Revolution] Revolve111  label="removeToCreateScrewAndThreadedInsertHole038"
  Angle = 360
  Axis = (0,1,0)
  Base = (0,0,0)
  FaceMakerClass = Part::FaceMakerBullseye
  Placement = pos=(109.5,4.7,3.5) rot=(0,0,1;0rad)
  Solid = false
  Source = -> Face103
  Symmetric = false
FEATURE [Part::Feature] Face104
  shape: bbox 3.5 x 17.8 x 2e-07 mm, 1 faces, 0 solids (baked)
FEATURE [Part::Revolution] Revolve112  label="removeToCreateScrewAndThreadedInsertHole039"
  Angle = 360
  Axis = (0,1,0)
  Base = (0,0,0)
  FaceMakerClass = Part::FaceMakerBullseye
  Placement = pos=(109.5,4.7,68.5) rot=(0,0,1;0rad)
  Solid = false
  Source = -> Face104
  Symmetric = false
FEATURE [Part::MultiFuse] Fusion081  label="removeToCreateScrewAndThreadedInsertHole040"
  Shapes = -> [Revolve107,Revolve108,Revolve109,Revolve110,Revolve111,Revolve112]
FEATURE [Part::MultiFuse] Fusion082  label="casePillars002"
  Shapes = -> [Revolve094,Revolve092,Revolve090,Revolve089,Revolve091,Revolve093]
FEATURE [Part::Cut] Cut037  label="casePillars003"
  Base = -> Fusion082
  Tool = -> Fusion081
FEATURE [Sketcher::SketchObject] Sketch051
  FullyConstrained = true
  Placement = pos=(117,19,0) rot=(0.57735,0.57735,0.57735;2.0944rad)
  sketch-geometry (48):
    g0: LineSegment StartX=-49.19 StartY=69.25 StartZ=0 EndX=-49.19 EndY=66.25 EndZ=0
    g1: LineSegment StartX=-49.19 StartY=63.5 StartZ=0 EndX=-49.19 EndY=60.5 EndZ=0
    g2: LineSegment StartX=-49.19 StartY=57.75 StartZ=0 EndX=-49.19 EndY=54.75 EndZ=0
    g3: LineSegment StartX=-49.19 StartY=52 StartZ=0 EndX=-49.19 EndY=49 EndZ=0
    g4: LineSegment StartX=-49.19 StartY=46.25 StartZ=0 EndX=-49.19 EndY=43.25 EndZ=0
    g5: LineSegment StartX=-49.19 StartY=40.5 StartZ=0 EndX=-49.19 EndY=37.5 EndZ=0
    g6: LineSegment StartX=-49.19 StartY=34.5 StartZ=0 EndX=-49.19 EndY=31.5 EndZ=0
    g7: LineSegment StartX=-49.19 StartY=28.75 StartZ=0 EndX=-49.19 EndY=25.75 EndZ=0
    g8: LineSegment StartX=-49.19 StartY=23 StartZ=0 EndX=-49.19 EndY=20 EndZ=0
    g9: LineSegment StartX=-49.19 StartY=17.25 StartZ=0 EndX=-49.19 EndY=14.25 EndZ=0
    g10: LineSegment StartX=-49.19 StartY=11.5 StartZ=0 EndX=-49.19 EndY=8.5 EndZ=0
    g11: LineSegment StartX=-49.19 StartY=5.75 StartZ=0 EndX=-49.19 EndY=2.75 EndZ=0
    g12: ArcOfCircle CenterX=-1.5 CenterY=67.75 CenterZ=0 NormalX=0 NormalY=0 NormalZ=1 AngleXU=0 Radius=1.5 StartAngle=4.71239 EndAngle=7.85398
    g13: ArcOfCircle CenterX=-1.5 CenterY=62 CenterZ=0 NormalX=0 NormalY=0 NormalZ=1 AngleXU=0 Radius=1.5 StartAngle=4.71239 EndAngle=7.85398
    g14: ArcOfCircle CenterX=-1.5 CenterY=56.25 CenterZ=0 NormalX=0 NormalY=0 NormalZ=1 AngleXU=0 Radius=1.5 StartAngle=4.71239 EndAngle=7.85398
    g15: ArcOfCircle CenterX=-11.49 CenterY=50.5 CenterZ=0 NormalX=0 NormalY=0 NormalZ=1 AngleXU=0 Radius=1.5 StartAngle=4.71239 EndAngle=7.85398
    g16: ArcOfCircle CenterX=-16.28 CenterY=44.75 CenterZ=0 NormalX=0 NormalY=0 NormalZ=1 AngleXU=0 Radius=1.5 StartAngle=4.71239 EndAngle=7.85398
    g17: ArcOfCircle CenterX=-18.2337 CenterY=39 CenterZ=0 NormalX=0 NormalY=0 NormalZ=1 AngleXU=0 Radius=1.5 StartAngle=4.71485 EndAngle=7.85398
    g18: ArcOfCircle CenterX=-16.2837 CenterY=27.25 CenterZ=0 NormalX=0 NormalY=0 NormalZ=1 AngleXU=0 Radius=1.5 StartAngle=4.71485 EndAngle=7.85398
    g19: ArcOfCircle CenterX=-18.2337 CenterY=33 CenterZ=0 NormalX=0 NormalY=0 NormalZ=1 AngleXU=0 Radius=1.5 StartAngle=4.71485 EndAngle=7.85398
    g20: ArcOfCircle CenterX=-11.49 CenterY=21.5 CenterZ=0 NormalX=0 NormalY=0 NormalZ=1 AngleXU=0 Radius=1.5 StartAngle=4.71239 EndAngle=7.85398
    g21: ArcOfCircle CenterX=-1.5 CenterY=4.25 CenterZ=0 NormalX=0 NormalY=0 NormalZ=1 AngleXU=0 Radius=1.5 StartAngle=4.71239 EndAngle=7.85398
    g22: ArcOfCircle CenterX=-1.5 CenterY=10 CenterZ=0 NormalX=0 NormalY=0 NormalZ=1 AngleXU=0 Radius=1.5 StartAngle=4.71239 EndAngle=7.85398
    g23: ArcOfCircle CenterX=-1.5 CenterY=15.75 CenterZ=0 NormalX=0 NormalY=0 NormalZ=1 AngleXU=0 Radius=1.5 StartAngle=4.71239 EndAngle=7.85398
    g24: LineSegment StartX=-49.19 StartY=69.25 StartZ=0 EndX=-1.5 EndY=69.25 EndZ=0
    g25: LineSegment StartX=-49.19 StartY=66.25 StartZ=0 EndX=-1.5 EndY=66.25 EndZ=0
    g26: LineSegment StartX=-49.19 StartY=63.5 StartZ=0 EndX=-1.5 EndY=63.5 EndZ=0
    g27: LineSegment StartX=-49.19 StartY=60.5 StartZ=0 EndX=-1.5 EndY=60.5 EndZ=0
    g28: LineSegment StartX=-49.19 StartY=57.75 StartZ=0 EndX=-1.5 EndY=57.75 EndZ=0
    g29: LineSegment StartX=-49.19 StartY=54.75 StartZ=0 EndX=-1.5 EndY=54.75 EndZ=0
    g30: LineSegment StartX=-49.19 StartY=52 StartZ=0 EndX=-11.49 EndY=52 EndZ=0
    g31: LineSegment StartX=-49.19 StartY=49 StartZ=0 EndX=-11.49 EndY=49 EndZ=0
    g32: LineSegment StartX=-49.19 StartY=46.25 StartZ=0 EndX=-16.28 EndY=46.25 EndZ=0
    g33: LineSegment StartX=-49.19 StartY=43.25 StartZ=0 EndX=-16.28 EndY=43.25 EndZ=0
    g34: LineSegment StartX=-49.19 StartY=40.5 StartZ=0 EndX=-18.2337 EndY=40.5 EndZ=0
    g35: LineSegment StartX=-49.19 StartY=37.5 StartZ=0 EndX=-18.23 EndY=37.5 EndZ=0
    g36: LineSegment StartX=-49.19 StartY=34.5 StartZ=0 EndX=-18.2337 EndY=34.5 EndZ=0
    g37: LineSegment StartX=-49.19 StartY=31.5 StartZ=0 EndX=-18.23 EndY=31.5 EndZ=0
    g38: LineSegment StartX=-49.19 StartY=28.75 StartZ=0 EndX=-16.2837 EndY=28.75 EndZ=0
    g39: LineSegment StartX=-49.19 StartY=25.75 StartZ=0 EndX=-16.28 EndY=25.75 EndZ=0
    g40: LineSegment StartX=-49.19 StartY=23 StartZ=0 EndX=-11.49 EndY=23 EndZ=0
    g41: LineSegment StartX=-49.19 StartY=20 StartZ=0 EndX=-11.49 EndY=20 EndZ=0
    g42: LineSegment StartX=-49.19 StartY=17.25 StartZ=0 EndX=-1.5 EndY=17.25 EndZ=0
    g43: LineSegment StartX=-49.19 StartY=14.25 StartZ=0 EndX=-1.5 EndY=14.25 EndZ=0
    g44: LineSegment StartX=-49.19 StartY=11.5 StartZ=0 EndX=-1.5 EndY=11.5 EndZ=0
    g45: LineSegment StartX=-49.19 StartY=8.5 StartZ=0 EndX=-1.5 EndY=8.5 EndZ=0
    g46: LineSegment StartX=-49.19 StartY=5.75 StartZ=0 EndX=-1.5 EndY=5.75 EndZ=0
    g47: LineSegment StartX=-49.19 StartY=2.75 StartZ=0 EndX=-1.5 EndY=2.75 EndZ=0
  constraints (120):
    c: Vertical(g0)
    c: Distance(g0) = 3
    c: Block(g0)
    c: Vertical(g1)
    c: Distance(g1) = 3
    c: Vertical(g2)
    c: Equal(g0,g2) = 3
    c: Block(g2)
    c: Vertical(g3)
    c: Equal(g1,g3) = 3
    c: Vertical(g4)
    c: Equal(g0,g4) = 3
    c: Block(g4)
    c: Vertical(g5)
    c: Equal(g1,g5) = 3
    c: Vertical(g6)
    c: Equal(g0,g6) = 3
    c: Block(g6)
    c: Vertical(g7)
    c: Equal(g1,g7) = 3
    c: Vertical(g8)
    c: Equal(g0,g8) = 3
    c: Block(g8)
    c: Vertical(g9)
    c: Equal(g1,g9) = 3
    c: Vertical(g10)
    c: Equal(g0,g10) = 3
    c: Block(g10)
    c: Vertical(g11)
    c: Equal(g1,g11) = 3
    c: Block(g12)
    c: Block(g13)
    c: Block(g14)
    c: Block(g15)
    c: Block(g16)
    c: Block(g17)
    c: Block(g18)
    c: Block(g19)
    c: Block(g20)
    c: Block(g21)
    c: Block(g22)
    c: Block(g23)
    c: Block(g11)
    c: Block(g9)
    c: Block(g7)
    c: Block(g5)
    c: Block(g3)
    c: Block(g1)
    c: Coincident(g24,g0)
    c: Coincident(g24,g12)
    c: Horizontal(g24)
    c: Coincident(g25,g0)
    c: Coincident(g25,g12)
    c: Horizontal(g25)
    c: Coincident(g26,g1)
    c: Coincident(g26,g13)
    c: Horizontal(g26)
    c: Coincident(g27,g1)
    c: Coincident(g27,g13)
    c: Horizontal(g27)
    c: Coincident(g28,g2)
    c: Coincident(g28,g14)
    c: Horizontal(g28)
    c: Coincident(g29,g2)
    c: Coincident(g29,g14)
    c: Horizontal(g29)
    c: Coincident(g30,g3)
    c: Coincident(g30,g15)
    c: Horizontal(g30)
    c: Coincident(g31,g3)
    c: Coincident(g31,g15)
    c: Horizontal(g31)
    c: Coincident(g32,g4)
    c: Coincident(g32,g16)
    c: Horizontal(g32)
    c: Coincident(g33,g4)
    c: Coincident(g33,g16)
    c: Horizontal(g33)
    c: Coincident(g34,g5)
    c: Coincident(g34,g17)
    c: Horizontal(g34)
    c: Coincident(g35,g5)
    c: Coincident(g35,g17)
    c: Horizontal(g35)
    c: Coincident(g36,g6)
    c: Coincident(g36,g19)
    c: Horizontal(g36)
    c: Coincident(g37,g6)
    c: Coincident(g37,g19)
    c: Horizontal(g37)
    c: Coincident(g38,g7)
    c: Coincident(g38,g18)
    c: Horizontal(g38)
    c: Coincident(g39,g7)
    c: Coincident(g39,g18)
    c: Horizontal(g39)
    c: Coincident(g40,g8)
    c: Coincident(g40,g20)
    c: Horizontal(g40)
    c: Coincident(g41,g8)
    c: Coincident(g41,g20)
    c: Horizontal(g41)
    c: Coincident(g42,g9)
    c: Coincident(g42,g23)
    c: Horizontal(g42)
    c: Coincident(g43,g9)
    c: Coincident(g43,g23)
    c: Horizontal(g43)
    c: Coincident(g44,g10)
    c: Coincident(g44,g22)
    c: Horizontal(g44)
    c: Coincident(g45,g10)
    c: Coincident(g45,g22)
    c: Horizontal(g45)
    c: Coincident(g46,g11)
    c: Coincident(g46,g21)
    c: Horizontal(g46)
    c: Coincident(g47,g11)
    c: Coincident(g47,g21)
    c: Horizontal(g47)
FEATURE [Part::Extrusion] Extrude042
  Base = -> Sketch051
  Dir = (1,-2e-16,2e-16)
  DirMode = 2
  FaceMakerClass = Part::FaceMakerBullseye
  LengthFwd = 19
  LengthRev = 0
  Placement = pos=(-19,0,0) rot=(0,0,1;0rad)
  Solid = true
  Symmetric = false
FEATURE [Part::Fillet] Fillet035  label="removeToCreateVentalationHoles"
  Base = -> Extrude042
  Edges = <same value as first occurrence — deduplicated (x6 in doc)>
  Placement = pos=(7,0,0) rot=(0,0,1;0rad)
FEATURE [Part::Cut] Cut038  label="top017"
  Base = -> Cut033
  Tool = -> Fillet035
FEATURE [Sketcher::SketchObject] Sketch052  label="bottomSketch001"
  FullyConstrained = true
  sketch-geometry (45):
    g0: LineSegment StartX=6.29999 StartY=8 StartZ=0 EndX=3.29999 EndY=8 EndZ=0
    g1: LineSegment StartX=3.29999 StartY=8 StartZ=0 EndX=3.29999 EndY=-6.03275e-07 EndZ=0
    g2: ArcOfCircle CenterX=8.29999 CenterY=5 CenterZ=0 NormalX=0 NormalY=0 NormalZ=1 AngleXU=0 Radius=2 StartAngle=3.14159 EndAngle=4.71239
    g3: LineSegment StartX=6.29999 StartY=8 StartZ=0 EndX=6.29999 EndY=5 EndZ=0
    g4: ArcOfCircle CenterX=105 CenterY=19 CenterZ=0 NormalX=0 NormalY=0 NormalZ=1 AngleXU=0 Radius=12.7 StartAngle=4.71239 EndAngle=5.94289
    g5-g11: Circle x7 (B-spline internal-alignment scaffolding for g12; pole/knot coordinates omitted)
    g12: BSplineCurve PolesCount=7 KnotsCount=5 Degree=3 IsPeriodic=0
    g13-g17: GeomPoint x5 (B-spline internal-alignment scaffolding for g12; pole/knot coordinates omitted)
    g18: ArcOfCircle CenterX=105 CenterY=19 CenterZ=0 NormalX=0 NormalY=0 NormalZ=1 AngleXU=0 Radius=15.7 StartAngle=5.81226 EndAngle=6.28319
    g19: BSplineCurve PolesCount=5 KnotsCount=3 Degree=3 IsPeriodic=0
    g20: LineSegment StartX=8.29999 StartY=3 StartZ=0 EndX=101.7 EndY=3 EndZ=0
    g21: LineSegment StartX=3.29999 StartY=-6.03275e-07 StartZ=0 EndX=105 EndY=-6.03275e-07 EndZ=0
    g22: LineSegment StartX=120.974 StartY=8.71251 StartZ=0 EndX=122.332 EndY=7.83778 EndZ=0
    g23: LineSegment StartX=105 StartY=-6.03274e-07 StartZ=0 EndX=113 EndY=-6.03274e-07 EndZ=0
    g24: ArcOfCircle CenterX=105 CenterY=19 CenterZ=0 NormalX=0 NormalY=0 NormalZ=1 AngleXU=0 Radius=20.6155 StartAngle=5.11091 EndAngle=5.71103
    g25: ArcOfCircle CenterX=117.7 CenterY=19 CenterZ=0 NormalX=0 NormalY=0 NormalZ=1 AngleXU=0 Radius=3 StartAngle=1.2e-15 EndAngle=2.10468
    g26: Circle CenterX=116.345 CenterY=16.3232 CenterZ=0 NormalX=0 NormalY=0 NormalZ=1 AngleXU=0 Radius=1
    g27: Circle CenterX=117.24 CenterY=15.7584 CenterZ=0 NormalX=0 NormalY=0 NormalZ=1 AngleXU=0 Radius=1
    g28: Circle CenterX=116.972 CenterY=14.7612 CenterZ=0 NormalX=0 NormalY=0 NormalZ=1 AngleXU=0 Radius=1
    g29: BSplineCurve PolesCount=3 KnotsCount=2 Degree=2 IsPeriodic=0
    g30: GeomPoint X=116.345 Y=16.3232 Z=0
    g31: GeomPoint X=116.972 Y=14.7612 Z=0
    g32: Circle CenterX=115.828 CenterY=17.157 CenterZ=0 NormalX=0 NormalY=0 NormalZ=1 AngleXU=0 Radius=1
    g33: Circle CenterX=115.841 CenterY=16.639 CenterZ=0 NormalX=0 NormalY=0 NormalZ=1 AngleXU=0 Radius=1
    g34: Circle CenterX=116.345 CenterY=16.3232 CenterZ=0 NormalX=0 NormalY=0 NormalZ=1 AngleXU=0 Radius=1
    g35: BSplineCurve PolesCount=3 KnotsCount=2 Degree=2 IsPeriodic=0
    g36: GeomPoint X=115.828 Y=17.157 Z=0
    g37: GeomPoint X=116.345 Y=16.3232 Z=0
    g38: LineSegment StartX=115.828 StartY=17.157 StartZ=0 EndX=115.828 EndY=20.8307 EndZ=0
    g39: Circle CenterX=115.828 CenterY=20.8307 CenterZ=0 NormalX=0 NormalY=0 NormalZ=1 AngleXU=0 Radius=1
    g40: Circle CenterX=115.831 CenterY=21.3396 CenterZ=0 NormalX=0 NormalY=0 NormalZ=1 AngleXU=0 Radius=1
    g41: Circle CenterX=116.173 CenterY=21.5825 CenterZ=0 NormalX=0 NormalY=0 NormalZ=1 AngleXU=0 Radius=1
    g42: BSplineCurve PolesCount=3 KnotsCount=2 Degree=2 IsPeriodic=0
    g43: GeomPoint X=115.828 Y=20.8307 Z=0
    g44: GeomPoint X=116.173 Y=21.5825 Z=0
  constraints (70):
    c: Horizontal(g0)
    c: Distance(g0) = 3
    c: Coincident(g1,g0)
    c: Vertical(g1)
    c: Block(g2)
    c: Block(g0)
    c: Coincident(g3,g0)
    c: Coincident(g3,g2)
    c: Vertical(g3)
    c: Block(g1)
    c: Block(g4)
    c: Coincident(g19,g4)
    c: Block(g19)
    c: Equal(g5, g6-g11) x6
    c: InternalAlignment(g5-g11 -> g12) x7
    c: InternalAlignment(g13-g17 -> g12) x5
    c: Block(g12)
    c: Coincident(g18,g12)
    c: Block(g18)
    c: Coincident(g20,g2)
    c: Coincident(g20,g19)
    c: Horizontal(g20)
    c: Distance(g20) = 93.4
    c: Coincident(g21,g1)
    c: Horizontal(g21)
    c: Distance(g21) = 101.7
    c: Horizontal(g23)
    c: Distance(g23) = 8
    c: Coincident(g24,g23)
    c: Block(g23)
    c: Coincident(g22,g24)
    c: Block(g24)
    c: Block(g22)
    c: Distance(g22) = 1.61553
    c: Coincident(g25,g18)
    c: Block(g25)
    c: Weight(g26) = 1
    c: Equal(g26,g27)
    c: Equal(g26,g28)
    c: Coincident(g29,g4)
    c: InternalAlignment(g26,g29)
    c: InternalAlignment(g27,g29)
    c: InternalAlignment(g28,g29)
    c: InternalAlignment(g30,g29)
    c: InternalAlignment(g31,g29)
    c: Block(g29)
    c: Weight(g32) = 1
    c: Equal(g32,g33)
    c: Equal(g32,g34)
    c: Coincident(g35,g29)
    c: InternalAlignment(g32,g35)
    c: InternalAlignment(g33,g35)
    c: InternalAlignment(g34,g35)
    c: InternalAlignment(g36,g35)
    c: InternalAlignment(g37,g35)
    c: Block(g35)
    c: Coincident(g38,g35)
    c: Vertical(g38)
    c: Block(g38)
    c: Coincident(g42,g38)
    c: Weight(g39) = 1
    c: Equal(g39,g40)
    c: Equal(g39,g41)
    c: Coincident(g42,g25)
    c: InternalAlignment(g39,g42)
    c: InternalAlignment(g40,g42)
    c: InternalAlignment(g41,g42)
    c: InternalAlignment(g43,g42)
    c: InternalAlignment(g44,g42)
    c: Block(g42)
FEATURE [Part::Extrusion] Extrude043  label="bottom010"
  Base = -> Sketch052
  Dir = (0,0,1)
  DirMode = 2
  FaceMakerClass = Part::FaceMakerBullseye
  LengthFwd = 71.4
  LengthRev = 0
  Placement = pos=(0,0,0.3) rot=(0,0,1;0rad)
  Solid = true
  Symmetric = false
FEATURE [Sketcher::SketchObject] Sketch053  label="topSketch013"
  FullyConstrained = true
  sketch-geometry (22):
    g0: LineSegment StartX=5.21097e-06 StartY=3 StartZ=0 EndX=5.21097e-06 EndY=19 EndZ=0
    g1: ArcOfCircle CenterX=19 CenterY=19 CenterZ=0 NormalX=0 NormalY=0 NormalZ=1 AngleXU=0 Radius=19 StartAngle=1.5708 EndAngle=3.14159
    g2: ArcOfCircle CenterX=19 CenterY=19 CenterZ=0 NormalX=0 NormalY=0 NormalZ=1 AngleXU=0 Radius=16 StartAngle=1.5708 EndAngle=3.14159
    g3: LineSegment StartX=114 StartY=35 StartZ=0 EndX=19 EndY=35 EndZ=0
    g4: LineSegment StartX=5.21097e-06 StartY=3 StartZ=0 EndX=5.21097e-06 EndY=0 EndZ=0
    g5: LineSegment StartX=3 StartY=0 StartZ=0 EndX=5.21097e-06 EndY=0 EndZ=0
    g6: LineSegment StartX=3 StartY=19 StartZ=0 EndX=3 EndY=0 EndZ=0
    g7: LineSegment StartX=19 StartY=38 StartZ=0 EndX=124 EndY=38 EndZ=0
    g8: Circle CenterX=119 CenterY=35 CenterZ=0 NormalX=0 NormalY=0 NormalZ=1 AngleXU=0 Radius=1
    g9: Circle CenterX=121 CenterY=35 CenterZ=0 NormalX=0 NormalY=0 NormalZ=1 AngleXU=0 Radius=1
    g10: Circle CenterX=121 CenterY=33 CenterZ=0 NormalX=0 NormalY=0 NormalZ=1 AngleXU=0 Radius=1
    g11: BSplineCurve PolesCount=3 KnotsCount=2 Degree=2 IsPeriodic=0
    g12: GeomPoint X=119 Y=35 Z=0
    g13: GeomPoint X=121 Y=33 Z=0
    g14: LineSegment StartX=119 StartY=35 StartZ=0 EndX=114 EndY=35 EndZ=0
    g15: ArcOfCircle CenterX=105 CenterY=19 CenterZ=0 NormalX=0 NormalY=0 NormalZ=1 AngleXU=0 Radius=16 StartAngle=5.60905 EndAngle=6.28319
    g16: LineSegment StartX=121 StartY=33 StartZ=0 EndX=121 EndY=19 EndZ=0
    g17: LineSegment StartX=117.5 StartY=9.01251 StartZ=0 EndX=121.163 EndY=9.0125 EndZ=0
    g18: ArcOfCircle CenterX=105 CenterY=19 CenterZ=0 NormalX=0 NormalY=0 NormalZ=1 AngleXU=0 Radius=20.6155 StartAngle=5.7297 EndAngle=6.28319
    g19: LineSegment StartX=121.163 StartY=9.0125 StartZ=0 EndX=122.538 EndY=8.16329 EndZ=0
    g20: LineSegment StartX=124 StartY=38 StartZ=0 EndX=125.616 EndY=38 EndZ=0
    g21: LineSegment StartX=125.616 StartY=19 StartZ=0 EndX=125.616 EndY=38 EndZ=0
  constraints (50):
    c: Vertical(g0)
    c: Block(g0)
    c: Coincident(g1,g0)
    c: Block(g1)
    c: Coincident(g2,g1)
    c: Block(g2)
    c: Coincident(g3,g2)
    c: Horizontal(g3)
    c: Tangent(g3,g2)
    c: Coincident(g4,g0)
    c: Distance(g4) = 3
    c: Vertical(g4)
    c: Coincident(g5,g4)
    c: Horizontal(g5)
    c: Coincident(g6,g2)
    c: Coincident(g6,g5)
    c: Vertical(g6)
    c: Horizontal(g7)
    c: Distance(g7) = 105
    c: Coincident(g7,g1)
    c: Block(g3)
    c: Weight(g8) = 1
    c: Equal(g8,g9)
    c: Equal(g8,g10)
    c: InternalAlignment(g8,g11)
    c: InternalAlignment(g9,g11)
    c: InternalAlignment(g10,g11)
    c: InternalAlignment(g12,g11)
    c: InternalAlignment(g13,g11)
    c: Block(g11)
    c: Coincident(g14,g11)
    c: Coincident(g14,g3)
    c: Horizontal(g14)
    c: Block(g15)
    c: Coincident(g16,g11)
    c: Coincident(g16,g15)
    c: Vertical(g16)
    c: Distance(g16) = 14
    c: Coincident(g17,g15)
    c: Block(g18)
    c: Coincident(g19,g18)
    c: Coincident(g20,g7)
    c: Horizontal(g20)
    c: Vertical(g21)
    c: Coincident(g20,g21)
    c: Block(g20)
    c: Block(g21)
    c: Block(g19)
    c: Block(g17)
    c: Distance(g20) = 1.61553
FEATURE [Part::Extrusion] Extrude044
  Base = -> Sketch053
  Dir = (0,0,1)
  DirMode = 2
  FaceMakerClass = Part::FaceMakerBullseye
  LengthFwd = 72
  LengthRev = 0
  Solid = true
  Symmetric = false
FEATURE [Part::Fillet] Fillet036  label="top018"
  Base = -> Extrude044
  Edges = 1 edges r=2: [Edge41]
FEATURE [Sketcher::SketchObject] Sketch054
  FullyConstrained = false
  Placement = pos=(0,0,0) rot=(1,0,0;1.5708rad)
  sketch-geometry (24):
    g0: ArcOfCircle CenterX=-4 CenterY=-10.5 CenterZ=0 NormalX=0 NormalY=0 NormalZ=1 AngleXU=0 Radius=1.5 StartAngle=6e-16 EndAngle=3.14159
    g1: ArcOfCircle CenterX=-34.2 CenterY=-10.5 CenterZ=0 NormalX=0 NormalY=0 NormalZ=1 AngleXU=0 Radius=1.5 StartAngle=0 EndAngle=3.14159
    g2: ArcOfCircle CenterX=-34.2 CenterY=-27.7 CenterZ=0 NormalX=0 NormalY=0 NormalZ=1 AngleXU=0 Radius=1.5 StartAngle=3.14159 EndAngle=6.28319
    g3: ArcOfCircle CenterX=-4 CenterY=-27.7 CenterZ=0 NormalX=0 NormalY=0 NormalZ=1 AngleXU=0 Radius=1.5 StartAngle=3.1416 EndAngle=6.28319
    g4: ArcOfCircle CenterX=-10 CenterY=-4.3 CenterZ=0 NormalX=0 NormalY=0 NormalZ=1 AngleXU=0 Radius=1.5 StartAngle=2e-16 EndAngle=3.14159
    g5: ArcOfCircle CenterX=-16.1 CenterY=-1.8 CenterZ=0 NormalX=0 NormalY=0 NormalZ=1 AngleXU=0 Radius=1.5 StartAngle=5e-16 EndAngle=3.14159
    g6: ArcOfCircle CenterX=-22.1 CenterY=-1.8 CenterZ=0 NormalX=0 NormalY=0 NormalZ=1 AngleXU=0 Radius=1.5 StartAngle=5e-16 EndAngle=3.14159
    g7: ArcOfCircle CenterX=-28.2 CenterY=-4.3 CenterZ=0 NormalX=0 NormalY=0 NormalZ=1 AngleXU=0 Radius=1.5 StartAngle=2e-16 EndAngle=3.14159
    g8: ArcOfCircle CenterX=-10 CenterY=-33.9 CenterZ=0 NormalX=0 NormalY=0 NormalZ=1 AngleXU=0 Radius=1.5 StartAngle=3.14159 EndAngle=6.28319
    g9: ArcOfCircle CenterX=-16.1 CenterY=-36.4 CenterZ=0 NormalX=0 NormalY=0 NormalZ=1 AngleXU=0 Radius=1.5 StartAngle=3.14159 EndAngle=6.28319
    g10: ArcOfCircle CenterX=-22.1 CenterY=-36.4 CenterZ=0 NormalX=0 NormalY=0 NormalZ=1 AngleXU=0 Radius=1.5 StartAngle=3.14159 EndAngle=6.28319
    g11: ArcOfCircle CenterX=-28.2 CenterY=-33.9 CenterZ=0 NormalX=0 NormalY=0 NormalZ=1 AngleXU=0 Radius=1.5 StartAngle=3.14159 EndAngle=6.28319
    g12: LineSegment StartX=-35.7 StartY=-10.5 StartZ=0 EndX=-35.7 EndY=-27.7 EndZ=0
    g13: LineSegment StartX=-32.7 StartY=-10.5 StartZ=0 EndX=-32.7 EndY=-27.7 EndZ=0
    g14: LineSegment StartX=-29.7 StartY=-33.9 StartZ=0 EndX=-29.7 EndY=-4.3 EndZ=0
    g15: LineSegment StartX=-26.7 StartY=-33.9 StartZ=0 EndX=-26.7 EndY=-4.3 EndZ=0
    g16: LineSegment StartX=-2.5 StartY=-10.5 StartZ=0 EndX=-2.5 EndY=-27.7 EndZ=0
    g17: LineSegment StartX=-8.5 StartY=-4.3 StartZ=0 EndX=-8.5 EndY=-33.9 EndZ=0
    g18: LineSegment StartX=-5.5 StartY=-10.5 StartZ=0 EndX=-5.5 EndY=-27.7 EndZ=0
    g19: LineSegment StartX=-11.5 StartY=-4.3 StartZ=0 EndX=-11.5 EndY=-33.9 EndZ=0
    g20: LineSegment StartX=-14.6 StartY=-1.8 StartZ=0 EndX=-14.6 EndY=-36.4 EndZ=0
    g21: LineSegment StartX=-17.6 StartY=-1.8 StartZ=0 EndX=-17.6 EndY=-36.4 EndZ=0
    g22: LineSegment StartX=-20.6 StartY=-36.4 StartZ=0 EndX=-20.6 EndY=-1.8 EndZ=0
    g23: LineSegment StartX=-23.6 StartY=-1.8 StartZ=0 EndX=-23.6 EndY=-36.4 EndZ=0
  constraints (48):
    c: Block(g0)
    c: Block(g1)
    c: Block(g2)
    c: Block(g3)
    c: Block(g4)
    c: Block(g5)
    c: Block(g6)
    c: Block(g7)
    c: Block(g8)
    c: Block(g9)
    c: Block(g10)
    c: Block(g11)
    c: Coincident(g12,g1)
    c: Coincident(g12,g2)
    c: Vertical(g12)
    c: Coincident(g13,g1)
    c: Coincident(g13,g2)
    c: Vertical(g13)
    c: Coincident(g14,g11)
    c: Coincident(g14,g7)
    c: Vertical(g14)
    c: Coincident(g15,g11)
    c: Coincident(g15,g7)
    c: Vertical(g15)
    c: Coincident(g16,g0)
    c: Coincident(g16,g3)
    c: Vertical(g16)
    c: Coincident(g17,g4)
    c: Coincident(g17,g8)
    c: Vertical(g17)
    c: Coincident(g18,g0)
    c: Coincident(g18,g3)
    c: Vertical(g18)
    c: Coincident(g19,g4)
    c: Coincident(g19,g8)
    c: Vertical(g19)
    c: Coincident(g20,g5)
    c: Coincident(g20,g9)
    c: Vertical(g20)
    c: Coincident(g21,g5)
    c: Coincident(g21,g9)
    c: Vertical(g21)
    c: Coincident(g22,g10)
    c: Coincident(g22,g6)
    c: Vertical(g22)
    c: Coincident(g23,g6)
    c: Coincident(g23,g10)
    c: Vertical(g23)
FEATURE [Part::Extrusion] Extrude045  label="removeToCreateFanGrillHoles003"
  Base = -> Sketch054
  Dir = (0,-1,6e-16)
  DirMode = 2
  FaceMakerClass = Part::FaceMakerBullseye
  LengthFwd = 10
  LengthRev = 0
  Placement = pos=(65.4,44,54.82) rot=(0,0,1;0rad)
  Solid = true
  Symmetric = false
FEATURE [Part::Feature] Face105 .. Face108  x4 (patterned run collapsed; names and placements below)
  shape: bbox 3.5 x 17.8 x 2e-07 mm, 1 faces, 0 solids (baked)
FEATURE [Part::Revolution] Revolve113  label="removeToCreateScrewAndThreadedInsertHole041"
  Angle = 360
  Axis = (0,1,0)
  Base = (0,0,0)
  FaceMakerClass = Part::FaceMakerBullseye
  Placement = pos=(62.3,30.3,19.7) rot=(0,0,1;0rad)
  Solid = false
  Source = -> Face105
  Symmetric = false
FEATURE [Part::Revolution] Revolve114  label="removeToCreateScrewAndThreadedInsertHole042"
  Angle = 360
  Axis = (0,1,0)
  Base = (0,0,0)
  FaceMakerClass = Part::FaceMakerBullseye
  Placement = pos=(62.3,30.3,51.7) rot=(0,0,1;0rad)
  Solid = false
  Source = -> Face106
  Symmetric = false
FEATURE [Part::Revolution] Revolve115  label="removeToCreateScrewAndThreadedInsertHole043"
  Angle = 360
  Axis = (0,1,0)
  Base = (0,0,0)
  FaceMakerClass = Part::FaceMakerBullseye
  Placement = pos=(30.3,30.3,19.7) rot=(0,0,1;0rad)
  Solid = false
  Source = -> Face107
  Symmetric = false
FEATURE [Part::Revolution] Revolve116  label="removeToCreateScrewAndThreadedInsertHole044"
  Angle = 360
  Axis = (0,1,0)
  Base = (0,0,0)
  FaceMakerClass = Part::FaceMakerBullseye
  Placement = pos=(30.3,30.3,51.7) rot=(0,0,1;0rad)
  Solid = false
  Source = -> Face108
  Symmetric = false
FEATURE [Part::MultiFuse] Fusion083  label="createThreadedInsertHolesForFan004"
  Shapes = -> [Revolve113,Revolve114,Revolve115,Revolve116]
FEATURE [Part::Box] Box024  label="removeToCreteHoleForPlugHousing026"
  AttacherType = Attacher::AttachEngine3D
  Height = 28.6
  Length = 10
  Placement = pos=(-2,0,21.7) rot=(0,0,1;0rad)
  Width = 19
FEATURE [Part::Cylinder] Cylinder038  label="removeToCreteHoleForPlugHousing027"
  Angle = 360
  AttacherType = Attacher::AttachEngine3D
  Height = 20
  Placement = pos=(-2,19,36) rot=(0,1,0;1.5708rad)
  Radius = 14.3
FEATURE [Part::MultiFuse] Fusion084  label="removeToCreteHoleForPlugHousing028"
  Shapes = -> [Box024,Cylinder038]
FEATURE [Part::Cylinder] Cylinder039
  Angle = 360
  AttacherType = Attacher::AttachEngine3D
  Height = 20
  Placement = pos=(0,0,36.15) rot=(0,0,1;0rad)
  Radius = 14.3
FEATURE [Part::Cylinder] Cylinder040
  Angle = 360
  AttacherType = Attacher::AttachEngine3D
  Height = 10
  Placement = pos=(0,0,36.15) rot=(0,0,1;0rad)
  Radius = 4
FEATURE [Part::Box] Box025  label="removeToCreteHoleForPlugHousing030"
  AttacherType = Attacher::AttachEngine3D
  Height = 28.6
  Length = 20
  Placement = pos=(106.15,0,21.7) rot=(0,0,1;0rad)
  Width = 19
FEATURE [Part::MultiFuse] Fusion086  label="removeToCreteHoleForPlugHousing031"
  Placement = pos=(70,19,36) rot=(0,1,0;1.5708rad)
  Shapes = -> [Cylinder039,Cylinder040]
FEATURE [Part::MultiFuse] Fusion085  label="removeToCreteHoleForPlugHousing029"
  Shapes = -> [Box025,Fusion086]
FEATURE [Sketcher::SketchObject] Sketch055
  FullyConstrained = true
  Placement = pos=(117,19,0) rot=(0.57735,0.57735,0.57735;2.0944rad)
  sketch-geometry (48):
    g0: LineSegment StartX=-49.19 StartY=69.25 StartZ=0 EndX=-49.19 EndY=66.25 EndZ=0
    g1: LineSegment StartX=-49.19 StartY=63.5 StartZ=0 EndX=-49.19 EndY=60.5 EndZ=0
    g2: LineSegment StartX=-49.19 StartY=57.75 StartZ=0 EndX=-49.19 EndY=54.75 EndZ=0
    g3: LineSegment StartX=-49.19 StartY=52 StartZ=0 EndX=-49.19 EndY=49 EndZ=0
    g4: LineSegment StartX=-49.19 StartY=46.25 StartZ=0 EndX=-49.19 EndY=43.25 EndZ=0
    g5: LineSegment StartX=-49.19 StartY=40.5 StartZ=0 EndX=-49.19 EndY=37.5 EndZ=0
    g6: LineSegment StartX=-49.19 StartY=34.5 StartZ=0 EndX=-49.19 EndY=31.5 EndZ=0
    g7: LineSegment StartX=-49.19 StartY=28.75 StartZ=0 EndX=-49.19 EndY=25.75 EndZ=0
    g8: LineSegment StartX=-49.19 StartY=23 StartZ=0 EndX=-49.19 EndY=20 EndZ=0
    g9: LineSegment StartX=-49.19 StartY=17.25 StartZ=0 EndX=-49.19 EndY=14.25 EndZ=0
    g10: LineSegment StartX=-49.19 StartY=11.5 StartZ=0 EndX=-49.19 EndY=8.5 EndZ=0
    g11: LineSegment StartX=-49.19 StartY=5.75 StartZ=0 EndX=-49.19 EndY=2.75 EndZ=0
    g12: ArcOfCircle CenterX=-1.5 CenterY=67.75 CenterZ=0 NormalX=0 NormalY=0 NormalZ=1 AngleXU=0 Radius=1.5 StartAngle=4.71239 EndAngle=7.85398
    g13: ArcOfCircle CenterX=-1.5 CenterY=62 CenterZ=0 NormalX=0 NormalY=0 NormalZ=1 AngleXU=0 Radius=1.5 StartAngle=4.71239 EndAngle=7.85398
    g14: ArcOfCircle CenterX=-1.5 CenterY=56.25 CenterZ=0 NormalX=0 NormalY=0 NormalZ=1 AngleXU=0 Radius=1.5 StartAngle=4.71239 EndAngle=7.85398
    g15: ArcOfCircle CenterX=-11.49 CenterY=50.5 CenterZ=0 NormalX=0 NormalY=0 NormalZ=1 AngleXU=0 Radius=1.5 StartAngle=4.71239 EndAngle=7.85398
    g16: ArcOfCircle CenterX=-16.28 CenterY=44.75 CenterZ=0 NormalX=0 NormalY=0 NormalZ=1 AngleXU=0 Radius=1.5 StartAngle=4.71239 EndAngle=7.85398
    g17: ArcOfCircle CenterX=-18.2337 CenterY=39 CenterZ=0 NormalX=0 NormalY=0 NormalZ=1 AngleXU=0 Radius=1.5 StartAngle=4.71485 EndAngle=7.85398
    g18: ArcOfCircle CenterX=-16.2837 CenterY=27.25 CenterZ=0 NormalX=0 NormalY=0 NormalZ=1 AngleXU=0 Radius=1.5 StartAngle=4.71485 EndAngle=7.85398
    g19: ArcOfCircle CenterX=-18.2337 CenterY=33 CenterZ=0 NormalX=0 NormalY=0 NormalZ=1 AngleXU=0 Radius=1.5 StartAngle=4.71485 EndAngle=7.85398
    g20: ArcOfCircle CenterX=-11.49 CenterY=21.5 CenterZ=0 NormalX=0 NormalY=0 NormalZ=1 AngleXU=0 Radius=1.5 StartAngle=4.71239 EndAngle=7.85398
    g21: ArcOfCircle CenterX=-1.5 CenterY=4.25 CenterZ=0 NormalX=0 NormalY=0 NormalZ=1 AngleXU=0 Radius=1.5 StartAngle=4.71239 EndAngle=7.85398
    g22: ArcOfCircle CenterX=-1.5 CenterY=10 CenterZ=0 NormalX=0 NormalY=0 NormalZ=1 AngleXU=0 Radius=1.5 StartAngle=4.71239 EndAngle=7.85398
    g23: ArcOfCircle CenterX=-1.5 CenterY=15.75 CenterZ=0 NormalX=0 NormalY=0 NormalZ=1 AngleXU=0 Radius=1.5 StartAngle=4.71239 EndAngle=7.85398
    g24: LineSegment StartX=-49.19 StartY=69.25 StartZ=0 EndX=-1.5 EndY=69.25 EndZ=0
    g25: LineSegment StartX=-49.19 StartY=66.25 StartZ=0 EndX=-1.5 EndY=66.25 EndZ=0
    g26: LineSegment StartX=-49.19 StartY=63.5 StartZ=0 EndX=-1.5 EndY=63.5 EndZ=0
    g27: LineSegment StartX=-49.19 StartY=60.5 StartZ=0 EndX=-1.5 EndY=60.5 EndZ=0
    g28: LineSegment StartX=-49.19 StartY=57.75 StartZ=0 EndX=-1.5 EndY=57.75 EndZ=0
    g29: LineSegment StartX=-49.19 StartY=54.75 StartZ=0 EndX=-1.5 EndY=54.75 EndZ=0
    g30: LineSegment StartX=-49.19 StartY=52 StartZ=0 EndX=-11.49 EndY=52 EndZ=0
    g31: LineSegment StartX=-49.19 StartY=49 StartZ=0 EndX=-11.49 EndY=49 EndZ=0
    g32: LineSegment StartX=-49.19 StartY=46.25 StartZ=0 EndX=-16.28 EndY=46.25 EndZ=0
    g33: LineSegment StartX=-49.19 StartY=43.25 StartZ=0 EndX=-16.28 EndY=43.25 EndZ=0
    g34: LineSegment StartX=-49.19 StartY=40.5 StartZ=0 EndX=-18.2337 EndY=40.5 EndZ=0
    g35: LineSegment StartX=-49.19 StartY=37.5 StartZ=0 EndX=-18.23 EndY=37.5 EndZ=0
    g36: LineSegment StartX=-49.19 StartY=34.5 StartZ=0 EndX=-18.2337 EndY=34.5 EndZ=0
    g37: LineSegment StartX=-49.19 StartY=31.5 StartZ=0 EndX=-18.23 EndY=31.5 EndZ=0
    g38: LineSegment StartX=-49.19 StartY=28.75 StartZ=0 EndX=-16.2837 EndY=28.75 EndZ=0
    g39: LineSegment StartX=-49.19 StartY=25.75 StartZ=0 EndX=-16.28 EndY=25.75 EndZ=0
    g40: LineSegment StartX=-49.19 StartY=23 StartZ=0 EndX=-11.49 EndY=23 EndZ=0
    g41: LineSegment StartX=-49.19 StartY=20 StartZ=0 EndX=-11.49 EndY=20 EndZ=0
    g42: LineSegment StartX=-49.19 StartY=17.25 StartZ=0 EndX=-1.5 EndY=17.25 EndZ=0
    g43: LineSegment StartX=-49.19 StartY=14.25 StartZ=0 EndX=-1.5 EndY=14.25 EndZ=0
    g44: LineSegment StartX=-49.19 StartY=11.5 StartZ=0 EndX=-1.5 EndY=11.5 EndZ=0
    g45: LineSegment StartX=-49.19 StartY=8.5 StartZ=0 EndX=-1.5 EndY=8.5 EndZ=0
    g46: LineSegment StartX=-49.19 StartY=5.75 StartZ=0 EndX=-1.5 EndY=5.75 EndZ=0
    g47: LineSegment StartX=-49.19 StartY=2.75 StartZ=0 EndX=-1.5 EndY=2.75 EndZ=0
  constraints (120):
    c: Vertical(g0)
    c: Distance(g0) = 3
    c: Block(g0)
    c: Vertical(g1)
    c: Distance(g1) = 3
    c: Vertical(g2)
    c: Equal(g0,g2) = 3
    c: Block(g2)
    c: Vertical(g3)
    c: Equal(g1,g3) = 3
    c: Vertical(g4)
    c: Equal(g0,g4) = 3
    c: Block(g4)
    c: Vertical(g5)
    c: Equal(g1,g5) = 3
    c: Vertical(g6)
    c: Equal(g0,g6) = 3
    c: Block(g6)
    c: Vertical(g7)
    c: Equal(g1,g7) = 3
    c: Vertical(g8)
    c: Equal(g0,g8) = 3
    c: Block(g8)
    c: Vertical(g9)
    c: Equal(g1,g9) = 3
    c: Vertical(g10)
    c: Equal(g0,g10) = 3
    c: Block(g10)
    c: Vertical(g11)
    c: Equal(g1,g11) = 3
    c: Block(g12)
    c: Block(g13)
    c: Block(g14)
    c: Block(g15)
    c: Block(g16)
    c: Block(g17)
    c: Block(g18)
    c: Block(g19)
    c: Block(g20)
    c: Block(g21)
    c: Block(g22)
    c: Block(g23)
    c: Block(g11)
    c: Block(g9)
    c: Block(g7)
    c: Block(g5)
    c: Block(g3)
    c: Block(g1)
    c: Coincident(g24,g0)
    c: Coincident(g24,g12)
    c: Horizontal(g24)
    c: Coincident(g25,g0)
    c: Coincident(g25,g12)
    c: Horizontal(g25)
    c: Coincident(g26,g1)
    c: Coincident(g26,g13)
    c: Horizontal(g26)
    c: Coincident(g27,g1)
    c: Coincident(g27,g13)
    c: Horizontal(g27)
    c: Coincident(g28,g2)
    c: Coincident(g28,g14)
    c: Horizontal(g28)
    c: Coincident(g29,g2)
    c: Coincident(g29,g14)
    c: Horizontal(g29)
    c: Coincident(g30,g3)
    c: Coincident(g30,g15)
    c: Horizontal(g30)
    c: Coincident(g31,g3)
    c: Coincident(g31,g15)
    c: Horizontal(g31)
    c: Coincident(g32,g4)
    c: Coincident(g32,g16)
    c: Horizontal(g32)
    c: Coincident(g33,g4)
    c: Coincident(g33,g16)
    c: Horizontal(g33)
    c: Coincident(g34,g5)
    c: Coincident(g34,g17)
    c: Horizontal(g34)
    c: Coincident(g35,g5)
    c: Coincident(g35,g17)
    c: Horizontal(g35)
    c: Coincident(g36,g6)
    c: Coincident(g36,g19)
    c: Horizontal(g36)
    c: Coincident(g37,g6)
    c: Coincident(g37,g19)
    c: Horizontal(g37)
    c: Coincident(g38,g7)
    c: Coincident(g38,g18)
    c: Horizontal(g38)
    c: Coincident(g39,g7)
    c: Coincident(g39,g18)
    c: Horizontal(g39)
    c: Coincident(g40,g8)
    c: Coincident(g40,g20)
    c: Horizontal(g40)
    c: Coincident(g41,g8)
    c: Coincident(g41,g20)
    c: Horizontal(g41)
    c: Coincident(g42,g9)
    c: Coincident(g42,g23)
    c: Horizontal(g42)
    c: Coincident(g43,g9)
    c: Coincident(g43,g23)
    c: Horizontal(g43)
    c: Coincident(g44,g10)
    c: Coincident(g44,g22)
    c: Horizontal(g44)
    c: Coincident(g45,g10)
    c: Coincident(g45,g22)
    c: Horizontal(g45)
    c: Coincident(g46,g11)
    c: Coincident(g46,g21)
    c: Horizontal(g46)
    c: Coincident(g47,g11)
    c: Coincident(g47,g21)
    c: Horizontal(g47)
FEATURE [Part::Extrusion] Extrude046
  Base = -> Sketch055
  Dir = (1,0,0)
  DirMode = 2
  FaceMakerClass = Part::FaceMakerBullseye
  LengthFwd = 23
  LengthRev = 0
  Placement = pos=(-19,0,0) rot=(0,0,1;0rad)
  Solid = true
  Symmetric = false
FEATURE [Part::Fillet] Fillet038  label="removeToCreateVentalationHoles001"
  Base = -> Extrude046
  Edges = <same value as first occurrence — deduplicated (x6 in doc)>
  Placement = pos=(7,0,0) rot=(0,0,1;0rad)
FEATURE [Sketcher::SketchObject] Sketch056  label="topSketch014"
  FullyConstrained = true
  sketch-geometry (22):
    g0: LineSegment StartX=5.21097e-06 StartY=3 StartZ=0 EndX=5.21097e-06 EndY=19 EndZ=0
    g1: ArcOfCircle CenterX=19 CenterY=19 CenterZ=0 NormalX=0 NormalY=0 NormalZ=1 AngleXU=0 Radius=19 StartAngle=1.5708 EndAngle=3.14159
    g2: ArcOfCircle CenterX=19 CenterY=19 CenterZ=0 NormalX=0 NormalY=0 NormalZ=1 AngleXU=0 Radius=16 StartAngle=1.5708 EndAngle=3.14159
    g3: LineSegment StartX=114 StartY=35 StartZ=0 EndX=19 EndY=35 EndZ=0
    g4: LineSegment StartX=5.21097e-06 StartY=3 StartZ=0 EndX=5.21097e-06 EndY=0 EndZ=0
    g5: LineSegment StartX=3 StartY=0 StartZ=0 EndX=5.21097e-06 EndY=0 EndZ=0
    g6: LineSegment StartX=3 StartY=19 StartZ=0 EndX=3 EndY=0 EndZ=0
    g7: LineSegment StartX=19 StartY=38 StartZ=0 EndX=124 EndY=38 EndZ=0
    g8: Circle CenterX=119 CenterY=35 CenterZ=0 NormalX=0 NormalY=0 NormalZ=1 AngleXU=0 Radius=1
    g9: Circle CenterX=121 CenterY=35 CenterZ=0 NormalX=0 NormalY=0 NormalZ=1 AngleXU=0 Radius=1
    g10: Circle CenterX=121 CenterY=33 CenterZ=0 NormalX=0 NormalY=0 NormalZ=1 AngleXU=0 Radius=1
    g11: BSplineCurve PolesCount=3 KnotsCount=2 Degree=2 IsPeriodic=0
    g12: GeomPoint X=119 Y=35 Z=0
    g13: GeomPoint X=121 Y=33 Z=0
    g14: LineSegment StartX=119 StartY=35 StartZ=0 EndX=114 EndY=35 EndZ=0
    g15: ArcOfCircle CenterX=105 CenterY=19 CenterZ=0 NormalX=0 NormalY=0 NormalZ=1 AngleXU=0 Radius=16 StartAngle=5.60905 EndAngle=6.28319
    g16: LineSegment StartX=121 StartY=33 StartZ=0 EndX=121 EndY=19 EndZ=0
    g17: LineSegment StartX=117.5 StartY=9.01251 StartZ=0 EndX=121.163 EndY=9.0125 EndZ=0
    g18: ArcOfCircle CenterX=105 CenterY=19 CenterZ=0 NormalX=0 NormalY=0 NormalZ=1 AngleXU=0 Radius=20.6155 StartAngle=5.7297 EndAngle=6.28319
    g19: LineSegment StartX=121.163 StartY=9.0125 StartZ=0 EndX=122.538 EndY=8.16329 EndZ=0
    g20: LineSegment StartX=124 StartY=38 StartZ=0 EndX=125.616 EndY=38 EndZ=0
    g21: LineSegment StartX=125.616 StartY=19 StartZ=0 EndX=125.616 EndY=38 EndZ=0
  constraints (49):
    c: Vertical(g0)
    c: Block(g0)
    c: Coincident(g1,g0)
    c: Block(g1)
    c: Coincident(g2,g1)
    c: Block(g2)
    c: Coincident(g3,g2)
    c: Horizontal(g3)
    c: Tangent(g3,g2)
    c: Coincident(g4,g0)
    c: Distance(g4) = 3
    c: Vertical(g4)
    c: Coincident(g5,g4)
    c: Horizontal(g5)
    c: Coincident(g6,g2)
    c: Coincident(g6,g5)
    c: Vertical(g6)
    c: Horizontal(g7)
    c: Distance(g7) = 105
    c: Coincident(g7,g1)
    c: Block(g3)
    c: Weight(g8) = 1
    c: Equal(g8,g9)
    c: Equal(g8,g10)
    c: InternalAlignment(g8,g11)
    c: InternalAlignment(g9,g11)
    c: InternalAlignment(g10,g11)
    c: InternalAlignment(g12,g11)
    c: InternalAlignment(g13,g11)
    c: Block(g11)
    c: Coincident(g14,g11)
    c: Coincident(g14,g3)
    c: Horizontal(g14)
    c: Block(g15)
    c: Coincident(g16,g11)
    c: Coincident(g16,g15)
    c: Vertical(g16)
    c: Distance(g16) = 14
    c: Coincident(g17,g15)
    c: Block(g18)
    c: Coincident(g19,g18)
    c: Coincident(g20,g7)
    c: Horizontal(g20)
    c: Vertical(g21)
    c: Coincident(g20,g21)
    c: Block(g20)
    c: Block(g21)
    c: Block(g19)
    c: Block(g17)
FEATURE [Part::Box] Box026  label="removeToCreteHoleForPlugHousing032"
  AttacherType = Attacher::AttachEngine3D
  Height = 28.6
  Length = 10
  Placement = pos=(-2,0,21.7) rot=(0,0,1;0rad)
  Width = 19
FEATURE [Part::Feature] Face109 .. Face112  x4 (patterned run collapsed; names and placements below)
  shape: bbox 3.5 x 17.8 x 2e-07 mm, 1 faces, 0 solids (baked)
FEATURE [Part::Revolution] Revolve117  label="removeToCreateScrewAndThreadedInsertHole045"
  Angle = 360
  Axis = (0,1,0)
  Base = (0,0,0)
  FaceMakerClass = Part::FaceMakerBullseye
  Placement = pos=(62.3,30.3,19.7) rot=(0,0,1;0rad)
  Solid = false
  Source = -> Face109
  Symmetric = false
FEATURE [Part::Revolution] Revolve118  label="removeToCreateScrewAndThreadedInsertHole046"
  Angle = 360
  Axis = (0,1,0)
  Base = (0,0,0)
  FaceMakerClass = Part::FaceMakerBullseye
  Placement = pos=(62.3,30.3,51.7) rot=(0,0,1;0rad)
  Solid = false
  Source = -> Face110
  Symmetric = false
FEATURE [Part::Revolution] Revolve119  label="removeToCreateScrewAndThreadedInsertHole047"
  Angle = 360
  Axis = (0,1,0)
  Base = (0,0,0)
  FaceMakerClass = Part::FaceMakerBullseye
  Placement = pos=(30.3,30.3,19.7) rot=(0,0,1;0rad)
  Solid = false
  Source = -> Face111
  Symmetric = false
FEATURE [Part::Revolution] Revolve120  label="removeToCreateScrewAndThreadedInsertHole048"
  Angle = 360
  Axis = (0,1,0)
  Base = (0,0,0)
  FaceMakerClass = Part::FaceMakerBullseye
  Placement = pos=(30.3,30.3,51.7) rot=(0,0,1;0rad)
  Solid = false
  Source = -> Face112
  Symmetric = false
FEATURE [Part::MultiFuse] Fusion087  label="createThreadedInsertHolesForFan005"
  Shapes = -> [Revolve117,Revolve118,Revolve119,Revolve120]
FEATURE [Part::Extrusion] Extrude047
  Base = -> Sketch056
  Dir = (0,0,1)
  DirMode = 2
  FaceMakerClass = Part::FaceMakerBullseye
  LengthFwd = 72
  LengthRev = 0
  Solid = true
  Symmetric = false
FEATURE [Part::Fillet] Fillet039  label="top019"
  Base = -> Extrude047
  Edges = 1 edges r=2: [Edge35]
FEATURE [Sketcher::SketchObject] Sketch057
  FullyConstrained = false
  Placement = pos=(0,0,0) rot=(1,0,0;1.5708rad)
  sketch-geometry (24):
    g0: ArcOfCircle CenterX=-4 CenterY=-10.5 CenterZ=0 NormalX=0 NormalY=0 NormalZ=1 AngleXU=0 Radius=1.5 StartAngle=6e-16 EndAngle=3.14159
    g1: ArcOfCircle CenterX=-34.2 CenterY=-10.5 CenterZ=0 NormalX=0 NormalY=0 NormalZ=1 AngleXU=0 Radius=1.5 StartAngle=0 EndAngle=3.14159
    g2: ArcOfCircle CenterX=-34.2 CenterY=-27.7 CenterZ=0 NormalX=0 NormalY=0 NormalZ=1 AngleXU=0 Radius=1.5 StartAngle=3.14159 EndAngle=6.28319
    g3: ArcOfCircle CenterX=-4 CenterY=-27.7 CenterZ=0 NormalX=0 NormalY=0 NormalZ=1 AngleXU=0 Radius=1.5 StartAngle=3.1416 EndAngle=6.28319
    g4: ArcOfCircle CenterX=-10 CenterY=-4.3 CenterZ=0 NormalX=0 NormalY=0 NormalZ=1 AngleXU=0 Radius=1.5 StartAngle=2e-16 EndAngle=3.14159
    g5: ArcOfCircle CenterX=-16.1 CenterY=-1.8 CenterZ=0 NormalX=0 NormalY=0 NormalZ=1 AngleXU=0 Radius=1.5 StartAngle=5e-16 EndAngle=3.14159
    g6: ArcOfCircle CenterX=-22.1 CenterY=-1.8 CenterZ=0 NormalX=0 NormalY=0 NormalZ=1 AngleXU=0 Radius=1.5 StartAngle=5e-16 EndAngle=3.14159
    g7: ArcOfCircle CenterX=-28.2 CenterY=-4.3 CenterZ=0 NormalX=0 NormalY=0 NormalZ=1 AngleXU=0 Radius=1.5 StartAngle=2e-16 EndAngle=3.14159
    g8: ArcOfCircle CenterX=-10 CenterY=-33.9 CenterZ=0 NormalX=0 NormalY=0 NormalZ=1 AngleXU=0 Radius=1.5 StartAngle=3.14159 EndAngle=6.28319
    g9: ArcOfCircle CenterX=-16.1 CenterY=-36.4 CenterZ=0 NormalX=0 NormalY=0 NormalZ=1 AngleXU=0 Radius=1.5 StartAngle=3.14159 EndAngle=6.28319
    g10: ArcOfCircle CenterX=-22.1 CenterY=-36.4 CenterZ=0 NormalX=0 NormalY=0 NormalZ=1 AngleXU=0 Radius=1.5 StartAngle=3.14159 EndAngle=6.28319
    g11: ArcOfCircle CenterX=-28.2 CenterY=-33.9 CenterZ=0 NormalX=0 NormalY=0 NormalZ=1 AngleXU=0 Radius=1.5 StartAngle=3.14159 EndAngle=6.28319
    g12: LineSegment StartX=-35.7 StartY=-10.5 StartZ=0 EndX=-35.7 EndY=-27.7 EndZ=0
    g13: LineSegment StartX=-32.7 StartY=-10.5 StartZ=0 EndX=-32.7 EndY=-27.7 EndZ=0
    g14: LineSegment StartX=-29.7 StartY=-33.9 StartZ=0 EndX=-29.7 EndY=-4.3 EndZ=0
    g15: LineSegment StartX=-26.7 StartY=-33.9 StartZ=0 EndX=-26.7 EndY=-4.3 EndZ=0
    g16: LineSegment StartX=-2.5 StartY=-10.5 StartZ=0 EndX=-2.5 EndY=-27.7 EndZ=0
    g17: LineSegment StartX=-8.5 StartY=-4.3 StartZ=0 EndX=-8.5 EndY=-33.9 EndZ=0
    g18: LineSegment StartX=-5.5 StartY=-10.5 StartZ=0 EndX=-5.5 EndY=-27.7 EndZ=0
    g19: LineSegment StartX=-11.5 StartY=-4.3 StartZ=0 EndX=-11.5 EndY=-33.9 EndZ=0
    g20: LineSegment StartX=-14.6 StartY=-1.8 StartZ=0 EndX=-14.6 EndY=-36.4 EndZ=0
    g21: LineSegment StartX=-17.6 StartY=-1.8 StartZ=0 EndX=-17.6 EndY=-36.4 EndZ=0
    g22: LineSegment StartX=-20.6 StartY=-36.4 StartZ=0 EndX=-20.6 EndY=-1.8 EndZ=0
    g23: LineSegment StartX=-23.6 StartY=-1.8 StartZ=0 EndX=-23.6 EndY=-36.4 EndZ=0
  constraints (48):
    c: Block(g0)
    c: Block(g1)
    c: Block(g2)
    c: Block(g3)
    c: Block(g4)
    c: Block(g5)
    c: Block(g6)
    c: Block(g7)
    c: Block(g8)
    c: Block(g9)
    c: Block(g10)
    c: Block(g11)
    c: Coincident(g12,g1)
    c: Coincident(g12,g2)
    c: Vertical(g12)
    c: Coincident(g13,g1)
    c: Coincident(g13,g2)
    c: Vertical(g13)
    c: Coincident(g14,g11)
    c: Coincident(g14,g7)
    c: Vertical(g14)
    c: Coincident(g15,g11)
    c: Coincident(g15,g7)
    c: Vertical(g15)
    c: Coincident(g16,g0)
    c: Coincident(g16,g3)
    c: Vertical(g16)
    c: Coincident(g17,g4)
    c: Coincident(g17,g8)
    c: Vertical(g17)
    c: Coincident(g18,g0)
    c: Coincident(g18,g3)
    c: Vertical(g18)
    c: Coincident(g19,g4)
    c: Coincident(g19,g8)
    c: Vertical(g19)
    c: Coincident(g20,g5)
    c: Coincident(g20,g9)
    c: Vertical(g20)
    c: Coincident(g21,g5)
    c: Coincident(g21,g9)
    c: Vertical(g21)
    c: Coincident(g22,g10)
    c: Coincident(g22,g6)
    c: Vertical(g22)
    c: Coincident(g23,g6)
    c: Coincident(g23,g10)
    c: Vertical(g23)
FEATURE [Part::Extrusion] Extrude048  label="removeToCreateFanGrillHoles004"
  Base = -> Sketch057
  Dir = (0,-1,6e-16)
  DirMode = 2
  FaceMakerClass = Part::FaceMakerBullseye
  LengthFwd = 10
  LengthRev = 0
  Placement = pos=(65.4,44,54.82) rot=(0,0,1;0rad)
  Solid = true
  Symmetric = false
FEATURE [Part::Cut] Cut040  label="top021"
  Base = -> Fillet039
  Tool = -> Extrude048
FEATURE [Part::Cylinder] Cylinder041  label="removeToCreteHoleForPlugHousing034"
  Angle = 360
  AttacherType = Attacher::AttachEngine3D
  Height = 20
  Placement = pos=(-2,19,36) rot=(0,1,0;1.5708rad)
  Radius = 14.3
FEATURE [Part::MultiFuse] Fusion089  label="removeToCreteHoleForPlugHousing035"
  Shapes = -> [Box026,Cylinder041]
FEATURE [Part::Cylinder] Cylinder042
  Angle = 360
  AttacherType = Attacher::AttachEngine3D
  Height = 20
  Placement = pos=(0,0,36.15) rot=(0,0,1;0rad)
  Radius = 14.3
FEATURE [Part::Cylinder] Cylinder043
  Angle = 360
  AttacherType = Attacher::AttachEngine3D
  Height = 10
  Placement = pos=(0,0,36.15) rot=(0,0,1;0rad)
  Radius = 4
FEATURE [Part::Box] Box027  label="removeToCreteHoleForPlugHousing036"
  AttacherType = Attacher::AttachEngine3D
  Height = 28.6
  Length = 20
  Placement = pos=(106.15,0,21.7) rot=(0,0,1;0rad)
  Width = 19
FEATURE [Part::Cut] Cut041  label="top022"
  Base = -> Cut040
  Tool = -> Fusion087
FEATURE [Part::Cut] Cut039  label="top020"
  Base = -> Cut041
  Tool = -> Fusion089
FEATURE [Part::MultiFuse] Fusion090  label="removeToCreteHoleForPlugHousing037"
  Placement = pos=(70,19,36) rot=(0,1,0;1.5708rad)
  Shapes = -> [Cylinder042,Cylinder043]
FEATURE [Part::MultiFuse] Fusion088  label="removeToCreteHoleForPlugHousing033"
  Shapes = -> [Box027,Fusion090]
FEATURE [Part::Cut] Cut042  label="removeToCreteHoleForPlugHousing038"
  Base = -> Cut039
  Tool = -> Fusion088
FEATURE [Part::MultiFuse] Fusion091  label="removeFromTop"
  Shapes = -> [Fillet038,Fusion085,Fusion084,Fusion083,Extrude045]
FEATURE [Part::Cut] Cut043  label="REAL TOP ====="
  Base = -> Fillet036
  Tool = -> Fusion091
FEATURE [Part::MultiFuse] Fusion092  label="caseScrewPillarBracket016"
  Shapes = -> [Extrude030,Extrude031,Extrude032,Extrude033,Extrude034,Extrude035,Extrude036,Extrude037,Box013,Box014]
FEATURE [Sketcher::SketchObject] Sketch058  label="topSketch015"
  FullyConstrained = true
  sketch-geometry (20):
    g0: LineSegment StartX=5.21097e-06 StartY=3 StartZ=0 EndX=5.21097e-06 EndY=19 EndZ=0
    g1: ArcOfCircle CenterX=19 CenterY=19 CenterZ=0 NormalX=0 NormalY=0 NormalZ=1 AngleXU=0 Radius=19 StartAngle=1.5708 EndAngle=3.14159
    g2: ArcOfCircle CenterX=19 CenterY=19 CenterZ=0 NormalX=0 NormalY=0 NormalZ=1 AngleXU=0 Radius=16 StartAngle=1.5708 EndAngle=3.14159
    g3: LineSegment StartX=114 StartY=35 StartZ=0 EndX=19 EndY=35 EndZ=0
    g4: LineSegment StartX=5.21097e-06 StartY=3 StartZ=0 EndX=5.21097e-06 EndY=0 EndZ=0
    g5: LineSegment StartX=3 StartY=0 StartZ=0 EndX=5.21097e-06 EndY=0 EndZ=0
    g6: LineSegment StartX=3 StartY=19 StartZ=0 EndX=3 EndY=0 EndZ=0
    g7: LineSegment StartX=19 StartY=38 StartZ=0 EndX=124 EndY=38 EndZ=0
    g8: Circle CenterX=119 CenterY=35 CenterZ=0 NormalX=0 NormalY=0 NormalZ=1 AngleXU=0 Radius=1
    g9: Circle CenterX=121 CenterY=35 CenterZ=0 NormalX=0 NormalY=0 NormalZ=1 AngleXU=0 Radius=1
    g10: Circle CenterX=121 CenterY=33 CenterZ=0 NormalX=0 NormalY=0 NormalZ=1 AngleXU=0 Radius=1
    g11: BSplineCurve PolesCount=3 KnotsCount=2 Degree=2 IsPeriodic=0
    g12: GeomPoint X=119 Y=35 Z=0
    g13: GeomPoint X=121 Y=33 Z=0
    g14: LineSegment StartX=119 StartY=35 StartZ=0 EndX=114 EndY=35 EndZ=0
    g15: ArcOfCircle CenterX=105 CenterY=19 CenterZ=0 NormalX=0 NormalY=0 NormalZ=1 AngleXU=0 Radius=19 StartAngle=5.7297 EndAngle=6.28319
    g16: ArcOfCircle CenterX=105 CenterY=19 CenterZ=0 NormalX=0 NormalY=0 NormalZ=1 AngleXU=0 Radius=16 StartAngle=5.60905 EndAngle=6.28319
    g17: LineSegment StartX=121 StartY=33 StartZ=0 EndX=121 EndY=19 EndZ=0
    g18: LineSegment StartX=124 StartY=38 StartZ=0 EndX=124 EndY=19 EndZ=0
    g19: LineSegment StartX=117.5 StartY=9.01251 StartZ=0 EndX=121.163 EndY=9.0125 EndZ=0
  constraints (46):
    c: Vertical(g0)
    c: Block(g0)
    c: Coincident(g1,g0)
    c: Block(g1)
    c: Coincident(g2,g1)
    c: Block(g2)
    c: Coincident(g3,g2)
    c: Horizontal(g3)
    c: Tangent(g3,g2)
    c: Coincident(g4,g0)
    c: Distance(g4) = 3
    c: Vertical(g4)
    c: Coincident(g5,g4)
    c: Horizontal(g5)
    c: Coincident(g6,g2)
    c: Coincident(g6,g5)
    c: Vertical(g6)
    c: Horizontal(g7)
    c: Distance(g7) = 105
    c: Coincident(g7,g1)
    c: Block(g3)
    c: Weight(g8) = 1
    c: Equal(g8,g9)
    c: Equal(g8,g10)
    c: InternalAlignment(g8,g11)
    c: InternalAlignment(g9,g11)
    c: InternalAlignment(g10,g11)
    c: InternalAlignment(g12,g11)
    c: InternalAlignment(g13,g11)
    c: Block(g11)
    c: Coincident(g14,g11)
    c: Coincident(g14,g3)
    c: Horizontal(g14)
    c: Block(g15)
    c: Coincident(g16,g15)
    c: Block(g16)
    c: Coincident(g17,g11)
    c: Coincident(g17,g16)
    c: Vertical(g17)
    c: Distance(g17) = 14
    c: Coincident(g18,g7)
    c: Coincident(g18,g15)
    c: Vertical(g18)
    c: Distance(g18) = 19
    c: Coincident(g19,g16)
    c: Coincident(g19,g15)
FEATURE [Part::Extrusion] Extrude049  label="top023"
  Base = -> Sketch058
  Dir = (0,0,1)
  DirMode = 2
  FaceMakerClass = Part::FaceMakerBullseye
  LengthFwd = 72
  LengthRev = 0
  Solid = true
  Symmetric = false
FEATURE [Sketcher::SketchObject] Sketch059
  FullyConstrained = true
  MapMode = 3
  Placement = pos=(0,0,0) rot=(1,0,0;1.5708rad)
  Support = -> [Extrude049]
  sketch-geometry (8):
    g0: Circle CenterX=80.351 CenterY=-67.6202 CenterZ=0 NormalX=0 NormalY=0 NormalZ=1 AngleXU=0 Radius=2
    g1: Circle CenterX=80.351 CenterY=-67.6202 CenterZ=0 NormalX=0 NormalY=0 NormalZ=1 AngleXU=0 Radius=3
    g2: Circle CenterX=80.351 CenterY=-4.92017 CenterZ=0 NormalX=0 NormalY=0 NormalZ=1 AngleXU=0 Radius=2
    g3: Circle CenterX=80.351 CenterY=-4.92017 CenterZ=0 NormalX=0 NormalY=0 NormalZ=1 AngleXU=0 Radius=3
    g4: Circle CenterX=23.851 CenterY=-4.92017 CenterZ=0 NormalX=0 NormalY=0 NormalZ=1 AngleXU=0 Radius=2
    g5: Circle CenterX=23.851 CenterY=-4.92017 CenterZ=0 NormalX=0 NormalY=0 NormalZ=1 AngleXU=0 Radius=3
    g6: Circle CenterX=23.851 CenterY=-67.6202 CenterZ=0 NormalX=0 NormalY=0 NormalZ=1 AngleXU=0 Radius=2
    g7: Circle CenterX=23.851 CenterY=-67.6202 CenterZ=0 NormalX=0 NormalY=0 NormalZ=1 AngleXU=0 Radius=3
  constraints (8):
    c: Block(g3)
    c: Block(g2)
    c: Block(g1)
    c: Block(g0)
    c: Block(g6)
    c: Block(g7)
    c: Block(g4)
    c: Block(g5)
FEATURE [Sketcher::SketchObject] Sketch060
  FullyConstrained = true
  MapMode = 3
  Placement = pos=(0,0,0) rot=(1,0,0;1.5708rad)
  Support = -> [Extrude049]
  sketch-geometry (8):
    g0: Circle CenterX=80.351 CenterY=-67.6202 CenterZ=0 NormalX=0 NormalY=0 NormalZ=1 AngleXU=0 Radius=3
    g1: Circle CenterX=80.351 CenterY=-4.92017 CenterZ=0 NormalX=0 NormalY=0 NormalZ=1 AngleXU=0 Radius=3
    g2: Circle CenterX=23.851 CenterY=-4.92017 CenterZ=0 NormalX=0 NormalY=0 NormalZ=1 AngleXU=0 Radius=3
    g3: Circle CenterX=23.851 CenterY=-67.6202 CenterZ=0 NormalX=0 NormalY=0 NormalZ=1 AngleXU=0 Radius=3
    g4: Circle CenterX=23.851 CenterY=-67.6202 CenterZ=0 NormalX=0 NormalY=0 NormalZ=1 AngleXU=0 Radius=5
    g5: Circle CenterX=80.351 CenterY=-67.6202 CenterZ=0 NormalX=0 NormalY=0 NormalZ=1 AngleXU=0 Radius=5
    g6: Circle CenterX=23.851 CenterY=-4.92017 CenterZ=0 NormalX=0 NormalY=0 NormalZ=1 AngleXU=0 Radius=5
    g7: Circle CenterX=80.351 CenterY=-4.92017 CenterZ=0 NormalX=0 NormalY=0 NormalZ=1 AngleXU=0 Radius=5
  constraints (8):
    c: Block(g1)
    c: Block(g0)
    c: Block(g3)
    c: Block(g2)
    c: Block(g5)
    c: Block(g4)
    c: Block(g6)
    c: Block(g7)
FEATURE [Sketcher::SketchObject] Sketch061
  FullyConstrained = true
  MapMode = 3
  Placement = pos=(0,0,0) rot=(1,0,0;1.5708rad)
  sketch-geometry (8):
    g0: Circle CenterX=80.351 CenterY=-67.6202 CenterZ=0 NormalX=0 NormalY=0 NormalZ=1 AngleXU=0 Radius=3
    g1: Circle CenterX=80.351 CenterY=-4.92017 CenterZ=0 NormalX=0 NormalY=0 NormalZ=1 AngleXU=0 Radius=3
    g2: Circle CenterX=23.851 CenterY=-4.92017 CenterZ=0 NormalX=0 NormalY=0 NormalZ=1 AngleXU=0 Radius=3
    g3: Circle CenterX=23.851 CenterY=-67.6202 CenterZ=0 NormalX=0 NormalY=0 NormalZ=1 AngleXU=0 Radius=3
    g4: Circle CenterX=23.851 CenterY=-67.6202 CenterZ=0 NormalX=0 NormalY=0 NormalZ=1 AngleXU=0 Radius=5
    g5: Circle CenterX=80.351 CenterY=-67.6202 CenterZ=0 NormalX=0 NormalY=0 NormalZ=1 AngleXU=0 Radius=5
    g6: Circle CenterX=23.851 CenterY=-4.92017 CenterZ=0 NormalX=0 NormalY=0 NormalZ=1 AngleXU=0 Radius=5
    g7: Circle CenterX=80.351 CenterY=-4.92017 CenterZ=0 NormalX=0 NormalY=0 NormalZ=1 AngleXU=0 Radius=5
  constraints (8):
    c: Block(g1)
    c: Block(g0)
    c: Block(g3)
    c: Block(g2)
    c: Block(g5)
    c: Block(g4)
    c: Block(g6)
    c: Block(g7)
FEATURE [Sketcher::SketchObject] Sketch062  label="topSketch016"
  FullyConstrained = true
  sketch-geometry (20):
    g0: LineSegment StartX=5.21097e-06 StartY=3 StartZ=0 EndX=5.21097e-06 EndY=19 EndZ=0
    g1: ArcOfCircle CenterX=19 CenterY=19 CenterZ=0 NormalX=0 NormalY=0 NormalZ=1 AngleXU=0 Radius=19 StartAngle=1.5708 EndAngle=3.14159
    g2: ArcOfCircle CenterX=19 CenterY=19 CenterZ=0 NormalX=0 NormalY=0 NormalZ=1 AngleXU=0 Radius=16 StartAngle=1.5708 EndAngle=3.14159
    g3: LineSegment StartX=114 StartY=35 StartZ=0 EndX=19 EndY=35 EndZ=0
    g4: LineSegment StartX=5.21097e-06 StartY=3 StartZ=0 EndX=5.21097e-06 EndY=0 EndZ=0
    g5: LineSegment StartX=3 StartY=0 StartZ=0 EndX=5.21097e-06 EndY=0 EndZ=0
    g6: LineSegment StartX=3 StartY=19 StartZ=0 EndX=3 EndY=0 EndZ=0
    g7: LineSegment StartX=19 StartY=38 StartZ=0 EndX=124 EndY=38 EndZ=0
    g8: Circle CenterX=119 CenterY=35 CenterZ=0 NormalX=0 NormalY=0 NormalZ=1 AngleXU=0 Radius=1
    g9: Circle CenterX=121 CenterY=35 CenterZ=0 NormalX=0 NormalY=0 NormalZ=1 AngleXU=0 Radius=1
    g10: Circle CenterX=121 CenterY=33 CenterZ=0 NormalX=0 NormalY=0 NormalZ=1 AngleXU=0 Radius=1
    g11: BSplineCurve PolesCount=3 KnotsCount=2 Degree=2 IsPeriodic=0
    g12: GeomPoint X=119 Y=35 Z=0
    g13: GeomPoint X=121 Y=33 Z=0
    g14: LineSegment StartX=119 StartY=35 StartZ=0 EndX=114 EndY=35 EndZ=0
    g15: ArcOfCircle CenterX=105 CenterY=19 CenterZ=0 NormalX=0 NormalY=0 NormalZ=1 AngleXU=0 Radius=19 StartAngle=5.7297 EndAngle=6.28319
    g16: ArcOfCircle CenterX=105 CenterY=19 CenterZ=0 NormalX=0 NormalY=0 NormalZ=1 AngleXU=0 Radius=16 StartAngle=5.60905 EndAngle=6.28319
    g17: LineSegment StartX=121 StartY=33 StartZ=0 EndX=121 EndY=19 EndZ=0
    g18: LineSegment StartX=124 StartY=38 StartZ=0 EndX=124 EndY=19 EndZ=0
    g19: LineSegment StartX=117.5 StartY=9.01251 StartZ=0 EndX=121.163 EndY=9.0125 EndZ=0
  constraints (46):
    c: Vertical(g0)
    c: Block(g0)
    c: Coincident(g1,g0)
    c: Block(g1)
    c: Coincident(g2,g1)
    c: Block(g2)
    c: Coincident(g3,g2)
    c: Horizontal(g3)
    c: Tangent(g3,g2)
    c: Coincident(g4,g0)
    c: Distance(g4) = 3
    c: Vertical(g4)
    c: Coincident(g5,g4)
    c: Horizontal(g5)
    c: Coincident(g6,g2)
    c: Coincident(g6,g5)
    c: Vertical(g6)
    c: Horizontal(g7)
    c: Distance(g7) = 105
    c: Coincident(g7,g1)
    c: Block(g3)
    c: Weight(g8) = 1
    c: Equal(g8,g9)
    c: Equal(g8,g10)
    c: InternalAlignment(g8,g11)
    c: InternalAlignment(g9,g11)
    c: InternalAlignment(g10,g11)
    c: InternalAlignment(g12,g11)
    c: InternalAlignment(g13,g11)
    c: Block(g11)
    c: Coincident(g14,g11)
    c: Coincident(g14,g3)
    c: Horizontal(g14)
    c: Block(g15)
    c: Coincident(g16,g15)
    c: Block(g16)
    c: Coincident(g17,g11)
    c: Coincident(g17,g16)
    c: Vertical(g17)
    c: Distance(g17) = 14
    c: Coincident(g18,g7)
    c: Coincident(g18,g15)
    c: Vertical(g18)
    c: Distance(g18) = 19
    c: Coincident(g19,g16)
    c: Coincident(g19,g15)
FEATURE [Part::Extrusion] Extrude053  label="top024"
  Base = -> Sketch062
  Dir = (0,0,1)
  DirMode = 2
  FaceMakerClass = Part::FaceMakerBullseye
  LengthFwd = 72
  LengthRev = 0
  Solid = true
  Symmetric = false
FEATURE [Sketcher::SketchObject] Sketch063
  FullyConstrained = true
  MapMode = 3
  Placement = pos=(0,0,0) rot=(1,0,0;1.5708rad)
  Support = -> [Extrude053]
  sketch-geometry (8):
    g0: Circle CenterX=80.351 CenterY=-67.6202 CenterZ=0 NormalX=0 NormalY=0 NormalZ=1 AngleXU=0 Radius=2
    g1: Circle CenterX=80.351 CenterY=-67.6202 CenterZ=0 NormalX=0 NormalY=0 NormalZ=1 AngleXU=0 Radius=3
    g2: Circle CenterX=80.351 CenterY=-4.92017 CenterZ=0 NormalX=0 NormalY=0 NormalZ=1 AngleXU=0 Radius=2
    g3: Circle CenterX=80.351 CenterY=-4.92017 CenterZ=0 NormalX=0 NormalY=0 NormalZ=1 AngleXU=0 Radius=3
    g4: Circle CenterX=23.851 CenterY=-4.92017 CenterZ=0 NormalX=0 NormalY=0 NormalZ=1 AngleXU=0 Radius=2
    g5: Circle CenterX=23.851 CenterY=-4.92017 CenterZ=0 NormalX=0 NormalY=0 NormalZ=1 AngleXU=0 Radius=3
    g6: Circle CenterX=23.851 CenterY=-67.6202 CenterZ=0 NormalX=0 NormalY=0 NormalZ=1 AngleXU=0 Radius=2
    g7: Circle CenterX=23.851 CenterY=-67.6202 CenterZ=0 NormalX=0 NormalY=0 NormalZ=1 AngleXU=0 Radius=3
  constraints (8):
    c: Block(g3)
    c: Block(g2)
    c: Block(g1)
    c: Block(g0)
    c: Block(g6)
    c: Block(g7)
    c: Block(g4)
    c: Block(g5)
FEATURE [Part::Extrusion] Extrude054
  Base = -> Sketch063
  Dir = (0,-1,2e-16)
  DirMode = 2
  FaceMakerClass = Part::FaceMakerBullseye
  LengthFwd = 6
  LengthRev = 0
  Placement = pos=(0,9,0) rot=(0,0,1;0rad)
  Solid = true
  Symmetric = false
FEATURE [Sketcher::SketchObject] Sketch064  label="topSketch017"
  FullyConstrained = true
  sketch-geometry (20):
    g0: LineSegment StartX=5.21097e-06 StartY=3 StartZ=0 EndX=5.21097e-06 EndY=19 EndZ=0
    g1: ArcOfCircle CenterX=19 CenterY=19 CenterZ=0 NormalX=0 NormalY=0 NormalZ=1 AngleXU=0 Radius=19 StartAngle=1.5708 EndAngle=3.14159
    g2: ArcOfCircle CenterX=19 CenterY=19 CenterZ=0 NormalX=0 NormalY=0 NormalZ=1 AngleXU=0 Radius=16 StartAngle=1.5708 EndAngle=3.14159
    g3: LineSegment StartX=114 StartY=35 StartZ=0 EndX=19 EndY=35 EndZ=0
    g4: LineSegment StartX=5.21097e-06 StartY=3 StartZ=0 EndX=5.21097e-06 EndY=0 EndZ=0
    g5: LineSegment StartX=3 StartY=0 StartZ=0 EndX=5.21097e-06 EndY=0 EndZ=0
    g6: LineSegment StartX=3 StartY=19 StartZ=0 EndX=3 EndY=0 EndZ=0
    g7: LineSegment StartX=19 StartY=38 StartZ=0 EndX=124 EndY=38 EndZ=0
    g8: Circle CenterX=119 CenterY=35 CenterZ=0 NormalX=0 NormalY=0 NormalZ=1 AngleXU=0 Radius=1
    g9: Circle CenterX=121 CenterY=35 CenterZ=0 NormalX=0 NormalY=0 NormalZ=1 AngleXU=0 Radius=1
    g10: Circle CenterX=121 CenterY=33 CenterZ=0 NormalX=0 NormalY=0 NormalZ=1 AngleXU=0 Radius=1
    g11: BSplineCurve PolesCount=3 KnotsCount=2 Degree=2 IsPeriodic=0
    g12: GeomPoint X=119 Y=35 Z=0
    g13: GeomPoint X=121 Y=33 Z=0
    g14: LineSegment StartX=119 StartY=35 StartZ=0 EndX=114 EndY=35 EndZ=0
    g15: ArcOfCircle CenterX=105 CenterY=19 CenterZ=0 NormalX=0 NormalY=0 NormalZ=1 AngleXU=0 Radius=19 StartAngle=5.7297 EndAngle=6.28319
    g16: ArcOfCircle CenterX=105 CenterY=19 CenterZ=0 NormalX=0 NormalY=0 NormalZ=1 AngleXU=0 Radius=16 StartAngle=5.60905 EndAngle=6.28319
    g17: LineSegment StartX=121 StartY=33 StartZ=0 EndX=121 EndY=19 EndZ=0
    g18: LineSegment StartX=124 StartY=38 StartZ=0 EndX=124 EndY=19 EndZ=0
    g19: LineSegment StartX=117.5 StartY=9.01251 StartZ=0 EndX=121.163 EndY=9.0125 EndZ=0
  constraints (46):
    c: Vertical(g0)
    c: Block(g0)
    c: Coincident(g1,g0)
    c: Block(g1)
    c: Coincident(g2,g1)
    c: Block(g2)
    c: Coincident(g3,g2)
    c: Horizontal(g3)
    c: Tangent(g3,g2)
    c: Coincident(g4,g0)
    c: Distance(g4) = 3
    c: Vertical(g4)
    c: Coincident(g5,g4)
    c: Horizontal(g5)
    c: Coincident(g6,g2)
    c: Coincident(g6,g5)
    c: Vertical(g6)
    c: Horizontal(g7)
    c: Distance(g7) = 105
    c: Coincident(g7,g1)
    c: Block(g3)
    c: Weight(g8) = 1
    c: Equal(g8,g9)
    c: Equal(g8,g10)
    c: InternalAlignment(g8,g11)
    c: InternalAlignment(g9,g11)
    c: InternalAlignment(g10,g11)
    c: InternalAlignment(g12,g11)
    c: InternalAlignment(g13,g11)
    c: Block(g11)
    c: Coincident(g14,g11)
    c: Coincident(g14,g3)
    c: Horizontal(g14)
    c: Block(g15)
    c: Coincident(g16,g15)
    c: Block(g16)
    c: Coincident(g17,g11)
    c: Coincident(g17,g16)
    c: Vertical(g17)
    c: Distance(g17) = 14
    c: Coincident(g18,g7)
    c: Coincident(g18,g15)
    c: Vertical(g18)
    c: Distance(g18) = 19
    c: Coincident(g19,g16)
    c: Coincident(g19,g15)
FEATURE [Sketcher::SketchObject] Sketch065
  FullyConstrained = true
  MapMode = 3
  Placement = pos=(0,0,0) rot=(1,0,0;1.5708rad)
  sketch-geometry (8):
    g0: Circle CenterX=80.351 CenterY=-67.6202 CenterZ=0 NormalX=0 NormalY=0 NormalZ=1 AngleXU=0 Radius=3
    g1: Circle CenterX=80.351 CenterY=-4.92017 CenterZ=0 NormalX=0 NormalY=0 NormalZ=1 AngleXU=0 Radius=3
    g2: Circle CenterX=23.851 CenterY=-4.92017 CenterZ=0 NormalX=0 NormalY=0 NormalZ=1 AngleXU=0 Radius=3
    g3: Circle CenterX=23.851 CenterY=-67.6202 CenterZ=0 NormalX=0 NormalY=0 NormalZ=1 AngleXU=0 Radius=3
    g4: Circle CenterX=23.851 CenterY=-67.6202 CenterZ=0 NormalX=0 NormalY=0 NormalZ=1 AngleXU=0 Radius=5
    g5: Circle CenterX=80.351 CenterY=-67.6202 CenterZ=0 NormalX=0 NormalY=0 NormalZ=1 AngleXU=0 Radius=5
    g6: Circle CenterX=23.851 CenterY=-4.92017 CenterZ=0 NormalX=0 NormalY=0 NormalZ=1 AngleXU=0 Radius=5
    g7: Circle CenterX=80.351 CenterY=-4.92017 CenterZ=0 NormalX=0 NormalY=0 NormalZ=1 AngleXU=0 Radius=5
  constraints (8):
    c: Block(g1)
    c: Block(g0)
    c: Block(g3)
    c: Block(g2)
    c: Block(g5)
    c: Block(g4)
    c: Block(g6)
    c: Block(g7)
FEATURE [Part::Extrusion] Extrude056
  Base = -> Sketch065
  Dir = (0,-1,2e-16)
  DirMode = 2
  FaceMakerClass = Part::FaceMakerBullseye
  LengthFwd = 2
  LengthRev = 0
  Solid = true
  Symmetric = false
FEATURE [Part::Extrusion] Extrude057  label="top025"
  Base = -> Sketch064
  Dir = (0,0,1)
  DirMode = 2
  FaceMakerClass = Part::FaceMakerBullseye
  LengthFwd = 72
  LengthRev = 0
  Solid = true
  Symmetric = false
FEATURE [Sketcher::SketchObject] Sketch066
  FullyConstrained = true
  MapMode = 3
  Placement = pos=(0,0,0) rot=(1,0,0;1.5708rad)
  Support = -> [Extrude057]
  sketch-geometry (8):
    g0: Circle CenterX=80.351 CenterY=-67.6202 CenterZ=0 NormalX=0 NormalY=0 NormalZ=1 AngleXU=0 Radius=3
    g1: Circle CenterX=80.351 CenterY=-4.92017 CenterZ=0 NormalX=0 NormalY=0 NormalZ=1 AngleXU=0 Radius=3
    g2: Circle CenterX=23.851 CenterY=-4.92017 CenterZ=0 NormalX=0 NormalY=0 NormalZ=1 AngleXU=0 Radius=3
    g3: Circle CenterX=23.851 CenterY=-67.6202 CenterZ=0 NormalX=0 NormalY=0 NormalZ=1 AngleXU=0 Radius=3
    g4: Circle CenterX=23.851 CenterY=-67.6202 CenterZ=0 NormalX=0 NormalY=0 NormalZ=1 AngleXU=0 Radius=5
    g5: Circle CenterX=80.351 CenterY=-67.6202 CenterZ=0 NormalX=0 NormalY=0 NormalZ=1 AngleXU=0 Radius=5
    g6: Circle CenterX=23.851 CenterY=-4.92017 CenterZ=0 NormalX=0 NormalY=0 NormalZ=1 AngleXU=0 Radius=5
    g7: Circle CenterX=80.351 CenterY=-4.92017 CenterZ=0 NormalX=0 NormalY=0 NormalZ=1 AngleXU=0 Radius=5
  constraints (8):
    c: Block(g1)
    c: Block(g0)
    c: Block(g3)
    c: Block(g2)
    c: Block(g5)
    c: Block(g4)
    c: Block(g6)
    c: Block(g7)
FEATURE [Part::Extrusion] Extrude055
  Base = -> Sketch066
  Dir = (0,-1,2e-16)
  DirMode = 2
  FaceMakerClass = Part::FaceMakerBullseye
  LengthFwd = 2
  LengthRev = 0
  Solid = true
  Symmetric = false
FEATURE [Part::Fillet] Fillet041
  Base = -> Extrude056
  Edges = 4 edges r=1.99: [Edge6,Edge12,Edge18,Edge24]
FEATURE [Part::Cut] Cut045
  Base = -> Extrude055
  Placement = pos=(0,6,0) rot=(0,0,1;0rad)
  Tool = -> Fillet041
FEATURE [Part::MultiFuse] Fusion095  label="pcbScrewPillars"
  Placement = pos=(-3.2,-1,72.3) rot=(0,0,1;0rad)
  Shapes = -> [Cut045,Extrude054]
FEATURE [Part::Feature] Face113
  shape: bbox 3.2 x 1.5 x 2e-07 mm, 1 faces, 0 solids (baked)
FEATURE [Part::Revolution] Revolve121  label="backCaseScrewRetainer002"
  Angle = 360
  Axis = (0,1,0)
  Base = (0,0,0)
  FaceMakerClass = Part::FaceMakerBullseye
  Placement = pos=(12.5,3,62) rot=(0,0,1;0rad)
  Solid = false
  Source = -> Face113
  Symmetric = false
FEATURE [Part::Feature] Face114
  shape: bbox 3.2 x 1.5 x 2e-07 mm, 1 faces, 0 solids (baked)
FEATURE [Part::Feature] Face115
  shape: bbox 3.2 x 1.5 x 2e-07 mm, 1 faces, 0 solids (baked)
FEATURE [Part::Feature] Face116
  shape: bbox 3.2 x 1.5 x 2e-07 mm, 1 faces, 0 solids (baked)
FEATURE [Part::Revolution] Revolve122  label="frontCaseScrewRetainer004"
  Angle = 360
  Axis = (0,1,0)
  Base = (0,0,0)
  FaceMakerClass = Part::FaceMakerBullseye
  Placement = pos=(89.5,3,68.5) rot=(0,0,1;0rad)
  Solid = false
  Source = -> Face115
  Symmetric = false
FEATURE [Part::Revolution] Revolve123  label="frontCaseScrewRetainer005"
  Angle = 360
  Axis = (0,1,0)
  Base = (0,0,0)
  FaceMakerClass = Part::FaceMakerBullseye
  Placement = pos=(89.5,3,3.5) rot=(0,0,1;0rad)
  Solid = false
  Source = -> Face116
  Symmetric = false
FEATURE [Part::Revolution] Revolve124  label="backCaseScrewRetainer003"
  Angle = 360
  Axis = (0,1,0)
  Base = (0,0,0)
  FaceMakerClass = Part::FaceMakerBullseye
  Placement = pos=(12.5,3,10) rot=(0,0,1;0rad)
  Solid = false
  Source = -> Face114
  Symmetric = false
FEATURE [Part::Feature] Face117
  shape: bbox 3.6 x 3.2 x 2e-07 mm, 1 faces, 0 solids (baked)
FEATURE [Part::Revolution] Revolve125  label="moreFrontCaseScrewRetainer004"
  Angle = 360
  Axis = (0,1,0)
  Base = (0,0,0)
  FaceMakerClass = Part::FaceMakerBullseye
  Placement = pos=(109.5,4.5,68.5) rot=(0,0,1;0rad)
  Solid = false
  Source = -> Face117
  Symmetric = false
FEATURE [Part::Feature] Face118
  shape: bbox 3.6 x 3.2 x 2e-07 mm, 1 faces, 0 solids (baked)
FEATURE [Part::Revolution] Revolve126  label="moreFrontCaseScrewRetainer005"
  Angle = 360
  Axis = (0,1,0)
  Base = (0,0,0)
  FaceMakerClass = Part::FaceMakerBullseye
  Placement = pos=(109.5,4.5,3.5) rot=(0,0,1;0rad)
  Solid = false
  Source = -> Face118
  Symmetric = false
FEATURE [Part::MultiFuse] Fusion096  label="screwRetainers001"
  Shapes = -> [Revolve126,Revolve125,Revolve124,Revolve123,Revolve122,Revolve121]
FEATURE [Part::Feature] Face119
  shape: bbox 10 x 16.5 x 2e-07 mm, 1 faces, 0 solids (baked)
FEATURE [Part::Revolution] Revolve130  label="plugHousing050"
  Angle = 360
  Axis = (0,1,0)
  Base = (0,0,0)
  FaceMakerClass = Part::FaceMakerBullseye
  Placement = pos=(0,0,36.15) rot=(0,0,1;0rad)
  Solid = false
  Source = -> Face119
  Symmetric = false
FEATURE [Part::Feature] Face120
  shape: bbox 10 x 16.5 x 2e-07 mm, 1 faces, 0 solids (baked)
FEATURE [Part::Feature] Face121
  shape: bbox 10 x 16.5 x 2e-07 mm, 1 faces, 0 solids (baked)
FEATURE [Part::Revolution] Revolve127  label="plugHousing047"
  Angle = 360
  Axis = (0,1,0)
  Base = (0,0,0)
  FaceMakerClass = Part::FaceMakerBullseye
  Placement = pos=(0,0,36.15) rot=(0,0,1;0rad)
  Solid = false
  Source = -> Face121
  Symmetric = false
FEATURE [Part::Feature] Face122
  shape: bbox 10 x 16.5 x 2e-07 mm, 1 faces, 0 solids (baked)
FEATURE [Part::Feature] Face123
  shape: bbox 10 x 16.5 x 2e-07 mm, 1 faces, 0 solids (baked)
FEATURE [Part::Revolution] Revolve128  label="plugHousing048"
  Angle = 360
  Axis = (0,1,0)
  Base = (0,0,0)
  FaceMakerClass = Part::FaceMakerBullseye
  Placement = pos=(0,0,36.15) rot=(0,0,1;0rad)
  Solid = false
  Source = -> Face123
  Symmetric = false
FEATURE [Part::MultiFuse] Fusion100  label="plugHousing054"
  Placement = pos=(0,0,0) rot=(0,0,1;1.5708rad)
  Shapes = -> [Revolve130,Revolve128]
FEATURE [Part::Feature] Face124
  shape: bbox 10 x 16.5 x 2e-07 mm, 1 faces, 0 solids (baked)
FEATURE [Part::Feature] Face125
  shape: bbox 10 x 16.5 x 2e-07 mm, 1 faces, 0 solids (baked)
FEATURE [Part::Revolution] Revolve129  label="plugHousing049"
  Angle = 360
  Axis = (0,1,0)
  Base = (0,0,0)
  FaceMakerClass = Part::FaceMakerBullseye
  Placement = pos=(0,0,36.15) rot=(0,0,1;0rad)
  Solid = false
  Source = -> Face125
  Symmetric = false
FEATURE [Part::Feature] Face126
  shape: bbox 10 x 16.5 x 2e-07 mm, 1 faces, 0 solids (baked)
FEATURE [Part::Revolution] Revolve131  label="plugHousing058"
  Angle = 360
  Axis = (0,1,0)
  Base = (0,0,0)
  FaceMakerClass = Part::FaceMakerBullseye
  Placement = pos=(0,0,36.15) rot=(0,0,1;0rad)
  Solid = false
  Source = -> Face120
  Symmetric = false
FEATURE [Part::MultiFuse] Fusion099  label="plugHousing053"
  Placement = pos=(0,0,0) rot=(0,0,1;1.5708rad)
  Shapes = -> [Revolve127,Revolve131]
FEATURE [Part::MultiFuse] Fusion102  label="plugHousing056"
  Placement = pos=(0,19,0) rot=(0,0,1;3.14159rad)
  Shapes = -> [Fusion100,Fusion099]
FEATURE [Part::Revolution] Revolve132  label="plugHousing059"
  Angle = 360
  Axis = (0,1,0)
  Base = (0,0,0)
  FaceMakerClass = Part::FaceMakerBullseye
  Placement = pos=(0,0,36.15) rot=(0,0,1;0rad)
  Solid = false
  Source = -> Face126
  Symmetric = false
FEATURE [Part::Revolution] Revolve133  label="plugHousing060"
  Angle = 360
  Axis = (0,1,0)
  Base = (0,0,0)
  FaceMakerClass = Part::FaceMakerBullseye
  Placement = pos=(0,0,36.15) rot=(0,0,1;0rad)
  Solid = false
  Source = -> Face122
  Symmetric = false
FEATURE [Part::MultiFuse] Fusion097  label="plugHousing051"
  Placement = pos=(0,0,0) rot=(0,0,1;1.5708rad)
  Shapes = -> [Revolve133,Revolve132]
FEATURE [Part::Revolution] Revolve134  label="plugHousing061"
  Angle = 360
  Axis = (0,1,0)
  Base = (0,0,0)
  FaceMakerClass = Part::FaceMakerBullseye
  Placement = pos=(0,0,36.15) rot=(0,0,1;0rad)
  Solid = false
  Source = -> Face124
  Symmetric = false
FEATURE [Part::MultiFuse] Fusion101  label="plugHousing055"
  Placement = pos=(0,0,0) rot=(0,0,1;1.5708rad)
  Shapes = -> [Revolve129,Revolve134]
FEATURE [Part::MultiFuse] Fusion098  label="plugHousing052"
  Placement = pos=(0,19,0) rot=(0,0,1;3.14159rad)
  Shapes = -> [Fusion097,Fusion101]
FEATURE [Part::MultiFuse] Fusion103  label="plugHousing057"
  Placement = pos=(122.621,0,-0.15) rot=(0,0,1;0rad)
  Shapes = -> [Fusion102,Fusion098]
FEATURE [Part::Box] Box028  label="Cube015"
  AttacherType = Attacher::AttachEngine3D
  Height = 28
  Length = 3
  Placement = pos=(110.7,19,22) rot=(0,0,1;0rad)
  Width = 15.7
FEATURE [Part::Cylinder] Cylinder044
  Angle = 360
  AttacherType = Attacher::AttachEngine3D
  Height = 20
  Placement = pos=(0,0,36.15) rot=(0,0,1;0rad)
  Radius = 10.3
FEATURE [Part::Cylinder] Cylinder045
  Angle = 360
  AttacherType = Attacher::AttachEngine3D
  Height = 10
  Placement = pos=(0,0,36.15) rot=(0,0,1;0rad)
  Radius = 4
FEATURE [Part::MultiFuse] Fusion104  label="removeToCreteHoleForPlugHousing040"
  Placement = pos=(70,19,36) rot=(0,1,0;1.5708rad)
  Shapes = -> [Cylinder044,Cylinder045]
FEATURE [Part::Cut] Cut046  label="plugHousingTab003"
  Base = -> Box028
  Tool = -> Fusion104
FEATURE [Part::MultiFuse] Fusion105  label="plugHousing062"
  Shapes = -> [Fusion103,Cut046]
FEATURE [Part::Fillet] Fillet042
  Base = -> Fusion105
  Edges = 1 edges r=2: [Edge25]
FEATURE [Part::Fillet] Fillet043  label="plugHousing063"
  Base = -> Fillet042
  Edges = 1 edges r=2: [Edge8]
  Placement = pos=(7,0,0) rot=(0,0,1;0rad)
FEATURE [Part::Feature] Face127
  shape: bbox 10 x 16.5 x 2e-07 mm, 1 faces, 0 solids (baked)
FEATURE [Part::Feature] Face128
  shape: bbox 10 x 16.5 x 2e-07 mm, 1 faces, 0 solids (baked)
FEATURE [Part::Revolution] Revolve137  label="plugHousing070"
  Angle = 360
  Axis = (0,1,0)
  Base = (0,0,0)
  FaceMakerClass = Part::FaceMakerBullseye
  Placement = pos=(0,0,36.15) rot=(0,0,1;0rad)
  Solid = false
  Source = -> Face127
  Symmetric = false
FEATURE [Part::Revolution] Revolve140  label="plugHousing073"
  Angle = 360
  Axis = (0,1,0)
  Base = (0,0,0)
  FaceMakerClass = Part::FaceMakerBullseye
  Placement = pos=(0,0,36.15) rot=(0,0,1;0rad)
  Solid = false
  Source = -> Face128
  Symmetric = false
FEATURE [Part::Feature] Face129
  shape: bbox 10 x 16.5 x 2e-07 mm, 1 faces, 0 solids (baked)
FEATURE [Part::Revolution] Revolve138  label="plugHousing071"
  Angle = 360
  Axis = (0,1,0)
  Base = (0,0,0)
  FaceMakerClass = Part::FaceMakerBullseye
  Placement = pos=(0,0,36.15) rot=(0,0,1;0rad)
  Solid = false
  Source = -> Face129
  Symmetric = false
FEATURE [Part::Feature] Face130
  shape: bbox 10 x 16.5 x 2e-07 mm, 1 faces, 0 solids (baked)
FEATURE [Part::Revolution] Revolve139  label="plugHousing072"
  Angle = 360
  Axis = (0,1,0)
  Base = (0,0,0)
  FaceMakerClass = Part::FaceMakerBullseye
  Placement = pos=(0,0,36.15) rot=(0,0,1;0rad)
  Solid = false
  Source = -> Face130
  Symmetric = false
FEATURE [Part::Feature] Face131
  shape: bbox 10 x 16.5 x 2e-07 mm, 1 faces, 0 solids (baked)
FEATURE [Part::Revolution] Revolve135  label="plugHousing068"
  Angle = 360
  Axis = (0,1,0)
  Base = (0,0,0)
  FaceMakerClass = Part::FaceMakerBullseye
  Placement = pos=(0,0,36.15) rot=(0,0,1;0rad)
  Solid = false
  Source = -> Face131
  Symmetric = false
FEATURE [Part::MultiFuse] Fusion112  label="plugHousing078"
  Placement = pos=(0,0,0) rot=(0,0,1;1.5708rad)
  Shapes = -> [Revolve135,Revolve139]
FEATURE [Part::Feature] Face132
  shape: bbox 10 x 16.5 x 2e-07 mm, 1 faces, 0 solids (baked)
FEATURE [Part::Revolution] Revolve141  label="plugHousing074"
  Angle = 360
  Axis = (0,1,0)
  Base = (0,0,0)
  FaceMakerClass = Part::FaceMakerBullseye
  Placement = pos=(0,0,36.15) rot=(0,0,1;0rad)
  Solid = false
  Source = -> Face132
  Symmetric = false
FEATURE [Part::MultiFuse] Fusion110  label="plugHousing076"
  Placement = pos=(0,0,0) rot=(0,0,1;1.5708rad)
  Shapes = -> [Revolve141,Revolve140]
FEATURE [Part::Feature] Face133
  shape: bbox 10 x 16.5 x 2e-07 mm, 1 faces, 0 solids (baked)
FEATURE [Part::Revolution] Revolve136  label="plugHousing069"
  Angle = 360
  Axis = (0,1,0)
  Base = (0,0,0)
  FaceMakerClass = Part::FaceMakerBullseye
  Placement = pos=(0,0,36.15) rot=(0,0,1;0rad)
  Solid = false
  Source = -> Face133
  Symmetric = false
FEATURE [Part::MultiFuse] Fusion106  label="plugHousing064"
  Placement = pos=(0,0,0) rot=(0,0,1;1.5708rad)
  Shapes = -> [Revolve138,Revolve136]
FEATURE [Part::MultiFuse] Fusion108  label="plugHousing066"
  Placement = pos=(0,19,0) rot=(0,0,1;3.14159rad)
  Shapes = -> [Fusion106,Fusion112]
FEATURE [Part::Feature] Face134
  shape: bbox 10 x 16.5 x 2e-07 mm, 1 faces, 0 solids (baked)
FEATURE [Part::Revolution] Revolve142  label="plugHousing075"
  Angle = 360
  Axis = (0,1,0)
  Base = (0,0,0)
  FaceMakerClass = Part::FaceMakerBullseye
  Placement = pos=(0,0,36.15) rot=(0,0,1;0rad)
  Solid = false
  Source = -> Face134
  Symmetric = false
FEATURE [Part::MultiFuse] Fusion107  label="plugHousing065"
  Placement = pos=(0,0,0) rot=(0,0,1;1.5708rad)
  Shapes = -> [Revolve137,Revolve142]
FEATURE [Part::MultiFuse] Fusion111  label="plugHousing077"
  Placement = pos=(0,19,0) rot=(0,0,1;3.14159rad)
  Shapes = -> [Fusion110,Fusion107]
FEATURE [Part::MultiFuse] Fusion109  label="plugHousing067"
  Placement = pos=(131.236,0,-0.15) rot=(0,0,1;0rad)
  Shapes = -> [Fusion108,Fusion111]
FEATURE [Part::MultiFuse] Fusion113  label="plugHousing079"
  Shapes = -> [Fillet043,Fusion109]
FEATURE [Part::Feature] Face135
  shape: bbox 3.5 x 17.8 x 2e-07 mm, 1 faces, 0 solids (baked)
FEATURE [Part::Revolution] Revolve143  label="removeToCreateScrewAndThreadedInsertHole049"
  Angle = 360
  Axis = (0,1,0)
  Base = (0,0,0)
  FaceMakerClass = Part::FaceMakerBullseye
  Placement = pos=(12.5,0,10) rot=(0,0,1;0rad)
  Solid = false
  Source = -> Face135
  Symmetric = false
FEATURE [Part::Feature] Face136
  shape: bbox 3.5 x 17.8 x 2e-07 mm, 1 faces, 0 solids (baked)
FEATURE [Part::Revolution] Revolve144  label="removeToCreateScrewAndThreadedInsertHole050"
  Angle = 360
  Axis = (0,1,0)
  Base = (0,0,0)
  FaceMakerClass = Part::FaceMakerBullseye
  Placement = pos=(12.5,0,62) rot=(0,0,1;0rad)
  Solid = false
  Source = -> Face136
  Symmetric = false
FEATURE [Part::Feature] Face137
  shape: bbox 3.5 x 17.8 x 2e-07 mm, 1 faces, 0 solids (baked)
FEATURE [Part::Revolution] Revolve145  label="removeToCreateScrewAndThreadedInsertHole051"
  Angle = 360
  Axis = (0,1,0)
  Base = (0,0,0)
  FaceMakerClass = Part::FaceMakerBullseye
  Placement = pos=(89.5,0,68.5) rot=(0,0,1;0rad)
  Solid = false
  Source = -> Face137
  Symmetric = false
FEATURE [Part::Feature] Face138
  shape: bbox 3.5 x 17.8 x 2e-07 mm, 1 faces, 0 solids (baked)
FEATURE [Part::Revolution] Revolve146  label="removeToCreateScrewAndThreadedInsertHole052"
  Angle = 360
  Axis = (0,1,0)
  Base = (0,0,0)
  FaceMakerClass = Part::FaceMakerBullseye
  Placement = pos=(89.5,0,3.5) rot=(0,0,1;0rad)
  Solid = false
  Source = -> Face138
  Symmetric = false
FEATURE [Part::Feature] Face139
  shape: bbox 3.5 x 17.8 x 2e-07 mm, 1 faces, 0 solids (baked)
FEATURE [Part::Revolution] Revolve147  label="removeToCreateScrewAndThreadedInsertHole053"
  Angle = 360
  Axis = (0,1,0)
  Base = (0,0,0)
  FaceMakerClass = Part::FaceMakerBullseye
  Placement = pos=(109.5,4.7,3.5) rot=(0,0,1;0rad)
  Solid = false
  Source = -> Face139
  Symmetric = false
FEATURE [Part::Feature] Face140
  shape: bbox 3.5 x 17.8 x 2e-07 mm, 1 faces, 0 solids (baked)
FEATURE [Part::Revolution] Revolve148  label="removeToCreateScrewAndThreadedInsertHole054"
  Angle = 360
  Axis = (0,1,0)
  Base = (0,0,0)
  FaceMakerClass = Part::FaceMakerBullseye
  Placement = pos=(109.5,4.7,68.5) rot=(0,0,1;0rad)
  Solid = false
  Source = -> Face140
  Symmetric = false
FEATURE [Part::MultiFuse] Fusion114  label="removeToCreateScrewAndThreadedInsertHole055"
  Shapes = -> [Revolve148,Revolve147,Revolve146,Revolve145,Revolve144,Revolve143]
FEATURE [Part::Cut] Cut047  label="casePillars004"
  Base = -> Cut037
  Tool = -> Fusion114
FEATURE [Part::Feature] Face141
  shape: bbox 3.5 x 17.8 x 2e-07 mm, 1 faces, 0 solids (baked)
FEATURE [Part::Feature] Face142
  shape: bbox 3.5 x 17.8 x 2e-07 mm, 1 faces, 0 solids (baked)
FEATURE [Part::Feature] Face143
  shape: bbox 3.5 x 17.8 x 2e-07 mm, 1 faces, 0 solids (baked)
FEATURE [Part::Revolution] Revolve149  label="removeToCreateScrewAndThreadedInsertHole057"
  Angle = 360
  Axis = (0,1,0)
  Base = (0,0,0)
  FaceMakerClass = Part::FaceMakerBullseye
  Placement = pos=(12.5,0,10) rot=(0,0,1;0rad)
  Solid = false
  Source = -> Face141
  Symmetric = false
FEATURE [Part::Feature] Face144
  shape: bbox 3.5 x 17.8 x 2e-07 mm, 1 faces, 0 solids (baked)
FEATURE [Part::Feature] Face145
  shape: bbox 3.5 x 17.8 x 2e-07 mm, 1 faces, 0 solids (baked)
FEATURE [Part::Feature] Face146
  shape: bbox 3.5 x 17.8 x 2e-07 mm, 1 faces, 0 solids (baked)
FEATURE [Part::Revolution] Revolve150  label="removeToCreateScrewAndThreadedInsertHole058"
  Angle = 360
  Axis = (0,1,0)
  Base = (0,0,0)
  FaceMakerClass = Part::FaceMakerBullseye
  Placement = pos=(12.5,0,62) rot=(0,0,1;0rad)
  Solid = false
  Source = -> Face146
  Symmetric = false
FEATURE [Part::Revolution] Revolve151  label="removeToCreateScrewAndThreadedInsertHole059"
  Angle = 360
  Axis = (0,1,0)
  Base = (0,0,0)
  FaceMakerClass = Part::FaceMakerBullseye
  Placement = pos=(89.5,0,68.5) rot=(0,0,1;0rad)
  Solid = false
  Source = -> Face143
  Symmetric = false
FEATURE [Part::Revolution] Revolve152  label="removeToCreateScrewAndThreadedInsertHole060"
  Angle = 360
  Axis = (0,1,0)
  Base = (0,0,0)
  FaceMakerClass = Part::FaceMakerBullseye
  Placement = pos=(89.5,0,3.5) rot=(0,0,1;0rad)
  Solid = false
  Source = -> Face142
  Symmetric = false
FEATURE [Part::Revolution] Revolve153  label="removeToCreateScrewAndThreadedInsertHole061"
  Angle = 360
  Axis = (0,1,0)
  Base = (0,0,0)
  FaceMakerClass = Part::FaceMakerBullseye
  Placement = pos=(109.5,4.7,3.5) rot=(0,0,1;0rad)
  Solid = false
  Source = -> Face145
  Symmetric = false
FEATURE [Part::Revolution] Revolve154  label="removeToCreateScrewAndThreadedInsertHole062"
  Angle = 360
  Axis = (0,1,0)
  Base = (0,0,0)
  FaceMakerClass = Part::FaceMakerBullseye
  Placement = pos=(109.5,4.7,68.5) rot=(0,0,1;0rad)
  Solid = false
  Source = -> Face144
  Symmetric = false
FEATURE [Part::MultiFuse] Fusion115  label="removeToCreateScrewAndThreadedInsertHole056"
  Shapes = -> [Revolve154,Revolve153,Revolve152,Revolve151,Revolve150,Revolve149]
FEATURE [Part::Feature] Face147
  shape: bbox 9.8 x 26.5 x 2e-07 mm, 1 faces, 0 solids (baked)
FEATURE [Part::Revolution] Revolve155
  Angle = 360
  Axis = (0,1,0)
  Base = (0,0,0)
  FaceMakerClass = Part::FaceMakerBullseye
  Placement = pos=(0,0,0) rot=(0,0,1;1.5708rad)
  Solid = false
  Source = -> Face147
  Symmetric = false
FEATURE [Part::Feature] Face148
  shape: bbox 9.8 x 26.5 x 2e-07 mm, 1 faces, 0 solids (baked)
FEATURE [Part::Revolution] Revolve156
  Angle = 360
  Axis = (0,1,0)
  Base = (0,0,0)
  FaceMakerClass = Part::FaceMakerBullseye
  Placement = pos=(0,0,0) rot=(0,0,1;1.5708rad)
  Solid = false
  Source = -> Face148
  Symmetric = false
FEATURE [Part::MultiFuse] Fusion116
  Placement = pos=(-18,19,36) rot=(0,0,1;0rad)
  Shapes = -> [Revolve156,Revolve155]
FEATURE [Part::Box] Box029  label="Cube016"
  AttacherType = Attacher::AttachEngine3D
  Height = 28
  Length = 3
  Placement = pos=(110.7,19,22) rot=(0,0,1;0rad)
  Width = 15.7
FEATURE [Part::Cylinder] Cylinder046
  Angle = 360
  AttacherType = Attacher::AttachEngine3D
  Height = 10
  Placement = pos=(0,0,36.15) rot=(0,0,1;0rad)
  Radius = 4
FEATURE [Part::Cylinder] Cylinder047
  Angle = 360
  AttacherType = Attacher::AttachEngine3D
  Height = 20
  Placement = pos=(0,0,36.15) rot=(0,0,1;0rad)
  Radius = 10.3
FEATURE [Part::MultiFuse] Fusion117  label="removeToCreteHoleForPlugHousing041"
  Placement = pos=(70,19,36) rot=(0,1,0;1.5708rad)
  Shapes = -> [Cylinder047,Cylinder046]
FEATURE [Part::Cut] Cut049  label="plugHousingTab004"
  Base = -> Box029
  Placement = pos=(-107.4,-14,0) rot=(0,0,1;0rad)
  Tool = -> Fusion117
FEATURE [Part::Box] Box030  label="Cube017"
  AttacherType = Attacher::AttachEngine3D
  Height = 28
  Length = 3
  Placement = pos=(110.7,19,22) rot=(0,0,1;0rad)
  Width = 15.7
FEATURE [Part::Cylinder] Cylinder048
  Angle = 360
  AttacherType = Attacher::AttachEngine3D
  Height = 10
  Placement = pos=(0,0,36.15) rot=(0,0,1;0rad)
  Radius = 4
FEATURE [Part::Cylinder] Cylinder049
  Angle = 360
  AttacherType = Attacher::AttachEngine3D
  Height = 20
  Placement = pos=(0,0,36.15) rot=(0,0,1;0rad)
  Radius = 10.3
FEATURE [Part::MultiFuse] Fusion118  label="removeToCreteHoleForPlugHousing042"
  Placement = pos=(70,19,36) rot=(0,1,0;1.5708rad)
  Shapes = -> [Cylinder049,Cylinder048]
FEATURE [Part::Cut] Cut050  label="plugHousingTab005"
  Base = -> Box030
  Placement = pos=(-107.4,-14,0) rot=(0,0,1;0rad)
  Tool = -> Fusion118
FEATURE [Part::MultiFuse] Fusion119
  Placement = pos=(9.6,23,0) rot=(0,0,1;3.14159rad)
  Shapes = -> [Cut049,Cut050]
FEATURE [Part::Box] Box031  label="Cube018"
  AttacherType = Attacher::AttachEngine3D
  Height = 10
  Length = 3
  Placement = pos=(3.3,4,12) rot=(0,0,1;0rad)
  Width = 10
FEATURE [Part::Fillet] Fillet044
  Base = -> Box031
  Edges = 1 edges r=2: [Edge11]
FEATURE [Part::Box] Box032  label="Cube019"
  AttacherType = Attacher::AttachEngine3D
  Height = 10
  Length = 3
  Placement = pos=(3.3,4,50) rot=(0,0,1;0rad)
  Width = 10
FEATURE [Part::Fillet] Fillet045
  Base = -> Box032
  Edges = 1 edges r=2: [Edge12]
FEATURE [Part::Box] Box033  label="Cube020"
  AttacherType = Attacher::AttachEngine3D
  Height = 28
  Length = 4
  Placement = pos=(5,0,22) rot=(0,0,1;0rad)
  Width = 10
FEATURE [Part::Fillet] Fillet046
  Base = -> Box033
  Edges = 1 edges r=1: [Edge7]
FEATURE [Part::Fillet] Fillet047
  Base = -> Fillet046
  Edges = 1 edges r=2: [Edge5]
FEATURE [Part::Fillet] Fillet048
  Base = -> Fillet047
  Edges = 1 edges r=2: [Edge2]
FEATURE [Part::Cylinder] Cylinder050
  Angle = 360
  AttacherType = Attacher::AttachEngine3D
  Height = 20
  Placement = pos=(0,0,36.15) rot=(0,0,1;0rad)
  Radius = 8.2
FEATURE [Part::Cylinder] Cylinder051
  Angle = 360
  AttacherType = Attacher::AttachEngine3D
  Height = 10
  Placement = pos=(0,0,36.15) rot=(0,0,1;0rad)
  Radius = 4
FEATURE [Part::MultiFuse] Fusion120  label="removeToCreteHoleForPlugHousing043"
  Placement = pos=(-42,19,36) rot=(0,1,0;1.5708rad)
  Shapes = -> [Cylinder050,Cylinder051]
FEATURE [Sketcher::SketchObject] Sketch067  label="topSketch018"
  FullyConstrained = true
  sketch-geometry (4):
    g0: LineSegment StartX=16.8446 StartY=31.512 StartZ=0 EndX=16.3251 EndY=34.4666 EndZ=0
    g1: ArcOfCircle CenterX=19 CenterY=19.2524 CenterZ=0 NormalX=0 NormalY=0 NormalZ=1 AngleXU=0 Radius=15.4476 StartAngle=1.74483 EndAngle=2.72717
    g2: ArcOfCircle CenterX=19 CenterY=19.2524 CenterZ=0 NormalX=0 NormalY=0 NormalZ=1 AngleXU=0 Radius=12.4476 StartAngle=1.74483 EndAngle=2.73189
    g3: LineSegment StartX=4.86004 StartY=25.4725 StartZ=0 EndX=7.58253 EndY=24.2107 EndZ=0
  constraints (7):
    c: Block(g0)
    c: Coincident(g1,g0)
    c: Coincident(g2,g0)
    c: Coincident(g3,g1)
    c: Coincident(g3,g2)
    c: Block(g1)
    c: Block(g2)
FEATURE [Part::Extrusion] Extrude058
  Base = -> Sketch067
  Dir = (0,0,1)
  DirMode = 2
  FaceMakerClass = Part::FaceMakerBullseye
  LengthFwd = 10
  LengthRev = 0
  Placement = pos=(0,0,31) rot=(0,0,1;0rad)
  Solid = true
  Symmetric = false
FEATURE [Part::Cut] Cut051
  Base = -> Extrude058
  Tool = -> Fusion120
FEATURE [Part::Fillet] Fillet049
  Base = -> Cut051
  Edges = 1 edges r=2: [Edge1]
FEATURE [Part::Fillet] Fillet050
  Base = -> Fillet049
  Edges = 1 edges r=2.5: [Edge1]
FEATURE [Part::Fillet] Fillet051
  Base = -> Fillet050
  Edges = 1 edges r=2.5: [Edge2]
FEATURE [Part::MultiFuse] Fusion121  label="wireHolder003"
  Shapes = -> [Fusion116,Fillet051]
FEATURE [Part::MultiFuse] Fusion122
  Shapes = -> [Fillet045,Fusion121]
FEATURE [Part::MultiFuse] Fusion123  label="wireHolder004"
  Shapes = -> [Fusion122,Fillet048]
FEATURE [Part::MultiFuse] Fusion124  label="wireHolder005"
  Shapes = -> [Fillet044,Fusion119,Fusion123]
FEATURE [Sketcher::SketchObject] Sketch068  label="topSketch019"
  FullyConstrained = true
  sketch-geometry (6):
    g0: LineSegment StartX=19 StartY=38 StartZ=0 EndX=117 EndY=38 EndZ=0
    g1: ArcOfCircle CenterX=19 CenterY=19 CenterZ=0 NormalX=0 NormalY=0 NormalZ=1 AngleXU=0 Radius=19 StartAngle=1.5708 EndAngle=3.14159
    g2: LineSegment StartX=117 StartY=38 StartZ=0 EndX=117 EndY=19 EndZ=0
    g3: LineSegment StartX=98 StartY=1.0161e-12 StartZ=0 EndX=5.22862e-06 EndY=1.0161e-12 EndZ=0
    g4: LineSegment StartX=5.22862e-06 StartY=19 StartZ=0 EndX=5.22862e-06 EndY=1.0161e-12 EndZ=0
    g5: ArcOfCircle CenterX=98 CenterY=19 CenterZ=0 NormalX=0 NormalY=0 NormalZ=1 AngleXU=0 Radius=19 StartAngle=4.71239 EndAngle=6.28319
  constraints (16):
    c: Horizontal(g0)
    c: Distance(g0) = 98
    c: Coincident(g1,g0)
    c: Block(g1)
    c: Coincident(g2,g0)
    c: Vertical(g2)
    c: Distance(g2) = 19
    c: Horizontal(g3)
    c: Coincident(g4,g1)
    c: Vertical(g4)
    c: Coincident(g3,g4)
    c: Block(g3)
    c: Coincident(g5,g2)
    c: Coincident(g5,g3)
    c: Block(g0)
    c: Block(g5)
FEATURE [Part::Extrusion] Extrude059  label="sideA002"
  Base = -> Sketch068
  Dir = (0,0,1)
  DirMode = 2
  FaceMakerClass = Part::FaceMakerBullseye
  LengthFwd = 3
  LengthRev = 0
  Placement = pos=(0,0,-2.7) rot=(0,0,1;0rad)
  Solid = true
  Symmetric = false
FEATURE [Sketcher::SketchObject] Sketch069  label="topSketch020"
  FullyConstrained = true
  sketch-geometry (6):
    g0: LineSegment StartX=19 StartY=38 StartZ=0 EndX=117 EndY=38 EndZ=0
    g1: ArcOfCircle CenterX=19 CenterY=19 CenterZ=0 NormalX=0 NormalY=0 NormalZ=1 AngleXU=0 Radius=19 StartAngle=1.5708 EndAngle=3.14159
    g2: LineSegment StartX=117 StartY=38 StartZ=0 EndX=117 EndY=19 EndZ=0
    g3: LineSegment StartX=98 StartY=1.0161e-12 StartZ=0 EndX=5.22862e-06 EndY=1.0161e-12 EndZ=0
    g4: LineSegment StartX=5.22862e-06 StartY=19 StartZ=0 EndX=5.22862e-06 EndY=1.0161e-12 EndZ=0
    g5: ArcOfCircle CenterX=98 CenterY=19 CenterZ=0 NormalX=0 NormalY=0 NormalZ=1 AngleXU=0 Radius=19 StartAngle=4.71239 EndAngle=6.28319
  constraints (16):
    c: Horizontal(g0)
    c: Distance(g0) = 98
    c: Coincident(g1,g0)
    c: Block(g1)
    c: Coincident(g2,g0)
    c: Vertical(g2)
    c: Distance(g2) = 19
    c: Horizontal(g3)
    c: Coincident(g4,g1)
    c: Vertical(g4)
    c: Coincident(g3,g4)
    c: Block(g3)
    c: Coincident(g5,g2)
    c: Coincident(g5,g3)
    c: Block(g0)
    c: Block(g5)
FEATURE [Part::Extrusion] Extrude060  label="sideB002"
  Base = -> Sketch069
  Dir = (0,0,1)
  DirMode = 2
  FaceMakerClass = Part::FaceMakerBullseye
  LengthFwd = 3
  LengthRev = 0
  Placement = pos=(0,0,71.7) rot=(0,0,1;0rad)
  Solid = true
  Symmetric = false
FEATURE [Part::MultiFuse] Fusion127  label="removeFromBottom001"
  Placement = pos=(2,0,0) rot=(0,0,1;0rad)
  Shapes = -> [Extrude059,Extrude060]
FEATURE [Part::Cylinder] Cylinder052
  Angle = 360
  AttacherType = Attacher::AttachEngine3D
  Height = 20
  Placement = pos=(0,0,36.15) rot=(0,0,1;0rad)
  Radius = 14
FEATURE [Part::Cylinder] Cylinder053
  Angle = 360
  AttacherType = Attacher::AttachEngine3D
  Height = 10
  Placement = pos=(0,0,36.15) rot=(0,0,1;0rad)
  Radius = 4
FEATURE [Part::MultiFuse] Fusion128  label="removeToCreteHoleForPlugHousing044"
  Placement = pos=(70,19,36) rot=(0,1,0;1.5708rad)
  Shapes = -> [Cylinder052,Cylinder053]
FEATURE [Part::Cut] Cut052  label="bottom011"
  Base = -> Extrude043
  Tool = -> Fusion128
FEATURE [Part::Cut] Cut054  label="bottom012"
  Base = -> Cut052
  Tool = -> Fusion115
FEATURE [Sketcher::SketchObject] Sketch070
  FullyConstrained = true
  Placement = pos=(117,19,0) rot=(0.57735,0.57735,0.57735;2.0944rad)
  sketch-geometry (48):
    g0: LineSegment StartX=-49.19 StartY=69.25 StartZ=0 EndX=-49.19 EndY=66.25 EndZ=0
    g1: LineSegment StartX=-49.19 StartY=63.5 StartZ=0 EndX=-49.19 EndY=60.5 EndZ=0
    g2: LineSegment StartX=-49.19 StartY=57.75 StartZ=0 EndX=-49.19 EndY=54.75 EndZ=0
    g3: LineSegment StartX=-49.19 StartY=52 StartZ=0 EndX=-49.19 EndY=49 EndZ=0
    g4: LineSegment StartX=-49.19 StartY=46.25 StartZ=0 EndX=-49.19 EndY=43.25 EndZ=0
    g5: LineSegment StartX=-49.19 StartY=40.5 StartZ=0 EndX=-49.19 EndY=37.5 EndZ=0
    g6: LineSegment StartX=-49.19 StartY=34.5 StartZ=0 EndX=-49.19 EndY=31.5 EndZ=0
    g7: LineSegment StartX=-49.19 StartY=28.75 StartZ=0 EndX=-49.19 EndY=25.75 EndZ=0
    g8: LineSegment StartX=-49.19 StartY=23 StartZ=0 EndX=-49.19 EndY=20 EndZ=0
    g9: LineSegment StartX=-49.19 StartY=17.25 StartZ=0 EndX=-49.19 EndY=14.25 EndZ=0
    g10: LineSegment StartX=-49.19 StartY=11.5 StartZ=0 EndX=-49.19 EndY=8.5 EndZ=0
    g11: LineSegment StartX=-49.19 StartY=5.75 StartZ=0 EndX=-49.19 EndY=2.75 EndZ=0
    g12: ArcOfCircle CenterX=-1.5 CenterY=67.75 CenterZ=0 NormalX=0 NormalY=0 NormalZ=1 AngleXU=0 Radius=1.5 StartAngle=4.71239 EndAngle=7.85398
    g13: ArcOfCircle CenterX=-1.5 CenterY=62 CenterZ=0 NormalX=0 NormalY=0 NormalZ=1 AngleXU=0 Radius=1.5 StartAngle=4.71239 EndAngle=7.85398
    g14: ArcOfCircle CenterX=-1.5 CenterY=56.25 CenterZ=0 NormalX=0 NormalY=0 NormalZ=1 AngleXU=0 Radius=1.5 StartAngle=4.71239 EndAngle=7.85398
    g15: ArcOfCircle CenterX=-11.49 CenterY=50.5 CenterZ=0 NormalX=0 NormalY=0 NormalZ=1 AngleXU=0 Radius=1.5 StartAngle=4.71239 EndAngle=7.85398
    g16: ArcOfCircle CenterX=-16.28 CenterY=44.75 CenterZ=0 NormalX=0 NormalY=0 NormalZ=1 AngleXU=0 Radius=1.5 StartAngle=4.71239 EndAngle=7.85398
    g17: ArcOfCircle CenterX=-18.2337 CenterY=39 CenterZ=0 NormalX=0 NormalY=0 NormalZ=1 AngleXU=0 Radius=1.5 StartAngle=4.71485 EndAngle=7.85398
    g18: ArcOfCircle CenterX=-16.2837 CenterY=27.25 CenterZ=0 NormalX=0 NormalY=0 NormalZ=1 AngleXU=0 Radius=1.5 StartAngle=4.71485 EndAngle=7.85398
    g19: ArcOfCircle CenterX=-18.2337 CenterY=33 CenterZ=0 NormalX=0 NormalY=0 NormalZ=1 AngleXU=0 Radius=1.5 StartAngle=4.71485 EndAngle=7.85398
    g20: ArcOfCircle CenterX=-11.49 CenterY=21.5 CenterZ=0 NormalX=0 NormalY=0 NormalZ=1 AngleXU=0 Radius=1.5 StartAngle=4.71239 EndAngle=7.85398
    g21: ArcOfCircle CenterX=-1.5 CenterY=4.25 CenterZ=0 NormalX=0 NormalY=0 NormalZ=1 AngleXU=0 Radius=1.5 StartAngle=4.71239 EndAngle=7.85398
    g22: ArcOfCircle CenterX=-1.5 CenterY=10 CenterZ=0 NormalX=0 NormalY=0 NormalZ=1 AngleXU=0 Radius=1.5 StartAngle=4.71239 EndAngle=7.85398
    g23: ArcOfCircle CenterX=-1.5 CenterY=15.75 CenterZ=0 NormalX=0 NormalY=0 NormalZ=1 AngleXU=0 Radius=1.5 StartAngle=4.71239 EndAngle=7.85398
    g24: LineSegment StartX=-49.19 StartY=69.25 StartZ=0 EndX=-1.5 EndY=69.25 EndZ=0
    g25: LineSegment StartX=-49.19 StartY=66.25 StartZ=0 EndX=-1.5 EndY=66.25 EndZ=0
    g26: LineSegment StartX=-49.19 StartY=63.5 StartZ=0 EndX=-1.5 EndY=63.5 EndZ=0
    g27: LineSegment StartX=-49.19 StartY=60.5 StartZ=0 EndX=-1.5 EndY=60.5 EndZ=0
    g28: LineSegment StartX=-49.19 StartY=57.75 StartZ=0 EndX=-1.5 EndY=57.75 EndZ=0
    g29: LineSegment StartX=-49.19 StartY=54.75 StartZ=0 EndX=-1.5 EndY=54.75 EndZ=0
    g30: LineSegment StartX=-49.19 StartY=52 StartZ=0 EndX=-11.49 EndY=52 EndZ=0
    g31: LineSegment StartX=-49.19 StartY=49 StartZ=0 EndX=-11.49 EndY=49 EndZ=0
    g32: LineSegment StartX=-49.19 StartY=46.25 StartZ=0 EndX=-16.28 EndY=46.25 EndZ=0
    g33: LineSegment StartX=-49.19 StartY=43.25 StartZ=0 EndX=-16.28 EndY=43.25 EndZ=0
    g34: LineSegment StartX=-49.19 StartY=40.5 StartZ=0 EndX=-18.2337 EndY=40.5 EndZ=0
    g35: LineSegment StartX=-49.19 StartY=37.5 StartZ=0 EndX=-18.23 EndY=37.5 EndZ=0
    g36: LineSegment StartX=-49.19 StartY=34.5 StartZ=0 EndX=-18.2337 EndY=34.5 EndZ=0
    g37: LineSegment StartX=-49.19 StartY=31.5 StartZ=0 EndX=-18.23 EndY=31.5 EndZ=0
    g38: LineSegment StartX=-49.19 StartY=28.75 StartZ=0 EndX=-16.2837 EndY=28.75 EndZ=0
    g39: LineSegment StartX=-49.19 StartY=25.75 StartZ=0 EndX=-16.28 EndY=25.75 EndZ=0
    g40: LineSegment StartX=-49.19 StartY=23 StartZ=0 EndX=-11.49 EndY=23 EndZ=0
    g41: LineSegment StartX=-49.19 StartY=20 StartZ=0 EndX=-11.49 EndY=20 EndZ=0
    g42: LineSegment StartX=-49.19 StartY=17.25 StartZ=0 EndX=-1.5 EndY=17.25 EndZ=0
    g43: LineSegment StartX=-49.19 StartY=14.25 StartZ=0 EndX=-1.5 EndY=14.25 EndZ=0
    g44: LineSegment StartX=-49.19 StartY=11.5 StartZ=0 EndX=-1.5 EndY=11.5 EndZ=0
    g45: LineSegment StartX=-49.19 StartY=8.5 StartZ=0 EndX=-1.5 EndY=8.5 EndZ=0
    g46: LineSegment StartX=-49.19 StartY=5.75 StartZ=0 EndX=-1.5 EndY=5.75 EndZ=0
    g47: LineSegment StartX=-49.19 StartY=2.75 StartZ=0 EndX=-1.5 EndY=2.75 EndZ=0
  constraints (120):
    c: Vertical(g0)
    c: Distance(g0) = 3
    c: Block(g0)
    c: Vertical(g1)
    c: Distance(g1) = 3
    c: Vertical(g2)
    c: Equal(g0,g2) = 3
    c: Block(g2)
    c: Vertical(g3)
    c: Equal(g1,g3) = 3
    c: Vertical(g4)
    c: Equal(g0,g4) = 3
    c: Block(g4)
    c: Vertical(g5)
    c: Equal(g1,g5) = 3
    c: Vertical(g6)
    c: Equal(g0,g6) = 3
    c: Block(g6)
    c: Vertical(g7)
    c: Equal(g1,g7) = 3
    c: Vertical(g8)
    c: Equal(g0,g8) = 3
    c: Block(g8)
    c: Vertical(g9)
    c: Equal(g1,g9) = 3
    c: Vertical(g10)
    c: Equal(g0,g10) = 3
    c: Block(g10)
    c: Vertical(g11)
    c: Equal(g1,g11) = 3
    c: Block(g12)
    c: Block(g13)
    c: Block(g14)
    c: Block(g15)
    c: Block(g16)
    c: Block(g17)
    c: Block(g18)
    c: Block(g19)
    c: Block(g20)
    c: Block(g21)
    c: Block(g22)
    c: Block(g23)
    c: Block(g11)
    c: Block(g9)
    c: Block(g7)
    c: Block(g5)
    c: Block(g3)
    c: Block(g1)
    c: Coincident(g24,g0)
    c: Coincident(g24,g12)
    c: Horizontal(g24)
    c: Coincident(g25,g0)
    c: Coincident(g25,g12)
    c: Horizontal(g25)
    c: Coincident(g26,g1)
    c: Coincident(g26,g13)
    c: Horizontal(g26)
    c: Coincident(g27,g1)
    c: Coincident(g27,g13)
    c: Horizontal(g27)
    c: Coincident(g28,g2)
    c: Coincident(g28,g14)
    c: Horizontal(g28)
    c: Coincident(g29,g2)
    c: Coincident(g29,g14)
    c: Horizontal(g29)
    c: Coincident(g30,g3)
    c: Coincident(g30,g15)
    c: Horizontal(g30)
    c: Coincident(g31,g3)
    c: Coincident(g31,g15)
    c: Horizontal(g31)
    c: Coincident(g32,g4)
    c: Coincident(g32,g16)
    c: Horizontal(g32)
    c: Coincident(g33,g4)
    c: Coincident(g33,g16)
    c: Horizontal(g33)
    c: Coincident(g34,g5)
    c: Coincident(g34,g17)
    c: Horizontal(g34)
    c: Coincident(g35,g5)
    c: Coincident(g35,g17)
    c: Horizontal(g35)
    c: Coincident(g36,g6)
    c: Coincident(g36,g19)
    c: Horizontal(g36)
    c: Coincident(g37,g6)
    c: Coincident(g37,g19)
    c: Horizontal(g37)
    c: Coincident(g38,g7)
    c: Coincident(g38,g18)
    c: Horizontal(g38)
    c: Coincident(g39,g7)
    c: Coincident(g39,g18)
    c: Horizontal(g39)
    c: Coincident(g40,g8)
    c: Coincident(g40,g20)
    c: Horizontal(g40)
    c: Coincident(g41,g8)
    c: Coincident(g41,g20)
    c: Horizontal(g41)
    c: Coincident(g42,g9)
    c: Coincident(g42,g23)
    c: Horizontal(g42)
    c: Coincident(g43,g9)
    c: Coincident(g43,g23)
    c: Horizontal(g43)
    c: Coincident(g44,g10)
    c: Coincident(g44,g22)
    c: Horizontal(g44)
    c: Coincident(g45,g10)
    c: Coincident(g45,g22)
    c: Horizontal(g45)
    c: Coincident(g46,g11)
    c: Coincident(g46,g21)
    c: Horizontal(g46)
    c: Coincident(g47,g11)
    c: Coincident(g47,g21)
    c: Horizontal(g47)
FEATURE [Part::Extrusion] Extrude061
  Base = -> Sketch070
  Dir = (1,0,0)
  DirMode = 2
  FaceMakerClass = Part::FaceMakerBullseye
  LengthFwd = 23
  LengthRev = 0
  Placement = pos=(-19,0,0) rot=(0,0,1;0rad)
  Solid = true
  Symmetric = false
FEATURE [Part::Fillet] Fillet052  label="removeToCreateVentalationHoles002"
  Base = -> Extrude061
  Edges = <same value as first occurrence — deduplicated (x6 in doc)>
  Placement = pos=(7,0.02,0) rot=(0,0,1;0rad)
FEATURE [Part::MultiFuse] Fusion130  label="bottom013"
  Shapes = -> [Cut054,Cut034]
FEATURE [Part::Cut] Cut055
  Base = -> Fusion130
  Tool = -> Fillet052
FEATURE [Part::Cylinder] Cylinder054
  Angle = 360
  AttacherType = Attacher::AttachEngine3D
  Height = 20
  Placement = pos=(0,0,36.15) rot=(0,0,1;0rad)
  Radius = 4
FEATURE [Sketcher::SketchObject] Sketch071  label="bottomSketch002"
  FullyConstrained = true
  sketch-geometry (32):
    g0: LineSegment StartX=3.3 StartY=-6.03275e-07 StartZ=0 EndX=98 EndY=-6.03275e-07 EndZ=0
    g1: ArcOfCircle CenterX=98 CenterY=19 CenterZ=0 NormalX=0 NormalY=0 NormalZ=1 AngleXU=0 Radius=19 StartAngle=4.71239 EndAngle=5.71103
    g2: LineSegment StartX=6.3 StartY=8 StartZ=0 EndX=3.3 EndY=8 EndZ=0
    g3: LineSegment StartX=3.3 StartY=8 StartZ=0 EndX=3.3 EndY=-6.03275e-07 EndZ=0
    g4: ArcOfCircle CenterX=8.3 CenterY=5 CenterZ=0 NormalX=0 NormalY=0 NormalZ=1 AngleXU=0 Radius=2 StartAngle=3.14159 EndAngle=4.71239
    g5: LineSegment StartX=6.3 StartY=8 StartZ=0 EndX=6.3 EndY=5 EndZ=0
    g6: ArcOfCircle CenterX=98 CenterY=19 CenterZ=0 NormalX=0 NormalY=0 NormalZ=1 AngleXU=0 Radius=12.7 StartAngle=4.71239 EndAngle=6.28319
    g7: LineSegment StartX=94.7 StartY=3 StartZ=0 EndX=8.3 EndY=3 EndZ=0
    g8-g12: Circle x5 (B-spline internal-alignment scaffolding for g13; pole/knot coordinates omitted)
    g13: BSplineCurve PolesCount=5 KnotsCount=3 Degree=3 IsPeriodic=0
    g14: GeomPoint X=98 Y=6.3 Z=0
    g15: GeomPoint X=96.3938 Y=4.71946 Z=0
    g16: GeomPoint X=94.7 Y=3 Z=0
    g17-g23: Circle x7 (B-spline internal-alignment scaffolding for g24; pole/knot coordinates omitted)
    g24: BSplineCurve PolesCount=7 KnotsCount=5 Degree=3 IsPeriodic=0
    g25-g29: GeomPoint x5 (B-spline internal-alignment scaffolding for g24; pole/knot coordinates omitted)
    g30: ArcOfCircle CenterX=98 CenterY=19 CenterZ=0 NormalX=0 NormalY=0 NormalZ=1 AngleXU=0 Radius=15.7 StartAngle=5.81226 EndAngle=6.28319
    g31: LineSegment StartX=110.7 StartY=19 StartZ=0 EndX=113.7 EndY=19 EndZ=0
  constraints (41):
    c: Horizontal(g0)
    c: Coincident(g1,g0)
    c: Block(g1)
    c: Horizontal(g2)
    c: Distance(g2) = 3
    c: Coincident(g3,g2)
    c: Vertical(g3)
    c: Coincident(g3,g0)
    c: Block(g4)
    c: Block(g2)
    c: Coincident(g5,g2)
    c: Coincident(g5,g4)
    c: Vertical(g5)
    c: Coincident(g6,g1)
    c: Block(g6)
    c: Coincident(g7,g4)
    c: Horizontal(g7)
    c: Block(g0)
    c: Block(g7)
    c: Block(g3)
    c: Coincident(g13,g6)
    c: Weight(g8) = 1
    c: Equal(g8, g9-g12) x4
    c: Coincident(g13,g7)
    c: InternalAlignment(g8-g12 -> g13) x5
    c: InternalAlignment(g14,g13)
    c: InternalAlignment(g15,g13)
    c: InternalAlignment(g16,g13)
    c: Block(g13)
    c: Weight(g17) = 1
    c: Equal(g17, g18-g23) x6
    c: Coincident(g24,g1)
    c: InternalAlignment(g17-g23 -> g24) x7
    c: InternalAlignment(g25-g29 -> g24) x5
    c: Block(g24)
    c: Coincident(g30,g24)
    c: Coincident(g31,g6)
    c: Coincident(g31,g30)
    c: Horizontal(g31)
    c: Block(g31)
    c: Block(g30)
FEATURE [Part::Extrusion] Extrude062  label="bottom014"
  Base = -> Sketch071
  Dir = (0,0,1)
  DirMode = 2
  FaceMakerClass = Part::FaceMakerBullseye
  LengthFwd = 71.4
  LengthRev = 0
  Placement = pos=(0,0,0.3) rot=(0,0,1;0rad)
  Solid = true
  Symmetric = false
FEATURE [Part::Fillet] Fillet054
  Base = -> Extrude062
  Edges = 1 edges r=2.4: [Edge17]
FEATURE [Part::Fillet] Fillet055  label="bottom015"
  Base = -> Fillet054
  Edges = 1 edges r=2.4: [Edge36]
FEATURE [Part::Cylinder] Cylinder055
  Angle = 360
  AttacherType = Attacher::AttachEngine3D
  Height = 10
  Placement = pos=(0,0,36.15) rot=(0,0,1;0rad)
  Radius = 4
FEATURE [Part::MultiFuse] Fusion131  label="removeToCreateHoleForPlugHousing002"
  Placement = pos=(70,19,36.15) rot=(0,1,0;1.5708rad)
  Shapes = -> [Cylinder054,Cylinder055]
FEATURE [Part::Cut] Cut056  label="Bottom001"
  Base = -> Fillet055
  Placement = pos=(9,0,0) rot=(0,0,1;0rad)
  Tool = -> Fusion131
FEATURE [Part::Cut] Cut057
  Base = -> Cut055
  Tool = -> Cut056
FEATURE [Sketcher::SketchObject] Sketch072  label="topSketch021"
  FullyConstrained = true
  sketch-geometry (4):
    g0: ArcOfCircle CenterX=105 CenterY=19 CenterZ=0 NormalX=0 NormalY=0 NormalZ=1 AngleXU=0 Radius=20.6155 StartAngle=5.54125 EndAngle=6.28319
    g1: ArcOfCircle CenterX=105 CenterY=19 CenterZ=0 NormalX=0 NormalY=0 NormalZ=1 AngleXU=0 Radius=13 StartAngle=5.54125 EndAngle=6.28319
    g2: LineSegment StartX=118 StartY=19 StartZ=0 EndX=125.616 EndY=19 EndZ=0
    g3: LineSegment StartX=114.583 StartY=10.2157 StartZ=0 EndX=120.197 EndY=5.06982 EndZ=0
  constraints (7):
    c: Block(g0)
    c: Block(g1)
    c: Coincident(g2,g1)
    c: Coincident(g2,g0)
    c: Horizontal(g2)
    c: Coincident(g3,g1)
    c: Coincident(g3,g0)
FEATURE [Part::Extrusion] Extrude063  label="bottomPlugHousingBit003"
  Base = -> Sketch072
  Dir = (0,0,1)
  DirMode = 2
  FaceMakerClass = Part::FaceMakerBullseye
  LengthFwd = 72
  LengthRev = 0
  Solid = true
  Symmetric = false
FEATURE [Part::Cylinder] Cylinder056
  Angle = 360
  AttacherType = Attacher::AttachEngine3D
  Height = 20
  Placement = pos=(0,0,36.15) rot=(0,0,1;0rad)
  Radius = 14.3
FEATURE [Part::Cylinder] Cylinder057
  Angle = 360
  AttacherType = Attacher::AttachEngine3D
  Height = 10
  Placement = pos=(0,0,36.15) rot=(0,0,1;0rad)
  Radius = 4
FEATURE [Part::Box] Box034  label="removeToCreteHoleForPlugHousing047"
  AttacherType = Attacher::AttachEngine3D
  Height = 28.6
  Length = 20
  Placement = pos=(106.15,0,21.7) rot=(0,0,1;0rad)
  Width = 19
FEATURE [Part::Cylinder] Cylinder058
  Angle = 360
  AttacherType = Attacher::AttachEngine3D
  Height = 20
  Placement = pos=(0,0,36.15) rot=(0,0,1;0rad)
  Radius = 14.3
FEATURE [Part::Cylinder] Cylinder059
  Angle = 360
  AttacherType = Attacher::AttachEngine3D
  Height = 10
  Placement = pos=(0,0,36.15) rot=(0,0,1;0rad)
  Radius = 4
FEATURE [Part::MultiFuse] Fusion134  label="removeToCreteHoleForPlugHousing046"
  Placement = pos=(70,19,36) rot=(0,1,0;1.5708rad)
  Shapes = -> [Cylinder058,Cylinder059]
FEATURE [Part::Cylinder] Cylinder060
  Angle = 360
  AttacherType = Attacher::AttachEngine3D
  Height = 20
  Placement = pos=(0,0,36.15) rot=(0,0,1;0rad)
  Radius = 14
FEATURE [Part::Cylinder] Cylinder061
  Angle = 360
  AttacherType = Attacher::AttachEngine3D
  Height = 10
  Placement = pos=(0,0,36.15) rot=(0,0,1;0rad)
  Radius = 4
FEATURE [Part::MultiFuse] Fusion135  label="removeToCreteHoleForPlugHousing048"
  Placement = pos=(70,19,36) rot=(0,1,0;1.5708rad)
  Shapes = -> [Cylinder060,Cylinder061]
FEATURE [Part::Box] Box035  label="removeToCreteHoleForPlugHousing049"
  AttacherType = Attacher::AttachEngine3D
  Height = 28.6
  Length = 20
  Placement = pos=(106.15,0,21.7) rot=(0,0,1;0rad)
  Width = 19
FEATURE [Part::MultiFuse] Fusion133  label="removeToCreteHoleForPlugHousing045"
  Placement = pos=(0,0,-28.3) rot=(0,0,1;0rad)
  Shapes = -> [Box035,Fusion134]
FEATURE [Part::MultiFuse] Fusion138  label="removeToCreteHoleForPlugHousing051"
  Placement = pos=(70,19,36) rot=(0,1,0;1.5708rad)
  Shapes = -> [Cylinder056,Cylinder057]
FEATURE [Part::MultiFuse] Fusion137  label="removeToCreteHoleForPlugHousing050"
  Placement = pos=(0,0,28.3) rot=(0,0,1;0rad)
  Shapes = -> [Box034,Fusion138]
FEATURE [Part::MultiFuse] Fusion132  label="removeToCreatePlugHousingBottomBit002"
  Shapes = -> [Fusion133,Fusion137]
FEATURE [Part::MultiFuse] Fusion136  label="removeToCreatePlugHousingBottomBit003"
  Shapes = -> [Fusion135,Fusion132]
FEATURE [Part::Cut] Cut058  label="bottomPlugHousingBit002"
  Base = -> Extrude063
  Placement = pos=(-0.09,0,0) rot=(0,0,1;0rad)
  Tool = -> Fusion136
FEATURE [Sketcher::SketchObject] Sketch073  label="bottomSketch003"
  FullyConstrained = true
  sketch-geometry (45):
    g0: LineSegment StartX=6.29999 StartY=8 StartZ=0 EndX=3.29999 EndY=8 EndZ=0
    g1: LineSegment StartX=3.29999 StartY=8 StartZ=0 EndX=3.29999 EndY=-6.03275e-07 EndZ=0
    g2: ArcOfCircle CenterX=8.29999 CenterY=5 CenterZ=0 NormalX=0 NormalY=0 NormalZ=1 AngleXU=0 Radius=2 StartAngle=3.14159 EndAngle=4.71239
    g3: LineSegment StartX=6.29999 StartY=8 StartZ=0 EndX=6.29999 EndY=5 EndZ=0
    g4: ArcOfCircle CenterX=105 CenterY=19 CenterZ=0 NormalX=0 NormalY=0 NormalZ=1 AngleXU=0 Radius=12.7 StartAngle=4.71239 EndAngle=5.94289
    g5-g11: Circle x7 (B-spline internal-alignment scaffolding for g12; pole/knot coordinates omitted)
    g12: BSplineCurve PolesCount=7 KnotsCount=5 Degree=3 IsPeriodic=0
    g13-g17: GeomPoint x5 (B-spline internal-alignment scaffolding for g12; pole/knot coordinates omitted)
    g18: ArcOfCircle CenterX=105 CenterY=19 CenterZ=0 NormalX=0 NormalY=0 NormalZ=1 AngleXU=0 Radius=15.7 StartAngle=5.81226 EndAngle=6.28319
    g19: BSplineCurve PolesCount=5 KnotsCount=3 Degree=3 IsPeriodic=0
    g20: LineSegment StartX=8.29999 StartY=3 StartZ=0 EndX=101.7 EndY=3 EndZ=0
    g21: LineSegment StartX=3.29999 StartY=-6.03275e-07 StartZ=0 EndX=105 EndY=-6.03275e-07 EndZ=0
    g22: LineSegment StartX=120.974 StartY=8.71251 StartZ=0 EndX=122.332 EndY=7.83778 EndZ=0
    g23: LineSegment StartX=105 StartY=-6.03274e-07 StartZ=0 EndX=113 EndY=-6.03274e-07 EndZ=0
    g24: ArcOfCircle CenterX=105 CenterY=19 CenterZ=0 NormalX=0 NormalY=0 NormalZ=1 AngleXU=0 Radius=20.6155 StartAngle=5.11091 EndAngle=5.71103
    g25: ArcOfCircle CenterX=117.7 CenterY=19 CenterZ=0 NormalX=0 NormalY=0 NormalZ=1 AngleXU=0 Radius=3 StartAngle=1.2e-15 EndAngle=2.10468
    g26: Circle CenterX=116.345 CenterY=16.3232 CenterZ=0 NormalX=0 NormalY=0 NormalZ=1 AngleXU=0 Radius=1
    g27: Circle CenterX=117.24 CenterY=15.7584 CenterZ=0 NormalX=0 NormalY=0 NormalZ=1 AngleXU=0 Radius=1
    g28: Circle CenterX=116.972 CenterY=14.7612 CenterZ=0 NormalX=0 NormalY=0 NormalZ=1 AngleXU=0 Radius=1
    g29: BSplineCurve PolesCount=3 KnotsCount=2 Degree=2 IsPeriodic=0
    g30: GeomPoint X=116.345 Y=16.3232 Z=0
    g31: GeomPoint X=116.972 Y=14.7612 Z=0
    g32: Circle CenterX=115.828 CenterY=17.157 CenterZ=0 NormalX=0 NormalY=0 NormalZ=1 AngleXU=0 Radius=1
    g33: Circle CenterX=115.841 CenterY=16.639 CenterZ=0 NormalX=0 NormalY=0 NormalZ=1 AngleXU=0 Radius=1
    g34: Circle CenterX=116.345 CenterY=16.3232 CenterZ=0 NormalX=0 NormalY=0 NormalZ=1 AngleXU=0 Radius=1
    g35: BSplineCurve PolesCount=3 KnotsCount=2 Degree=2 IsPeriodic=0
    g36: GeomPoint X=115.828 Y=17.157 Z=0
    g37: GeomPoint X=116.345 Y=16.3232 Z=0
    g38: LineSegment StartX=115.828 StartY=17.157 StartZ=0 EndX=115.828 EndY=20.8307 EndZ=0
    g39: Circle CenterX=115.828 CenterY=20.8307 CenterZ=0 NormalX=0 NormalY=0 NormalZ=1 AngleXU=0 Radius=1
    g40: Circle CenterX=115.831 CenterY=21.3396 CenterZ=0 NormalX=0 NormalY=0 NormalZ=1 AngleXU=0 Radius=1
    g41: Circle CenterX=116.173 CenterY=21.5825 CenterZ=0 NormalX=0 NormalY=0 NormalZ=1 AngleXU=0 Radius=1
    g42: BSplineCurve PolesCount=3 KnotsCount=2 Degree=2 IsPeriodic=0
    g43: GeomPoint X=115.828 Y=20.8307 Z=0
    g44: GeomPoint X=116.173 Y=21.5825 Z=0
  constraints (70):
    c: Horizontal(g0)
    c: Distance(g0) = 3
    c: Coincident(g1,g0)
    c: Vertical(g1)
    c: Block(g2)
    c: Block(g0)
    c: Coincident(g3,g0)
    c: Coincident(g3,g2)
    c: Vertical(g3)
    c: Block(g1)
    c: Block(g4)
    c: Coincident(g19,g4)
    c: Block(g19)
    c: Equal(g5, g6-g11) x6
    c: InternalAlignment(g5-g11 -> g12) x7
    c: InternalAlignment(g13-g17 -> g12) x5
    c: Block(g12)
    c: Coincident(g18,g12)
    c: Block(g18)
    c: Coincident(g20,g2)
    c: Coincident(g20,g19)
    c: Horizontal(g20)
    c: Distance(g20) = 93.4
    c: Coincident(g21,g1)
    c: Horizontal(g21)
    c: Distance(g21) = 101.7
    c: Horizontal(g23)
    c: Distance(g23) = 8
    c: Coincident(g24,g23)
    c: Block(g23)
    c: Coincident(g22,g24)
    c: Block(g24)
    c: Block(g22)
    c: Distance(g22) = 1.61553
    c: Coincident(g25,g18)
    c: Block(g25)
    c: Weight(g26) = 1
    c: Equal(g26,g27)
    c: Equal(g26,g28)
    c: Coincident(g29,g4)
    c: InternalAlignment(g26,g29)
    c: InternalAlignment(g27,g29)
    c: InternalAlignment(g28,g29)
    c: InternalAlignment(g30,g29)
    c: InternalAlignment(g31,g29)
    c: Block(g29)
    c: Weight(g32) = 1
    c: Equal(g32,g33)
    c: Equal(g32,g34)
    c: Coincident(g35,g29)
    c: InternalAlignment(g32,g35)
    c: InternalAlignment(g33,g35)
    c: InternalAlignment(g34,g35)
    c: InternalAlignment(g36,g35)
    c: InternalAlignment(g37,g35)
    c: Block(g35)
    c: Coincident(g38,g35)
    c: Vertical(g38)
    c: Block(g38)
    c: Coincident(g42,g38)
    c: Weight(g39) = 1
    c: Equal(g39,g40)
    c: Equal(g39,g41)
    c: Coincident(g42,g25)
    c: InternalAlignment(g39,g42)
    c: InternalAlignment(g40,g42)
    c: InternalAlignment(g41,g42)
    c: InternalAlignment(g43,g42)
    c: InternalAlignment(g44,g42)
    c: Block(g42)
FEATURE [Part::Extrusion] Extrude064  label="bottom016"
  Base = -> Sketch073
  Dir = (0,0,1)
  DirMode = 2
  FaceMakerClass = Part::FaceMakerBullseye
  LengthFwd = 71.4
  LengthRev = 0
  Placement = pos=(0,0,0.3) rot=(0,0,1;0rad)
  Solid = true
  Symmetric = false
FEATURE [Part::Revolution] Revolve157  label="removeToCreateScrewAndThreadedInsertHole063"
  Angle = 360
  Axis = (0,1,0)
  Base = (0,0,0)
  FaceMakerClass = Part::FaceMakerBullseye
  Placement = pos=(12.5,0,10) rot=(0,0,1;0rad)
  Solid = false
  Source = -> Face141
  Symmetric = false
FEATURE [Sketcher::SketchObject] Sketch074
  FullyConstrained = true
  Placement = pos=(117,19,0) rot=(0.57735,0.57735,0.57735;2.0944rad)
  sketch-geometry (48):
    g0: LineSegment StartX=-49.19 StartY=69.25 StartZ=0 EndX=-49.19 EndY=66.25 EndZ=0
    g1: LineSegment StartX=-49.19 StartY=63.5 StartZ=0 EndX=-49.19 EndY=60.5 EndZ=0
    g2: LineSegment StartX=-49.19 StartY=57.75 StartZ=0 EndX=-49.19 EndY=54.75 EndZ=0
    g3: LineSegment StartX=-49.19 StartY=52 StartZ=0 EndX=-49.19 EndY=49 EndZ=0
    g4: LineSegment StartX=-49.19 StartY=46.25 StartZ=0 EndX=-49.19 EndY=43.25 EndZ=0
    g5: LineSegment StartX=-49.19 StartY=40.5 StartZ=0 EndX=-49.19 EndY=37.5 EndZ=0
    g6: LineSegment StartX=-49.19 StartY=34.5 StartZ=0 EndX=-49.19 EndY=31.5 EndZ=0
    g7: LineSegment StartX=-49.19 StartY=28.75 StartZ=0 EndX=-49.19 EndY=25.75 EndZ=0
    g8: LineSegment StartX=-49.19 StartY=23 StartZ=0 EndX=-49.19 EndY=20 EndZ=0
    g9: LineSegment StartX=-49.19 StartY=17.25 StartZ=0 EndX=-49.19 EndY=14.25 EndZ=0
    g10: LineSegment StartX=-49.19 StartY=11.5 StartZ=0 EndX=-49.19 EndY=8.5 EndZ=0
    g11: LineSegment StartX=-49.19 StartY=5.75 StartZ=0 EndX=-49.19 EndY=2.75 EndZ=0
    g12: ArcOfCircle CenterX=-1.5 CenterY=67.75 CenterZ=0 NormalX=0 NormalY=0 NormalZ=1 AngleXU=0 Radius=1.5 StartAngle=4.71239 EndAngle=7.85398
    g13: ArcOfCircle CenterX=-1.5 CenterY=62 CenterZ=0 NormalX=0 NormalY=0 NormalZ=1 AngleXU=0 Radius=1.5 StartAngle=4.71239 EndAngle=7.85398
    g14: ArcOfCircle CenterX=-1.5 CenterY=56.25 CenterZ=0 NormalX=0 NormalY=0 NormalZ=1 AngleXU=0 Radius=1.5 StartAngle=4.71239 EndAngle=7.85398
    g15: ArcOfCircle CenterX=-11.49 CenterY=50.5 CenterZ=0 NormalX=0 NormalY=0 NormalZ=1 AngleXU=0 Radius=1.5 StartAngle=4.71239 EndAngle=7.85398
    g16: ArcOfCircle CenterX=-16.28 CenterY=44.75 CenterZ=0 NormalX=0 NormalY=0 NormalZ=1 AngleXU=0 Radius=1.5 StartAngle=4.71239 EndAngle=7.85398
    g17: ArcOfCircle CenterX=-18.2337 CenterY=39 CenterZ=0 NormalX=0 NormalY=0 NormalZ=1 AngleXU=0 Radius=1.5 StartAngle=4.71485 EndAngle=7.85398
    g18: ArcOfCircle CenterX=-16.2837 CenterY=27.25 CenterZ=0 NormalX=0 NormalY=0 NormalZ=1 AngleXU=0 Radius=1.5 StartAngle=4.71485 EndAngle=7.85398
    g19: ArcOfCircle CenterX=-18.2337 CenterY=33 CenterZ=0 NormalX=0 NormalY=0 NormalZ=1 AngleXU=0 Radius=1.5 StartAngle=4.71485 EndAngle=7.85398
    g20: ArcOfCircle CenterX=-11.49 CenterY=21.5 CenterZ=0 NormalX=0 NormalY=0 NormalZ=1 AngleXU=0 Radius=1.5 StartAngle=4.71239 EndAngle=7.85398
    g21: ArcOfCircle CenterX=-1.5 CenterY=4.25 CenterZ=0 NormalX=0 NormalY=0 NormalZ=1 AngleXU=0 Radius=1.5 StartAngle=4.71239 EndAngle=7.85398
    g22: ArcOfCircle CenterX=-1.5 CenterY=10 CenterZ=0 NormalX=0 NormalY=0 NormalZ=1 AngleXU=0 Radius=1.5 StartAngle=4.71239 EndAngle=7.85398
    g23: ArcOfCircle CenterX=-1.5 CenterY=15.75 CenterZ=0 NormalX=0 NormalY=0 NormalZ=1 AngleXU=0 Radius=1.5 StartAngle=4.71239 EndAngle=7.85398
    g24: LineSegment StartX=-49.19 StartY=69.25 StartZ=0 EndX=-1.5 EndY=69.25 EndZ=0
    g25: LineSegment StartX=-49.19 StartY=66.25 StartZ=0 EndX=-1.5 EndY=66.25 EndZ=0
    g26: LineSegment StartX=-49.19 StartY=63.5 StartZ=0 EndX=-1.5 EndY=63.5 EndZ=0
    g27: LineSegment StartX=-49.19 StartY=60.5 StartZ=0 EndX=-1.5 EndY=60.5 EndZ=0
    g28: LineSegment StartX=-49.19 StartY=57.75 StartZ=0 EndX=-1.5 EndY=57.75 EndZ=0
    g29: LineSegment StartX=-49.19 StartY=54.75 StartZ=0 EndX=-1.5 EndY=54.75 EndZ=0
    g30: LineSegment StartX=-49.19 StartY=52 StartZ=0 EndX=-11.49 EndY=52 EndZ=0
    g31: LineSegment StartX=-49.19 StartY=49 StartZ=0 EndX=-11.49 EndY=49 EndZ=0
    g32: LineSegment StartX=-49.19 StartY=46.25 StartZ=0 EndX=-16.28 EndY=46.25 EndZ=0
    g33: LineSegment StartX=-49.19 StartY=43.25 StartZ=0 EndX=-16.28 EndY=43.25 EndZ=0
    g34: LineSegment StartX=-49.19 StartY=40.5 StartZ=0 EndX=-18.2337 EndY=40.5 EndZ=0
    g35: LineSegment StartX=-49.19 StartY=37.5 StartZ=0 EndX=-18.23 EndY=37.5 EndZ=0
    g36: LineSegment StartX=-49.19 StartY=34.5 StartZ=0 EndX=-18.2337 EndY=34.5 EndZ=0
    g37: LineSegment StartX=-49.19 StartY=31.5 StartZ=0 EndX=-18.23 EndY=31.5 EndZ=0
    g38: LineSegment StartX=-49.19 StartY=28.75 StartZ=0 EndX=-16.2837 EndY=28.75 EndZ=0
    g39: LineSegment StartX=-49.19 StartY=25.75 StartZ=0 EndX=-16.28 EndY=25.75 EndZ=0
    g40: LineSegment StartX=-49.19 StartY=23 StartZ=0 EndX=-11.49 EndY=23 EndZ=0
    g41: LineSegment StartX=-49.19 StartY=20 StartZ=0 EndX=-11.49 EndY=20 EndZ=0
    g42: LineSegment StartX=-49.19 StartY=17.25 StartZ=0 EndX=-1.5 EndY=17.25 EndZ=0
    g43: LineSegment StartX=-49.19 StartY=14.25 StartZ=0 EndX=-1.5 EndY=14.25 EndZ=0
    g44: LineSegment StartX=-49.19 StartY=11.5 StartZ=0 EndX=-1.5 EndY=11.5 EndZ=0
    g45: LineSegment StartX=-49.19 StartY=8.5 StartZ=0 EndX=-1.5 EndY=8.5 EndZ=0
    g46: LineSegment StartX=-49.19 StartY=5.75 StartZ=0 EndX=-1.5 EndY=5.75 EndZ=0
    g47: LineSegment StartX=-49.19 StartY=2.75 StartZ=0 EndX=-1.5 EndY=2.75 EndZ=0
  constraints (120):
    c: Vertical(g0)
    c: Distance(g0) = 3
    c: Block(g0)
    c: Vertical(g1)
    c: Distance(g1) = 3
    c: Vertical(g2)
    c: Equal(g0,g2) = 3
    c: Block(g2)
    c: Vertical(g3)
    c: Equal(g1,g3) = 3
    c: Vertical(g4)
    c: Equal(g0,g4) = 3
    c: Block(g4)
    c: Vertical(g5)
    c: Equal(g1,g5) = 3
    c: Vertical(g6)
    c: Equal(g0,g6) = 3
    c: Block(g6)
    c: Vertical(g7)
    c: Equal(g1,g7) = 3
    c: Vertical(g8)
    c: Equal(g0,g8) = 3
    c: Block(g8)
    c: Vertical(g9)
    c: Equal(g1,g9) = 3
    c: Vertical(g10)
    c: Equal(g0,g10) = 3
    c: Block(g10)
    c: Vertical(g11)
    c: Equal(g1,g11) = 3
    c: Block(g12)
    c: Block(g13)
    c: Block(g14)
    c: Block(g15)
    c: Block(g16)
    c: Block(g17)
    c: Block(g18)
    c: Block(g19)
    c: Block(g20)
    c: Block(g21)
    c: Block(g22)
    c: Block(g23)
    c: Block(g11)
    c: Block(g9)
    c: Block(g7)
    c: Block(g5)
    c: Block(g3)
    c: Block(g1)
    c: Coincident(g24,g0)
    c: Coincident(g24,g12)
    c: Horizontal(g24)
    c: Coincident(g25,g0)
    c: Coincident(g25,g12)
    c: Horizontal(g25)
    c: Coincident(g26,g1)
    c: Coincident(g26,g13)
    c: Horizontal(g26)
    c: Coincident(g27,g1)
    c: Coincident(g27,g13)
    c: Horizontal(g27)
    c: Coincident(g28,g2)
    c: Coincident(g28,g14)
    c: Horizontal(g28)
    c: Coincident(g29,g2)
    c: Coincident(g29,g14)
    c: Horizontal(g29)
    c: Coincident(g30,g3)
    c: Coincident(g30,g15)
    c: Horizontal(g30)
    c: Coincident(g31,g3)
    c: Coincident(g31,g15)
    c: Horizontal(g31)
    c: Coincident(g32,g4)
    c: Coincident(g32,g16)
    c: Horizontal(g32)
    c: Coincident(g33,g4)
    c: Coincident(g33,g16)
    c: Horizontal(g33)
    c: Coincident(g34,g5)
    c: Coincident(g34,g17)
    c: Horizontal(g34)
    c: Coincident(g35,g5)
    c: Coincident(g35,g17)
    c: Horizontal(g35)
    c: Coincident(g36,g6)
    c: Coincident(g36,g19)
    c: Horizontal(g36)
    c: Coincident(g37,g6)
    c: Coincident(g37,g19)
    c: Horizontal(g37)
    c: Coincident(g38,g7)
    c: Coincident(g38,g18)
    c: Horizontal(g38)
    c: Coincident(g39,g7)
    c: Coincident(g39,g18)
    c: Horizontal(g39)
    c: Coincident(g40,g8)
    c: Coincident(g40,g20)
    c: Horizontal(g40)
    c: Coincident(g41,g8)
    c: Coincident(g41,g20)
    c: Horizontal(g41)
    c: Coincident(g42,g9)
    c: Coincident(g42,g23)
    c: Horizontal(g42)
    c: Coincident(g43,g9)
    c: Coincident(g43,g23)
    c: Horizontal(g43)
    c: Coincident(g44,g10)
    c: Coincident(g44,g22)
    c: Horizontal(g44)
    c: Coincident(g45,g10)
    c: Coincident(g45,g22)
    c: Horizontal(g45)
    c: Coincident(g46,g11)
    c: Coincident(g46,g21)
    c: Horizontal(g46)
    c: Coincident(g47,g11)
    c: Coincident(g47,g21)
    c: Horizontal(g47)
FEATURE [Part::Extrusion] Extrude065
  Base = -> Sketch074
  Dir = (1,0,0)
  DirMode = 2
  FaceMakerClass = Part::FaceMakerBullseye
  LengthFwd = 23
  LengthRev = 0
  Placement = pos=(-19,0,0) rot=(0,0,1;0rad)
  Solid = true
  Symmetric = false
FEATURE [Part::Fillet] Fillet056  label="removeToCreateVentalationHoles003"
  Base = -> Extrude065
  Edges = <same value as first occurrence — deduplicated (x6 in doc)>
  Placement = pos=(7,0.02,0) rot=(0,0,1;0rad)
FEATURE [Part::Revolution] Revolve158  label="removeToCreateScrewAndThreadedInsertHole065"
  Angle = 360
  Axis = (0,1,0)
  Base = (0,0,0)
  FaceMakerClass = Part::FaceMakerBullseye
  Placement = pos=(12.5,0,62) rot=(0,0,1;0rad)
  Solid = false
  Source = -> Face146
  Symmetric = false
FEATURE [Part::Revolution] Revolve159  label="removeToCreateScrewAndThreadedInsertHole066"
  Angle = 360
  Axis = (0,1,0)
  Base = (0,0,0)
  FaceMakerClass = Part::FaceMakerBullseye
  Placement = pos=(89.5,0,68.5) rot=(0,0,1;0rad)
  Solid = false
  Source = -> Face143
  Symmetric = false
FEATURE [Part::Revolution] Revolve160  label="removeToCreateScrewAndThreadedInsertHole067"
  Angle = 360
  Axis = (0,1,0)
  Base = (0,0,0)
  FaceMakerClass = Part::FaceMakerBullseye
  Placement = pos=(89.5,0,3.5) rot=(0,0,1;0rad)
  Solid = false
  Source = -> Face142
  Symmetric = false
FEATURE [Part::Revolution] Revolve161  label="removeToCreateScrewAndThreadedInsertHole068"
  Angle = 360
  Axis = (0,1,0)
  Base = (0,0,0)
  FaceMakerClass = Part::FaceMakerBullseye
  Placement = pos=(109.5,4.7,3.5) rot=(0,0,1;0rad)
  Solid = false
  Source = -> Face145
  Symmetric = false
FEATURE [Part::Revolution] Revolve162  label="removeToCreateScrewAndThreadedInsertHole069"
  Angle = 360
  Axis = (0,1,0)
  Base = (0,0,0)
  FaceMakerClass = Part::FaceMakerBullseye
  Placement = pos=(109.5,4.7,68.5) rot=(0,0,1;0rad)
  Solid = false
  Source = -> Face144
  Symmetric = false
FEATURE [Part::MultiFuse] Fusion141  label="removeToCreateScrewAndThreadedInsertHole064"
  Shapes = -> [Revolve162,Revolve161,Revolve160,Revolve159,Revolve158,Revolve157]
FEATURE [Part::Cylinder] Cylinder062
  Angle = 360
  AttacherType = Attacher::AttachEngine3D
  Height = 20
  Placement = pos=(0,0,36.15) rot=(0,0,1;0rad)
  Radius = 14
FEATURE [Part::Cylinder] Cylinder063
  Angle = 360
  AttacherType = Attacher::AttachEngine3D
  Height = 10
  Placement = pos=(0,0,36.15) rot=(0,0,1;0rad)
  Radius = 4
FEATURE [Part::MultiFuse] Fusion139  label="removeToCreteHoleForPlugHousing052"
  Placement = pos=(70,19,36) rot=(0,1,0;1.5708rad)
  Shapes = -> [Cylinder062,Cylinder063]
FEATURE [Part::Cut] Cut060  label="bottom017"
  Base = -> Extrude064
  Tool = -> Fusion139
FEATURE [Part::Cut] Cut061  label="bottom019"
  Base = -> Cut060
  Tool = -> Fusion141
FEATURE [Part::MultiFuse] Fusion140  label="bottom018"
  Shapes = -> [Cut061,Cut058]
FEATURE [Part::Cut] Cut059  label="bottom020"
  Base = -> Fusion140
  Tool = -> Fillet056
FEATURE [Part::Box] Box036  label="Cube021"
  AttacherType = Attacher::AttachEngine3D
  Height = 80
  Length = 26
  Placement = pos=(0,-1,-5) rot=(0,0,1;0rad)
  Width = 11
FEATURE [Part::Cut] Cut062  label="removeFromBottom002"
  Base = -> Cut057
  Tool = -> Box036
FEATURE [Part::Cut] Cut063
  Base = -> Cut059
  Tool = -> Cut062
FEATURE [Part::Cut] Cut064  label="pcbStands"
  Base = -> Fusion095
  Tool = -> Fusion127
FEATURE [Sketcher::SketchObject] Sketch075  label="topSketch022"
  FullyConstrained = true
  sketch-geometry (6):
    g0: LineSegment StartX=19 StartY=38 StartZ=0 EndX=117 EndY=38 EndZ=0
    g1: ArcOfCircle CenterX=19 CenterY=19 CenterZ=0 NormalX=0 NormalY=0 NormalZ=1 AngleXU=0 Radius=19 StartAngle=1.5708 EndAngle=3.14159
    g2: LineSegment StartX=117 StartY=38 StartZ=0 EndX=117 EndY=19 EndZ=0
    g3: LineSegment StartX=98 StartY=1.0161e-12 StartZ=0 EndX=5.22862e-06 EndY=1.0161e-12 EndZ=0
    g4: LineSegment StartX=5.22862e-06 StartY=19 StartZ=0 EndX=5.22862e-06 EndY=1.0161e-12 EndZ=0
    g5: ArcOfCircle CenterX=98 CenterY=19 CenterZ=0 NormalX=0 NormalY=0 NormalZ=1 AngleXU=0 Radius=19 StartAngle=4.71239 EndAngle=6.28319
  constraints (16):
    c: Horizontal(g0)
    c: Distance(g0) = 98
    c: Coincident(g1,g0)
    c: Block(g1)
    c: Coincident(g2,g0)
    c: Vertical(g2)
    c: Distance(g2) = 19
    c: Horizontal(g3)
    c: Coincident(g4,g1)
    c: Vertical(g4)
    c: Coincident(g3,g4)
    c: Block(g3)
    c: Coincident(g5,g2)
    c: Coincident(g5,g3)
    c: Block(g0)
    c: Block(g5)
FEATURE [Part::Extrusion] Extrude067  label="sideB003"
  Base = -> Sketch075
  Dir = (0,0,1)
  DirMode = 2
  FaceMakerClass = Part::FaceMakerBullseye
  LengthFwd = 3
  LengthRev = 0
  Placement = pos=(0,0,71.7) rot=(0,0,1;0rad)
  Solid = true
  Symmetric = false
FEATURE [Sketcher::SketchObject] Sketch076  label="topSketch023"
  FullyConstrained = true
  sketch-geometry (6):
    g0: LineSegment StartX=19 StartY=38 StartZ=0 EndX=117 EndY=38 EndZ=0
    g1: ArcOfCircle CenterX=19 CenterY=19 CenterZ=0 NormalX=0 NormalY=0 NormalZ=1 AngleXU=0 Radius=19 StartAngle=1.5708 EndAngle=3.14159
    g2: LineSegment StartX=117 StartY=38 StartZ=0 EndX=117 EndY=19 EndZ=0
    g3: LineSegment StartX=98 StartY=1.0161e-12 StartZ=0 EndX=5.22862e-06 EndY=1.0161e-12 EndZ=0
    g4: LineSegment StartX=5.22862e-06 StartY=19 StartZ=0 EndX=5.22862e-06 EndY=1.0161e-12 EndZ=0
    g5: ArcOfCircle CenterX=98 CenterY=19 CenterZ=0 NormalX=0 NormalY=0 NormalZ=1 AngleXU=0 Radius=19 StartAngle=4.71239 EndAngle=6.28319
  constraints (16):
    c: Horizontal(g0)
    c: Distance(g0) = 98
    c: Coincident(g1,g0)
    c: Block(g1)
    c: Coincident(g2,g0)
    c: Vertical(g2)
    c: Distance(g2) = 19
    c: Horizontal(g3)
    c: Coincident(g4,g1)
    c: Vertical(g4)
    c: Coincident(g3,g4)
    c: Block(g3)
    c: Coincident(g5,g2)
    c: Coincident(g5,g3)
    c: Block(g0)
    c: Block(g5)
FEATURE [Part::Extrusion] Extrude066  label="sideA003"
  Base = -> Sketch076
  Dir = (0,0,1)
  DirMode = 2
  FaceMakerClass = Part::FaceMakerBullseye
  LengthFwd = 3
  LengthRev = 0
  Placement = pos=(0,0,-2.7) rot=(0,0,1;0rad)
  Solid = true
  Symmetric = false
FEATURE [Part::MultiFuse] Fusion142  label="removeFromBottom003"
  Placement = pos=(2,0,0) rot=(0,0,1;0rad)
  Shapes = -> [Extrude066,Extrude067]
FEATURE [Part::Cut] Cut065  label="screwRetainers002"
  Base = -> Fusion096
  Tool = -> Fusion142
FEATURE [Sketcher::SketchObject] Sketch077
  FullyConstrained = true
  Placement = pos=(117,19,0) rot=(0.57735,0.57735,0.57735;2.0944rad)
  sketch-geometry (8):
    g0: LineSegment StartX=-49.19 StartY=63.5 StartZ=0 EndX=-49.19 EndY=60.5 EndZ=0
    g1: LineSegment StartX=-49.19 StartY=11.5 StartZ=0 EndX=-49.19 EndY=8.5 EndZ=0
    g2: ArcOfCircle CenterX=-1.5 CenterY=62 CenterZ=0 NormalX=0 NormalY=0 NormalZ=1 AngleXU=0 Radius=1.5 StartAngle=4.71239 EndAngle=7.85398
    g3: ArcOfCircle CenterX=-1.5 CenterY=10 CenterZ=0 NormalX=0 NormalY=0 NormalZ=1 AngleXU=0 Radius=1.5 StartAngle=4.71239 EndAngle=7.85398
    g4: LineSegment StartX=-49.19 StartY=63.5 StartZ=0 EndX=-1.5 EndY=63.5 EndZ=0
    g5: LineSegment StartX=-49.19 StartY=60.5 StartZ=0 EndX=-1.5 EndY=60.5 EndZ=0
    g6: LineSegment StartX=-49.19 StartY=11.5 StartZ=0 EndX=-1.5 EndY=11.5 EndZ=0
    g7: LineSegment StartX=-49.19 StartY=8.5 StartZ=0 EndX=-1.5 EndY=8.5 EndZ=0
  constraints (19):
    c: Vertical(g0)
    c: Distance(g0) = 3
    c: Vertical(g1)
    c: Block(g1)
    c: Block(g2)
    c: Block(g3)
    c: Block(g0)
    c: Coincident(g4,g0)
    c: Coincident(g4,g2)
    c: Horizontal(g4)
    c: Coincident(g5,g0)
    c: Coincident(g5,g2)
    c: Horizontal(g5)
    c: Coincident(g6,g1)
    c: Coincident(g6,g3)
    c: Horizontal(g6)
    c: Coincident(g7,g1)
    c: Coincident(g7,g3)
    c: Horizontal(g7)
FEATURE [Part::Extrusion] Extrude068
  Base = -> Sketch077
  Dir = (1,0,0)
  DirMode = 2
  FaceMakerClass = Part::FaceMakerBullseye
  LengthFwd = 10
  LengthRev = 0
  Solid = true
  Symmetric = false
FEATURE [Part::Fillet] Fillet057  label="removeFromtMoreFrontCaseScrewRetainers002"
  Base = -> Extrude068
  Edges = 4 edges r=1.49: [Edge6,Edge11,Edge18,Edge23]
  Placement = pos=(-12,0,0) rot=(0,0,1;0rad)
FEATURE [Sketcher::SketchObject] Sketch078
  FullyConstrained = true
  Placement = pos=(117,19,0) rot=(0.57735,0.57735,0.57735;2.0944rad)
  sketch-geometry (8):
    g0: LineSegment StartX=-49.19 StartY=69.25 StartZ=0 EndX=-49.19 EndY=66.25 EndZ=0
    g1: LineSegment StartX=-49.19 StartY=5.75 StartZ=0 EndX=-49.19 EndY=2.75 EndZ=0
    g2: ArcOfCircle CenterX=-1.5 CenterY=67.75 CenterZ=0 NormalX=0 NormalY=0 NormalZ=1 AngleXU=0 Radius=1.5 StartAngle=4.71239 EndAngle=7.85398
    g3: ArcOfCircle CenterX=-1.5 CenterY=4.25 CenterZ=0 NormalX=0 NormalY=0 NormalZ=1 AngleXU=0 Radius=1.5 StartAngle=4.71239 EndAngle=7.85398
    g4: LineSegment StartX=-49.19 StartY=69.25 StartZ=0 EndX=-1.5 EndY=69.25 EndZ=0
    g5: LineSegment StartX=-49.19 StartY=66.25 StartZ=0 EndX=-1.5 EndY=66.25 EndZ=0
    g6: LineSegment StartX=-49.19 StartY=5.75 StartZ=0 EndX=-1.5 EndY=5.75 EndZ=0
    g7: LineSegment StartX=-49.19 StartY=2.75 StartZ=0 EndX=-1.5 EndY=2.75 EndZ=0
  constraints (19):
    c: Vertical(g0)
    c: Distance(g0) = 3
    c: Block(g0)
    c: Vertical(g1)
    c: Block(g2)
    c: Block(g3)
    c: Block(g1)
    c: Coincident(g4,g0)
    c: Coincident(g4,g2)
    c: Horizontal(g4)
    c: Coincident(g5,g0)
    c: Coincident(g5,g2)
    c: Horizontal(g5)
    c: Coincident(g6,g1)
    c: Coincident(g6,g3)
    c: Horizontal(g6)
    c: Coincident(g7,g1)
    c: Coincident(g7,g3)
    c: Horizontal(g7)
FEATURE [Part::Extrusion] Extrude069
  Base = -> Sketch078
  Dir = (1,0,0)
  DirMode = 2
  FaceMakerClass = Part::FaceMakerBullseye
  LengthFwd = 10
  LengthRev = 0
  Solid = true
  Symmetric = false
FEATURE [Part::Fillet] Fillet058  label="removeFromtMoreFrontCaseScrewRetainers003"
  Base = -> Extrude069
  Edges = 4 edges r=1.49: [Edge6,Edge11,Edge18,Edge23]
  Placement = pos=(-4,0,0) rot=(0,0,1;0rad)
FEATURE [Part::Cut] Cut066
  Base = -> Cut065
  Tool = -> Fillet058
FEATURE [Part::Cut] Cut067  label="screwPillars"
  Base = -> Cut066
  Tool = -> Fillet057
FEATURE [Part::MultiFuse] Fusion143  label="bottom021"
  Shapes = -> [Cut031,Cut063]
FEATURE [Part::Cylinder] Cylinder
  Angle = 360
  AttacherType = Attacher::AttachEngine3D
  Height = 10
  Placement = pos=(20.65,12,4.68) rot=(1,0,0;1.5708rad)
  Radius = 2
FEATURE [Part::Cylinder] Cylinder064
  Angle = 360
  AttacherType = Attacher::AttachEngine3D
  Height = 10
  Placement = pos=(20.65,12,67.38) rot=(1,0,0;1.5708rad)
  Radius = 2
FEATURE [Part::Cylinder] Cylinder065
  Angle = 360
  AttacherType = Attacher::AttachEngine3D
  Height = 10
  Placement = pos=(77.15,12,67.38) rot=(1,0,0;1.5708rad)
  Radius = 2
FEATURE [Part::Cylinder] Cylinder066
  Angle = 360
  AttacherType = Attacher::AttachEngine3D
  Height = 10
  Placement = pos=(77.15,12,4.68) rot=(1,0,0;1.5708rad)
  Radius = 2
FEATURE [Part::MultiFuse] Fusion144  label="removeFromThreadedInsertHousing"
  Shapes = -> [Cylinder065,Cylinder064,Cylinder,Cylinder066]
FEATURE [Part::Cut] Cut068  label="pcbStands001"
  Base = -> Cut064
  Tool = -> Fusion144
FEATURE [Part::MultiFuse] Fusion145
  Shapes = -> [Cut068,Fusion143]
FEATURE [Part::MultiFuse] Fusion146
  Shapes = -> [Fusion145]
FEATURE [Part::MultiFuse] Fusion147  label="bottom022"
  Shapes = -> [Cut067,Fusion146]
FEATURE [Part::MultiFuse] Fusion148  label="casePillars005"
  Shapes = -> [Cut047,Fusion092]
FEATURE [Part::MultiFuse] Fusion149  label="bottom023"
  Shapes = -> [Fusion124,Fusion113,Fusion147]
FEATURE [Part::MultiFuse] Fusion150  label="topBits"
  Shapes = -> [Cut025,Fusion148,Cut030,Fillet034]
FEATURE [Part::Feature] Face149 .. Face152  x4 (patterned run collapsed; names and placements below)
  shape: bbox 3.2 x 1.5 x 2e-07 mm, 1 faces, 0 solids (baked)
FEATURE [Part::Feature] Face153
  shape: bbox 3.6 x 3.2 x 2e-07 mm, 1 faces, 0 solids (baked)
FEATURE [Part::Feature] Face154
  shape: bbox 3.6 x 3.2 x 2e-07 mm, 1 faces, 0 solids (baked)
FEATURE [Sketcher::SketchObject] Sketch079  label="topSketch024"
  FullyConstrained = true
  sketch-geometry (6):
    g0: LineSegment StartX=19 StartY=38 StartZ=0 EndX=117 EndY=38 EndZ=0
    g1: ArcOfCircle CenterX=19 CenterY=19 CenterZ=0 NormalX=0 NormalY=0 NormalZ=1 AngleXU=0 Radius=19 StartAngle=1.5708 EndAngle=3.14159
    g2: LineSegment StartX=117 StartY=38 StartZ=0 EndX=117 EndY=19 EndZ=0
    g3: LineSegment StartX=98 StartY=1.0161e-12 StartZ=0 EndX=5.22862e-06 EndY=1.0161e-12 EndZ=0
    g4: LineSegment StartX=5.22862e-06 StartY=19 StartZ=0 EndX=5.22862e-06 EndY=1.0161e-12 EndZ=0
    g5: ArcOfCircle CenterX=98 CenterY=19 CenterZ=0 NormalX=0 NormalY=0 NormalZ=1 AngleXU=0 Radius=19 StartAngle=4.71239 EndAngle=6.28319
  constraints (16):
    c: Horizontal(g0)
    c: Distance(g0) = 98
    c: Coincident(g1,g0)
    c: Block(g1)
    c: Coincident(g2,g0)
    c: Vertical(g2)
    c: Distance(g2) = 19
    c: Horizontal(g3)
    c: Coincident(g4,g1)
    c: Vertical(g4)
    c: Coincident(g3,g4)
    c: Block(g3)
    c: Coincident(g5,g2)
    c: Coincident(g5,g3)
    c: Block(g0)
    c: Block(g5)
FEATURE [Sketcher::SketchObject] Sketch080  label="topSketch025"
  FullyConstrained = true
  sketch-geometry (6):
    g0: LineSegment StartX=19 StartY=38 StartZ=0 EndX=117 EndY=38 EndZ=0
    g1: ArcOfCircle CenterX=19 CenterY=19 CenterZ=0 NormalX=0 NormalY=0 NormalZ=1 AngleXU=0 Radius=19 StartAngle=1.5708 EndAngle=3.14159
    g2: LineSegment StartX=117 StartY=38 StartZ=0 EndX=117 EndY=19 EndZ=0
    g3: LineSegment StartX=98 StartY=1.0161e-12 StartZ=0 EndX=5.22862e-06 EndY=1.0161e-12 EndZ=0
    g4: LineSegment StartX=5.22862e-06 StartY=19 StartZ=0 EndX=5.22862e-06 EndY=1.0161e-12 EndZ=0
    g5: ArcOfCircle CenterX=98 CenterY=19 CenterZ=0 NormalX=0 NormalY=0 NormalZ=1 AngleXU=0 Radius=19 StartAngle=4.71239 EndAngle=6.28319
  constraints (16):
    c: Horizontal(g0)
    c: Distance(g0) = 98
    c: Coincident(g1,g0)
    c: Block(g1)
    c: Coincident(g2,g0)
    c: Vertical(g2)
    c: Distance(g2) = 19
    c: Horizontal(g3)
    c: Coincident(g4,g1)
    c: Vertical(g4)
    c: Coincident(g3,g4)
    c: Block(g3)
    c: Coincident(g5,g2)
    c: Coincident(g5,g3)
    c: Block(g0)
    c: Block(g5)
FEATURE [Part::Extrusion] Extrude070  label="sideA004"
  Base = -> Sketch080
  Dir = (0,0,1)
  DirMode = 2
  FaceMakerClass = Part::FaceMakerBullseye
  LengthFwd = 3
  LengthRev = 0
  Placement = pos=(0,0,-2.7) rot=(0,0,1;0rad)
  Solid = true
  Symmetric = false
FEATURE [Sketcher::SketchObject] Sketch081
  FullyConstrained = true
  Placement = pos=(117,19,0) rot=(0.57735,0.57735,0.57735;2.0944rad)
  sketch-geometry (8):
    g0: LineSegment StartX=-49.19 StartY=63.5 StartZ=0 EndX=-49.19 EndY=60.5 EndZ=0
    g1: LineSegment StartX=-49.19 StartY=11.5 StartZ=0 EndX=-49.19 EndY=8.5 EndZ=0
    g2: ArcOfCircle CenterX=-1.5 CenterY=62 CenterZ=0 NormalX=0 NormalY=0 NormalZ=1 AngleXU=0 Radius=1.5 StartAngle=4.71239 EndAngle=7.85398
    g3: ArcOfCircle CenterX=-1.5 CenterY=10 CenterZ=0 NormalX=0 NormalY=0 NormalZ=1 AngleXU=0 Radius=1.5 StartAngle=4.71239 EndAngle=7.85398
    g4: LineSegment StartX=-49.19 StartY=63.5 StartZ=0 EndX=-1.5 EndY=63.5 EndZ=0
    g5: LineSegment StartX=-49.19 StartY=60.5 StartZ=0 EndX=-1.5 EndY=60.5 EndZ=0
    g6: LineSegment StartX=-49.19 StartY=11.5 StartZ=0 EndX=-1.5 EndY=11.5 EndZ=0
    g7: LineSegment StartX=-49.19 StartY=8.5 StartZ=0 EndX=-1.5 EndY=8.5 EndZ=0
  constraints (19):
    c: Vertical(g0)
    c: Distance(g0) = 3
    c: Vertical(g1)
    c: Block(g1)
    c: Block(g2)
    c: Block(g3)
    c: Block(g0)
    c: Coincident(g4,g0)
    c: Coincident(g4,g2)
    c: Horizontal(g4)
    c: Coincident(g5,g0)
    c: Coincident(g5,g2)
    c: Horizontal(g5)
    c: Coincident(g6,g1)
    c: Coincident(g6,g3)
    c: Horizontal(g6)
    c: Coincident(g7,g1)
    c: Coincident(g7,g3)
    c: Horizontal(g7)
FEATURE [Part::Extrusion] Extrude071  label="sideB004"
  Base = -> Sketch079
  Dir = (0,0,1)
  DirMode = 2
  FaceMakerClass = Part::FaceMakerBullseye
  LengthFwd = 3
  LengthRev = 0
  Placement = pos=(0,0,71.7) rot=(0,0,1;0rad)
  Solid = true
  Symmetric = false
FEATURE [Part::MultiFuse] Fusion152  label="removeFromBottom004"
  Placement = pos=(2,0,0) rot=(0,0,1;0rad)
  Shapes = -> [Extrude070,Extrude071]
FEATURE [Part::Extrusion] Extrude072
  Base = -> Sketch081
  Dir = (1,0,0)
  DirMode = 2
  FaceMakerClass = Part::FaceMakerBullseye
  LengthFwd = 10
  LengthRev = 0
  Solid = true
  Symmetric = false
FEATURE [Part::Fillet] Fillet059  label="removeFromtMoreFrontCaseScrewRetainers004"
  Base = -> Extrude072
  Edges = 4 edges r=1.49: [Edge6,Edge11,Edge18,Edge23]
  Placement = pos=(-12,0,0) rot=(0,0,1;0rad)
FEATURE [Sketcher::SketchObject] Sketch082
  FullyConstrained = true
  Placement = pos=(117,19,0) rot=(0.57735,0.57735,0.57735;2.0944rad)
  sketch-geometry (8):
    g0: LineSegment StartX=-49.19 StartY=69.25 StartZ=0 EndX=-49.19 EndY=66.25 EndZ=0
    g1: LineSegment StartX=-49.19 StartY=5.75 StartZ=0 EndX=-49.19 EndY=2.75 EndZ=0
    g2: ArcOfCircle CenterX=-1.5 CenterY=67.75 CenterZ=0 NormalX=0 NormalY=0 NormalZ=1 AngleXU=0 Radius=1.5 StartAngle=4.71239 EndAngle=7.85398
    g3: ArcOfCircle CenterX=-1.5 CenterY=4.25 CenterZ=0 NormalX=0 NormalY=0 NormalZ=1 AngleXU=0 Radius=1.5 StartAngle=4.71239 EndAngle=7.85398
    g4: LineSegment StartX=-49.19 StartY=69.25 StartZ=0 EndX=-1.5 EndY=69.25 EndZ=0
    g5: LineSegment StartX=-49.19 StartY=66.25 StartZ=0 EndX=-1.5 EndY=66.25 EndZ=0
    g6: LineSegment StartX=-49.19 StartY=5.75 StartZ=0 EndX=-1.5 EndY=5.75 EndZ=0
    g7: LineSegment StartX=-49.19 StartY=2.75 StartZ=0 EndX=-1.5 EndY=2.75 EndZ=0
  constraints (19):
    c: Vertical(g0)
    c: Distance(g0) = 3
    c: Block(g0)
    c: Vertical(g1)
    c: Block(g2)
    c: Block(g3)
    c: Block(g1)
    c: Coincident(g4,g0)
    c: Coincident(g4,g2)
    c: Horizontal(g4)
    c: Coincident(g5,g0)
    c: Coincident(g5,g2)
    c: Horizontal(g5)
    c: Coincident(g6,g1)
    c: Coincident(g6,g3)
    c: Horizontal(g6)
    c: Coincident(g7,g1)
    c: Coincident(g7,g3)
    c: Horizontal(g7)
FEATURE [Part::Extrusion] Extrude073
  Base = -> Sketch082
  Dir = (1,0,0)
  DirMode = 2
  FaceMakerClass = Part::FaceMakerBullseye
  LengthFwd = 10
  LengthRev = 0
  Solid = true
  Symmetric = false
FEATURE [Part::Fillet] Fillet060  label="removeFromtMoreFrontCaseScrewRetainers005"
  Base = -> Extrude073
  Edges = 4 edges r=1.49: [Edge6,Edge11,Edge18,Edge23]
  Placement = pos=(-4,0,0) rot=(0,0,1;0rad)
FEATURE [Part::Revolution] Revolve163  label="backCaseScrewRetainer004"
  Angle = 360
  Axis = (0,1,0)
  Base = (0,0,0)
  FaceMakerClass = Part::FaceMakerBullseye
  Placement = pos=(12.5,3,62) rot=(0,0,1;0rad)
  Solid = false
  Source = -> Face149
  Symmetric = false
FEATURE [Part::Revolution] Revolve164  label="frontCaseScrewRetainer006"
  Angle = 360
  Axis = (0,1,0)
  Base = (0,0,0)
  FaceMakerClass = Part::FaceMakerBullseye
  Placement = pos=(89.5,3,68.5) rot=(0,0,1;0rad)
  Solid = false
  Source = -> Face151
  Symmetric = false
FEATURE [Part::Revolution] Revolve165  label="frontCaseScrewRetainer007"
  Angle = 360
  Axis = (0,1,0)
  Base = (0,0,0)
  FaceMakerClass = Part::FaceMakerBullseye
  Placement = pos=(89.5,3,3.5) rot=(0,0,1;0rad)
  Solid = false
  Source = -> Face152
  Symmetric = false
FEATURE [Part::Revolution] Revolve166  label="backCaseScrewRetainer005"
  Angle = 360
  Axis = (0,1,0)
  Base = (0,0,0)
  FaceMakerClass = Part::FaceMakerBullseye
  Placement = pos=(12.5,3,10) rot=(0,0,1;0rad)
  Solid = false
  Source = -> Face150
  Symmetric = false
FEATURE [Part::Revolution] Revolve167  label="moreFrontCaseScrewRetainer006"
  Angle = 360
  Axis = (0,1,0)
  Base = (0,0,0)
  FaceMakerClass = Part::FaceMakerBullseye
  Placement = pos=(109.5,4.5,68.5) rot=(0,0,1;0rad)
  Solid = false
  Source = -> Face153
  Symmetric = false
FEATURE [Part::Revolution] Revolve168  label="moreFrontCaseScrewRetainer007"
  Angle = 360
  Axis = (0,1,0)
  Base = (0,0,0)
  FaceMakerClass = Part::FaceMakerBullseye
  Placement = pos=(109.5,4.5,3.5) rot=(0,0,1;0rad)
  Solid = false
  Source = -> Face154
  Symmetric = false
FEATURE [Part::MultiFuse] Fusion151  label="screwRetainers003"
  Shapes = -> [Revolve168,Revolve167,Revolve166,Revolve165,Revolve164,Revolve163]
FEATURE [Part::Cut] Cut069  label="screwRetainers004"
  Base = -> Fusion151
  Tool = -> Fusion152
FEATURE [Part::Cut] Cut070
  Base = -> Cut069
  Tool = -> Fillet060
FEATURE [Part::Cut] Cut071  label="screwPillars001"
  Base = -> Cut070
  Tool = -> Fillet059
FEATURE [Part::MultiFuse] Fusion153  label="bottom024"
  Shapes = -> [Fusion149,Cut071]
FEATURE [Part::Cylinder] Cylinder067
  Angle = 360
  AttacherType = Attacher::AttachEngine3D
  Height = 10
  Placement = pos=(20.65,12,4.68) rot=(1,0,0;1.5708rad)
  Radius = 2
FEATURE [Part::Cylinder] Cylinder068
  Angle = 360
  AttacherType = Attacher::AttachEngine3D
  Height = 10
  Placement = pos=(20.65,12,67.38) rot=(1,0,0;1.5708rad)
  Radius = 2
FEATURE [Part::Cylinder] Cylinder069
  Angle = 360
  AttacherType = Attacher::AttachEngine3D
  Height = 10
  Placement = pos=(77.15,12,67.38) rot=(1,0,0;1.5708rad)
  Radius = 2
FEATURE [Part::Cylinder] Cylinder070
  Angle = 360
  AttacherType = Attacher::AttachEngine3D
  Height = 10
  Placement = pos=(77.15,12,4.68) rot=(1,0,0;1.5708rad)
  Radius = 2
FEATURE [Part::MultiFuse] Fusion154  label="removeFromThreadedInsertHousing001"
  Shapes = -> [Cylinder069,Cylinder068,Cylinder067,Cylinder070]
FEATURE [Part::Cut] Cut072  label="bottom025"
  Base = -> Fusion153
  Tool = -> Fusion154
FEATURE [Image::ImagePlane] ImagePlane
  XSize = 339
  YSize = 72
FEATURE [Sketcher::SketchObject] Sketch083
  FullyConstrained = true
  MapMode = 5
  Support = -> [XY_Plane]
  sketch-geometry (338):
    g0: LineSegment StartX=-151.619 StartY=28.8932 StartZ=0 EndX=-140.819 EndY=28.8932 EndZ=0
    g1: LineSegment StartX=-151.619 StartY=24.0313 StartZ=0 EndX=-151.619 EndY=28.8932 EndZ=0
    g2: LineSegment StartX=-140.819 StartY=17.7713 StartZ=0 EndX=-151.619 EndY=17.7713 EndZ=0
    g3: LineSegment StartX=-151.619 StartY=17.7713 StartZ=0 EndX=-151.619 EndY=22.6313 EndZ=0
    g4: LineSegment StartX=-151.619 StartY=22.6313 StartZ=0 EndX=-145.128 EndY=22.6313 EndZ=0
    g5: LineSegment StartX=-145.128 StartY=24.0313 StartZ=0 EndX=-140.819 EndY=28.8932 EndZ=0
    g6: LineSegment StartX=-145.128 StartY=22.6313 StartZ=0 EndX=-140.819 EndY=17.7713 EndZ=0
    g7: ArcOfCircle CenterX=-155.157 CenterY=23.3323 CenterZ=0 NormalX=0 NormalY=0 NormalZ=1 AngleXU=0 Radius=6.92354 StartAngle=1.03434 EndAngle=5.24885
    g8: ArcOfCircle CenterX=-155.157 CenterY=23.3323 CenterZ=0 NormalX=0 NormalY=0 NormalZ=1 AngleXU=0 Radius=12.6269 StartAngle=1.28675 EndAngle=4.99643
    g9: LineSegment StartX=-151.619 StartY=35.4532 StartZ=0 EndX=-151.619 EndY=29.2832 EndZ=0
    g10: LineSegment StartX=-151.619 StartY=17.3813 StartZ=0 EndX=-151.619 EndY=11.2113 EndZ=0
    g11-g21: Circle x11 (B-spline internal-alignment scaffolding for g22; pole/knot coordinates omitted)
    g22: BSplineCurve PolesCount=11 KnotsCount=9 Degree=3 IsPeriodic=0
    g23-g31: GeomPoint x9 (B-spline internal-alignment scaffolding for g22; pole/knot coordinates omitted)
    g32-g49: Circle x18 (B-spline internal-alignment scaffolding for g50; pole/knot coordinates omitted)
    g50: BSplineCurve PolesCount=18 KnotsCount=16 Degree=3 IsPeriodic=0
    g51-g66: GeomPoint x16 (B-spline internal-alignment scaffolding for g50; pole/knot coordinates omitted)
    g67: LineSegment StartX=-117.124 StartY=30.093 StartZ=0 EndX=-117.603 EndY=26.5272 EndZ=0
    g68: LineSegment StartX=-117.603 StartY=17.8472 StartZ=0 EndX=-117.124 EndY=14.2659 EndZ=0
    g69: Ellipse CenterX=-109.671 CenterY=20.025 CenterZ=0 NormalX=0 NormalY=0 NormalZ=1 MajorRadius=3.34798 MinorRadius=2.71052 AngleXU=-1.56793
    g70: GeomPoint X=-109.666 Y=18.0598 Z=0
    g71: GeomPoint X=-109.677 Y=21.9902 Z=0
    g72: Ellipse CenterX=-109.671 CenterY=20.0123 CenterZ=0 NormalX=0 NormalY=0 NormalZ=1 MajorRadius=6.93002 MinorRadius=6.36273 AngleXU=-3.13976
    g73: GeomPoint X=-112.417 Y=20.0073 Z=0
    g74: GeomPoint X=-106.925 Y=20.0173 Z=0
    g75: Ellipse CenterX=-51.7682 CenterY=20.1463 CenterZ=0 NormalX=0 NormalY=0 NormalZ=1 MajorRadius=3.19279 MinorRadius=2.71052 AngleXU=-1.52774
    g76: GeomPoint X=-51.6955 Y=18.4606 Z=0
    g77: GeomPoint X=-51.8408 Y=21.832 Z=0
    g78: GeomPoint X=-54.5142 Y=20.1413 Z=0
    g79: GeomPoint X=-49.0221 Y=20.1513 Z=0
    g80: Ellipse CenterX=-51.7682 CenterY=20.1463 CenterZ=0 NormalX=0 NormalY=0 NormalZ=1 MajorRadius=6.93002 MinorRadius=6.36273 AngleXU=-3.13976
    g81: Ellipse CenterX=-22.8436 CenterY=20.1783 CenterZ=0 NormalX=0 NormalY=0 NormalZ=1 MajorRadius=3.31512 MinorRadius=2.71052 AngleXU=-1.60214
    g82: GeomPoint X=-22.9034 Y=18.2706 Z=0
    g83: GeomPoint X=-22.7838 Y=22.0861 Z=0
    g84: GeomPoint X=-25.5897 Y=20.1733 Z=0
    g85: GeomPoint X=-20.0976 Y=20.1833 Z=0
    g86: Ellipse CenterX=-22.8436 CenterY=20.1783 CenterZ=0 NormalX=0 NormalY=0 NormalZ=1 MajorRadius=6.93002 MinorRadius=6.36273 AngleXU=-3.13976
    g87: LineSegment StartX=-101.889 StartY=14.1107 StartZ=0 EndX=-97.7455 EndY=14.1107 EndZ=0
    g88: LineSegment StartX=-93.8155 StartY=14.1107 StartZ=0 EndX=-89.6755 EndY=14.1107 EndZ=0
    g89: LineSegment StartX=-85.7455 StartY=14.1107 StartZ=0 EndX=-81.6055 EndY=14.1107 EndZ=0
    g90: LineSegment StartX=-101.889 StartY=14.1107 StartZ=0 EndX=-101.889 EndY=25.9907 EndZ=0
    g91: LineSegment StartX=-101.889 StartY=25.9907 StartZ=0 EndX=-97.8594 EndY=25.9907 EndZ=0
    g92: LineSegment StartX=-97.8594 StartY=25.9907 StartZ=0 EndX=-97.8594 EndY=24.0907 EndZ=0
    g93: LineSegment StartX=-97.7455 StartY=14.1107 StartZ=0 EndX=-97.7455 EndY=19.9107 EndZ=0
    g94: LineSegment StartX=-89.6755 StartY=14.1107 StartZ=0 EndX=-89.6755 EndY=19.9107 EndZ=0
    g95: LineSegment StartX=-93.8155 StartY=14.1107 StartZ=0 EndX=-93.8155 EndY=21.0107 EndZ=0
    g96-g106: Circle x11 (B-spline internal-alignment scaffolding for g107; pole/knot coordinates omitted)
    g107: BSplineCurve PolesCount=11 KnotsCount=9 Degree=3 IsPeriodic=0
    g108-g116: GeomPoint x9 (B-spline internal-alignment scaffolding for g107; pole/knot coordinates omitted)
    g117: BSplineCurve PolesCount=11 KnotsCount=9 Degree=3 IsPeriodic=0
    g118-g125: Circle x8 (B-spline internal-alignment scaffolding for g126; pole/knot coordinates omitted)
    g126: BSplineCurve PolesCount=8 KnotsCount=6 Degree=3 IsPeriodic=0
    g127-g132: GeomPoint x6 (B-spline internal-alignment scaffolding for g126; pole/knot coordinates omitted)
    g133: BSplineCurve PolesCount=8 KnotsCount=6 Degree=3 IsPeriodic=0
    g134: LineSegment StartX=-85.7455 StartY=21.0107 StartZ=0 EndX=-85.7455 EndY=14.1107 EndZ=0
    g135: LineSegment StartX=-80.0879 StartY=14.1107 StartZ=0 EndX=-75.944 EndY=14.1107 EndZ=0
    g136: LineSegment StartX=-72.014 StartY=14.1107 StartZ=0 EndX=-67.874 EndY=14.1107 EndZ=0
    g137: LineSegment StartX=-63.944 StartY=14.1107 StartZ=0 EndX=-59.804 EndY=14.1107 EndZ=0
    g138: LineSegment StartX=-80.0879 StartY=14.1107 StartZ=0 EndX=-80.0879 EndY=25.9907 EndZ=0
    g139: LineSegment StartX=-80.0879 StartY=25.9907 StartZ=0 EndX=-76.0579 EndY=25.9907 EndZ=0
    g140: LineSegment StartX=-76.0579 StartY=25.9907 StartZ=0 EndX=-76.0579 EndY=24.0907 EndZ=0
    g141: LineSegment StartX=-75.944 StartY=14.1107 StartZ=0 EndX=-75.944 EndY=19.9107 EndZ=0
    g142: LineSegment StartX=-67.874 StartY=14.1107 StartZ=0 EndX=-67.874 EndY=19.9107 EndZ=0
    g143: LineSegment StartX=-72.014 StartY=14.1107 StartZ=0 EndX=-72.014 EndY=21.0107 EndZ=0
    g144-g148: Circle x5 (B-spline internal-alignment scaffolding for g149; pole/knot coordinates omitted)
    g149: BSplineCurve PolesCount=11 KnotsCount=9 Degree=3 IsPeriodic=0
    g150-g158: GeomPoint x9 (B-spline internal-alignment scaffolding for g149; pole/knot coordinates omitted)
    g159: BSplineCurve PolesCount=11 KnotsCount=9 Degree=3 IsPeriodic=0
    g160-g167: Circle x8 (B-spline internal-alignment scaffolding for g168; pole/knot coordinates omitted)
    g168: BSplineCurve PolesCount=8 KnotsCount=6 Degree=3 IsPeriodic=0
    g169-g174: GeomPoint x6 (B-spline internal-alignment scaffolding for g168; pole/knot coordinates omitted)
    g175: BSplineCurve PolesCount=8 KnotsCount=6 Degree=3 IsPeriodic=0
    g176: LineSegment StartX=-63.944 StartY=21.0107 StartZ=0 EndX=-63.944 EndY=14.1107 EndZ=0
    g177: LineSegment StartX=-59.804 StartY=14.1107 StartZ=0 EndX=-59.804 EndY=21.5868 EndZ=0
    g178: BSplineCurve PolesCount=4 KnotsCount=2 Degree=3 IsPeriodic=0
    g179: GeomPoint X=-59.804 Y=21.5868 Z=0
    g180: GeomPoint X=-60.2379 Y=24.0907 Z=0
    g181: LineSegment StartX=-81.6055 StartY=14.1107 StartZ=0 EndX=-81.6055 EndY=21.5868 EndZ=0
    g182: LineSegment StartX=-151.619 StartY=24.0313 StartZ=0 EndX=-145.128 EndY=24.0313 EndZ=0
    g183: Circle CenterX=-82.0394 CenterY=24.0907 CenterZ=0 NormalX=0 NormalY=0 NormalZ=1 AngleXU=0 Radius=1
    g184: Circle CenterX=-81.7131 CenterY=23.2736 CenterZ=0 NormalX=0 NormalY=0 NormalZ=1 AngleXU=0 Radius=1
    g185: Circle CenterX=-81.6055 CenterY=21.5868 CenterZ=0 NormalX=0 NormalY=0 NormalZ=1 AngleXU=0 Radius=1
    g186: BSplineCurve PolesCount=3 KnotsCount=2 Degree=2 IsPeriodic=0
    g187: GeomPoint X=-82.0394 Y=24.0907 Z=0
    g188: GeomPoint X=-81.6055 Y=21.5868 Z=0
    g189: Ellipse CenterX=-37.3522 CenterY=19.9515 CenterZ=0 NormalX=0 NormalY=0 NormalZ=1 MajorRadius=2.99755 MinorRadius=2.49 AngleXU=1.5708
    g190: GeomPoint X=-37.3522 Y=21.6203 Z=0
    g191: GeomPoint X=-37.3522 Y=18.2826 Z=0
    g192: ArcOfEllipse CenterX=-38.7647 CenterY=20.06 CenterZ=0 NormalX=0 NormalY=0 NormalZ=1 MajorRadius=6.30025 MinorRadius=5.3849 AngleXU=1.57276 StartAngle=5.50632 EndAngle=10.3035
    g193: GeomPoint X=-38.7711 Y=23.3304 Z=0
    g194: GeomPoint X=-38.7583 Y=16.7895 Z=0
    g195: LineSegment StartX=-34.6109 StartY=14.1107 StartZ=0 EndX=-30.8984 EndY=14.1107 EndZ=0
    g196: LineSegment StartX=-30.8984 StartY=14.1107 StartZ=0 EndX=-30.8984 EndY=31.1784 EndZ=0
    g197: LineSegment StartX=-30.8984 StartY=31.1784 StartZ=0 EndX=-34.9984 EndY=31.1784 EndZ=0
    g198: LineSegment StartX=-34.9984 StartY=24.5602 StartZ=0 EndX=-34.9984 EndY=31.1784 EndZ=0
    g199: LineSegment StartX=-34.6109 StartY=16.0476 StartZ=0 EndX=-34.6109 EndY=14.1107 EndZ=0
    g200: LineSegment StartX=-14.8781 StartY=14.1107 StartZ=0 EndX=-10.5106 EndY=14.1107 EndZ=0
    g201: LineSegment StartX=-14.8781 StartY=14.1107 StartZ=0 EndX=-14.8781 EndY=25.8504 EndZ=0
    g202: LineSegment StartX=-14.8781 StartY=25.8504 StartZ=0 EndX=-10.8534 EndY=25.8504 EndZ=0
    g203: LineSegment StartX=-10.8534 StartY=25.8504 StartZ=0 EndX=-10.8534 EndY=24.0923 EndZ=0
    g204: LineSegment StartX=-10.5106 StartY=14.1107 StartZ=0 EndX=-10.5106 EndY=19.7752 EndZ=0
    g205: LineSegment StartX=-5.96397 StartY=25.9304 StartZ=0 EndX=-5.96397 EndY=22.574 EndZ=0
    g206-g214: Circle x9 (B-spline internal-alignment scaffolding for g215; pole/knot coordinates omitted)
    g215: BSplineCurve PolesCount=9 KnotsCount=7 Degree=3 IsPeriodic=0
    g216-g222: GeomPoint x7 (B-spline internal-alignment scaffolding for g215; pole/knot coordinates omitted)
    g223-g232: Circle x10 (B-spline internal-alignment scaffolding for g233; pole/knot coordinates omitted)
    g233: BSplineCurve PolesCount=10 KnotsCount=8 Degree=3 IsPeriodic=0
    g234-g241: GeomPoint x8 (B-spline internal-alignment scaffolding for g233; pole/knot coordinates omitted)
    g242: LineSegment StartX=-1.58923 StartY=21.0696 StartZ=0 EndX=2.62034 EndY=21.0696 EndZ=0
    g243: LineSegment StartX=-1.55856 StartY=18.7342 StartZ=0 EndX=6.45946 EndY=18.7342 EndZ=0
    g244: LineSegment StartX=5.29231 StartY=17.386 StartZ=0 EndX=5.29231 EndY=14.3674 EndZ=0
    g245-g269: Circle x25 (B-spline internal-alignment scaffolding for g270; pole/knot coordinates omitted)
    g270: BSplineCurve PolesCount=25 KnotsCount=23 Degree=3 IsPeriodic=0
    g271-g293: GeomPoint x23 (B-spline internal-alignment scaffolding for g270; pole/knot coordinates omitted)
    g294-g304: Circle x11 (B-spline internal-alignment scaffolding for g305; pole/knot coordinates omitted)
    g305: BSplineCurve PolesCount=11 KnotsCount=9 Degree=3 IsPeriodic=0
    g306-g314: GeomPoint x9 (B-spline internal-alignment scaffolding for g305; pole/knot coordinates omitted)
    g315-g326: Circle x12 (B-spline internal-alignment scaffolding for g327; pole/knot coordinates omitted)
    g327: BSplineCurve PolesCount=12 KnotsCount=10 Degree=3 IsPeriodic=0
    g328-g337: GeomPoint x10 (B-spline internal-alignment scaffolding for g327; pole/knot coordinates omitted)
  constraints (252):
    c: Coincident(g1,g0)
    c: Horizontal(g0)
    c: Vertical(g1)
    c: Coincident(g2,g3)
    c: Coincident(g3,g4)
    c: Horizontal(g4)
    c: Horizontal(g2)
    c: Vertical(g3)
    c: Block(g1)
    c: Distance(g3) = 4.86
    c: Block(g4)
    c: Distance(g0) = 10.8
    c: Distance(g2) = 10.8
    c: Coincident(g5,g0)
    c: Coincident(g6,g4)
    c: Coincident(g6,g2)
    c: Block(g8)
    c: Block(g7)
    c: Coincident(g9,g8)
    c: Coincident(g9,g7)
    c: Vertical(g9)
    c: Coincident(g10,g7)
    c: Coincident(g10,g8)
    c: Vertical(g10)
    c: Weight(g11) = 1
    c: Equal(g11, g12-g21) x10
    c: InternalAlignment(g11-g21 -> g22) x11
    c: InternalAlignment(g23-g31 -> g22) x9
    c: Block(g22)
    c: Weight(g32) = 1
    c: Equal(g32, g33-g49) x17
    c: InternalAlignment(g32-g49 -> g50) x18
    c: InternalAlignment(g51-g66 -> g50) x16
    c: Block(g50)
    c: Coincident(g67,g50)
    c: Coincident(g67,g22)
    c: Coincident(g68,g22)
    c: Coincident(g68,g50)
    c: InternalAlignment(g70,g69)
    c: InternalAlignment(g71,g69)
    c: Block(g69)
    c: InternalAlignment(g73,g72)
    c: InternalAlignment(g74,g72)
    c: Block(g72)
    c: InternalAlignment(g76,g75)
    c: InternalAlignment(g77,g75)
    c: InternalAlignment(g78,g80)
    c: InternalAlignment(g79,g80)
    c: Block(g80)
    c: Coincident(g75,g80)
    c: Block(g75)
    c: InternalAlignment(g82,g81)
    c: InternalAlignment(g83,g81)
    c: InternalAlignment(g84,g86)
    c: InternalAlignment(g85,g86)
    c: Block(g86)
    c: Coincident(g81,g86)
    c: Block(g81)
    c: Horizontal(g87)
    c: Block(g87)
    c: Horizontal(g88)
    c: Distance(g88) = 4.14
    c: Horizontal(g89)
    c: Equal(g88,g89) = 4.14
    c: Block(g89)
    c: Block(g88)
    c: Coincident(g90,g87)
    c: Vertical(g90)
    c: Distance(g90) = 11.88
    c: Coincident(g91,g90)
    c: Horizontal(g91)
    c: Coincident(g92,g91)
    c: Vertical(g92)
    c: Distance(g91) = 4.03
    c: Distance(g92) = 1.9
    c: Coincident(g93,g87)
    c: Vertical(g93)
    c: Vertical(g94)
    c: Coincident(g94,g88)
    c: Distance(g93) = 5.8
    c: Distance(g94) = 5.8
    c: Vertical(g95)
    c: Coincident(g95,g88)
    c: Distance(g95) = 6.9
    c: Coincident(g107,g92)
    c: Weight(g96) = 1
    c: Equal(g96, g97-g106) x10
    c: InternalAlignment(g96-g106 -> g107) x11
    c: InternalAlignment(g108-g116 -> g107) x9
    c: Block(g107)
    c: Block(g117)
    c: Coincident(g126,g93)
    c: Weight(g118) = 1
    c: Equal(g118, g119-g125) x7
    c: Coincident(g126,g95)
    c: InternalAlignment(g118-g125 -> g126) x8
    c: InternalAlignment(g127-g132 -> g126) x6
    c: Coincident(g133,g94)
    c: Block(g126)
    c: Block(g133)
    c: Coincident(g134,g133)
    c: Coincident(g134,g89)
    c: Vertical(g134)
    c: Horizontal(g135)
    c: Block(g135)
    c: Horizontal(g136)
    c: Equal(g88,g136) = 4.14
    c: Horizontal(g137)
    c: Equal(g136,g137) = 4.14
    c: Block(g137)
    c: Block(g136)
    c: Coincident(g138,g135)
    c: Vertical(g138)
    c: Equal(g90,g138) = 11.88
    c: Coincident(g139,g138)
    c: Horizontal(g139)
    c: Coincident(g140,g139)
    c: Vertical(g140)
    c: Equal(g91,g139) = 4.03
    c: Equal(g92,g140) = 1.9
    c: Coincident(g141,g135)
    c: Vertical(g141)
    c: Vertical(g142)
    c: Coincident(g142,g136)
    c: Equal(g93,g141) = 5.8
    c: Equal(g94,g142) = 5.8
    c: Vertical(g143)
    c: Coincident(g143,g136)
    c: Equal(g95,g143) = 6.9
    c: Coincident(g149,g140)
    c: Equal(g96,g144) = 1
    c: Equal(g144, g145-g148) x4
    c: InternalAlignment(g144-g148 -> g149) x5
    c: InternalAlignment(g150-g158 -> g149) x9
    c: Block(g149)
    c: Block(g159)
    c: Coincident(g168,g141)
    c: Equal(g118,g160) = 1
    c: Equal(g160, g161-g167) x7
    c: Coincident(g168,g143)
    c: InternalAlignment(g160-g167 -> g168) x8
    c: InternalAlignment(g169-g174 -> g168) x6
    c: Coincident(g175,g142)
    c: Block(g168)
    c: Block(g175)
    c: Coincident(g176,g175)
    c: Coincident(g176,g137)
    c: Vertical(g176)
    c: Coincident(g177,g137)
    c: Vertical(g177)
    c: Coincident(g178,g177)
    c: Coincident(g178,g159)
    c: InternalAlignment(g179,g178)
    c: InternalAlignment(g180,g178)
    c: Block(g178)
    c: Vertical(g181)
    c: Coincident(g181,g89)
    c: Block(g5)
    c: Coincident(g182,g1)
    c: Coincident(g182,g5)
    c: Horizontal(g182)
    c: Coincident(g186,g117)
    c: Weight(g183) = 1
    c: Equal(g183,g184)
    c: Equal(g183,g185)
    c: Coincident(g186,g181)
    c: InternalAlignment(g183,g186)
    c: InternalAlignment(g184,g186)
    c: InternalAlignment(g185,g186)
    c: InternalAlignment(g187,g186)
    c: InternalAlignment(g188,g186)
    c: Block(g186)
    c: InternalAlignment(g190,g189)
    c: InternalAlignment(g191,g189)
    c: Block(g189)
    c: InternalAlignment(g193,g192)
    c: InternalAlignment(g194,g192)
    c: Block(g192)
    c: Horizontal(g195)
    c: Block(g195)
    c: Coincident(g196,g195)
    c: Vertical(g196)
    c: Block(g196)
    c: Distance(g195) = 3.71244
    c: Coincident(g197,g196)
    c: Horizontal(g197)
    c: Distance(g197) = 4.1
    c: Coincident(g198,g192)
    c: Coincident(g198,g197)
    c: Vertical(g198)
    c: Block(g198)
    c: Coincident(g199,g192)
    c: Coincident(g199,g195)
    c: Vertical(g199)
    c: Block(g199)
    c: Horizontal(g200)
    c: Block(g200)
    c: Coincident(g201,g200)
    c: Vertical(g201)
    c: Block(g201)
    c: Coincident(g202,g201)
    c: Horizontal(g202)
    c: Block(g202)
    c: Coincident(g203,g202)
    c: Vertical(g203)
    c: Block(g203)
    c: Coincident(g204,g200)
    c: Vertical(g204)
    c: Block(g204)
    c: Coincident(g215,g203)
    c: Weight(g206) = 1
    c: Equal(g206, g207-g214) x8
    c: Coincident(g215,g205)
    c: InternalAlignment(g206-g214 -> g215) x9
    c: InternalAlignment(g216-g222 -> g215) x7
    c: Coincident(g233,g204)
    c: Weight(g223) = 1
    c: Equal(g223, g224-g232) x9
    c: Coincident(g233,g205)
    c: InternalAlignment(g223-g232 -> g233) x10
    c: InternalAlignment(g234-g241 -> g233) x8
    c: Vertical(g205)
    c: Block(g205)
    c: Block(g215)
    c: Block(g233)
    c: Horizontal(g242)
    c: Horizontal(g243)
    c: Block(g242)
    c: Block(g243)
    c: Vertical(g244)
    c: Block(g244)
    c: Coincident(g270,g243)
    c: Weight(g245) = 1
    c: Equal(g245, g246-g269) x24
    c: Coincident(g270,g244)
    c: InternalAlignment(g245-g269 -> g270) x25
    c: InternalAlignment(g271-g293 -> g270) x23
    c: Coincident(g305,g242)
    c: Weight(g294) = 1
    c: Equal(g294, g295-g304) x10
    c: Coincident(g305,g242)
    c: InternalAlignment(g294-g304 -> g305) x11
    c: InternalAlignment(g306-g314 -> g305) x9
    c: Block(g305)
    c: Coincident(g327,g243)
    c: Weight(g315) = 1
    c: Equal(g315, g316-g326) x11
    c: Coincident(g327,g244)
    c: InternalAlignment(g315-g326 -> g327) x12
    c: InternalAlignment(g328-g337 -> g327) x10
    c: Block(g327)
    c: Block(g270)
FEATURE [PartDesign::Body] Body  label="CommodoreLogoAndText"
  Group = -> [Sketch083]
  Origin = -> Origin
FEATURE [Part::Extrusion] Extrude074  label="CommodoreLogoAndText001"
  Base = -> Sketch083
  Dir = (0,0,1)
  DirMode = 2
  FaceMakerClass = Part::FaceMakerBullseye
  LengthFwd = 10
  LengthRev = 0
  Solid = true
  Symmetric = false
FEATURE [Part::FeaturePython] Clone  label="CommodoreLogoAndTextScale"  # Draft clone (typed FeaturePython)
  AttacherType = Attacher::AttachEngine3D
  Fuse = false
  Objects = -> [Extrude074]
  Placement = pos=(111,5.37,-11.6) rot=(0,0,1;0rad)
  Scale = (0.62,0.62,1)
FEATURE [Part::Mirroring] Part__Mirroring  label="CommodoreLogoAndTextScale (Mirror #1)"
  Base = (0,0,0)
  Normal = (1,0,0)
  Placement = pos=(123.576,0,0) rot=(0,0,1;0rad)
  Source = -> Clone
FEATURE [Sketcher::SketchObject] Sketch084
  FullyConstrained = true
  MapMode = 5
  Support = -> [XY_Plane001]
  sketch-geometry (338):
    g0: LineSegment StartX=-151.619 StartY=28.8932 StartZ=0 EndX=-140.819 EndY=28.8932 EndZ=0
    g1: LineSegment StartX=-151.619 StartY=24.0313 StartZ=0 EndX=-151.619 EndY=28.8932 EndZ=0
    g2: LineSegment StartX=-140.819 StartY=17.7713 StartZ=0 EndX=-151.619 EndY=17.7713 EndZ=0
    g3: LineSegment StartX=-151.619 StartY=17.7713 StartZ=0 EndX=-151.619 EndY=22.6313 EndZ=0
    g4: LineSegment StartX=-151.619 StartY=22.6313 StartZ=0 EndX=-145.128 EndY=22.6313 EndZ=0
    g5: LineSegment StartX=-145.128 StartY=24.0313 StartZ=0 EndX=-140.819 EndY=28.8932 EndZ=0
    g6: LineSegment StartX=-145.128 StartY=22.6313 StartZ=0 EndX=-140.819 EndY=17.7713 EndZ=0
    g7: ArcOfCircle CenterX=-155.157 CenterY=23.3323 CenterZ=0 NormalX=0 NormalY=0 NormalZ=1 AngleXU=0 Radius=6.92354 StartAngle=1.03434 EndAngle=5.24885
    g8: ArcOfCircle CenterX=-155.157 CenterY=23.3323 CenterZ=0 NormalX=0 NormalY=0 NormalZ=1 AngleXU=0 Radius=12.6269 StartAngle=1.28675 EndAngle=4.99643
    g9: LineSegment StartX=-151.619 StartY=35.4532 StartZ=0 EndX=-151.619 EndY=29.2832 EndZ=0
    g10: LineSegment StartX=-151.619 StartY=17.3813 StartZ=0 EndX=-151.619 EndY=11.2113 EndZ=0
    g11-g21: Circle x11 (B-spline internal-alignment scaffolding for g22; pole/knot coordinates omitted)
    g22: BSplineCurve PolesCount=11 KnotsCount=9 Degree=3 IsPeriodic=0
    g23-g31: GeomPoint x9 (B-spline internal-alignment scaffolding for g22; pole/knot coordinates omitted)
    g32-g49: Circle x18 (B-spline internal-alignment scaffolding for g50; pole/knot coordinates omitted)
    g50: BSplineCurve PolesCount=18 KnotsCount=16 Degree=3 IsPeriodic=0
    g51-g66: GeomPoint x16 (B-spline internal-alignment scaffolding for g50; pole/knot coordinates omitted)
    g67: LineSegment StartX=-117.124 StartY=30.093 StartZ=0 EndX=-117.603 EndY=26.5272 EndZ=0
    g68: LineSegment StartX=-117.603 StartY=17.8472 StartZ=0 EndX=-117.124 EndY=14.2659 EndZ=0
    g69: Ellipse CenterX=-109.671 CenterY=20.025 CenterZ=0 NormalX=0 NormalY=0 NormalZ=1 MajorRadius=3.34798 MinorRadius=2.71052 AngleXU=-1.56793
    g70: GeomPoint X=-109.666 Y=18.0598 Z=0
    g71: GeomPoint X=-109.677 Y=21.9902 Z=0
    g72: Ellipse CenterX=-109.671 CenterY=20.0123 CenterZ=0 NormalX=0 NormalY=0 NormalZ=1 MajorRadius=6.93002 MinorRadius=6.36273 AngleXU=-3.13976
    g73: GeomPoint X=-112.417 Y=20.0073 Z=0
    g74: GeomPoint X=-106.925 Y=20.0173 Z=0
    g75: Ellipse CenterX=-51.7682 CenterY=20.1463 CenterZ=0 NormalX=0 NormalY=0 NormalZ=1 MajorRadius=3.19279 MinorRadius=2.71052 AngleXU=-1.52774
    g76: GeomPoint X=-51.6955 Y=18.4606 Z=0
    g77: GeomPoint X=-51.8408 Y=21.832 Z=0
    g78: GeomPoint X=-54.5142 Y=20.1413 Z=0
    g79: GeomPoint X=-49.0221 Y=20.1513 Z=0
    g80: Ellipse CenterX=-51.7682 CenterY=20.1463 CenterZ=0 NormalX=0 NormalY=0 NormalZ=1 MajorRadius=6.93002 MinorRadius=6.36273 AngleXU=-3.13976
    g81: Ellipse CenterX=-22.8436 CenterY=20.1783 CenterZ=0 NormalX=0 NormalY=0 NormalZ=1 MajorRadius=3.31512 MinorRadius=2.71052 AngleXU=-1.60214
    g82: GeomPoint X=-22.9034 Y=18.2706 Z=0
    g83: GeomPoint X=-22.7838 Y=22.0861 Z=0
    g84: GeomPoint X=-25.5897 Y=20.1733 Z=0
    g85: GeomPoint X=-20.0976 Y=20.1833 Z=0
    g86: Ellipse CenterX=-22.8436 CenterY=20.1783 CenterZ=0 NormalX=0 NormalY=0 NormalZ=1 MajorRadius=6.93002 MinorRadius=6.36273 AngleXU=-3.13976
    g87: LineSegment StartX=-101.889 StartY=14.1107 StartZ=0 EndX=-97.7455 EndY=14.1107 EndZ=0
    g88: LineSegment StartX=-93.8155 StartY=14.1107 StartZ=0 EndX=-89.6755 EndY=14.1107 EndZ=0
    g89: LineSegment StartX=-85.7455 StartY=14.1107 StartZ=0 EndX=-81.6055 EndY=14.1107 EndZ=0
    g90: LineSegment StartX=-101.889 StartY=14.1107 StartZ=0 EndX=-101.889 EndY=25.9907 EndZ=0
    g91: LineSegment StartX=-101.889 StartY=25.9907 StartZ=0 EndX=-97.8594 EndY=25.9907 EndZ=0
    g92: LineSegment StartX=-97.8594 StartY=25.9907 StartZ=0 EndX=-97.8594 EndY=24.0907 EndZ=0
    g93: LineSegment StartX=-97.7455 StartY=14.1107 StartZ=0 EndX=-97.7455 EndY=19.9107 EndZ=0
    g94: LineSegment StartX=-89.6755 StartY=14.1107 StartZ=0 EndX=-89.6755 EndY=19.9107 EndZ=0
    g95: LineSegment StartX=-93.8155 StartY=14.1107 StartZ=0 EndX=-93.8155 EndY=21.0107 EndZ=0
    g96-g106: Circle x11 (B-spline internal-alignment scaffolding for g107; pole/knot coordinates omitted)
    g107: BSplineCurve PolesCount=11 KnotsCount=9 Degree=3 IsPeriodic=0
    g108-g116: GeomPoint x9 (B-spline internal-alignment scaffolding for g107; pole/knot coordinates omitted)
    g117: BSplineCurve PolesCount=11 KnotsCount=9 Degree=3 IsPeriodic=0
    g118-g125: Circle x8 (B-spline internal-alignment scaffolding for g126; pole/knot coordinates omitted)
    g126: BSplineCurve PolesCount=8 KnotsCount=6 Degree=3 IsPeriodic=0
    g127-g132: GeomPoint x6 (B-spline internal-alignment scaffolding for g126; pole/knot coordinates omitted)
    g133: BSplineCurve PolesCount=8 KnotsCount=6 Degree=3 IsPeriodic=0
    g134: LineSegment StartX=-85.7455 StartY=21.0107 StartZ=0 EndX=-85.7455 EndY=14.1107 EndZ=0
    g135: LineSegment StartX=-80.0879 StartY=14.1107 StartZ=0 EndX=-75.944 EndY=14.1107 EndZ=0
    g136: LineSegment StartX=-72.014 StartY=14.1107 StartZ=0 EndX=-67.874 EndY=14.1107 EndZ=0
    g137: LineSegment StartX=-63.944 StartY=14.1107 StartZ=0 EndX=-59.804 EndY=14.1107 EndZ=0
    g138: LineSegment StartX=-80.0879 StartY=14.1107 StartZ=0 EndX=-80.0879 EndY=25.9907 EndZ=0
    g139: LineSegment StartX=-80.0879 StartY=25.9907 StartZ=0 EndX=-76.0579 EndY=25.9907 EndZ=0
    g140: LineSegment StartX=-76.0579 StartY=25.9907 StartZ=0 EndX=-76.0579 EndY=24.0907 EndZ=0
    g141: LineSegment StartX=-75.944 StartY=14.1107 StartZ=0 EndX=-75.944 EndY=19.9107 EndZ=0
    g142: LineSegment StartX=-67.874 StartY=14.1107 StartZ=0 EndX=-67.874 EndY=19.9107 EndZ=0
    g143: LineSegment StartX=-72.014 StartY=14.1107 StartZ=0 EndX=-72.014 EndY=21.0107 EndZ=0
    g144-g148: Circle x5 (B-spline internal-alignment scaffolding for g149; pole/knot coordinates omitted)
    g149: BSplineCurve PolesCount=11 KnotsCount=9 Degree=3 IsPeriodic=0
    g150-g158: GeomPoint x9 (B-spline internal-alignment scaffolding for g149; pole/knot coordinates omitted)
    g159: BSplineCurve PolesCount=11 KnotsCount=9 Degree=3 IsPeriodic=0
    g160-g167: Circle x8 (B-spline internal-alignment scaffolding for g168; pole/knot coordinates omitted)
    g168: BSplineCurve PolesCount=8 KnotsCount=6 Degree=3 IsPeriodic=0
    g169-g174: GeomPoint x6 (B-spline internal-alignment scaffolding for g168; pole/knot coordinates omitted)
    g175: BSplineCurve PolesCount=8 KnotsCount=6 Degree=3 IsPeriodic=0
    g176: LineSegment StartX=-63.944 StartY=21.0107 StartZ=0 EndX=-63.944 EndY=14.1107 EndZ=0
    g177: LineSegment StartX=-59.804 StartY=14.1107 StartZ=0 EndX=-59.804 EndY=21.5868 EndZ=0
    g178: BSplineCurve PolesCount=4 KnotsCount=2 Degree=3 IsPeriodic=0
    g179: GeomPoint X=-59.804 Y=21.5868 Z=0
    g180: GeomPoint X=-60.2379 Y=24.0907 Z=0
    g181: LineSegment StartX=-81.6055 StartY=14.1107 StartZ=0 EndX=-81.6055 EndY=21.5868 EndZ=0
    g182: LineSegment StartX=-151.619 StartY=24.0313 StartZ=0 EndX=-145.128 EndY=24.0313 EndZ=0
    g183: Circle CenterX=-82.0394 CenterY=24.0907 CenterZ=0 NormalX=0 NormalY=0 NormalZ=1 AngleXU=0 Radius=1
    g184: Circle CenterX=-81.7131 CenterY=23.2736 CenterZ=0 NormalX=0 NormalY=0 NormalZ=1 AngleXU=0 Radius=1
    g185: Circle CenterX=-81.6055 CenterY=21.5868 CenterZ=0 NormalX=0 NormalY=0 NormalZ=1 AngleXU=0 Radius=1
    g186: BSplineCurve PolesCount=3 KnotsCount=2 Degree=2 IsPeriodic=0
    g187: GeomPoint X=-82.0394 Y=24.0907 Z=0
    g188: GeomPoint X=-81.6055 Y=21.5868 Z=0
    g189: Ellipse CenterX=-37.3522 CenterY=19.9515 CenterZ=0 NormalX=0 NormalY=0 NormalZ=1 MajorRadius=2.99755 MinorRadius=2.49 AngleXU=1.5708
    g190: GeomPoint X=-37.3522 Y=21.6203 Z=0
    g191: GeomPoint X=-37.3522 Y=18.2826 Z=0
    g192: ArcOfEllipse CenterX=-38.7647 CenterY=20.06 CenterZ=0 NormalX=0 NormalY=0 NormalZ=1 MajorRadius=6.30025 MinorRadius=5.3849 AngleXU=1.57276 StartAngle=5.50632 EndAngle=10.3035
    g193: GeomPoint X=-38.7711 Y=23.3304 Z=0
    g194: GeomPoint X=-38.7583 Y=16.7895 Z=0
    g195: LineSegment StartX=-34.6109 StartY=14.1107 StartZ=0 EndX=-30.8984 EndY=14.1107 EndZ=0
    g196: LineSegment StartX=-30.8984 StartY=14.1107 StartZ=0 EndX=-30.8984 EndY=31.1784 EndZ=0
    g197: LineSegment StartX=-30.8984 StartY=31.1784 StartZ=0 EndX=-34.9984 EndY=31.1784 EndZ=0
    g198: LineSegment StartX=-34.9984 StartY=24.5602 StartZ=0 EndX=-34.9984 EndY=31.1784 EndZ=0
    g199: LineSegment StartX=-34.6109 StartY=16.0476 StartZ=0 EndX=-34.6109 EndY=14.1107 EndZ=0
    g200: LineSegment StartX=-14.8781 StartY=14.1107 StartZ=0 EndX=-10.5106 EndY=14.1107 EndZ=0
    g201: LineSegment StartX=-14.8781 StartY=14.1107 StartZ=0 EndX=-14.8781 EndY=25.8504 EndZ=0
    g202: LineSegment StartX=-14.8781 StartY=25.8504 StartZ=0 EndX=-10.8534 EndY=25.8504 EndZ=0
    g203: LineSegment StartX=-10.8534 StartY=25.8504 StartZ=0 EndX=-10.8534 EndY=24.0923 EndZ=0
    g204: LineSegment StartX=-10.5106 StartY=14.1107 StartZ=0 EndX=-10.5106 EndY=19.7752 EndZ=0
    g205: LineSegment StartX=-5.96397 StartY=25.9304 StartZ=0 EndX=-5.96397 EndY=22.574 EndZ=0
    g206-g214: Circle x9 (B-spline internal-alignment scaffolding for g215; pole/knot coordinates omitted)
    g215: BSplineCurve PolesCount=9 KnotsCount=7 Degree=3 IsPeriodic=0
    g216-g222: GeomPoint x7 (B-spline internal-alignment scaffolding for g215; pole/knot coordinates omitted)
    g223-g232: Circle x10 (B-spline internal-alignment scaffolding for g233; pole/knot coordinates omitted)
    g233: BSplineCurve PolesCount=10 KnotsCount=8 Degree=3 IsPeriodic=0
    g234-g241: GeomPoint x8 (B-spline internal-alignment scaffolding for g233; pole/knot coordinates omitted)
    g242: LineSegment StartX=-1.58923 StartY=21.0696 StartZ=0 EndX=2.62034 EndY=21.0696 EndZ=0
    g243: LineSegment StartX=-1.55856 StartY=18.7342 StartZ=0 EndX=6.45946 EndY=18.7342 EndZ=0
    g244: LineSegment StartX=5.29231 StartY=17.386 StartZ=0 EndX=5.29231 EndY=14.3674 EndZ=0
    g245-g269: Circle x25 (B-spline internal-alignment scaffolding for g270; pole/knot coordinates omitted)
    g270: BSplineCurve PolesCount=25 KnotsCount=23 Degree=3 IsPeriodic=0
    g271-g293: GeomPoint x23 (B-spline internal-alignment scaffolding for g270; pole/knot coordinates omitted)
    g294-g304: Circle x11 (B-spline internal-alignment scaffolding for g305; pole/knot coordinates omitted)
    g305: BSplineCurve PolesCount=11 KnotsCount=9 Degree=3 IsPeriodic=0
    g306-g314: GeomPoint x9 (B-spline internal-alignment scaffolding for g305; pole/knot coordinates omitted)
    g315-g326: Circle x12 (B-spline internal-alignment scaffolding for g327; pole/knot coordinates omitted)
    g327: BSplineCurve PolesCount=12 KnotsCount=10 Degree=3 IsPeriodic=0
    g328-g337: GeomPoint x10 (B-spline internal-alignment scaffolding for g327; pole/knot coordinates omitted)
  constraints (252):
    c: Coincident(g1,g0)
    c: Horizontal(g0)
    c: Vertical(g1)
    c: Coincident(g2,g3)
    c: Coincident(g3,g4)
    c: Horizontal(g4)
    c: Horizontal(g2)
    c: Vertical(g3)
    c: Block(g1)
    c: Distance(g3) = 4.86
    c: Block(g4)
    c: Distance(g0) = 10.8
    c: Distance(g2) = 10.8
    c: Coincident(g5,g0)
    c: Coincident(g6,g4)
    c: Coincident(g6,g2)
    c: Block(g8)
    c: Block(g7)
    c: Coincident(g9,g8)
    c: Coincident(g9,g7)
    c: Vertical(g9)
    c: Coincident(g10,g7)
    c: Coincident(g10,g8)
    c: Vertical(g10)
    c: Weight(g11) = 1
    c: Equal(g11, g12-g21) x10
    c: InternalAlignment(g11-g21 -> g22) x11
    c: InternalAlignment(g23-g31 -> g22) x9
    c: Block(g22)
    c: Weight(g32) = 1
    c: Equal(g32, g33-g49) x17
    c: InternalAlignment(g32-g49 -> g50) x18
    c: InternalAlignment(g51-g66 -> g50) x16
    c: Block(g50)
    c: Coincident(g67,g50)
    c: Coincident(g67,g22)
    c: Coincident(g68,g22)
    c: Coincident(g68,g50)
    c: InternalAlignment(g70,g69)
    c: InternalAlignment(g71,g69)
    c: Block(g69)
    c: InternalAlignment(g73,g72)
    c: InternalAlignment(g74,g72)
    c: Block(g72)
    c: InternalAlignment(g76,g75)
    c: InternalAlignment(g77,g75)
    c: InternalAlignment(g78,g80)
    c: InternalAlignment(g79,g80)
    c: Block(g80)
    c: Coincident(g75,g80)
    c: Block(g75)
    c: InternalAlignment(g82,g81)
    c: InternalAlignment(g83,g81)
    c: InternalAlignment(g84,g86)
    c: InternalAlignment(g85,g86)
    c: Block(g86)
    c: Coincident(g81,g86)
    c: Block(g81)
    c: Horizontal(g87)
    c: Block(g87)
    c: Horizontal(g88)
    c: Distance(g88) = 4.14
    c: Horizontal(g89)
    c: Equal(g88,g89) = 4.14
    c: Block(g89)
    c: Block(g88)
    c: Coincident(g90,g87)
    c: Vertical(g90)
    c: Distance(g90) = 11.88
    c: Coincident(g91,g90)
    c: Horizontal(g91)
    c: Coincident(g92,g91)
    c: Vertical(g92)
    c: Distance(g91) = 4.03
    c: Distance(g92) = 1.9
    c: Coincident(g93,g87)
    c: Vertical(g93)
    c: Vertical(g94)
    c: Coincident(g94,g88)
    c: Distance(g93) = 5.8
    c: Distance(g94) = 5.8
    c: Vertical(g95)
    c: Coincident(g95,g88)
    c: Distance(g95) = 6.9
    c: Coincident(g107,g92)
    c: Weight(g96) = 1
    c: Equal(g96, g97-g106) x10
    c: InternalAlignment(g96-g106 -> g107) x11
    c: InternalAlignment(g108-g116 -> g107) x9
    c: Block(g107)
    c: Block(g117)
    c: Coincident(g126,g93)
    c: Weight(g118) = 1
    c: Equal(g118, g119-g125) x7
    c: Coincident(g126,g95)
    c: InternalAlignment(g118-g125 -> g126) x8
    c: InternalAlignment(g127-g132 -> g126) x6
    c: Coincident(g133,g94)
    c: Block(g126)
    c: Block(g133)
    c: Coincident(g134,g133)
    c: Coincident(g134,g89)
    c: Vertical(g134)
    c: Horizontal(g135)
    c: Block(g135)
    c: Horizontal(g136)
    c: Equal(g88,g136) = 4.14
    c: Horizontal(g137)
    c: Equal(g136,g137) = 4.14
    c: Block(g137)
    c: Block(g136)
    c: Coincident(g138,g135)
    c: Vertical(g138)
    c: Equal(g90,g138) = 11.88
    c: Coincident(g139,g138)
    c: Horizontal(g139)
    c: Coincident(g140,g139)
    c: Vertical(g140)
    c: Equal(g91,g139) = 4.03
    c: Equal(g92,g140) = 1.9
    c: Coincident(g141,g135)
    c: Vertical(g141)
    c: Vertical(g142)
    c: Coincident(g142,g136)
    c: Equal(g93,g141) = 5.8
    c: Equal(g94,g142) = 5.8
    c: Vertical(g143)
    c: Coincident(g143,g136)
    c: Equal(g95,g143) = 6.9
    c: Coincident(g149,g140)
    c: Equal(g96,g144) = 1
    c: Equal(g144, g145-g148) x4
    c: InternalAlignment(g144-g148 -> g149) x5
    c: InternalAlignment(g150-g158 -> g149) x9
    c: Block(g149)
    c: Block(g159)
    c: Coincident(g168,g141)
    c: Equal(g118,g160) = 1
    c: Equal(g160, g161-g167) x7
    c: Coincident(g168,g143)
    c: InternalAlignment(g160-g167 -> g168) x8
    c: InternalAlignment(g169-g174 -> g168) x6
    c: Coincident(g175,g142)
    c: Block(g168)
    c: Block(g175)
    c: Coincident(g176,g175)
    c: Coincident(g176,g137)
    c: Vertical(g176)
    c: Coincident(g177,g137)
    c: Vertical(g177)
    c: Coincident(g178,g177)
    c: Coincident(g178,g159)
    c: InternalAlignment(g179,g178)
    c: InternalAlignment(g180,g178)
    c: Block(g178)
    c: Vertical(g181)
    c: Coincident(g181,g89)
    c: Block(g5)
    c: Coincident(g182,g1)
    c: Coincident(g182,g5)
    c: Horizontal(g182)
    c: Coincident(g186,g117)
    c: Weight(g183) = 1
    c: Equal(g183,g184)
    c: Equal(g183,g185)
    c: Coincident(g186,g181)
    c: InternalAlignment(g183,g186)
    c: InternalAlignment(g184,g186)
    c: InternalAlignment(g185,g186)
    c: InternalAlignment(g187,g186)
    c: InternalAlignment(g188,g186)
    c: Block(g186)
    c: InternalAlignment(g190,g189)
    c: InternalAlignment(g191,g189)
    c: Block(g189)
    c: InternalAlignment(g193,g192)
    c: InternalAlignment(g194,g192)
    c: Block(g192)
    c: Horizontal(g195)
    c: Block(g195)
    c: Coincident(g196,g195)
    c: Vertical(g196)
    c: Block(g196)
    c: Distance(g195) = 3.71244
    c: Coincident(g197,g196)
    c: Horizontal(g197)
    c: Distance(g197) = 4.1
    c: Coincident(g198,g192)
    c: Coincident(g198,g197)
    c: Vertical(g198)
    c: Block(g198)
    c: Coincident(g199,g192)
    c: Coincident(g199,g195)
    c: Vertical(g199)
    c: Block(g199)
    c: Horizontal(g200)
    c: Block(g200)
    c: Coincident(g201,g200)
    c: Vertical(g201)
    c: Block(g201)
    c: Coincident(g202,g201)
    c: Horizontal(g202)
    c: Block(g202)
    c: Coincident(g203,g202)
    c: Vertical(g203)
    c: Block(g203)
    c: Coincident(g204,g200)
    c: Vertical(g204)
    c: Block(g204)
    c: Coincident(g215,g203)
    c: Weight(g206) = 1
    c: Equal(g206, g207-g214) x8
    c: Coincident(g215,g205)
    c: InternalAlignment(g206-g214 -> g215) x9
    c: InternalAlignment(g216-g222 -> g215) x7
    c: Coincident(g233,g204)
    c: Weight(g223) = 1
    c: Equal(g223, g224-g232) x9
    c: Coincident(g233,g205)
    c: InternalAlignment(g223-g232 -> g233) x10
    c: InternalAlignment(g234-g241 -> g233) x8
    c: Vertical(g205)
    c: Block(g205)
    c: Block(g215)
    c: Block(g233)
    c: Horizontal(g242)
    c: Horizontal(g243)
    c: Block(g242)
    c: Block(g243)
    c: Vertical(g244)
    c: Block(g244)
    c: Coincident(g270,g243)
    c: Weight(g245) = 1
    c: Equal(g245, g246-g269) x24
    c: Coincident(g270,g244)
    c: InternalAlignment(g245-g269 -> g270) x25
    c: InternalAlignment(g271-g293 -> g270) x23
    c: Coincident(g305,g242)
    c: Weight(g294) = 1
    c: Equal(g294, g295-g304) x10
    c: Coincident(g305,g242)
    c: InternalAlignment(g294-g304 -> g305) x11
    c: InternalAlignment(g306-g314 -> g305) x9
    c: Block(g305)
    c: Coincident(g327,g243)
    c: Weight(g315) = 1
    c: Equal(g315, g316-g326) x11
    c: Coincident(g327,g244)
    c: InternalAlignment(g315-g326 -> g327) x12
    c: InternalAlignment(g328-g337 -> g327) x10
    c: Block(g327)
    c: Block(g270)
FEATURE [Part::Extrusion] Extrude075  label="CommodoreLogoAndText002"
  Base = -> Sketch084
  Dir = (0,0,1)
  DirMode = 2
  FaceMakerClass = Part::FaceMakerBullseye
  LengthFwd = 10
  LengthRev = 0
  Solid = true
  Symmetric = false
FEATURE [Part::FeaturePython] Clone001  label="CommodoreLogoAndTextScale001"  # Draft clone (typed FeaturePython)
  AttacherType = Attacher::AttachEngine3D
  Fuse = false
  Objects = -> [Extrude075]
  Placement = pos=(112.566,5.37,73.6) rot=(0,0,1;0rad)
  Scale = (0.62,0.62,1)
FEATURE [Part::Cut] Cut073  label="sideA005"
  Base = -> Extrude002
  Tool = -> Part__Mirroring
FEATURE [Part::Cut] Cut074  label="sideB005"
  Base = -> Extrude028
  Tool = -> Clone001
FEATURE [Sketcher::SketchObject] Sketch085
  FullyConstrained = true
  Placement = pos=(0,0,0) rot=(-1,0,0;4.71239rad)
  sketch-geometry (10):
    g0: LineSegment StartX=0 StartY=0 StartZ=0 EndX=-7 EndY=0 EndZ=0
    g1: LineSegment StartX=-7 StartY=10 StartZ=0 EndX=-6.5 EndY=10 EndZ=0
    g2: LineSegment StartX=0 StartY=10 StartZ=0 EndX=-0.5 EndY=10 EndZ=0
    g3: ArcOfCircle CenterX=-3.5 CenterY=10 CenterZ=0 NormalX=0 NormalY=0 NormalZ=1 AngleXU=0 Radius=3 StartAngle=3.14159 EndAngle=6.28319
    g4: LineSegment StartX=-7 StartY=0 StartZ=0 EndX=-10.5 EndY=0 EndZ=0
    g5: LineSegment StartX=0 StartY=0 StartZ=0 EndX=3.5 EndY=0 EndZ=0
    g6: ArcOfCircle CenterX=-10.5 CenterY=3.5 CenterZ=0 NormalX=0 NormalY=0 NormalZ=1 AngleXU=0 Radius=3.5 StartAngle=4.71239 EndAngle=6.28319
    g7: ArcOfCircle CenterX=3.5 CenterY=3.5 CenterZ=0 NormalX=0 NormalY=0 NormalZ=1 AngleXU=0 Radius=3.5 StartAngle=3.14159 EndAngle=4.71239
    g8: LineSegment StartX=-7 StartY=3.5 StartZ=0 EndX=-7 EndY=10 EndZ=0
    g9: LineSegment StartX=0 StartY=10 StartZ=0 EndX=0 EndY=3.5 EndZ=0
  constraints (26):
    c: Coincident(g0,g-1)
    c: Horizontal(g0)
    c: Distance(g0) = 7
    c: Horizontal(g1)
    c: Distance(g1) = 0.5
    c: Horizontal(g2)
    c: Distance(g2) = 0.5
    c: Coincident(g3,g1)
    c: Coincident(g3,g2)
    c: Block(g3)
    c: Coincident(g4,g0)
    c: Horizontal(g4)
    c: Distance(g4) = 3.5
    c: Coincident(g5,g0)
    c: Distance(g5) = 3.5
    c: Horizontal(g5)
    c: Coincident(g6,g4)
    c: Block(g6)
    c: Coincident(g7,g5)
    c: Block(g7)
    c: Coincident(g8,g6)
    c: Coincident(g8,g1)
    c: Vertical(g8)
    c: Coincident(g9,g2)
    c: Coincident(g9,g7)
    c: Vertical(g9)
FEATURE [Part::Extrusion] Extrude076  label="backRightCasePillarSideBracket"
  Base = -> Sketch085
  Dir = (0,-1,3e-16)
  DirMode = 2
  FaceMakerClass = Part::FaceMakerBullseye
  LengthFwd = 6.7
  LengthRev = 0
  Placement = pos=(16,11.5,0) rot=(0,0,1;0rad)
  Solid = true
  Symmetric = false
FEATURE [Sketcher::SketchObject] Sketch086
  FullyConstrained = true
  Placement = pos=(0,0,0) rot=(1,0,0;1.5708rad)
  sketch-geometry (10):
    g0: LineSegment StartX=0 StartY=0 StartZ=0 EndX=-7 EndY=0 EndZ=0
    g1: LineSegment StartX=-7 StartY=10 StartZ=0 EndX=-6.5 EndY=10 EndZ=0
    g2: LineSegment StartX=0 StartY=10 StartZ=0 EndX=-0.5 EndY=10 EndZ=0
    g3: ArcOfCircle CenterX=-3.5 CenterY=10 CenterZ=0 NormalX=0 NormalY=0 NormalZ=1 AngleXU=0 Radius=3 StartAngle=3.14159 EndAngle=6.28319
    g4: LineSegment StartX=-7 StartY=0 StartZ=0 EndX=-10.5 EndY=0 EndZ=0
    g5: LineSegment StartX=0 StartY=0 StartZ=0 EndX=3.5 EndY=0 EndZ=0
    g6: ArcOfCircle CenterX=-10.5 CenterY=3.5 CenterZ=0 NormalX=0 NormalY=0 NormalZ=1 AngleXU=0 Radius=3.5 StartAngle=4.71239 EndAngle=6.28319
    g7: ArcOfCircle CenterX=3.5 CenterY=3.5 CenterZ=0 NormalX=0 NormalY=0 NormalZ=1 AngleXU=0 Radius=3.5 StartAngle=3.14159 EndAngle=4.71239
    g8: LineSegment StartX=-7 StartY=3.5 StartZ=0 EndX=-7 EndY=10 EndZ=0
    g9: LineSegment StartX=0 StartY=10 StartZ=0 EndX=0 EndY=3.5 EndZ=0
  constraints (26):
    c: Coincident(g0,g-1)
    c: Horizontal(g0)
    c: Distance(g0) = 7
    c: Horizontal(g1)
    c: Distance(g1) = 0.5
    c: Horizontal(g2)
    c: Distance(g2) = 0.5
    c: Coincident(g3,g1)
    c: Coincident(g3,g2)
    c: Block(g3)
    c: Coincident(g4,g0)
    c: Horizontal(g4)
    c: Distance(g4) = 3.5
    c: Coincident(g5,g0)
    c: Distance(g5) = 3.5
    c: Horizontal(g5)
    c: Coincident(g6,g4)
    c: Block(g6)
    c: Coincident(g7,g5)
    c: Block(g7)
    c: Coincident(g8,g6)
    c: Coincident(g8,g1)
    c: Vertical(g8)
    c: Coincident(g9,g2)
    c: Coincident(g9,g7)
    c: Vertical(g9)
FEATURE [Part::Extrusion] Extrude077  label="backLeftCasePillarSideBracket001"
  Base = -> Sketch086
  Dir = (0,-1,3e-16)
  DirMode = 2
  FaceMakerClass = Part::FaceMakerBullseye
  LengthFwd = 6.7
  LengthRev = 0
  Placement = pos=(9,11.5,72) rot=(0,1,0;3.14159rad)
  Solid = true
  Symmetric = false
FEATURE [Sketcher::SketchObject] Sketch087
  FullyConstrained = true
  Placement = pos=(0,0,0) rot=(1,0,0;1.5708rad)
  sketch-geometry (8):
    g0: LineSegment StartX=0 StartY=4e-16 StartZ=0 EndX=-7 EndY=4e-16 EndZ=0
    g1: LineSegment StartX=-7 StartY=4e-16 StartZ=0 EndX=-10.5 EndY=4e-16 EndZ=0
    g2: LineSegment StartX=0 StartY=4e-16 StartZ=0 EndX=3.5 EndY=4e-16 EndZ=0
    g3: ArcOfCircle CenterX=-10.5 CenterY=3.5 CenterZ=0 NormalX=0 NormalY=0 NormalZ=1 AngleXU=0 Radius=3.5 StartAngle=4.71239 EndAngle=6.28319
    g4: ArcOfCircle CenterX=3.5 CenterY=3.5 CenterZ=0 NormalX=0 NormalY=0 NormalZ=1 AngleXU=0 Radius=3.5 StartAngle=3.14159 EndAngle=4.71239
    g5: ArcOfCircle CenterX=-3.5 CenterY=3.5 CenterZ=0 NormalX=0 NormalY=0 NormalZ=1 AngleXU=0 Radius=3 StartAngle=3.14159 EndAngle=6.28319
    g6: LineSegment StartX=-7 StartY=3.5 StartZ=0 EndX=-6.5 EndY=3.5 EndZ=0
    g7: LineSegment StartX=-0.5 StartY=3.5 StartZ=0 EndX=0 EndY=3.5 EndZ=0
  constraints (20):
    c: Coincident(g0,g-1)
    c: Horizontal(g0)
    c: Distance(g0) = 7
    c: Coincident(g1,g0)
    c: Horizontal(g1)
    c: Distance(g1) = 3.5
    c: Coincident(g2,g0)
    c: Distance(g2) = 3.5
    c: Horizontal(g2)
    c: Coincident(g3,g1)
    c: Block(g3)
    c: Coincident(g4,g2)
    c: Block(g4)
    c: Horizontal(g6)
    c: Coincident(g5,g6)
    c: Block(g5)
    c: Coincident(g6,g3)
    c: Coincident(g7,g5)
    c: Coincident(g7,g4)
    c: Horizontal(g7)
FEATURE [Part::Extrusion] Extrude078
  Base = -> Sketch087
  Dir = (0,-1,2e-16)
  DirMode = 2
  FaceMakerClass = Part::FaceMakerBullseye
  LengthFwd = 6.7
  LengthRev = 0
  Solid = true
  Symmetric = false
